FCSTD DOCUMENT  (FreeCAD 1.0RUnknown)
Label: circumlocution
License: All rights reserved
LicenseURL: http://en.wikipedia.org/wiki/All_rights_reserved
objects: Part::Feature×459, Sketcher::SketchObject×126, App::Part×76, PartDesign::Pad×49, PartDesign::Pocket×37, Part::FeaturePython×31, PartDesign::Hole×30, PartDesign::Body×27, Part::Extrusion×10, PartDesign::CoordinateSystem×4, PartDesign::ShapeBinder×2, PartDesign::Mirrored×2, Part::Cut×2, Part::Fuse×1, PartDesign::Fillet×1, Part::Mirroring×1, Part::MultiFuse×1
note: 1145 computed .brp shape members not serialized (recipe doc carries the construction recipe); baked Part::Feature solids carry a one-line shape summary decoded from their .brp

FEATURE [Sketcher::SketchObject] Sketch  label="2020LinearExtrusion"
  ArcFitTolerance = 1e-06
  FullyConstrained = true
  MakeInternals = false
  Placement = pos=(0,0,0) rot=(0,0,1;1.5708rad)
  sketch-geometry (115):
    g0: GeomPoint [constr] X=0 Y=0 Z=0
    g1: ArcOfCircle CenterX=-8.5 CenterY=8.5 CenterZ=0 NormalX=0 NormalY=0 NormalZ=1 AngleXU=0 Radius=1.5 StartAngle=1.5708 EndAngle=3.14159
    g2: GeomPoint [constr] X=-10 Y=10 Z=0
    g3: ArcOfCircle CenterX=-8.5 CenterY=-8.5 CenterZ=0 NormalX=0 NormalY=0 NormalZ=1 AngleXU=0 Radius=1.5 StartAngle=3.14159 EndAngle=4.71239
    g4: GeomPoint [constr] X=-10 Y=-10 Z=0
    g5: ArcOfCircle CenterX=8.5 CenterY=-8.5 CenterZ=0 NormalX=0 NormalY=0 NormalZ=1 AngleXU=0 Radius=1.5 StartAngle=4.71239 EndAngle=6.28319
    g6: GeomPoint [constr] X=10 Y=-10 Z=0
    g7: ArcOfCircle CenterX=8.5 CenterY=8.5 CenterZ=0 NormalX=0 NormalY=0 NormalZ=1 AngleXU=0 Radius=1.5 StartAngle=0 EndAngle=1.5708
    g8: GeomPoint [constr] X=10 Y=10 Z=0
    g9: ArcOfCircle CenterX=0 CenterY=0 CenterZ=0 NormalX=0 NormalY=0 NormalZ=1 AngleXU=0 Radius=2.75 StartAngle=5.79106 EndAngle=6.77531
    g10: LineSegment StartX=1.88798 StartY=-3.01227 StartZ=0 EndX=3.01227 EndY=-1.88798 EndZ=0
    g11: LineSegment StartX=3.01227 StartY=-1.88798 StartZ=0 EndX=2.42366 EndY=-1.29936 EndZ=0
    g12: LineSegment StartX=-1.88798 StartY=3.01227 StartZ=0 EndX=-3.01227 EndY=1.88798 EndZ=0
    g13: LineSegment StartX=-3.01227 StartY=1.88798 StartZ=0 EndX=-2.42366 EndY=1.29936 EndZ=0
    g14: GeomPoint [constr] X=0 Y=0 Z=0
    g15: LineSegment StartX=-3.01227 StartY=-1.88798 StartZ=0 EndX=-1.88798 EndY=-3.01227 EndZ=0
    g16: LineSegment StartX=-1.88798 StartY=-3.01227 StartZ=0 EndX=-1.29936 EndY=-2.42366 EndZ=0
    g17: LineSegment StartX=3.01227 StartY=1.88798 StartZ=0 EndX=1.88798 EndY=3.01227 EndZ=0
    g18: LineSegment StartX=1.88798 StartY=3.01227 StartZ=0 EndX=1.29936 EndY=2.42366 EndZ=0
    g19: GeomPoint [constr] X=0 Y=0 Z=0
    g20: LineSegment StartX=-1.29936 StartY=2.42366 StartZ=0 EndX=-1.88798 EndY=3.01227 EndZ=0
    g21: LineSegment StartX=1.29936 StartY=-2.42366 StartZ=0 EndX=1.88798 EndY=-3.01227 EndZ=0
    g22: ArcOfCircle CenterX=0 CenterY=0 CenterZ=0 NormalX=0 NormalY=0 NormalZ=1 AngleXU=0 Radius=2.75 StartAngle=2.64947 EndAngle=3.63371
    g23: ArcOfCircle CenterX=0 CenterY=0 CenterZ=0 NormalX=0 NormalY=0 NormalZ=1 AngleXU=0 Radius=2.75 StartAngle=4.22027 EndAngle=5.20451
    g24: ArcOfCircle CenterX=0 CenterY=0 CenterZ=0 NormalX=0 NormalY=0 NormalZ=1 AngleXU=0 Radius=2.75 StartAngle=1.07868 EndAngle=2.06292
    g25: LineSegment StartX=-2.42366 StartY=-1.29936 StartZ=0 EndX=-3.01227 EndY=-1.88798 EndZ=0
    g26: LineSegment StartX=2.42366 StartY=1.29936 StartZ=0 EndX=3.01227 EndY=1.88798 EndZ=0
    g27: LineSegment [constr] StartX=-1.29936 StartY=2.42366 StartZ=0 EndX=2.42366 EndY=-1.29936 EndZ=0
    g28: LineSegment [constr] StartX=1.29936 StartY=-2.42366 StartZ=0 EndX=-2.42366 EndY=1.29936 EndZ=0
    g29: LineSegment [constr] StartX=-2.42366 StartY=-1.29936 StartZ=0 EndX=1.29936 EndY=2.42366 EndZ=0
    g30: LineSegment [constr] StartX=2.42366 StartY=1.29936 StartZ=0 EndX=-1.29936 EndY=-2.42366 EndZ=0
    g31: LineSegment StartX=-3.46967 StartY=-4.53033 StartZ=0 EndX=-0.800312 EndY=-4.53033 EndZ=0
    g32: LineSegment StartX=4.53033 StartY=-3.46967 StartZ=0 EndX=4.53033 EndY=-0.800312 EndZ=0
    g33: LineSegment StartX=3.46967 StartY=4.53033 StartZ=0 EndX=0.800312 EndY=4.53033 EndZ=0
    g34: LineSegment StartX=-4.53033 StartY=3.46967 StartZ=0 EndX=-4.53033 EndY=0.800312 EndZ=0
    g35: GeomPoint [constr] X=0 Y=0 Z=0
    g36: LineSegment StartX=-3.46967 StartY=4.53033 StartZ=0 EndX=-5.95 EndY=7.01066 EndZ=0
    g37: LineSegment StartX=-5.95 StartY=8.5 StartZ=0 EndX=-5.95 EndY=7.01066 EndZ=0
    g38: LineSegment StartX=-5.95 StartY=8.5 StartZ=0 EndX=-3 EndY=8.5 EndZ=0
    g39: LineSegment StartX=-3 StartY=8.5 StartZ=0 EndX=-3 EndY=9.5 EndZ=0
    g40: LineSegment StartX=-3 StartY=9.5 StartZ=0 EndX=-3.5 EndY=9.5 EndZ=0
    g41: LineSegment StartX=-3.5 StartY=9.5 StartZ=0 EndX=-3.5 EndY=10 EndZ=0
    g42: LineSegment StartX=-3.5 StartY=10 StartZ=0 EndX=-8.5 EndY=10 EndZ=0
    g43: ArcOfCircle CenterX=-4.75033 CenterY=0 CenterZ=0 NormalX=0 NormalY=0 NormalZ=1 AngleXU=0 Radius=0.83 StartAngle=4.98066 EndAngle=7.58572
    g44: LineSegment [constr] StartX=-4.75033 StartY=0 StartZ=0 EndX=-3.92033 EndY=0 EndZ=0
    g45: LineSegment StartX=-4.53033 StartY=-0.800312 StartZ=0 EndX=-4.53033 EndY=-3.46967 EndZ=0
    g46: LineSegment [constr] StartX=-4.53033 StartY=0.800312 StartZ=0 EndX=-4.53033 EndY=-0.800312 EndZ=0
    g47: LineSegment [constr] StartX=-10 StartY=10 StartZ=0 EndX=10 EndY=10 EndZ=0
    g48: LineSegment [constr] StartX=10 StartY=10 StartZ=0 EndX=10 EndY=-10 EndZ=0
    g49: LineSegment [constr] StartX=10 StartY=-10 StartZ=0 EndX=-10 EndY=-10 EndZ=0
    g50: LineSegment [constr] StartX=-10 StartY=-10 StartZ=0 EndX=-10 EndY=10 EndZ=0
    g51: LineSegment [constr] StartX=-8.5 StartY=8.5 StartZ=0 EndX=-10 EndY=8.5 EndZ=0
    g52: LineSegment [constr] StartX=-8.5 StartY=10 StartZ=0 EndX=-8.5 EndY=8.5 EndZ=0
    g53: LineSegment [constr] StartX=-10 StartY=10 StartZ=0 EndX=10 EndY=-10 EndZ=0
    g54: LineSegment [constr] StartX=10 StartY=10 StartZ=0 EndX=-10 EndY=-10 EndZ=0
    g55: LineSegment StartX=-10 StartY=3.5 StartZ=0 EndX=-10 EndY=8.5 EndZ=0
    g56: LineSegment StartX=-9.5 StartY=3.5 StartZ=0 EndX=-10 EndY=3.5 EndZ=0
    g57: LineSegment StartX=-9.5 StartY=3 StartZ=0 EndX=-9.5 EndY=3.5 EndZ=0
    g58: LineSegment StartX=-8.5 StartY=3 StartZ=0 EndX=-9.5 EndY=3 EndZ=0
    g59: LineSegment StartX=-8.5 StartY=5.95 StartZ=0 EndX=-8.5 EndY=3 EndZ=0
    g60: LineSegment StartX=-8.5 StartY=5.95 StartZ=0 EndX=-7.01066 EndY=5.95 EndZ=0
    g61: LineSegment StartX=-4.53033 StartY=3.46967 StartZ=0 EndX=-7.01066 EndY=5.95 EndZ=0
    g62: LineSegment StartX=3.5 StartY=10 StartZ=0 EndX=8.5 EndY=10 EndZ=0
    g63: LineSegment StartX=3.5 StartY=9.5 StartZ=0 EndX=3.5 EndY=10 EndZ=0
    g64: LineSegment StartX=3 StartY=8.5 StartZ=0 EndX=3 EndY=9.5 EndZ=0
    g65: LineSegment StartX=3 StartY=9.5 StartZ=0 EndX=3.5 EndY=9.5 EndZ=0
    g66: LineSegment StartX=5.95 StartY=8.5 StartZ=0 EndX=3 EndY=8.5 EndZ=0
    g67: LineSegment StartX=5.95 StartY=8.5 StartZ=0 EndX=5.95 EndY=7.01066 EndZ=0
    g68: LineSegment StartX=3.46967 StartY=4.53033 StartZ=0 EndX=5.95 EndY=7.01066 EndZ=0
    g69: LineSegment StartX=4.53033 StartY=3.46967 StartZ=0 EndX=7.01066 EndY=5.95 EndZ=0
    g70: LineSegment StartX=8.5 StartY=5.95 StartZ=0 EndX=7.01066 EndY=5.95 EndZ=0
    g71: LineSegment StartX=8.5 StartY=5.95 StartZ=0 EndX=8.5 EndY=3 EndZ=0
    g72: LineSegment StartX=8.5 StartY=3 StartZ=0 EndX=9.5 EndY=3 EndZ=0
    g73: LineSegment StartX=9.5 StartY=3 StartZ=0 EndX=9.5 EndY=3.5 EndZ=0
    g74: LineSegment StartX=9.5 StartY=3.5 StartZ=0 EndX=10 EndY=3.5 EndZ=0
    g75: LineSegment StartX=10 StartY=3.5 StartZ=0 EndX=10 EndY=8.5 EndZ=0
    g76: LineSegment StartX=-3.5 StartY=-10 StartZ=0 EndX=-8.5 EndY=-10 EndZ=0
    g77: LineSegment StartX=-3.5 StartY=-9.5 StartZ=0 EndX=-3.5 EndY=-10 EndZ=0
    g78: LineSegment StartX=-3 StartY=-9.5 StartZ=0 EndX=-3.5 EndY=-9.5 EndZ=0
    g79: LineSegment StartX=-3 StartY=-8.5 StartZ=0 EndX=-3 EndY=-9.5 EndZ=0
    g80: LineSegment StartX=-5.95 StartY=-8.5 StartZ=0 EndX=-3 EndY=-8.5 EndZ=0
    g81: LineSegment StartX=-5.95 StartY=-8.5 StartZ=0 EndX=-5.95 EndY=-7.01066 EndZ=0
    g82: LineSegment StartX=-3.46967 StartY=-4.53033 StartZ=0 EndX=-5.95 EndY=-7.01066 EndZ=0
    g83: LineSegment StartX=-4.53033 StartY=-3.46967 StartZ=0 EndX=-7.01066 EndY=-5.95 EndZ=0
    g84: LineSegment StartX=-8.5 StartY=-5.95 StartZ=0 EndX=-7.01066 EndY=-5.95 EndZ=0
    g85: LineSegment StartX=-8.5 StartY=-5.95 StartZ=0 EndX=-8.5 EndY=-3 EndZ=0
    g86: LineSegment StartX=-8.5 StartY=-3 StartZ=0 EndX=-9.5 EndY=-3 EndZ=0
    g87: LineSegment StartX=-9.5 StartY=-3 StartZ=0 EndX=-9.5 EndY=-3.5 EndZ=0
    g88: LineSegment StartX=-9.5 StartY=-3.5 StartZ=0 EndX=-10 EndY=-3.5 EndZ=0
    g89: LineSegment StartX=-10 StartY=-3.5 StartZ=0 EndX=-10 EndY=-8.5 EndZ=0
    g90: LineSegment StartX=3.5 StartY=-10 StartZ=0 EndX=8.5 EndY=-10 EndZ=0
    g91: LineSegment StartX=3.5 StartY=-9.5 StartZ=0 EndX=3.5 EndY=-10 EndZ=0
    g92: LineSegment StartX=3 StartY=-9.5 StartZ=0 EndX=3.5 EndY=-9.5 EndZ=0
    g93: LineSegment StartX=3 StartY=-8.5 StartZ=0 EndX=3 EndY=-9.5 EndZ=0
    g94: LineSegment StartX=5.95 StartY=-8.5 StartZ=0 EndX=3 EndY=-8.5 EndZ=0
    g95: LineSegment StartX=5.95 StartY=-8.5 StartZ=0 EndX=5.95 EndY=-7.01066 EndZ=0
    g96: LineSegment StartX=3.46967 StartY=-4.53033 StartZ=0 EndX=5.95 EndY=-7.01066 EndZ=0
    g97: LineSegment StartX=4.53033 StartY=-3.46967 StartZ=0 EndX=7.01066 EndY=-5.95 EndZ=0
    g98: LineSegment StartX=8.5 StartY=-5.95 StartZ=0 EndX=7.01066 EndY=-5.95 EndZ=0
    g99: LineSegment StartX=8.5 StartY=-5.95 StartZ=0 EndX=8.5 EndY=-3 EndZ=0
    g100: LineSegment StartX=8.5 StartY=-3 StartZ=0 EndX=9.5 EndY=-3 EndZ=0
    g101: LineSegment StartX=9.5 StartY=-3 StartZ=0 EndX=9.5 EndY=-3.5 EndZ=0
    g102: LineSegment StartX=9.5 StartY=-3.5 StartZ=0 EndX=10 EndY=-3.5 EndZ=0
    g103: LineSegment StartX=10 StartY=-3.5 StartZ=0 EndX=10 EndY=-8.5 EndZ=0
    g104: GeomPoint [constr] X=-4 Y=4 Z=0
    g105: GeomPoint [constr] X=4 Y=4 Z=0
    g106: ArcOfCircle CenterX=4.75033 CenterY=0 CenterZ=0 NormalX=0 NormalY=0 NormalZ=1 AngleXU=0 Radius=0.83 StartAngle=1.83906 EndAngle=4.44412
    g107: ArcOfCircle CenterX=-1e-16 CenterY=4.75033 CenterZ=0 NormalX=0 NormalY=0 NormalZ=1 AngleXU=0 Radius=0.83 StartAngle=3.40986 EndAngle=6.01492
    g108: ArcOfCircle CenterX=3e-16 CenterY=-4.75033 CenterZ=0 NormalX=0 NormalY=0 NormalZ=1 AngleXU=0 Radius=0.83 StartAngle=0.268266 EndAngle=2.87333
    g109: LineSegment StartX=-0.800312 StartY=4.53033 StartZ=0 EndX=-3.46967 EndY=4.53033 EndZ=0
    g110: LineSegment StartX=4.53033 StartY=0.800312 StartZ=0 EndX=4.53033 EndY=3.46967 EndZ=0
    g111: LineSegment StartX=0.800312 StartY=-4.53033 StartZ=0 EndX=3.46967 EndY=-4.53033 EndZ=0
    g112: LineSegment [constr] StartX=-0.800312 StartY=4.53033 StartZ=0 EndX=0.800312 EndY=4.53033 EndZ=0
    g113: LineSegment [constr] StartX=4.53033 StartY=0.800312 StartZ=0 EndX=4.53033 EndY=-0.800312 EndZ=0
    g114: LineSegment [constr] StartX=0.800312 StartY=-4.53033 StartZ=0 EndX=-0.800312 EndY=-4.53033 EndZ=0
  constraints (276):
    c: Symmetric(g8,g4,g0)
    c: Distance(g6,g4) = 20
    c: Distance(g4,g2) = 20
    c: Coincident(g0,g-1)
    c: Radius(g1) = 1.5
    c: Equal(g1,g3)
    c: Equal(g1,g7)
    c: Equal(g1,g5)
    c: Diameter(g9) = 5.5
    c: Coincident(g9,g0)
    c: Coincident(g10,g11)
    c: Coincident(g20,g12)
    c: Coincident(g12,g13)
    c: Coincident(g21,g10)
    c: Symmetric(g12,g10,g14)
    c: Distance(g11,g21) = 1.59
    c: Distance(g10,g12) = 6.93
    c: Coincident(g14,g0)
    c: Perpendicular(g12,g13)
    c: Perpendicular(g11,g10)
    c: Equal(g10,g12)
    c: Angle(g13,g-1) = 0.785398
    c: Coincident(g15,g16)
    c: Coincident(g26,g17)
    c: Coincident(g17,g18)
    c: Coincident(g25,g15)
    c: Symmetric(g17,g15,g19)
    c: Coincident(g19,g0)
    c: Equal(g17,g15)
    c: Perpendicular(g18,g15)
    c: Perpendicular(g16,g17)
    c: Angle(g18,g-2) = 0.785398
    c: Equal(g12,g15)
    c: PointOnObject(g23,g21)
    c: Coincident(g9,g11)
    c: PointOnObject(g21,g23)
    c: PointOnObject(g13,g22)
    c: Equal(g9,g22)
    c: Coincident(g24,g20)
    c: PointOnObject(g22,g13)
    c: Coincident(g9,g22)
    c: Equal(g22,g23)
    c: PointOnObject(g22,g25)
    c: Coincident(g22,g23)
    c: Equal(g9,g24)
    c: PointOnObject(g9,g26)
    c: Coincident(g9,g24)
    c: Coincident(g18,g24)
    c: PointOnObject(g25,g22)
    c: Coincident(g16,g23)
    c: PointOnObject(g26,g9)
    c: Coincident(g27,g20)
    c: Coincident(g27,g9)
    c: Coincident(g28,g21)
    c: Coincident(g28,g13)
    c: Coincident(g29,g18)
    c: Coincident(g30,g9)
    c: Coincident(g30,g16)
    c: Parallel(g21,g28)
    c: Parallel(g27,g20)
    c: Parallel(g29,g18)
    c: Parallel(g26,g30)
    c: Parallel(g30,g16)
    c: Parallel(g25,g29)
    c: Coincident(g29,g22)
    c: Parallel(g13,g28)
    c: Parallel(g11,g27)
    c: Equal(g20,g18)
    c: Horizontal(g31)
    c: Horizontal(g33)
    c: Vertical(g32)
    c: Vertical(g34)
    c: Coincident(g35,g0)
    c: Coincident(g37,g36)
    c: Vertical(g37)
    c: Coincident(g38,g37)
    c: Horizontal(g38)
    c: Coincident(g39,g38)
    c: Vertical(g39)
    c: Coincident(g40,g39)
    c: Horizontal(g40)
    c: Vertical(g41)
    c: Coincident(g42,g41)
    c: Coincident(g42,g1)
    c: Horizontal(g42)
    c: Diameter(g43) = 1.66
    c: Coincident(g44,g43)
    c: PointOnObject(g44,g43)
    c: Horizontal(g44)
    c: Distance(g44,g34) = 0.61
    c: PointOnObject(g43,g-1)
    c: Coincident(g34,g43)
    c: Coincident(g45,g43)
    c: Vertical(g45)
    c: Coincident(g46,g34)
    c: Coincident(g46,g43)
    c: Vertical(g46)
    c: DistanceY(g41,g41) = 0.5
    c: Coincident(g41,g40)
    c: DistanceY(g38,g41) = 1.5
    c: Coincident(g47,g2)
    c: Coincident(g47,g8)
    c: Horizontal(g47)
    c: Coincident(g48,g8)
    c: Coincident(g48,g6)
    c: Vertical(g48)
    c: Tangent(g48,g7)
    c: Coincident(g49,g6)
    c: Coincident(g49,g4)
    c: Horizontal(g49)
    c: Coincident(g50,g4)
    c: Coincident(g50,g2)
    c: Vertical(g50)
    c: Tangent(g3,g50) = 1.5708
    c: Tangent(g3,g49) = 1.5708
    c: PointOnObject(g5,g49)
    c: Tangent(g49,g5,g5) = 1.5708
    c: PointOnObject(g5,g48)
    c: Tangent(g48,g5,g5) = 1.5708
    c: Tangent(g48,g7,g7) = 1.5708
    c: PointOnObject(g1,g47)
    c: PointOnObject(g1,g50)
    c: Tangent(g7,g47) = 1.5708
    c: Coincident(g51,g1)
    c: Coincident(g51,g1)
    c: Horizontal(g51)
    c: Coincident(g52,g1)
    c: Coincident(g52,g1)
    c: Vertical(g52)
    c: DistanceX(g38,g38) = 2.95
    c: DistanceX(g2,g37) = 4.05
    c: Coincident(g53,g2)
    c: Coincident(g53,g6)
    c: Coincident(g54,g8)
    c: Coincident(g54,g4)
    c: Symmetric(g36,g61,g53)
    c: Symmetric(g37,g60,g53)
    c: Symmetric(g37,g60,g53)
    c: Symmetric(g38,g59,g53)
    c: Symmetric(g38,g59,g53)
    c: Symmetric(g39,g58,g53)
    c: Symmetric(g39,g58,g53)
    c: Symmetric(g40,g57,g53)
    c: Symmetric(g40,g57,g53)
    c: Symmetric(g41,g56,g53)
    c: Symmetric(g41,g56,g53)
    c: Symmetric(g42,g55,g53)
    c: Symmetric(g42,g55,g53)
    c: Symmetric(g36,g68,g-2)
    c: Symmetric(g37,g67,g-2)
    c: Symmetric(g37,g67,g-2)
    c: Symmetric(g38,g66,g-2)
    c: Symmetric(g38,g66,g-2)
    c: Symmetric(g39,g64,g-2)
    c: Symmetric(g39,g64,g-2)
    c: Symmetric(g40,g65,g-2)
    c: Symmetric(g40,g65,g-2)
    c: Symmetric(g41,g63,g-2)
    c: Symmetric(g41,g63,g-2)
    c: Symmetric(g42,g62,g-2)
    c: Symmetric(g42,g62,g-2)
    c: Symmetric(g55,g75,g-2)
    c: Symmetric(g55,g75,g-2)
    c: Symmetric(g56,g74,g-2)
    c: Symmetric(g56,g74,g-2)
    c: Symmetric(g57,g73,g-2)
    c: Symmetric(g57,g73,g-2)
    c: Symmetric(g58,g72,g-2)
    c: Symmetric(g58,g72,g-2)
    c: Symmetric(g59,g71,g-2)
    c: Symmetric(g59,g71,g-2)
    c: Symmetric(g60,g70,g-2)
    c: Symmetric(g60,g70,g-2)
    c: Symmetric(g61,g69,g-2)
    c: Symmetric(g36,g82,g-1)
    c: Symmetric(g37,g81,g-1)
    c: Symmetric(g37,g81,g-1)
    c: Symmetric(g38,g80,g-1)
    c: Symmetric(g38,g80,g-1)
    c: Symmetric(g39,g79,g-1)
    c: Symmetric(g39,g79,g-1)
    c: Symmetric(g40,g78,g-1)
    c: Symmetric(g40,g78,g-1)
    c: Symmetric(g41,g77,g-1)
    c: Symmetric(g41,g77,g-1)
    c: Symmetric(g42,g76,g-1)
    c: Symmetric(g42,g76,g-1)
    c: Symmetric(g55,g89,g-1)
    c: Symmetric(g55,g89,g-1)
    c: Symmetric(g56,g88,g-1)
    c: Symmetric(g56,g88,g-1)
    c: Symmetric(g57,g87,g-1)
    c: Symmetric(g57,g87,g-1)
    c: Symmetric(g58,g86,g-1)
    c: Symmetric(g58,g86,g-1)
    c: Symmetric(g59,g85,g-1)
    c: Symmetric(g59,g85,g-1)
    c: Symmetric(g60,g84,g-1)
    c: Symmetric(g60,g84,g-1)
    c: Symmetric(g61,g83,g-1)
    c: Symmetric(g62,g90,g-1)
    c: Symmetric(g62,g90,g-1)
    c: Symmetric(g63,g91,g-1)
    c: Symmetric(g63,g91,g-1)
    c: Symmetric(g64,g93,g-1)
    c: Symmetric(g64,g93,g-1)
    c: Symmetric(g65,g92,g-1)
    c: Symmetric(g65,g92,g-1)
    c: Symmetric(g66,g94,g-1)
    c: Symmetric(g66,g94,g-1)
    c: Symmetric(g67,g95,g-1)
    c: Symmetric(g67,g95,g-1)
    c: Symmetric(g68,g96,g-1)
    c: Symmetric(g69,g97,g-1)
    c: Symmetric(g70,g98,g-1)
    c: Symmetric(g70,g98,g-1)
    c: Symmetric(g71,g99,g-1)
    c: Symmetric(g71,g99,g-1)
    c: Symmetric(g72,g100,g-1)
    c: Symmetric(g72,g100,g-1)
    c: Symmetric(g73,g101,g-1)
    c: Symmetric(g73,g101,g-1)
    c: Symmetric(g74,g102,g-1)
    c: Symmetric(g74,g102,g-1)
    c: Symmetric(g75,g103,g-1)
    c: Symmetric(g75,g103,g-1)
    c: Coincident(g111,g96)
    c: Coincident(g32,g97)
    c: Coincident(g31,g82)
    c: Coincident(g45,g83)
    c: Coincident(g61,g34)
    c: Coincident(g36,g109)
    c: Coincident(g33,g68)
    c: Coincident(g69,g110)
    c: Equal(g61,g36)
    c: Equal(g68,g69)
    c: Equal(g97,g96)
    c: Equal(g83,g82)
    c: Parallel(g20,g36)
    c: Parallel(g13,g61)
    c: Parallel(g82,g16)
    c: Parallel(g25,g83)
    c: Parallel(g96,g21)
    c: Parallel(g97,g11)
    c: Parallel(g18,g68)
    c: Symmetric(g109,g34,g104)
    c: Symmetric(g33,g110,g105)
    c: DistanceX(g104,g105) = 8
    c: Equal(g43,g106)
    c: Symmetric(g43,g106,g-2)
    c: Symmetric(g43,g106,g-2)
    c: Equal(g43,g107)
    c: Symmetric(g43,g107,g53)
    c: Symmetric(g43,g107,g53)
    c: Equal(g106,g108)
    c: Symmetric(g106,g108,g53)
    c: Symmetric(g106,g108,g53)
    c: PointOnObject(g33,g107)
    c: PointOnObject(g109,g107)
    c: PointOnObject(g32,g106)
    c: PointOnObject(g31,g108)
    c: PointOnObject(g111,g108)
    c: Coincident(g112,g107)
    c: Coincident(g112,g33)
    c: Horizontal(g112)
    c: Coincident(g113,g106)
    c: Coincident(g113,g32)
    c: Vertical(g113)
    c: Coincident(g114,g108)
    c: Coincident(g114,g31)
    c: Horizontal(g109)
    c: Vertical(g110)
    c: Horizontal(g111)
    c: Coincident(g106,g110)
    c: DistanceX(g2,g41) = 6.5
    c: Distance(g61,g36) = 1.5
FEATURE [Part::Extrusion] Extrude  label="XAxisExtrusion"
  Base = -> Sketch
  Dir = (0,0,1)
  DirMode = 2
  FaceMakerClass = Part::FaceMakerBullseye
  FaceMakerMode = 3
  LengthFwd = 400
  LengthRev = 0
  Placement = pos=(-250,129,200) rot=(0,1,0;1.5708rad)
  Solid = true
  Symmetric = false
FEATURE [Part::FeaturePython] ThreadedRod  label="M8x430-ThreadedRod"  # WARN: FeaturePython — macro-defined, semantics opaque (R4)
  Diameter = 9
  DiameterCustom = 8
  Invert = false
  LeftHanded = false
  Length = 430
  MatchOuter = false
  OffsetAngle = 0
  PitchCustom = 2
  Placement = pos=(-170,181,500) rot=(0,0,1;0rad)
  Thread = true
  Type = 4
FEATURE [Part::Feature] Part__Feature  label="rear end cap"
  shape: bbox 46.44 x 42.08 x 9.4 mm, 73 faces (baked)
FEATURE [Part::Feature] Part__Feature001  label="rear bearing"
  Placement = pos=(0,0,6.6) rot=(0,0,1;0rad)
  shape: bbox 16 x 16 x 5.05 mm, 13 faces (baked)
FEATURE [Part::Feature] Part__Feature002  label="connector"
  shape: bbox 10.8 x 15.6 x 6.2 mm, 85 faces (baked)
FEATURE [Part::Feature] Part__Feature003  label="shaft"
  Placement = pos=(0,0,2.8) rot=(0,0,1;0rad)
  shape: bbox 5 x 5 x 58 mm, 7 faces (baked)
FEATURE [Part::Feature] Part__Feature004  label="stator"
  Placement = pos=(0,0,9.4) rot=(0,0,1;0rad)
  shape: bbox 42 x 42 x 20 mm, 713 faces (baked)
FEATURE [Part::Feature] Part__Feature005  label="front end cap"
  Placement = pos=(0,0,29.4) rot=(0,0,1;0rad)
  shape: bbox 42 x 42 x 10 mm, 34 faces (baked)
FEATURE [Part::Feature] Part__Feature006  label="front bearing"
  Placement = pos=(0,0,34.6) rot=(0,1,0;3.14159rad)
  shape: bbox 16 x 16 x 5.05 mm, 13 faces (baked)
FEATURE [Part::Feature] Part__Feature007  label="M3x10-Screw"
  Placement = pos=(15.5,15.5,2) rot=(0,1,0;3.14159rad)
  shape: bbox 5.7 x 5.7 x 11.65 mm, 15 faces (baked)
FEATURE [Part::Feature] Part__Feature008  label="M3x10-Screw001"
  Placement = pos=(15.5,-15.5,2) rot=(0,1,0;3.14159rad)
  shape: bbox 5.7 x 5.7 x 11.65 mm, 15 faces (baked)
FEATURE [Part::Feature] Part__Feature009  label="M3x10-Screw002"
  Placement = pos=(-15.5,15.5,2) rot=(0,1,0;3.14159rad)
  shape: bbox 5.7 x 5.7 x 11.65 mm, 15 faces (baked)
FEATURE [Part::Feature] Part__Feature010  label="M3x10-Screw003"
  Placement = pos=(-15.5,-15.5,2) rot=(0,1,0;3.14159rad)
  shape: bbox 5.7 x 5.7 x 11.65 mm, 15 faces (baked)
FEATURE [App::Part] _7HS4401S_Stepper_Motor  label="ZMotor"
  Group = -> [Part__Feature,Part__Feature001,Part__Feature002,Part__Feature003,Part__Feature004,Part__Feature005,Part__Feature006,Part__Feature007,Part__Feature008,Part__Feature009,Part__Feature010]
  Origin = -> Origin
  Placement = pos=(-170,181,10) rot=(0,0,1;1.5708rad)
FEATURE [Sketcher::SketchObject] Sketch001  label="2040LinearExtrusion"
  ArcFitTolerance = 1e-06
  FullyConstrained = true
  MakeInternals = false
  Placement = pos=(0,0,0) rot=(0,0,1;1.5708rad)
  sketch-geometry (187):
    g0: GeomPoint [constr] X=0 Y=0 Z=0
    g1: ArcOfCircle CenterX=-8.5 CenterY=8.5 CenterZ=0 NormalX=0 NormalY=0 NormalZ=1 AngleXU=0 Radius=1.5 StartAngle=1.5708 EndAngle=3.14159
    g2: GeomPoint [constr] X=-10 Y=10 Z=0
    g3: ArcOfCircle CenterX=-8.5 CenterY=-8.5 CenterZ=0 NormalX=0 NormalY=0 NormalZ=1 AngleXU=0 Radius=1.5 StartAngle=3.14159 EndAngle=4.71239
    g4: GeomPoint [constr] X=-10 Y=-10 Z=0
    g5: GeomPoint [constr] X=10 Y=-10 Z=0
    g6: GeomPoint [constr] X=10 Y=10 Z=0
    g7: ArcOfCircle CenterX=0 CenterY=0 CenterZ=0 NormalX=0 NormalY=0 NormalZ=1 AngleXU=0 Radius=2.75 StartAngle=5.79106 EndAngle=6.77531
    g8: LineSegment StartX=1.88798 StartY=-3.01227 StartZ=0 EndX=3.01227 EndY=-1.88798 EndZ=0
    g9: LineSegment StartX=3.01227 StartY=-1.88798 StartZ=0 EndX=2.42366 EndY=-1.29936 EndZ=0
    g10: LineSegment StartX=-1.88798 StartY=3.01227 StartZ=0 EndX=-3.01227 EndY=1.88798 EndZ=0
    g11: LineSegment StartX=-3.01227 StartY=1.88798 StartZ=0 EndX=-2.42366 EndY=1.29936 EndZ=0
    g12: GeomPoint [constr] X=0 Y=0 Z=0
    g13: LineSegment StartX=-3.01227 StartY=-1.88798 StartZ=0 EndX=-1.88798 EndY=-3.01227 EndZ=0
    g14: LineSegment StartX=-1.88798 StartY=-3.01227 StartZ=0 EndX=-1.29936 EndY=-2.42366 EndZ=0
    g15: LineSegment StartX=3.01227 StartY=1.88798 StartZ=0 EndX=1.88798 EndY=3.01227 EndZ=0
    g16: LineSegment StartX=1.88798 StartY=3.01227 StartZ=0 EndX=1.29936 EndY=2.42366 EndZ=0
    g17: GeomPoint [constr] X=0 Y=0 Z=0
    g18: LineSegment StartX=-1.29936 StartY=2.42366 StartZ=0 EndX=-1.88798 EndY=3.01227 EndZ=0
    g19: LineSegment StartX=1.29936 StartY=-2.42366 StartZ=0 EndX=1.88798 EndY=-3.01227 EndZ=0
    g20: ArcOfCircle CenterX=0 CenterY=0 CenterZ=0 NormalX=0 NormalY=0 NormalZ=1 AngleXU=0 Radius=2.75 StartAngle=2.64947 EndAngle=3.63371
    g21: ArcOfCircle CenterX=0 CenterY=0 CenterZ=0 NormalX=0 NormalY=0 NormalZ=1 AngleXU=0 Radius=2.75 StartAngle=4.22027 EndAngle=5.20451
    g22: ArcOfCircle CenterX=0 CenterY=0 CenterZ=0 NormalX=0 NormalY=0 NormalZ=1 AngleXU=0 Radius=2.75 StartAngle=1.07868 EndAngle=2.06292
    g23: LineSegment StartX=-2.42366 StartY=-1.29936 StartZ=0 EndX=-3.01227 EndY=-1.88798 EndZ=0
    g24: LineSegment StartX=2.42366 StartY=1.29936 StartZ=0 EndX=3.01227 EndY=1.88798 EndZ=0
    g25: LineSegment [constr] StartX=-1.29936 StartY=2.42366 StartZ=0 EndX=2.42366 EndY=-1.29936 EndZ=0
    g26: LineSegment [constr] StartX=1.29936 StartY=-2.42366 StartZ=0 EndX=-2.42366 EndY=1.29936 EndZ=0
    g27: LineSegment [constr] StartX=-2.42366 StartY=-1.29936 StartZ=0 EndX=1.29936 EndY=2.42366 EndZ=0
    g28: LineSegment [constr] StartX=2.42366 StartY=1.29936 StartZ=0 EndX=-1.29936 EndY=-2.42366 EndZ=0
    g29: LineSegment StartX=-3.46967 StartY=-4.53033 StartZ=0 EndX=-0.800312 EndY=-4.53033 EndZ=0
    g30: LineSegment StartX=4.53033 StartY=-3.46967 StartZ=0 EndX=4.53033 EndY=-0.800312 EndZ=0
    g31: LineSegment StartX=3.46967 StartY=4.53033 StartZ=0 EndX=0.800312 EndY=4.53033 EndZ=0
    g32: LineSegment StartX=-4.53033 StartY=3.46967 StartZ=0 EndX=-4.53033 EndY=0.800312 EndZ=0
    g33: GeomPoint [constr] X=0 Y=0 Z=0
    g34: LineSegment StartX=-3.46967 StartY=4.53033 StartZ=0 EndX=-5.95 EndY=7.01066 EndZ=0
    g35: LineSegment StartX=-5.95 StartY=8.5 StartZ=0 EndX=-5.95 EndY=7.01066 EndZ=0
    g36: LineSegment StartX=-5.95 StartY=8.5 StartZ=0 EndX=-3 EndY=8.5 EndZ=0
    g37: LineSegment StartX=-3 StartY=8.5 StartZ=0 EndX=-3 EndY=9.5 EndZ=0
    g38: LineSegment StartX=-3 StartY=9.5 StartZ=0 EndX=-3.5 EndY=9.5 EndZ=0
    g39: LineSegment StartX=-3.5 StartY=9.5 StartZ=0 EndX=-3.5 EndY=10 EndZ=0
    g40: LineSegment StartX=-3.5 StartY=10 StartZ=0 EndX=-8.5 EndY=10 EndZ=0
    g41: ArcOfCircle CenterX=-4.75033 CenterY=0 CenterZ=0 NormalX=0 NormalY=0 NormalZ=1 AngleXU=0 Radius=0.83 StartAngle=4.98066 EndAngle=7.58572
    g42: LineSegment [constr] StartX=-4.75033 StartY=0 StartZ=0 EndX=-3.92033 EndY=0 EndZ=0
    g43: LineSegment StartX=-4.53033 StartY=-0.800312 StartZ=0 EndX=-4.53033 EndY=-3.46967 EndZ=0
    g44: LineSegment [constr] StartX=-4.53033 StartY=0.800312 StartZ=0 EndX=-4.53033 EndY=-0.800312 EndZ=0
    g45: LineSegment [constr] StartX=-10 StartY=10 StartZ=0 EndX=10 EndY=10 EndZ=0
    g46: LineSegment [constr] StartX=10 StartY=10 StartZ=0 EndX=10 EndY=-10 EndZ=0
    g47: LineSegment [constr] StartX=10 StartY=-10 StartZ=0 EndX=-10 EndY=-10 EndZ=0
    g48: LineSegment [constr] StartX=-10 StartY=-10 StartZ=0 EndX=-10 EndY=10 EndZ=0
    g49: LineSegment [constr] StartX=-8.5 StartY=8.5 StartZ=0 EndX=-10 EndY=8.5 EndZ=0
    g50: LineSegment [constr] StartX=-8.5 StartY=10 StartZ=0 EndX=-8.5 EndY=8.5 EndZ=0
    g51: LineSegment [constr] StartX=-10 StartY=10 StartZ=0 EndX=10 EndY=-10 EndZ=0
    g52: LineSegment [constr] StartX=10 StartY=10 StartZ=0 EndX=-10 EndY=-10 EndZ=0
    g53: LineSegment StartX=-10 StartY=3.5 StartZ=0 EndX=-10 EndY=8.5 EndZ=0
    g54: LineSegment StartX=-9.5 StartY=3.5 StartZ=0 EndX=-10 EndY=3.5 EndZ=0
    g55: LineSegment StartX=-9.5 StartY=3 StartZ=0 EndX=-9.5 EndY=3.5 EndZ=0
    g56: LineSegment StartX=-8.5 StartY=3 StartZ=0 EndX=-9.5 EndY=3 EndZ=0
    g57: LineSegment StartX=-8.5 StartY=5.95 StartZ=0 EndX=-8.5 EndY=3 EndZ=0
    g58: LineSegment StartX=-8.5 StartY=5.95 StartZ=0 EndX=-7.01066 EndY=5.95 EndZ=0
    g59: LineSegment StartX=-4.53033 StartY=3.46967 StartZ=0 EndX=-7.01066 EndY=5.95 EndZ=0
    g60: LineSegment StartX=3.5 StartY=10 StartZ=0 EndX=8.5 EndY=10 EndZ=0
    g61: LineSegment StartX=3.5 StartY=9.5 StartZ=0 EndX=3.5 EndY=10 EndZ=0
    g62: LineSegment StartX=3 StartY=8.5 StartZ=0 EndX=3 EndY=9.5 EndZ=0
    g63: LineSegment StartX=3 StartY=9.5 StartZ=0 EndX=3.5 EndY=9.5 EndZ=0
    g64: LineSegment StartX=5.95 StartY=8.5 StartZ=0 EndX=3 EndY=8.5 EndZ=0
    g65: LineSegment StartX=-3.5 StartY=-10 StartZ=0 EndX=-8.5 EndY=-10 EndZ=0
    g66: LineSegment StartX=-3.5 StartY=-9.5 StartZ=0 EndX=-3.5 EndY=-10 EndZ=0
    g67: LineSegment StartX=-3 StartY=-9.5 StartZ=0 EndX=-3.5 EndY=-9.5 EndZ=0
    g68: LineSegment StartX=-3 StartY=-8.5 StartZ=0 EndX=-3 EndY=-9.5 EndZ=0
    g69: LineSegment StartX=-5.95 StartY=-8.5 StartZ=0 EndX=-3 EndY=-8.5 EndZ=0
    g70: LineSegment StartX=-5.95 StartY=-8.5 StartZ=0 EndX=-5.95 EndY=-7.01066 EndZ=0
    g71: LineSegment StartX=-3.46967 StartY=-4.53033 StartZ=0 EndX=-5.95 EndY=-7.01066 EndZ=0
    g72: LineSegment StartX=-4.53033 StartY=-3.46967 StartZ=0 EndX=-7.01066 EndY=-5.95 EndZ=0
    g73: LineSegment StartX=-8.5 StartY=-5.95 StartZ=0 EndX=-7.01066 EndY=-5.95 EndZ=0
    g74: LineSegment StartX=-8.5 StartY=-5.95 StartZ=0 EndX=-8.5 EndY=-3 EndZ=0
    g75: LineSegment StartX=-8.5 StartY=-3 StartZ=0 EndX=-9.5 EndY=-3 EndZ=0
    g76: LineSegment StartX=-9.5 StartY=-3 StartZ=0 EndX=-9.5 EndY=-3.5 EndZ=0
    g77: LineSegment StartX=-9.5 StartY=-3.5 StartZ=0 EndX=-10 EndY=-3.5 EndZ=0
    g78: LineSegment StartX=-10 StartY=-3.5 StartZ=0 EndX=-10 EndY=-8.5 EndZ=0
    g79: LineSegment StartX=3.5 StartY=-10 StartZ=0 EndX=8.5 EndY=-10 EndZ=0
    g80: LineSegment StartX=3.5 StartY=-9.5 StartZ=0 EndX=3.5 EndY=-10 EndZ=0
    g81: LineSegment StartX=3 StartY=-9.5 StartZ=0 EndX=3.5 EndY=-9.5 EndZ=0
    g82: LineSegment StartX=3 StartY=-8.5 StartZ=0 EndX=3 EndY=-9.5 EndZ=0
    g83: LineSegment StartX=5.95 StartY=-8.5 StartZ=0 EndX=3 EndY=-8.5 EndZ=0
    g84: LineSegment StartX=5.95 StartY=-8.5 StartZ=0 EndX=5.95 EndY=-7.01066 EndZ=0
    g85: LineSegment StartX=3.46967 StartY=-4.53033 StartZ=0 EndX=5.95 EndY=-7.01066 EndZ=0
    g86: GeomPoint [constr] X=-4 Y=4 Z=0
    g87: GeomPoint [constr] X=4 Y=4 Z=0
    g88: ArcOfCircle CenterX=4.75033 CenterY=1e-16 CenterZ=0 NormalX=0 NormalY=0 NormalZ=1 AngleXU=0 Radius=0.83 StartAngle=1.83906 EndAngle=4.44412
    g89: ArcOfCircle CenterX=7e-16 CenterY=4.75033 CenterZ=0 NormalX=0 NormalY=0 NormalZ=1 AngleXU=0 Radius=0.83 StartAngle=3.40986 EndAngle=6.01492
    g90: ArcOfCircle CenterX=1.2e-15 CenterY=-4.75033 CenterZ=0 NormalX=0 NormalY=0 NormalZ=1 AngleXU=0 Radius=0.83 StartAngle=0.268266 EndAngle=2.87333
    g91: LineSegment StartX=-0.800312 StartY=4.53033 StartZ=0 EndX=-3.46967 EndY=4.53033 EndZ=0
    g92: LineSegment StartX=4.53033 StartY=0.800312 StartZ=0 EndX=4.53033 EndY=3.46967 EndZ=0
    g93: LineSegment StartX=0.800312 StartY=-4.53033 StartZ=0 EndX=3.46967 EndY=-4.53033 EndZ=0
    g94: LineSegment [constr] StartX=-0.800312 StartY=4.53033 StartZ=0 EndX=0.800312 EndY=4.53033 EndZ=0
    g95: LineSegment [constr] StartX=4.53033 StartY=0.800312 StartZ=0 EndX=4.53033 EndY=-0.800312 EndZ=0
    g96: LineSegment [constr] StartX=0.800312 StartY=-4.53033 StartZ=0 EndX=-0.800312 EndY=-4.53033 EndZ=0
    g97: LineSegment [constr] StartX=7.45 StartY=-8.5 StartZ=0 EndX=5.95 EndY=-8.5 EndZ=0
    g98: LineSegment StartX=4.53033 StartY=-3.46967 StartZ=0 EndX=7.45 EndY=-6.38934 EndZ=0
    g99: LineSegment StartX=7.45 StartY=-6.38934 StartZ=0 EndX=7.45 EndY=-8.5 EndZ=0
    g100: LineSegment [constr] StartX=3.46967 StartY=-4.53033 StartZ=0 EndX=4.53033 EndY=-3.46967 EndZ=0
    g101: LineSegment [constr] StartX=7.45 StartY=8.5 StartZ=0 EndX=5.95 EndY=8.5 EndZ=0
    g102: LineSegment StartX=5.95 StartY=8.5 StartZ=0 EndX=5.95 EndY=7.01066 EndZ=0
    g103: LineSegment StartX=5.95 StartY=7.01066 StartZ=0 EndX=3.46967 EndY=4.53033 EndZ=0
    g104: LineSegment StartX=7.45 StartY=8.5 StartZ=0 EndX=7.45 EndY=6.38934 EndZ=0
    g105: LineSegment StartX=7.45 StartY=6.38934 StartZ=0 EndX=4.53033 EndY=3.46967 EndZ=0
    g106: LineSegment [constr] StartX=3.46967 StartY=4.53033 StartZ=0 EndX=4.53033 EndY=3.46967 EndZ=0
    g107: ArcOfCircle CenterX=28.5 CenterY=8.5 CenterZ=0 NormalX=0 NormalY=0 NormalZ=1 AngleXU=0 Radius=1.5 StartAngle=0 EndAngle=1.5708
    g108: ArcOfCircle CenterX=28.5 CenterY=-8.5 CenterZ=0 NormalX=0 NormalY=0 NormalZ=1 AngleXU=0 Radius=1.5 StartAngle=4.71239 EndAngle=6.28319
    g109: ArcOfCircle CenterX=20 CenterY=0 CenterZ=0 NormalX=0 NormalY=0 NormalZ=1 AngleXU=0 Radius=2.75 StartAngle=2.64947 EndAngle=3.63371
    g110: LineSegment StartX=18.112 StartY=-3.01227 StartZ=0 EndX=16.9877 EndY=-1.88798 EndZ=0
    g111: LineSegment StartX=16.9877 StartY=-1.88798 StartZ=0 EndX=17.5763 EndY=-1.29936 EndZ=0
    g112: LineSegment StartX=21.888 StartY=3.01227 StartZ=0 EndX=23.0123 EndY=1.88798 EndZ=0
    g113: LineSegment StartX=23.0123 StartY=1.88798 StartZ=0 EndX=22.4237 EndY=1.29936 EndZ=0
    g114: LineSegment StartX=23.0123 StartY=-1.88798 StartZ=0 EndX=21.888 EndY=-3.01227 EndZ=0
    g115: LineSegment StartX=21.888 StartY=-3.01227 StartZ=0 EndX=21.2994 EndY=-2.42366 EndZ=0
    g116: LineSegment StartX=16.9877 StartY=1.88798 StartZ=0 EndX=18.112 EndY=3.01227 EndZ=0
    g117: LineSegment StartX=18.112 StartY=3.01227 StartZ=0 EndX=18.7006 EndY=2.42366 EndZ=0
    g118: LineSegment StartX=21.2994 StartY=2.42366 StartZ=0 EndX=21.888 EndY=3.01227 EndZ=0
    g119: LineSegment StartX=18.7006 StartY=-2.42366 StartZ=0 EndX=18.112 EndY=-3.01227 EndZ=0
    g120: ArcOfCircle CenterX=20 CenterY=0 CenterZ=0 NormalX=0 NormalY=0 NormalZ=1 AngleXU=0 Radius=2.75 StartAngle=5.79106 EndAngle=6.77531
    g121: ArcOfCircle CenterX=20 CenterY=0 CenterZ=0 NormalX=0 NormalY=0 NormalZ=1 AngleXU=0 Radius=2.75 StartAngle=4.22027 EndAngle=5.20451
    g122: ArcOfCircle CenterX=20 CenterY=0 CenterZ=0 NormalX=0 NormalY=0 NormalZ=1 AngleXU=0 Radius=2.75 StartAngle=1.07868 EndAngle=2.06292
    g123: LineSegment StartX=22.4237 StartY=-1.29936 StartZ=0 EndX=23.0123 EndY=-1.88798 EndZ=0
    g124: LineSegment StartX=17.5763 StartY=1.29936 StartZ=0 EndX=16.9877 EndY=1.88798 EndZ=0
    g125: LineSegment StartX=23.4697 StartY=-4.53033 StartZ=0 EndX=20.8003 EndY=-4.53033 EndZ=0
    g126: LineSegment StartX=15.4697 StartY=-3.46967 StartZ=0 EndX=15.4697 EndY=-0.800312 EndZ=0
    g127: LineSegment StartX=16.5303 StartY=4.53033 StartZ=0 EndX=19.1997 EndY=4.53033 EndZ=0
    g128: LineSegment StartX=24.5303 StartY=3.46967 StartZ=0 EndX=24.5303 EndY=0.800312 EndZ=0
    g129: LineSegment StartX=23.4697 StartY=4.53033 StartZ=0 EndX=25.95 EndY=7.01066 EndZ=0
    g130: LineSegment StartX=25.95 StartY=8.5 StartZ=0 EndX=25.95 EndY=7.01066 EndZ=0
    g131: LineSegment StartX=25.95 StartY=8.5 StartZ=0 EndX=23 EndY=8.5 EndZ=0
    g132: LineSegment StartX=23 StartY=8.5 StartZ=0 EndX=23 EndY=9.5 EndZ=0
    g133: LineSegment StartX=23 StartY=9.5 StartZ=0 EndX=23.5 EndY=9.5 EndZ=0
    g134: LineSegment StartX=23.5 StartY=9.5 StartZ=0 EndX=23.5 EndY=10 EndZ=0
    g135: LineSegment StartX=23.5 StartY=10 StartZ=0 EndX=28.5 EndY=10 EndZ=0
    g136: ArcOfCircle CenterX=24.7503 CenterY=0 CenterZ=0 NormalX=0 NormalY=0 NormalZ=1 AngleXU=0 Radius=0.83 StartAngle=1.83906 EndAngle=4.44412
    g137: LineSegment StartX=24.5303 StartY=-0.800312 StartZ=0 EndX=24.5303 EndY=-3.46967 EndZ=0
    g138: LineSegment StartX=30 StartY=3.5 StartZ=0 EndX=30 EndY=8.5 EndZ=0
    g139: LineSegment StartX=29.5 StartY=3.5 StartZ=0 EndX=30 EndY=3.5 EndZ=0
    g140: LineSegment StartX=29.5 StartY=3 StartZ=0 EndX=29.5 EndY=3.5 EndZ=0
    g141: LineSegment StartX=28.5 StartY=3 StartZ=0 EndX=29.5 EndY=3 EndZ=0
    g142: LineSegment StartX=28.5 StartY=5.95 StartZ=0 EndX=28.5 EndY=3 EndZ=0
    g143: LineSegment StartX=28.5 StartY=5.95 StartZ=0 EndX=27.0107 EndY=5.95 EndZ=0
    g144: LineSegment StartX=24.5303 StartY=3.46967 StartZ=0 EndX=27.0107 EndY=5.95 EndZ=0
    g145: LineSegment StartX=16.5 StartY=10 StartZ=0 EndX=11.5 EndY=10 EndZ=0
    g146: LineSegment StartX=16.5 StartY=9.5 StartZ=0 EndX=16.5 EndY=10 EndZ=0
    g147: LineSegment StartX=17 StartY=8.5 StartZ=0 EndX=17 EndY=9.5 EndZ=0
    g148: LineSegment StartX=17 StartY=9.5 StartZ=0 EndX=16.5 EndY=9.5 EndZ=0
    g149: LineSegment StartX=14.05 StartY=8.5 StartZ=0 EndX=17 EndY=8.5 EndZ=0
    g150: LineSegment StartX=23.5 StartY=-10 StartZ=0 EndX=28.5 EndY=-10 EndZ=0
    g151: LineSegment StartX=23.5 StartY=-9.5 StartZ=0 EndX=23.5 EndY=-10 EndZ=0
    g152: LineSegment StartX=23 StartY=-9.5 StartZ=0 EndX=23.5 EndY=-9.5 EndZ=0
    g153: LineSegment StartX=23 StartY=-8.5 StartZ=0 EndX=23 EndY=-9.5 EndZ=0
    g154: LineSegment StartX=25.95 StartY=-8.5 StartZ=0 EndX=23 EndY=-8.5 EndZ=0
    g155: LineSegment StartX=25.95 StartY=-8.5 StartZ=0 EndX=25.95 EndY=-7.01066 EndZ=0
    g156: LineSegment StartX=23.4697 StartY=-4.53033 StartZ=0 EndX=25.95 EndY=-7.01066 EndZ=0
    g157: LineSegment StartX=24.5303 StartY=-3.46967 StartZ=0 EndX=27.0107 EndY=-5.95 EndZ=0
    g158: LineSegment StartX=28.5 StartY=-5.95 StartZ=0 EndX=27.0107 EndY=-5.95 EndZ=0
    g159: LineSegment StartX=28.5 StartY=-5.95 StartZ=0 EndX=28.5 EndY=-3 EndZ=0
    g160: LineSegment StartX=28.5 StartY=-3 StartZ=0 EndX=29.5 EndY=-3 EndZ=0
    g161: LineSegment StartX=29.5 StartY=-3 StartZ=0 EndX=29.5 EndY=-3.5 EndZ=0
    g162: LineSegment StartX=29.5 StartY=-3.5 StartZ=0 EndX=30 EndY=-3.5 EndZ=0
    g163: LineSegment StartX=30 StartY=-3.5 StartZ=0 EndX=30 EndY=-8.5 EndZ=0
    g164: LineSegment StartX=16.5 StartY=-10 StartZ=0 EndX=11.5 EndY=-10 EndZ=0
    g165: LineSegment StartX=16.5 StartY=-9.5 StartZ=0 EndX=16.5 EndY=-10 EndZ=0
    g166: LineSegment StartX=17 StartY=-9.5 StartZ=0 EndX=16.5 EndY=-9.5 EndZ=0
    g167: LineSegment StartX=17 StartY=-8.5 StartZ=0 EndX=17 EndY=-9.5 EndZ=0
    g168: LineSegment StartX=14.05 StartY=-8.5 StartZ=0 EndX=17 EndY=-8.5 EndZ=0
    g169: LineSegment StartX=14.05 StartY=-8.5 StartZ=0 EndX=14.05 EndY=-7.01066 EndZ=0
    g170: LineSegment StartX=16.5303 StartY=-4.53033 StartZ=0 EndX=14.05 EndY=-7.01066 EndZ=0
    g171: ArcOfCircle CenterX=15.2497 CenterY=-1e-16 CenterZ=0 NormalX=0 NormalY=0 NormalZ=1 AngleXU=0 Radius=0.83 StartAngle=4.98066 EndAngle=7.58572
    g172: ArcOfCircle CenterX=20 CenterY=4.75033 CenterZ=0 NormalX=0 NormalY=0 NormalZ=1 AngleXU=0 Radius=0.83 StartAngle=3.40986 EndAngle=6.01492
    g173: ArcOfCircle CenterX=20 CenterY=-4.75033 CenterZ=0 NormalX=0 NormalY=0 NormalZ=1 AngleXU=0 Radius=0.83 StartAngle=0.268266 EndAngle=2.87333
    g174: LineSegment StartX=20.8003 StartY=4.53033 StartZ=0 EndX=23.4697 EndY=4.53033 EndZ=0
    g175: LineSegment StartX=15.4697 StartY=0.800312 StartZ=0 EndX=15.4697 EndY=3.46967 EndZ=0
    g176: LineSegment StartX=19.1997 StartY=-4.53033 StartZ=0 EndX=16.5303 EndY=-4.53033 EndZ=0
    g177: LineSegment StartX=15.4697 StartY=-3.46967 StartZ=0 EndX=12.55 EndY=-6.38934 EndZ=0
    g178: LineSegment StartX=12.55 StartY=-6.38934 StartZ=0 EndX=12.55 EndY=-8.5 EndZ=0
    g179: LineSegment StartX=14.05 StartY=8.5 StartZ=0 EndX=14.05 EndY=7.01066 EndZ=0
    g180: LineSegment StartX=14.05 StartY=7.01066 StartZ=0 EndX=16.5303 EndY=4.53033 EndZ=0
    g181: LineSegment StartX=12.55 StartY=8.5 StartZ=0 EndX=12.55 EndY=6.38934 EndZ=0
    g182: LineSegment StartX=12.55 StartY=6.38934 StartZ=0 EndX=15.4697 EndY=3.46967 EndZ=0
    g183: LineSegment StartX=7.45 StartY=-8.5 StartZ=0 EndX=12.55 EndY=-8.5 EndZ=0
    g184: LineSegment StartX=11.5 StartY=-10 StartZ=0 EndX=8.5 EndY=-10 EndZ=0
    g185: LineSegment StartX=8.5 StartY=10 StartZ=0 EndX=11.5 EndY=10 EndZ=0
    g186: LineSegment StartX=12.55 StartY=8.5 StartZ=0 EndX=7.45 EndY=8.5 EndZ=0
  constraints (430):
    c: Symmetric(g6,g4,g0)
    c: Distance(g5,g4) = 20
    c: Distance(g4,g2) = 20
    c: Coincident(g0,g-1)
    c: Radius(g1) = 1.5
    c: Equal(g1,g3)
    c: Diameter(g7) = 5.5
    c: Coincident(g7,g0)
    c: Coincident(g8,g9)
    c: Coincident(g18,g10)
    c: Coincident(g10,g11)
    c: Coincident(g19,g8)
    c: Symmetric(g10,g8,g12)
    c: Distance(g9,g19) = 1.59
    c: Distance(g8,g10) = 6.93
    c: Coincident(g12,g0)
    c: Perpendicular(g10,g11)
    c: Perpendicular(g9,g8)
    c: Equal(g8,g10)
    c: Angle(g11,g-1) = 0.785398
    c: Coincident(g13,g14)
    c: Coincident(g24,g15)
    c: Coincident(g15,g16)
    c: Coincident(g23,g13)
    c: Symmetric(g15,g13,g17)
    c: Coincident(g17,g0)
    c: Equal(g15,g13)
    c: Perpendicular(g16,g13)
    c: Perpendicular(g14,g15)
    c: Angle(g16,g-2) = 0.785398
    c: Equal(g10,g13)
    c: PointOnObject(g21,g19)
    c: Coincident(g7,g9)
    c: PointOnObject(g19,g21)
    c: PointOnObject(g11,g20)
    c: Equal(g7,g20)
    c: Coincident(g22,g18)
    c: PointOnObject(g20,g11)
    c: Coincident(g7,g20)
    c: Equal(g20,g21)
    c: PointOnObject(g20,g23)
    c: Coincident(g20,g21)
    c: Equal(g7,g22)
    c: PointOnObject(g7,g24)
    c: Coincident(g7,g22)
    c: Coincident(g16,g22)
    c: PointOnObject(g23,g20)
    c: Coincident(g14,g21)
    c: PointOnObject(g24,g7)
    c: Coincident(g25,g18)
    c: Coincident(g25,g7)
    c: Coincident(g26,g19)
    c: Coincident(g26,g11)
    c: Coincident(g27,g16)
    c: Coincident(g28,g7)
    c: Coincident(g28,g14)
    c: Parallel(g19,g26)
    c: Parallel(g25,g18)
    c: Parallel(g27,g16)
    c: Parallel(g24,g28)
    c: Parallel(g28,g14)
    c: Parallel(g23,g27)
    c: Coincident(g27,g20)
    c: Parallel(g11,g26)
    c: Parallel(g9,g25)
    c: Equal(g18,g16)
    c: Horizontal(g29)
    c: Horizontal(g31)
    c: Vertical(g30)
    c: Vertical(g32)
    c: Coincident(g33,g0)
    c: Coincident(g35,g34)
    c: Vertical(g35)
    c: Coincident(g36,g35)
    c: Horizontal(g36)
    c: Coincident(g37,g36)
    c: Vertical(g37)
    c: Coincident(g38,g37)
    c: Horizontal(g38)
    c: Vertical(g39)
    c: Coincident(g40,g39)
    c: Coincident(g40,g1)
    c: Horizontal(g40)
    c: Diameter(g41) = 1.66
    c: Coincident(g42,g41)
    c: PointOnObject(g42,g41)
    c: Horizontal(g42)
    c: Distance(g42,g32) = 0.61
    c: PointOnObject(g41,g-1)
    c: Coincident(g32,g41)
    c: Coincident(g43,g41)
    c: Vertical(g43)
    c: Coincident(g44,g32)
    c: Coincident(g44,g41)
    c: Vertical(g44)
    c: DistanceY(g39,g39) = 0.5
    c: Coincident(g39,g38)
    c: DistanceY(g36,g39) = 1.5
    c: Coincident(g45,g2)
    c: Coincident(g45,g6)
    c: Horizontal(g45)
    c: Coincident(g46,g6)
    c: Coincident(g46,g5)
    c: Vertical(g46)
    c: Coincident(g47,g5)
    c: Coincident(g47,g4)
    c: Horizontal(g47)
    c: Coincident(g48,g4)
    c: Coincident(g48,g2)
    c: Vertical(g48)
    c: Tangent(g3,g48) = 1.5708
    c: Tangent(g3,g47) = 1.5708
    c: PointOnObject(g1,g45)
    c: PointOnObject(g1,g48)
    c: Coincident(g49,g1)
    c: Coincident(g49,g1)
    c: Horizontal(g49)
    c: Coincident(g50,g1)
    c: Coincident(g50,g1)
    c: Vertical(g50)
    c: DistanceX(g36,g36) = 2.95
    c: DistanceX(g2,g35) = 4.05
    c: Coincident(g51,g2)
    c: Coincident(g51,g5)
    c: Coincident(g52,g6)
    c: Coincident(g52,g4)
    c: Symmetric(g34,g59,g51)
    c: Symmetric(g35,g58,g51)
    c: Symmetric(g35,g58,g51)
    c: Symmetric(g36,g57,g51)
    c: Symmetric(g36,g57,g51)
    c: Symmetric(g37,g56,g51)
    c: Symmetric(g37,g56,g51)
    c: Symmetric(g38,g55,g51)
    c: Symmetric(g38,g55,g51)
    c: Symmetric(g39,g54,g51)
    c: Symmetric(g39,g54,g51)
    c: Symmetric(g40,g53,g51)
    c: Symmetric(g40,g53,g51)
    c: Symmetric(g36,g64,g-2)
    c: Symmetric(g36,g64,g-2)
    c: Symmetric(g37,g62,g-2)
    c: Symmetric(g37,g62,g-2)
    c: Symmetric(g38,g63,g-2)
    c: Symmetric(g38,g63,g-2)
    c: Symmetric(g39,g61,g-2)
    c: Symmetric(g39,g61,g-2)
    c: Symmetric(g40,g60,g-2)
    c: Symmetric(g40,g60,g-2)
    c: Symmetric(g34,g71,g-1)
    c: Symmetric(g35,g70,g-1)
    c: Symmetric(g35,g70,g-1)
    c: Symmetric(g36,g69,g-1)
    c: Symmetric(g36,g69,g-1)
    c: Symmetric(g37,g68,g-1)
    c: Symmetric(g37,g68,g-1)
    c: Symmetric(g38,g67,g-1)
    c: Symmetric(g38,g67,g-1)
    c: Symmetric(g39,g66,g-1)
    c: Symmetric(g39,g66,g-1)
    c: Symmetric(g40,g65,g-1)
    c: Symmetric(g40,g65,g-1)
    c: Symmetric(g53,g78,g-1)
    c: Symmetric(g53,g78,g-1)
    c: Symmetric(g54,g77,g-1)
    c: Symmetric(g54,g77,g-1)
    c: Symmetric(g55,g76,g-1)
    c: Symmetric(g55,g76,g-1)
    c: Symmetric(g56,g75,g-1)
    c: Symmetric(g56,g75,g-1)
    c: Symmetric(g57,g74,g-1)
    c: Symmetric(g57,g74,g-1)
    c: Symmetric(g58,g73,g-1)
    c: Symmetric(g58,g73,g-1)
    c: Symmetric(g59,g72,g-1)
    c: Symmetric(g60,g79,g-1)
    c: Symmetric(g60,g79,g-1)
    c: Symmetric(g61,g80,g-1)
    c: Symmetric(g61,g80,g-1)
    c: Symmetric(g62,g82,g-1)
    c: Symmetric(g62,g82,g-1)
    c: Symmetric(g63,g81,g-1)
    c: Symmetric(g63,g81,g-1)
    c: Symmetric(g64,g83,g-1)
    c: Symmetric(g64,g83,g-1)
    c: Coincident(g93,g85)
    c: Coincident(g29,g71)
    c: Coincident(g43,g72)
    c: Coincident(g59,g32)
    c: Coincident(g34,g91)
    c: Equal(g59,g34)
    c: Equal(g72,g71)
    c: Parallel(g18,g34)
    c: Parallel(g11,g59)
    c: Parallel(g71,g14)
    c: Parallel(g23,g72)
    c: Parallel(g85,g19)
    c: Symmetric(g91,g32,g86)
    c: DistanceX(g86,g87) = 8
    c: Equal(g41,g88)
    c: Symmetric(g41,g88,g-2)
    c: Symmetric(g41,g88,g-2)
    c: Equal(g41,g89)
    c: Symmetric(g41,g89,g51)
    c: Symmetric(g41,g89,g51)
    c: Equal(g88,g90)
    c: Symmetric(g88,g90,g51)
    c: Symmetric(g88,g90,g51)
    c: PointOnObject(g31,g89)
    c: PointOnObject(g91,g89)
    c: PointOnObject(g30,g88)
    c: PointOnObject(g29,g90)
    c: Coincident(g94,g89)
    c: Coincident(g94,g31)
    c: Horizontal(g94)
    c: Coincident(g95,g88)
    c: Coincident(g95,g30)
    c: Vertical(g95)
    c: Coincident(g96,g90)
    c: Coincident(g96,g29)
    c: Horizontal(g91)
    c: Vertical(g92)
    c: Horizontal(g93)
    c: Coincident(g88,g92)
    c: DistanceX(g2,g39) = 6.5
    c: Distance(g59,g34) = 1.5
    c: Coincident(g97,g83)
    c: Horizontal(g97)
    c: Coincident(g98,g30)
    c: Coincident(g99,g98)
    c: Coincident(g99,g97)
    c: DistanceX(g97,g97) = 1.5
    c: Coincident(g100,g85)
    c: Coincident(g100,g30)
    c: Distance(g100,g100) = 1.5
    c: Coincident(g93,g90)
    c: Vertical(g99)
    c: Parallel(g98,g85)
    c: Coincident(g101,g64)
    c: Horizontal(g101)
    c: DistanceX(g101,g101) = 1.5
    c: Coincident(g102,g64)
    c: Vertical(g102)
    c: Coincident(g103,g102)
    c: Coincident(g103,g31)
    c: Coincident(g104,g101)
    c: Vertical(g104)
    c: Coincident(g105,g104)
    c: Coincident(g105,g92)
    c: Coincident(g106,g31)
    c: Coincident(g106,g92)
    c: Distance(g106,g106) = 1.5
    c: Parallel(g103,g105)
    c: Parallel(g16,g103)
    c: Equal(g84,g102)
    c: Equal(g104,g99)
    c: Coincident(g84,g85)
    c: Symmetric(g31,g92,g87)
    c: PointOnObject(g87,g52)
    c: Coincident(g83,g84)
    c: Equal(g1,g107)
    c: Symmetric(g1,g107,g46)
    c: Symmetric(g1,g107,g46)
    c: Equal(g3,g108)
    c: Symmetric(g3,g108,g46)
    c: Symmetric(g3,g108,g46)
    c: Equal(g7,g109)
    c: Symmetric(g7,g109,g46)
    c: Symmetric(g7,g109,g46)
    c: Symmetric(g8,g110,g46)
    c: Symmetric(g8,g110,g46)
    c: Symmetric(g9,g111,g46)
    c: Symmetric(g9,g111,g46)
    c: Symmetric(g10,g112,g46)
    c: Symmetric(g10,g112,g46)
    c: Symmetric(g11,g113,g46)
    c: Symmetric(g11,g113,g46)
    c: Symmetric(g13,g114,g46)
    c: Symmetric(g13,g114,g46)
    c: Symmetric(g14,g115,g46)
    c: Symmetric(g14,g115,g46)
    c: Symmetric(g15,g116,g46)
    c: Symmetric(g15,g116,g46)
    c: Symmetric(g16,g117,g46)
    c: Symmetric(g16,g117,g46)
    c: Symmetric(g18,g118,g46)
    c: Symmetric(g18,g118,g46)
    c: Symmetric(g19,g119,g46)
    c: Symmetric(g19,g119,g46)
    c: Equal(g20,g120)
    c: Symmetric(g20,g120,g46)
    c: Symmetric(g20,g120,g46)
    c: Equal(g21,g121)
    c: Symmetric(g21,g121,g46)
    c: Symmetric(g21,g121,g46)
    c: Equal(g22,g122)
    c: Symmetric(g22,g122,g46)
    c: Symmetric(g22,g122,g46)
    c: Symmetric(g23,g123,g46)
    c: Symmetric(g23,g123,g46)
    c: Symmetric(g24,g124,g46)
    c: Symmetric(g24,g124,g46)
    c: Symmetric(g29,g125,g46)
    c: Symmetric(g29,g125,g46)
    c: Symmetric(g30,g126,g46)
    c: Symmetric(g30,g126,g46)
    c: Symmetric(g31,g127,g46)
    c: Symmetric(g31,g127,g46)
    c: Symmetric(g32,g128,g46)
    c: Symmetric(g32,g128,g46)
    c: Symmetric(g34,g129,g46)
    c: Symmetric(g34,g129,g46)
    c: Symmetric(g35,g130,g46)
    c: Symmetric(g35,g130,g46)
    c: Symmetric(g36,g131,g46)
    c: Symmetric(g36,g131,g46)
    c: Symmetric(g37,g132,g46)
    c: Symmetric(g37,g132,g46)
    c: Symmetric(g38,g133,g46)
    c: Symmetric(g38,g133,g46)
    c: Symmetric(g39,g134,g46)
    c: Symmetric(g39,g134,g46)
    c: Symmetric(g40,g135,g46)
    c: Symmetric(g40,g135,g46)
    c: Equal(g41,g136)
    c: Symmetric(g41,g136,g46)
    c: Symmetric(g41,g136,g46)
    c: Symmetric(g43,g137,g46)
    c: Symmetric(g43,g137,g46)
    c: Symmetric(g53,g138,g46)
    c: Symmetric(g53,g138,g46)
    c: Symmetric(g54,g139,g46)
    c: Symmetric(g54,g139,g46)
    c: Symmetric(g55,g140,g46)
    c: Symmetric(g55,g140,g46)
    c: Symmetric(g56,g141,g46)
    c: Symmetric(g56,g141,g46)
    c: Symmetric(g57,g142,g46)
    c: Symmetric(g57,g142,g46)
    c: Symmetric(g58,g143,g46)
    c: Symmetric(g58,g143,g46)
    c: Symmetric(g59,g144,g46)
    c: Symmetric(g59,g144,g46)
    c: Symmetric(g60,g145,g46)
    c: Symmetric(g60,g145,g46)
    c: Symmetric(g61,g146,g46)
    c: Symmetric(g61,g146,g46)
    c: Symmetric(g62,g147,g46)
    c: Symmetric(g62,g147,g46)
    c: Symmetric(g63,g148,g46)
    c: Symmetric(g63,g148,g46)
    c: Symmetric(g64,g149,g46)
    c: Symmetric(g64,g149,g46)
    c: Symmetric(g65,g150,g46)
    c: Symmetric(g65,g150,g46)
    c: Symmetric(g66,g151,g46)
    c: Symmetric(g66,g151,g46)
    c: Symmetric(g67,g152,g46)
    c: Symmetric(g67,g152,g46)
    c: Symmetric(g68,g153,g46)
    c: Symmetric(g68,g153,g46)
    c: Symmetric(g69,g154,g46)
    c: Symmetric(g69,g154,g46)
    c: Symmetric(g70,g155,g46)
    c: Symmetric(g70,g155,g46)
    c: Symmetric(g71,g156,g46)
    c: Symmetric(g71,g156,g46)
    c: Symmetric(g72,g157,g46)
    c: Symmetric(g72,g157,g46)
    c: Symmetric(g73,g158,g46)
    c: Symmetric(g73,g158,g46)
    c: Symmetric(g74,g159,g46)
    c: Symmetric(g74,g159,g46)
    c: Symmetric(g75,g160,g46)
    c: Symmetric(g75,g160,g46)
    c: Symmetric(g76,g161,g46)
    c: Symmetric(g76,g161,g46)
    c: Symmetric(g77,g162,g46)
    c: Symmetric(g77,g162,g46)
    c: Symmetric(g78,g163,g46)
    c: Symmetric(g78,g163,g46)
    c: Symmetric(g79,g164,g46)
    c: Symmetric(g79,g164,g46)
    c: Symmetric(g80,g165,g46)
    c: Symmetric(g80,g165,g46)
    c: Symmetric(g81,g166,g46)
    c: Symmetric(g81,g166,g46)
    c: Symmetric(g82,g167,g46)
    c: Symmetric(g82,g167,g46)
    c: Symmetric(g83,g168,g46)
    c: Symmetric(g83,g168,g46)
    c: Symmetric(g84,g169,g46)
    c: Symmetric(g84,g169,g46)
    c: Symmetric(g85,g170,g46)
    c: Symmetric(g85,g170,g46)
    c: Equal(g88,g171)
    c: Symmetric(g88,g171,g46)
    c: Symmetric(g88,g171,g46)
    c: Equal(g89,g172)
    c: Symmetric(g89,g172,g46)
    c: Symmetric(g89,g172,g46)
    c: Equal(g90,g173)
    c: Symmetric(g90,g173,g46)
    c: Symmetric(g90,g173,g46)
    c: Symmetric(g91,g174,g46)
    c: Symmetric(g91,g174,g46)
    c: Symmetric(g92,g175,g46)
    c: Symmetric(g92,g175,g46)
    c: Symmetric(g93,g176,g46)
    c: Symmetric(g93,g176,g46)
    c: Symmetric(g98,g177,g46)
    c: Symmetric(g98,g177,g46)
    c: Symmetric(g99,g178,g46)
    c: Symmetric(g99,g178,g46)
    c: Symmetric(g102,g179,g46)
    c: Symmetric(g102,g179,g46)
    c: Symmetric(g103,g180,g46)
    c: Symmetric(g103,g180,g46)
    c: Symmetric(g104,g181,g46)
    c: Symmetric(g104,g181,g46)
    c: Symmetric(g105,g182,g46)
    c: Symmetric(g105,g182,g46)
    c: Coincident(g183,g97)
    c: Coincident(g183,g178)
    c: Coincident(g184,g164)
    c: Coincident(g184,g79)
    c: Coincident(g185,g60)
    c: Coincident(g185,g145)
    c: Coincident(g186,g181)
    c: Coincident(g186,g101)
FEATURE [Part::Extrusion] Extrude001  label="ZAxisExtrusion"
  Base = -> Sketch001
  Dir = (0,0,1)
  DirMode = 2
  FaceMakerClass = Part::FaceMakerBullseye
  FaceMakerMode = 3
  LengthFwd = 470
  LengthRev = 0
  Placement = pos=(-160,150,10) rot=(0,0,1;1.5708rad)
  Solid = true
  Symmetric = false
FEATURE [Sketcher::SketchObject] Sketch002  label="MotorMountSktech"
  ArcFitTolerance = 1e-06
  FullyConstrained = true
  MakeInternals = false
  MapMode = 5
  sketch-geometry (13):
    g0: LineSegment StartX=25 StartY=-25 StartZ=0 EndX=25 EndY=25 EndZ=0
    g1: LineSegment StartX=25 StartY=25 StartZ=0 EndX=-25 EndY=25 EndZ=0
    g2: LineSegment StartX=-25 StartY=25 StartZ=0 EndX=-25 EndY=-25 EndZ=0
    g3: Circle CenterX=0 CenterY=4 CenterZ=0 NormalX=0 NormalY=0 NormalZ=1 AngleXU=0 Radius=11.05
    g4: Circle CenterX=-15.5 CenterY=19.5 CenterZ=0 NormalX=0 NormalY=0 NormalZ=1 AngleXU=0 Radius=1.75
    g5: Circle CenterX=-15.5 CenterY=-11.5 CenterZ=0 NormalX=0 NormalY=0 NormalZ=1 AngleXU=0 Radius=1.75
    g6: Circle CenterX=15.5 CenterY=19.5 CenterZ=0 NormalX=0 NormalY=0 NormalZ=1 AngleXU=0 Radius=1.75
    g7: Circle CenterX=15.5 CenterY=-11.5 CenterZ=0 NormalX=0 NormalY=0 NormalZ=1 AngleXU=0 Radius=1.75
    g8: LineSegment [constr] StartX=-15.5 StartY=19.5 StartZ=0 EndX=-15.5 EndY=-11.5 EndZ=0
    g9: LineSegment [constr] StartX=-15.5 StartY=19.5 StartZ=0 EndX=15.5 EndY=19.5 EndZ=0
    g10: LineSegment [constr] StartX=15.5 StartY=19.5 StartZ=0 EndX=15.5 EndY=-11.5 EndZ=0
    g11: LineSegment [constr] StartX=15.5 StartY=-11.5 StartZ=0 EndX=-15.5 EndY=-11.5 EndZ=0
    g12: LineSegment StartX=-25 StartY=-25 StartZ=0 EndX=25 EndY=-25 EndZ=0
  constraints (32):
    c: Coincident(g0,g1)
    c: Coincident(g1,g2)
    c: Vertical(g0)
    c: Distance(g2,g1) = 50
    c: DistanceX(g1,g1) = 50
    c: Diameter(g3) = 22.1
    c: Diameter(g4) = 3.5
    c: DistanceX(g4,g6) = 31
    c: DistanceX(g5,g7) = 31
    c: Coincident(g8,g4)
    c: Coincident(g8,g5)
    c: Vertical(g8)
    c: DistanceY(g8,g8) = 31
    c: Coincident(g9,g4)
    c: Coincident(g9,g6)
    c: Horizontal(g9)
    c: Coincident(g10,g6)
    c: Coincident(g10,g7)
    c: Coincident(g11,g7)
    c: Coincident(g11,g5)
    c: Equal(g4,g6)
    c: Equal(g6,g7)
    c: Equal(g7,g5)
    c: Horizontal(g11)
    c: DistanceY(g3,g1) = 21
    c: Coincident(g12,g2)
    c: Coincident(g12,g0)
    c: Horizontal(g12)
    c: Symmetric(g1,g0,g-2)
    c: Symmetric(g4,g7,g3)
    c: Symmetric(g2,g1,g-1)
    c: PointOnObject(g3,g-2)
FEATURE [Sketcher::SketchObject] Sketch003  label="MountPlateSketch"
  ArcFitTolerance = 1e-06
  FullyConstrained = true
  MakeInternals = false
  Placement = pos=(0,28.5,28.5) rot=(1,0,0;1.5708rad)
  sketch-geometry (13):
    g0: LineSegment StartX=-25 StartY=-25 StartZ=0 EndX=25 EndY=-25 EndZ=0
    g1: LineSegment StartX=25 StartY=-25 StartZ=0 EndX=25 EndY=25 EndZ=0
    g2: LineSegment StartX=25 StartY=25 StartZ=0 EndX=-25 EndY=25 EndZ=0
    g3: LineSegment StartX=-25 StartY=25 StartZ=0 EndX=-25 EndY=-25 EndZ=0
    g4: GeomPoint [constr] X=0 Y=0 Z=0
    g5: ArcOfCircle CenterX=-12.875 CenterY=16 CenterZ=0 NormalX=0 NormalY=0 NormalZ=1 AngleXU=0 Radius=2.1 StartAngle=0 EndAngle=3.14159
    g6: ArcOfCircle CenterX=-12.875 CenterY=-14 CenterZ=0 NormalX=0 NormalY=0 NormalZ=1 AngleXU=0 Radius=2.1 StartAngle=3.14159 EndAngle=6.28319
    g7: LineSegment StartX=-10.775 StartY=16 StartZ=0 EndX=-10.775 EndY=-14 EndZ=0
    g8: LineSegment StartX=-14.975 StartY=16 StartZ=0 EndX=-14.975 EndY=-14 EndZ=0
    g9: ArcOfCircle CenterX=12.875 CenterY=16 CenterZ=0 NormalX=0 NormalY=0 NormalZ=1 AngleXU=0 Radius=2.1 StartAngle=6.28318 EndAngle=9.42478
    g10: ArcOfCircle CenterX=12.875 CenterY=-14 CenterZ=0 NormalX=0 NormalY=0 NormalZ=1 AngleXU=0 Radius=2.1 StartAngle=3.14159 EndAngle=6.28319
    g11: LineSegment StartX=10.775 StartY=16 StartZ=0 EndX=10.775 EndY=-14 EndZ=0
    g12: LineSegment StartX=14.975 StartY=16 StartZ=0 EndX=14.975 EndY=-14 EndZ=0
  constraints (32):
    c: Coincident(g0,g1)
    c: Coincident(g1,g2)
    c: Coincident(g2,g3)
    c: Coincident(g3,g0)
    c: Horizontal(g0)
    c: Horizontal(g2)
    c: Vertical(g1)
    c: Vertical(g3)
    c: Symmetric(g2,g0,g4)
    c: Distance(g1,g3) = 50
    c: Distance(g0,g2) = 50
    c: Coincident(g4,g-1)
    c: Tangent(g5,g7) = 1.5708
    c: Tangent(g5,g8) = -1.5708
    c: Tangent(g6,g7) = 1.5708
    c: Tangent(g6,g8) = -1.5708
    c: Equal(g5,g6)
    c: Distance(g5,g6) = 30
    c: Radius(g5) = 2.1
    c: Vertical(g7)
    c: Equal(g5,g9)
    c: Symmetric(g5,g9,g-2)
    c: Symmetric(g5,g9,g-2)
    c: Equal(g6,g10)
    c: Symmetric(g6,g10,g-2)
    c: Symmetric(g6,g10,g-2)
    c: Symmetric(g7,g11,g-2)
    c: Symmetric(g7,g11,g-2)
    c: Symmetric(g8,g12,g-2)
    c: Symmetric(g8,g12,g-2)
    c: DistanceX(g6,g10) = 25.75
    c: DistanceY(g0,g10) = 11
FEATURE [Part::Extrusion] Extrude002  label="MotorPlate"
  Base = -> Sketch002
  Dir = (0,0,1)
  DirMode = 2
  FaceMakerClass = Part::FaceMakerBullseye
  FaceMakerMode = 3
  LengthFwd = 3.5
  LengthRev = 0
  Solid = true
  Symmetric = false
FEATURE [Part::Extrusion] Extrude003  label="MountPlate"
  Base = -> Sketch003
  Dir = (0,-1,2e-16)
  DirMode = 2
  FaceMakerClass = Part::FaceMakerBullseye
  FaceMakerMode = 3
  LengthFwd = 3.5
  LengthRev = 0
  Solid = true
  Symmetric = false
FEATURE [Part::Fuse] Fusion  label="NEMA17RightAngle"
  Base = -> Extrude002
  Placement = pos=(-9.85,-38.48,0) rot=(0,0,1;0rad)
  Tool = -> Extrude003
FEATURE [Sketcher::SketchObject] Sketch004  label="5mmCouplingSketch"
  ArcFitTolerance = 1e-06
  FullyConstrained = true
  MakeInternals = false
  sketch-geometry (2):
    g0: Circle CenterX=0 CenterY=0 CenterZ=0 NormalX=0 NormalY=0 NormalZ=1 AngleXU=0 Radius=10
    g1: Circle CenterX=0 CenterY=0 CenterZ=0 NormalX=0 NormalY=0 NormalZ=1 AngleXU=0 Radius=2.5
  constraints (4):
    c: Diameter(g0) = 20
    c: Coincident(g0,g-1)
    c: Diameter(g1) = 5
    c: Coincident(g1,g0)
FEATURE [Part::Extrusion] Extrude004  label="Z-5-8mmCoupling"
  Base = -> Sketch004
  Dir = (0,0,1)
  DirMode = 2
  FaceMakerClass = Part::FaceMakerBullseye
  FaceMakerMode = 3
  LengthFwd = 25
  LengthRev = 0
  Placement = pos=(-170,181,52.8) rot=(0,0,1;0rad)
  Solid = true
  Symmetric = false
FEATURE [Sketcher::SketchObject] Sketch005  label="BracketBaseShape"
  ArcFitTolerance = 1e-06
  AttachmentSupport = -> [YZ_Plane001]
  FullyConstrained = true
  MakeInternals = false
  MapMode = 5
  Placement = pos=(0,0,0) rot=(0.57735,0.57735,0.57735;2.0944rad)
  sketch-geometry (16):
    g0: LineSegment StartX=0 StartY=52.5 StartZ=0 EndX=0 EndY=32.5 EndZ=0
    g1: LineSegment StartX=0 StartY=32.5 StartZ=0 EndX=2.2 EndY=32.5 EndZ=0
    g2: LineSegment StartX=2.2 StartY=32.5 StartZ=0 EndX=2.2 EndY=52.5 EndZ=0
    g3: LineSegment StartX=2.2 StartY=52.5 StartZ=0 EndX=0 EndY=52.5 EndZ=0
    g4: LineSegment StartX=2.2 StartY=32.5 StartZ=0 EndX=45.8 EndY=32.5 EndZ=0
    g5: LineSegment StartX=45.8 StartY=32.5 StartZ=0 EndX=45.8 EndY=36 EndZ=0
    g6: LineSegment StartX=45.8 StartY=36 StartZ=0 EndX=2.2 EndY=36 EndZ=0
    g7: LineSegment StartX=2.2 StartY=36 StartZ=0 EndX=2.2 EndY=32.5 EndZ=0
    g8: LineSegment StartX=45.8 StartY=32.5 StartZ=0 EndX=42.3 EndY=32.5 EndZ=0
    g9: LineSegment StartX=42.3 StartY=32.5 StartZ=0 EndX=42.3 EndY=0 EndZ=0
    g10: LineSegment StartX=42.3 StartY=0 StartZ=0 EndX=45.8 EndY=0 EndZ=0
    g11: LineSegment StartX=45.8 StartY=0 StartZ=0 EndX=45.8 EndY=32.5 EndZ=0
    g12: LineSegment StartX=45.8 StartY=0 StartZ=0 EndX=75.8 EndY=0 EndZ=0
    g13: LineSegment StartX=75.8 StartY=0 StartZ=0 EndX=75.8 EndY=2.2 EndZ=0
    g14: LineSegment StartX=75.8 StartY=2.2 StartZ=0 EndX=45.8 EndY=2.2 EndZ=0
    g15: LineSegment StartX=45.8 StartY=2.2 StartZ=0 EndX=45.8 EndY=0 EndZ=0
  constraints (45):
    c: Coincident(g0,g1)
    c: Coincident(g1,g2)
    c: Coincident(g2,g3)
    c: Coincident(g3,g0)
    c: Vertical(g0)
    c: Vertical(g2)
    c: Horizontal(g1)
    c: Horizontal(g3)
    c: Coincident(g4,g5)
    c: Coincident(g5,g6)
    c: Coincident(g6,g7)
    c: Coincident(g7,g4)
    c: Horizontal(g4)
    c: Horizontal(g6)
    c: Vertical(g5)
    c: Vertical(g7)
    c: Coincident(g4,g1)
    c: Coincident(g8,g9)
    c: Coincident(g9,g10)
    c: Coincident(g10,g11)
    c: Coincident(g11,g8)
    c: Horizontal(g8)
    c: Horizontal(g10)
    c: Vertical(g9)
    c: Vertical(g11)
    c: Coincident(g8,g4)
    c: PointOnObject(g9,g-1)
    c: Coincident(g12,g13)
    c: Coincident(g13,g14)
    c: Coincident(g14,g15)
    c: Coincident(g15,g12)
    c: Horizontal(g12)
    c: Horizontal(g14)
    c: Vertical(g13)
    c: Vertical(g15)
    c: Coincident(g12,g10)
    c: DistanceX(g3,g3) = 2.2
    c: DistanceY(g0,g0) = 20
    c: DistanceY(g5,g5) = 3.5
    c: DistanceX(g0,g8) = 42.3
    c: DistanceX(g10,g10) = 3.5
    c: DistanceY(g13,g13) = 2.2
    c: DistanceX(g14,g14) = 30
    c: DistanceY(g9,g9) = 32.5
    c: PointOnObject(g0,g-2)
FEATURE [PartDesign::Pad] Pad  label="BracketPad"
  Direction = (1,0,0)
  Length = 42.3
  Length2 = 10
  Placement = pos=(0,0,0) rot=(1,1,1;2.0944rad)
  Profile = -> Sketch005
  ReferenceAxis = -> Sketch005 [N_Axis]
  Suppressed = false
  Type = 0
FEATURE [Sketcher::SketchObject] Sketch006  label="MotorMountHoles"
  ArcFitTolerance = 1e-06
  AttachmentSupport = -> [Pad]
  FullyConstrained = true
  MakeInternals = false
  MapMode = 5
  Placement = pos=(0,7.9e-15,36) rot=(0,0,-1;1.5708rad)
  sketch-geometry (9):
    g0: Circle CenterX=-21.15 CenterY=21.15 CenterZ=0 NormalX=0 NormalY=0 NormalZ=1 AngleXU=0 Radius=11.1
    g1: Circle CenterX=-36.65 CenterY=36.65 CenterZ=0 NormalX=0 NormalY=0 NormalZ=1 AngleXU=0 Radius=1.75
    g2: Circle CenterX=-36.65 CenterY=5.65 CenterZ=0 NormalX=0 NormalY=0 NormalZ=1 AngleXU=0 Radius=1.75
    g3: Circle CenterX=-5.65 CenterY=36.65 CenterZ=0 NormalX=0 NormalY=0 NormalZ=1 AngleXU=0 Radius=1.75
    g4: Circle CenterX=-5.65 CenterY=5.65 CenterZ=0 NormalX=0 NormalY=0 NormalZ=1 AngleXU=0 Radius=1.75
    g5: LineSegment [constr] StartX=-36.65 StartY=36.65 StartZ=0 EndX=-5.65 EndY=36.65 EndZ=0
    g6: LineSegment [constr] StartX=-5.65 StartY=36.65 StartZ=0 EndX=-5.65 EndY=5.65 EndZ=0
    g7: LineSegment [constr] StartX=-5.65 StartY=5.65 StartZ=0 EndX=-36.65 EndY=5.65 EndZ=0
    g8: LineSegment [constr] StartX=-36.65 StartY=5.65 StartZ=0 EndX=-36.65 EndY=36.65 EndZ=0
  constraints (22):
    c: Diameter(g0) = 22.2
    c: Coincident(g5,g1)
    c: Coincident(g5,g3)
    c: Horizontal(g5)
    c: Coincident(g6,g3)
    c: Coincident(g6,g4)
    c: Coincident(g7,g4)
    c: Coincident(g7,g2)
    c: Coincident(g8,g2)
    c: Coincident(g8,g1)
    c: Vertical(g8)
    c: Vertical(g6)
    c: Horizontal(g7)
    c: Equal(g4,g2)
    c: Equal(g2,g1)
    c: Equal(g1,g3)
    c: Diameter(g1) = 3.5
    c: Symmetric(g1,g4,g0)
    c: DistanceX(g5,g5) = 31
    c: DistanceY(g6,g6) = 31
    c: DistanceX(g0,g-1) = 21.15
    c: DistanceY(g-1,g0) = 21.15
FEATURE [PartDesign::Pocket] Pocket  label="MotorMountPocket"
  BaseFeature = -> Pad
  Direction = (0,0,-1)
  Length = 10
  Length2 = 5
  Placement = pos=(0,0,0) rot=(1,1,1;2.0944rad)
  Profile = -> Sketch006
  ReferenceAxis = -> Sketch006 [N_Axis]
  Suppressed = false
  Type = 1
FEATURE [Sketcher::SketchObject] Sketch007  label="MotorCableHole"
  ArcFitTolerance = 1e-06
  AttachmentOffset = pos=(0,0,-20) rot=(0,0,1;0rad)
  AttachmentSupport = -> [Pocket]
  FullyConstrained = true
  MakeInternals = false
  MapMode = 5
  Placement = pos=(1.67e-14,55.8,0) rot=(0.57735,0.57735,0.57735;4.18879rad)
  sketch-geometry (4):
    g0: LineSegment StartX=0 StartY=32 StartZ=0 EndX=0 EndY=10 EndZ=0
    g1: LineSegment StartX=0 StartY=10 StartZ=0 EndX=13 EndY=10 EndZ=0
    g2: LineSegment StartX=13 StartY=10 StartZ=0 EndX=13 EndY=32 EndZ=0
    g3: LineSegment StartX=13 StartY=32 StartZ=0 EndX=0 EndY=32 EndZ=0
  constraints (12):
    c: Coincident(g0,g1)
    c: Coincident(g1,g2)
    c: Coincident(g2,g3)
    c: Coincident(g3,g0)
    c: Vertical(g0)
    c: Vertical(g2)
    c: Horizontal(g1)
    c: Horizontal(g3)
    c: PointOnObject(g0,g-2)
    c: DistanceY(g2,g2) = 22
    c: DistanceX(g3,g3) = 13
    c: DistanceY(g-1,g0) = 10
FEATURE [PartDesign::Pocket] Pocket001  label="CablePocket"
  BaseFeature = -> Pocket
  Direction = (0,-1,0)
  Length = 5
  Length2 = 5
  Placement = pos=(0,0,0) rot=(1,1,1;2.0944rad)
  Profile = -> Sketch007
  ReferenceAxis = -> Sketch007 [N_Axis]
  Suppressed = false
  Type = 1
FEATURE [Sketcher::SketchObject] Sketch008  label="ZAxisExtrusionTSlotMountingHoles"
  ArcFitTolerance = 1e-06
  AttachmentSupport = -> [Pocket001]
  FullyConstrained = true
  MakeInternals = false
  MapMode = 5
  Placement = pos=(5e-16,2.2,0) rot=(0.57735,0.57735,0.57735;4.18879rad)
  sketch-geometry (3):
    g0: Circle CenterX=44 CenterY=31 CenterZ=0 NormalX=0 NormalY=0 NormalZ=1 AngleXU=0 Radius=3
    g1: Circle CenterX=44 CenterY=11 CenterZ=0 NormalX=0 NormalY=0 NormalZ=1 AngleXU=0 Radius=3
    g2: LineSegment [constr] StartX=44 StartY=31 StartZ=0 EndX=44 EndY=11 EndZ=0
  constraints (8):
    c: DistanceY(g-1,g1) = 11
    c: DistanceY(g-1,g0) = 31
    c: Diameter(g1) = 6
    c: Diameter(g0) = 6
    c: Coincident(g2,g0)
    c: Coincident(g2,g1)
    c: Vertical(g2)
    c: DistanceX(g-1,g0) = 44
FEATURE [PartDesign::Hole] Hole  label="ZMount"
  BaseFeature = -> Pocket001
  CustomThreadClearance = 0
  Depth = 25
  DepthType = 0
  Diameter = 5.5
  DrillForDepth = false
  DrillPoint = 1
  DrillPointAngle = 118
  HoleCutCountersinkAngle = 90
  HoleCutCustomValues = false
  HoleCutDepth = 0
  HoleCutDiameter = 0
  HoleCutType = 0
  ModelThread = false
  Placement = pos=(0,0,0) rot=(1,1,1;2.0944rad)
  Profile = -> Sketch008
  Suppressed = false
  Tapered = false
  TaperedAngle = 90
  ThreadClass = 0
  ThreadDepth = 25
  ThreadDepthType = 0
  ThreadDirection = 0
  ThreadFit = 0
  ThreadSize = 13
  ThreadType = 1
  Threaded = false
  UseCustomThreadClearance = false
FEATURE [Sketcher::SketchObject] Sketch009  label="BaseLeftExtrusionTSlotMountingHoles"
  ArcFitTolerance = 1e-06
  AttachmentSupport = -> [Hole]
  FullyConstrained = true
  MakeInternals = false
  MapMode = 5
  Placement = pos=(0,5e-16,2.2) rot=(0,0,-1;1.5708rad)
  sketch-geometry (3):
    g0: Circle CenterX=-66 CenterY=31 CenterZ=0 NormalX=0 NormalY=0 NormalZ=1 AngleXU=0 Radius=3
    g1: Circle CenterX=-66 CenterY=11 CenterZ=0 NormalX=0 NormalY=0 NormalZ=1 AngleXU=0 Radius=3
    g2: LineSegment [constr] StartX=-66 StartY=31 StartZ=0 EndX=-66 EndY=11 EndZ=0
  constraints (8):
    c: Diameter(g0) = 6
    c: Equal(g0,g1)
    c: Coincident(g2,g0)
    c: Coincident(g2,g1)
    c: Vertical(g2)
    c: DistanceY(g-1,g1) = 11
    c: DistanceY(g-1,g0) = 31
    c: DistanceX(g1,g-1) = 66
FEATURE [PartDesign::Hole] Hole001  label="BaseLeftMount"
  BaseFeature = -> Hole
  CustomThreadClearance = 0
  Depth = 25
  DepthType = 0
  Diameter = 5.5
  DrillForDepth = false
  DrillPoint = 1
  DrillPointAngle = 118
  HoleCutCountersinkAngle = 90
  HoleCutCustomValues = false
  HoleCutDepth = 0
  HoleCutDiameter = 0
  HoleCutType = 0
  ModelThread = false
  Placement = pos=(0,0,0) rot=(1,1,1;2.0944rad)
  Profile = -> Sketch009
  Suppressed = false
  Tapered = false
  TaperedAngle = 90
  ThreadClass = 0
  ThreadDepth = 25
  ThreadDepthType = 0
  ThreadDirection = 0
  ThreadFit = 0
  ThreadSize = 13
  ThreadType = 1
  Threaded = false
  UseCustomThreadClearance = false
FEATURE [Part::FeaturePython] TSlot001  label="M5 x 20 series-TSlot"  # WARN: FeaturePython — macro-defined, semantics opaque (R4)
  Diameter = 3
  Invert = false
  LeftHanded = false
  MatchOuter = false
  OffsetAngle = 0
  Placement = pos=(-160.02,225.9,9.5) rot=(0,0,1;0rad)
  SlotWidth = 0
  Thread = false
  Type = 3
FEATURE [Part::FeaturePython] TSlot002  label="M5 x 20 series-TSlot005"  # WARN: FeaturePython — macro-defined, semantics opaque (R4)
  Diameter = 3
  Invert = false
  LeftHanded = false
  MatchOuter = false
  OffsetAngle = 0
  Placement = pos=(-180,225.91,9.51) rot=(0,0,1;0rad)
  SlotWidth = 0
  Thread = false
  Type = 3
FEATURE [Part::FeaturePython] TSlot  label="M5 x 20 series-TSlot007"  # WARN: FeaturePython — macro-defined, semantics opaque (R4)
  Diameter = 3
  Invert = false
  LeftHanded = false
  MatchOuter = false
  OffsetAngle = 0
  Placement = pos=(-180.08,159.5,59) rot=(0,0.707107,0.707107;3.14159rad)
  SlotWidth = 0
  Thread = false
  Type = 3
FEATURE [Part::FeaturePython] TSlot003  label="M5 x 20 series-TSlot006"  # WARN: FeaturePython — macro-defined, semantics opaque (R4)
  Diameter = 3
  Invert = false
  LeftHanded = false
  MatchOuter = false
  OffsetAngle = 0
  Placement = pos=(-160,159.51,59) rot=(-1,0,0;1.5708rad)
  SlotWidth = 0
  Thread = false
  Type = 3
FEATURE [Sketcher::SketchObject] Sketch010
  ArcFitTolerance = 1e-06
  AttachmentSupport = -> [XY_Plane004]
  FullyConstrained = true
  MakeInternals = false
  MapMode = 5
  sketch-geometry (6):
    g0: Circle [constr] CenterX=0 CenterY=0 CenterZ=0 NormalX=0 NormalY=0 NormalZ=1 AngleXU=0 Radius=8
    g1: Circle CenterX=0 CenterY=0 CenterZ=0 NormalX=0 NormalY=0 NormalZ=1 AngleXU=0 Radius=11
    g2: Circle CenterX=0 CenterY=8 CenterZ=0 NormalX=0 NormalY=0 NormalZ=1 AngleXU=0 Radius=1.75
    g3: Circle CenterX=-8 CenterY=0 CenterZ=0 NormalX=0 NormalY=0 NormalZ=1 AngleXU=0 Radius=1.75
    g4: Circle CenterX=0 CenterY=-8 CenterZ=0 NormalX=0 NormalY=0 NormalZ=1 AngleXU=0 Radius=1.75
    g5: Circle CenterX=8 CenterY=0 CenterZ=0 NormalX=0 NormalY=0 NormalZ=1 AngleXU=0 Radius=1.75
  constraints (16):
    c: Diameter(g0) = 16
    c: Coincident(g0,g-1)
    c: Diameter(g1) = 22
    c: Coincident(g1,g0)
    c: Diameter(g2) = 3.5
    c: PointOnObject(g2,g0)
    c: PointOnObject(g3,g0)
    c: PointOnObject(g4,g0)
    c: PointOnObject(g5,g0)
    c: Equal(g3,g2)
    c: Equal(g2,g5)
    c: Equal(g4,g5)
    c: PointOnObject(g3,g-1)
    c: PointOnObject(g2,g-2)
    c: PointOnObject(g5,g-1)
    c: PointOnObject(g4,g-2)
FEATURE [PartDesign::Pad] Pad001
  Direction = (0,0,1)
  Length = 3.5
  Length2 = 10
  Profile = -> Sketch010
  ReferenceAxis = -> Sketch010 [N_Axis]
  Suppressed = false
  Type = 0
FEATURE [Sketcher::SketchObject] Sketch011
  ArcFitTolerance = 1e-06
  AttachmentSupport = -> [XY_Plane004]
  FullyConstrained = true
  MakeInternals = false
  MapMode = 5
  sketch-geometry (1):
    g0: Circle CenterX=0 CenterY=0 CenterZ=0 NormalX=0 NormalY=0 NormalZ=1 AngleXU=0 Radius=5.1
  constraints (2):
    c: Diameter(g0) = 10.2
    c: Coincident(g0,g-1)
FEATURE [PartDesign::Pad] Pad002
  BaseFeature = -> Pad001
  Direction = (0,0,1)
  Length = 5
  Length2 = 10
  Profile = -> Sketch011
  ReferenceAxis = -> Sketch011 [N_Axis]
  Suppressed = false
  Type = 0
FEATURE [PartDesign::Pad] Pad003
  BaseFeature = -> Pad002
  Direction = (0,0,1)
  Length = 10
  Length2 = 10
  Profile = -> Sketch011
  ReferenceAxis = -> Sketch011 [N_Axis]
  Reversed = true
  Suppressed = false
  Type = 0
FEATURE [Sketcher::SketchObject] Sketch012
  ArcFitTolerance = 1e-06
  AttachmentSupport = -> [Pad003]
  FullyConstrained = true
  MakeInternals = false
  MapMode = 5
  Placement = pos=(0,0,5) rot=(0,0,1;0rad)
  sketch-geometry (1):
    g0: Circle CenterX=0 CenterY=0 CenterZ=0 NormalX=0 NormalY=0 NormalZ=1 AngleXU=0 Radius=4
  constraints (2):
    c: Diameter(g0) = 8
    c: Coincident(g0,g-1)
FEATURE [PartDesign::Hole] Hole002
  BaseFeature = -> Pad003
  CustomThreadClearance = 0
  Depth = 69.6499
  DepthType = 1
  Diameter = 9
  DrillForDepth = false
  DrillPoint = 1
  DrillPointAngle = 118
  HoleCutCountersinkAngle = 90
  HoleCutCustomValues = false
  HoleCutDepth = 0
  HoleCutDiameter = 10.3
  HoleCutType = 0
  ModelThread = false
  Profile = -> Sketch012
  Suppressed = false
  Tapered = false
  TaperedAngle = 90
  ThreadClass = 0
  ThreadDepth = 69.6499
  ThreadDepthType = 2
  ThreadDirection = 0
  ThreadFit = 0
  ThreadSize = 16
  ThreadType = 1
  Threaded = false
  UseCustomThreadClearance = false
FEATURE [PartDesign::Body] Body001  label="LeadScrewNut"
  AllowCompound = false
  Group = -> [Sketch010,Pad001,Sketch011,Pad002,Pad003,Sketch012,Hole002]
  Origin = -> Origin004
  Placement = pos=(-170,181,178) rot=(0,0,1;0rad)
  Tip = -> Hole002
FEATURE [Sketcher::SketchObject] Sketch013  label="ZFollowerSketch"
  ArcFitTolerance = 1e-06
  AttachmentOffset = pos=(0,0,-12) rot=(0,0,1;0rad)
  AttachmentSupport = -> [YZ_Plane005]
  FullyConstrained = true
  MakeInternals = false
  MapMode = 5
  Placement = pos=(-12,0,0) rot=(0.57735,0.57735,0.57735;2.0944rad)
  sketch-geometry (6):
    g0: LineSegment StartX=44 StartY=-14.5 StartZ=0 EndX=44 EndY=-8 EndZ=0
    g1: LineSegment StartX=44 StartY=-8 StartZ=0 EndX=19 EndY=-8 EndZ=0
    g2: LineSegment StartX=14 StartY=-14.5 StartZ=0 EndX=44 EndY=-14.5 EndZ=0
    g3: LineSegment StartX=14 StartY=48 StartZ=0 EndX=14 EndY=-14.5 EndZ=0
    g4: LineSegment StartX=19 StartY=-8 StartZ=0 EndX=19 EndY=48 EndZ=0
    g5: LineSegment StartX=19 StartY=48 StartZ=0 EndX=14 EndY=48 EndZ=0
  constraints (18):
    c: Coincident(g0,g1)
    c: Coincident(g2,g0)
    c: Vertical(g0)
    c: Horizontal(g1)
    c: Vertical(g3)
    c: Vertical(g4)
    c: Coincident(g4,g1)
    c: DistanceY(g0,g0) = 6.5
    c: Coincident(g3,g2)
    c: DistanceX(g1,g1) = 25
    c: DistanceY(g4,g4) = 56
    c: Coincident(g5,g4)
    c: Coincident(g5,g3)
    c: Horizontal(g5)
    c: DistanceX(g5,g5) = 5
    c: Horizontal(g2)
    c: DistanceY(g2,g-1) = 14.5
    c: Distance(g-1,g3) = 14
FEATURE [PartDesign::Pad] Pad004  label="FollowerPad"
  Direction = (1,0,0)
  Length = 76
  Length2 = 10
  Placement = pos=(0,0,0) rot=(1,1,1;2.0944rad)
  Profile = -> Sketch013
  ReferenceAxis = -> Sketch013 [N_Axis]
  Reversed = true
  Suppressed = false
  Type = 0
FEATURE [Sketcher::SketchObject] Sketch014  label="ThreadedRodHoleSketch"
  ArcFitTolerance = 1e-06
  AttachmentSupport = -> [Pad004]
  FullyConstrained = true
  MakeInternals = false
  MapMode = 5
  Placement = pos=(0,-1.8e-15,-8) rot=(0,0,-1;1.5708rad)
  sketch-geometry (1):
    g0: Circle CenterX=-30.9 CenterY=-50 CenterZ=0 NormalX=0 NormalY=0 NormalZ=1 AngleXU=0 Radius=5.15
  constraints (3):
    c: Diameter(g0) = 10.3
    c: DistanceY(g0,g-1) = 50
    c: DistanceX(g0,g-1) = 30.9
FEATURE [PartDesign::Pocket] Pocket002  label="ThreadedRodThroughHole"
  BaseFeature = -> Pad004
  Direction = (0,0,-1)
  Length = 5
  Length2 = 5
  Placement = pos=(0,0,0) rot=(1,1,1;2.0944rad)
  Profile = -> Sketch014
  ReferenceAxis = -> Sketch014 [N_Axis]
  Suppressed = false
  Type = 1
FEATURE [Sketcher::SketchObject] Sketch015  label="LeadScrewNutHeatSetHolesSketch"
  ArcFitTolerance = 1e-06
  AttachmentSupport = -> [Pocket002]
  FullyConstrained = true
  MakeInternals = false
  MapMode = 5
  Placement = pos=(0,-1.8e-15,-8) rot=(0,0,-1;1.5708rad)
  sketch-geometry (7):
    g0: Circle [constr] CenterX=-31 CenterY=-50 CenterZ=0 NormalX=0 NormalY=0 NormalZ=1 AngleXU=0 Radius=9
    g1: Circle CenterX=-31 CenterY=-41 CenterZ=0 NormalX=0 NormalY=0 NormalZ=1 AngleXU=0 Radius=2.3
    g2: Circle CenterX=-22 CenterY=-50 CenterZ=0 NormalX=0 NormalY=0 NormalZ=1 AngleXU=0 Radius=2.3
    g3: Circle CenterX=-31 CenterY=-59 CenterZ=0 NormalX=0 NormalY=0 NormalZ=1 AngleXU=0 Radius=2.3
    g4: Circle CenterX=-40 CenterY=-50 CenterZ=0 NormalX=0 NormalY=0 NormalZ=1 AngleXU=0 Radius=2.3
    g5: LineSegment [constr] StartX=-40 StartY=-50 StartZ=0 EndX=-22 EndY=-50 EndZ=0
    g6: LineSegment [constr] StartX=-31 StartY=-59 StartZ=0 EndX=-31 EndY=-41 EndZ=0
  constraints (19):
    c: Diameter(g0) = 18
    c: PointOnObject(g1,g0)
    c: PointOnObject(g2,g0)
    c: PointOnObject(g3,g0)
    c: PointOnObject(g4,g0)
    c: Coincident(g5,g4)
    c: Coincident(g5,g2)
    c: Horizontal(g5)
    c: Coincident(g6,g3)
    c: Coincident(g6,g1)
    c: Vertical(g6)
    c: Diameter(g1) = 4.6
    c: Equal(g2,g1)
    c: Equal(g4,g1)
    c: Equal(g3,g4)
    c: PointOnObject(g0,g5)
    c: PointOnObject(g0,g6)
    c: DistanceX(g0,g-1) = 31
    c: DistanceY(g0,g-1) = 50
FEATURE [PartDesign::Pocket] Pocket003  label="LeadScrewNutHeatSetInsertPocket"
  BaseFeature = -> Pocket002
  Direction = (0,0,-1)
  Length = 5.5
  Length2 = 5
  Placement = pos=(0,0,0) rot=(1,1,1;2.0944rad)
  Profile = -> Sketch015
  ReferenceAxis = -> Sketch015 [N_Axis]
  Suppressed = false
  Type = 0
FEATURE [Part::FeaturePython] Screw  label="M5x6-Screw"  # WARN: FeaturePython — macro-defined, semantics opaque (R4)
  BaseObject = -> Body [Hole001.Edge34]
  Diameter = 6
  Invert = false
  LeftHanded = false
  Length = 12
  LengthCustom = 6
  MatchOuter = false
  OffsetAngle = 0
  Placement = pos=(-160.1,162.1,54) rot=(-1,0,0;1.5708rad)
  Thread = false
  Type = 75
FEATURE [Part::FeaturePython] Screw011  label="M5x6-Screw017"  # WARN: FeaturePython — macro-defined, semantics opaque (R4)
  BaseObject = -> Body [Hole001.Edge36]
  Diameter = 6
  Invert = false
  LeftHanded = false
  Length = 12
  LengthCustom = 6
  MatchOuter = false
  OffsetAngle = 0
  Placement = pos=(-180.1,162.1,54) rot=(-1,0,0;1.5708rad)
  Thread = false
  Type = 75
FEATURE [Part::FeaturePython] Screw012  label="M3x8-Screw"  # WARN: FeaturePython — macro-defined, semantics opaque (R4)
  BaseObject = -> Body [Hole001.Edge72]
  Diameter = 4
  Invert = false
  LeftHanded = false
  Length = 2
  LengthCustom = 8
  MatchOuter = false
  OffsetAngle = 0
  Placement = pos=(-154.45,165.55,46) rot=(0,0,1;0rad)
  Thread = false
  Type = 75
FEATURE [Part::FeaturePython] Screw013  label="M3x8-Screw026"  # WARN: FeaturePython — macro-defined, semantics opaque (R4)
  BaseObject = -> Body [Hole001.Edge75]
  Diameter = 4
  Invert = false
  LeftHanded = false
  Length = 2
  LengthCustom = 8
  MatchOuter = false
  OffsetAngle = 0
  Placement = pos=(-185.45,165.55,46) rot=(0,0,1;0rad)
  Thread = false
  Type = 75
FEATURE [Part::FeaturePython] Screw014  label="M3x8-Screw024"  # WARN: FeaturePython — macro-defined, semantics opaque (R4)
  BaseObject = -> Body [Hole001.Edge71]
  Diameter = 4
  Invert = false
  LeftHanded = false
  Length = 2
  LengthCustom = 8
  MatchOuter = false
  OffsetAngle = 0
  Placement = pos=(-154.45,196.55,46) rot=(0,0,1;0rad)
  Thread = false
  Type = 75
FEATURE [Part::FeaturePython] Screw015  label="M3x8-Screw025"  # WARN: FeaturePython — macro-defined, semantics opaque (R4)
  BaseObject = -> Body [Hole001.Edge73]
  Diameter = 4
  Invert = false
  LeftHanded = false
  Length = 2
  LengthCustom = 8
  MatchOuter = false
  OffsetAngle = 0
  Placement = pos=(-185.45,196.55,46) rot=(0,0,1;0rad)
  Thread = false
  Type = 75
FEATURE [Part::FeaturePython] Screw016  label="M5x6-Screw016"  # WARN: FeaturePython — macro-defined, semantics opaque (R4)
  BaseObject = -> Body [Hole001.Edge64]
  Diameter = 6
  Invert = false
  LeftHanded = false
  Length = 12
  LengthCustom = 6
  MatchOuter = false
  OffsetAngle = 0
  Placement = pos=(-160.1,225.9,12.2) rot=(0,0,1;0rad)
  Thread = false
  Type = 75
FEATURE [Part::FeaturePython] Screw017  label="M5x6-Screw015"  # WARN: FeaturePython — macro-defined, semantics opaque (R4)
  BaseObject = -> Body [Hole001.Edge65]
  Diameter = 6
  Invert = false
  LeftHanded = false
  Length = 12
  LengthCustom = 6
  MatchOuter = false
  OffsetAngle = 0
  Placement = pos=(-180.1,225.9,12.2) rot=(0,0,1;0rad)
  Thread = false
  Type = 75
FEATURE [App::Part] Part002  label="ZMotorBracketFasteners"
  Group = -> [TSlot001,TSlot002,TSlot,TSlot003,Screw012,Screw,Screw014,Screw017,Screw015,Screw016,Screw013,Screw011]
  Origin = -> Origin006
FEATURE [Sketcher::SketchObject] Sketch021
  ArcFitTolerance = 1e-06
  AttachmentSupport = -> [XY_Plane009]
  FullyConstrained = true
  MakeInternals = false
  MapMode = 5
  sketch-geometry (2):
    g0: Circle CenterX=0 CenterY=118 CenterZ=0 NormalX=0 NormalY=0 NormalZ=1 AngleXU=0 Radius=72.5
    g1: Circle CenterX=0 CenterY=118 CenterZ=0 NormalX=0 NormalY=0 NormalZ=1 AngleXU=0 Radius=87
  constraints (5):
    c: Diameter(g0) = 145
    c: PointOnObject(g0,g-2)
    c: DistanceY(g-1,g0) = 118
    c: Diameter(g1) = 174
    c: Coincident(g1,g0)
FEATURE [Part::Feature] Part__Feature011  label="rear end cap001"
  shape: bbox 46.44 x 42.08 x 9.4 mm, 73 faces (baked)
FEATURE [Part::Feature] Part__Feature012  label="rear bearing001"
  Placement = pos=(0,0,6.6) rot=(0,0,1;0rad)
  shape: bbox 16 x 16 x 5.05 mm, 13 faces (baked)
FEATURE [Part::Feature] Part__Feature013  label="connector001"
  shape: bbox 10.8 x 15.6 x 6.2 mm, 85 faces (baked)
FEATURE [Part::Feature] Part__Feature014  label="shaft001"
  Placement = pos=(0,0,2.8) rot=(0,0,1;0rad)
  shape: bbox 5 x 5 x 58 mm, 7 faces (baked)
FEATURE [Part::Feature] Part__Feature015  label="stator001"
  Placement = pos=(0,0,9.4) rot=(0,0,1;0rad)
  shape: bbox 42 x 42 x 20 mm, 713 faces (baked)
FEATURE [Part::Feature] Part__Feature016  label="front end cap001"
  Placement = pos=(0,0,29.4) rot=(0,0,1;0rad)
  shape: bbox 42 x 42 x 10 mm, 34 faces (baked)
FEATURE [Part::Feature] Part__Feature017  label="front bearing001"
  Placement = pos=(0,0,34.6) rot=(0,1,0;3.14159rad)
  shape: bbox 16 x 16 x 5.05 mm, 13 faces (baked)
FEATURE [Part::Feature] Part__Feature018  label="M3x10-Screw004"
  Placement = pos=(15.5,15.5,2) rot=(0,1,0;3.14159rad)
  shape: bbox 5.7 x 5.7 x 11.65 mm, 15 faces (baked)
FEATURE [Part::Feature] Part__Feature019  label="M3x10-Screw005"
  Placement = pos=(15.5,-15.5,2) rot=(0,1,0;3.14159rad)
  shape: bbox 5.7 x 5.7 x 11.65 mm, 15 faces (baked)
FEATURE [Part::Feature] Part__Feature020  label="M3x10-Screw006"
  Placement = pos=(-15.5,15.5,2) rot=(0,1,0;3.14159rad)
  shape: bbox 5.7 x 5.7 x 11.65 mm, 15 faces (baked)
FEATURE [Part::Feature] Part__Feature021  label="M3x10-Screw007"
  Placement = pos=(-15.5,-15.5,2) rot=(0,1,0;3.14159rad)
  shape: bbox 5.7 x 5.7 x 11.65 mm, 15 faces (baked)
FEATURE [App::Part] _7HS4401S_Stepper_Motor001  label="XMotor"
  Group = -> [Part__Feature011,Part__Feature012,Part__Feature013,Part__Feature014,Part__Feature015,Part__Feature016,Part__Feature017,Part__Feature018,Part__Feature019,Part__Feature020,Part__Feature021]
  Origin = -> Origin010
  Placement = pos=(-280,185,200) rot=(1,0,0;1.5708rad)
FEATURE [Part::Feature] Part__Feature022  label="GT2 Pulley 20 Tooth (ID6mm)"
  shape: bbox 16 x 16 x 17 mm, 133 faces (baked)
FEATURE [Part::Feature] Part__Feature023  label="socket set screw flat point_am_B18.3.6M - M3 x 0.5 x 5 Hex Socket Flat Pt. SS --S"
  Placement = pos=(8.05,9e-16,12) rot=(0,0.826578,-0.562822;3.14159rad)
  shape: bbox 5 x 3 x 3 mm, 71 faces (baked)
FEATURE [Part::Feature] Part__Feature024  label="socket set screw flat point_am_B18.3.6M - M3 x 0.5 x 5 Hex Socket Flat Pt. SS --S001"
  Placement = pos=(0,8.05,12) rot=(0.274383,-0.274383,-0.921644;1.6523rad)
  shape: bbox 3 x 5 x 3 mm, 71 faces (baked)
FEATURE [App::Part] GT2_20_Tooth_Assy__ID_6mm_  label="GT2 20 Tooth Assy (ID 6mm)"
  Group = -> [Part__Feature022,Part__Feature023,Part__Feature024]
  Origin = -> Origin011
  Placement = pos=(-280,141.2,200) rot=(-0.58,-0.58,0.58;4.18879rad)
FEATURE [Part::Feature] Part__Feature025  label="6153K690_625-2RS SST BALL BEARING, SEALED v2"
  Placement = pos=(3.05,0,1.33e-14) rot=(0,1,0;1.5708rad)
  shape: bbox 5 x 16 x 16 mm, 8 faces (baked)
FEATURE [Part::Feature] Part__Feature026  label="6153K690_625-2RS SST BALL BEARING, SEALED v003"
  Placement = pos=(3.05,0,1.33e-14) rot=(0,1,0;1.5708rad)
  shape: bbox 5 x 11.37 x 11.37 mm, 8 faces (baked)
FEATURE [Part::Feature] Part__Feature027  label="6153K690_625-2RS SST BALL BEARING, SEALED v004"
  Placement = pos=(3.05,0,1.33e-14) rot=(0,1,0;1.5708rad)
  shape: bbox 2.424 x 2.424 x 2.424 mm, 1 faces (baked)
FEATURE [Part::Feature] Part__Feature028  label="6153K690_625-2RS SST BALL BEARING, SEALED v005"
  Placement = pos=(3.05,0,1.33e-14) rot=(0,1,0;1.5708rad)
  shape: bbox 2.424 x 2.424 x 2.424 mm, 1 faces (baked)
FEATURE [Part::Feature] Part__Feature029  label="6153K690_625-2RS SST BALL BEARING, SEALED v006"
  Placement = pos=(3.05,0,1.33e-14) rot=(0,1,0;1.5708rad)
  shape: bbox 2.424 x 2.424 x 2.424 mm, 1 faces (baked)
FEATURE [Part::Feature] Part__Feature030  label="6153K690_625-2RS SST BALL BEARING, SEALED v007"
  Placement = pos=(3.05,0,1.33e-14) rot=(0,1,0;1.5708rad)
  shape: bbox 2.424 x 2.424 x 2.424 mm, 1 faces (baked)
FEATURE [Part::Feature] Part__Feature031  label="6153K690_625-2RS SST BALL BEARING, SEALED v008"
  Placement = pos=(3.05,0,1.33e-14) rot=(0,1,0;1.5708rad)
  shape: bbox 2.424 x 2.424 x 2.424 mm, 1 faces (baked)
FEATURE [Part::Feature] Part__Feature032  label="6153K690_625-2RS SST BALL BEARING, SEALED v009"
  Placement = pos=(3.05,0,1.33e-14) rot=(0,1,0;1.5708rad)
  shape: bbox 2.424 x 2.424 x 2.424 mm, 1 faces (baked)
FEATURE [Part::Feature] Part__Feature033  label="6153K690_625-2RS SST BALL BEARING, SEALED v010"
  Placement = pos=(3.05,0,1.33e-14) rot=(0,1,0;1.5708rad)
  shape: bbox 2.424 x 2.424 x 2.424 mm, 1 faces (baked)
FEATURE [Part::Feature] Part__Feature034  label="6153K690_625-2RS SST BALL BEARING, SEALED v011"
  Placement = pos=(3.05,0,1.33e-14) rot=(0,1,0;1.5708rad)
  shape: bbox 2.424 x 2.424 x 2.424 mm, 1 faces (baked)
FEATURE [Part::Feature] Part__Feature035  label="6153K690_625-2RS SST BALL BEARING, SEALED v012"
  Placement = pos=(3.05,0,1.33e-14) rot=(0,1,0;1.5708rad)
  shape: bbox 2.424 x 2.424 x 2.424 mm, 1 faces (baked)
FEATURE [Part::Feature] Part__Feature036  label="6153K690_625-2RS SST BALL BEARING, SEALED v013"
  Placement = pos=(3.05,0,1.33e-14) rot=(0,1,0;1.5708rad)
  shape: bbox 2.424 x 2.424 x 2.424 mm, 1 faces (baked)
FEATURE [Part::Feature] Part__Feature037  label="6153K690_625-2RS SST BALL BEARING, SEALED v014"
  Placement = pos=(3.05,0,1.33e-14) rot=(0,1,0;1.5708rad)
  shape: bbox 2.424 x 2.424 x 2.424 mm, 1 faces (baked)
FEATURE [Part::Feature] Part__Feature038  label="6153K690_625-2RS SST BALL BEARING, SEALED v015"
  Placement = pos=(3.05,0,1.33e-14) rot=(0,1,0;1.5708rad)
  shape: bbox 2.424 x 2.424 x 2.424 mm, 1 faces (baked)
FEATURE [Part::Feature] Part__Feature039  label="6153K690_625-2RS SST BALL BEARING, SEALED v016"
  Placement = pos=(3.05,0,1.33e-14) rot=(0,1,0;1.5708rad)
  shape: bbox 1.163 x 11.47 x 11.47 mm, 4 faces (baked)
FEATURE [Part::Feature] Part__Feature040  label="6153K690_625-2RS SST BALL BEARING, SEALED v017"
  Placement = pos=(3.05,0,1.33e-14) rot=(0,1,0;1.5708rad)
  shape: bbox 1.163 x 11.47 x 11.47 mm, 4 faces (baked)
FEATURE [App::Part] _153K690_625_2RS_SST_BALL_BEARING__SEALED_v2  label="6153K690_625-2RS SST BALL BEARING, SEALED v018"
  Group = -> [Part__Feature025,Part__Feature026,Part__Feature027,Part__Feature028,Part__Feature029,Part__Feature030,Part__Feature031,Part__Feature032,Part__Feature033,Part__Feature034,Part__Feature035,Part__Feature036,Part__Feature037,Part__Feature038,Part__Feature039,Part__Feature040]
  Origin = -> Origin014
FEATURE [Part::Feature] Part__Feature041  label="6153K690_625-2RS SST BALL BEARING, SEALED v2 (1)"
  Placement = pos=(-3.05,0,1.33e-14) rot=(0,1,0;1.5708rad)
  shape: bbox 5 x 16 x 16 mm, 8 faces (baked)
FEATURE [Part::Feature] Part__Feature042  label="6153K690_625-2RS SST BALL BEARING, SEALED v2 (1)001"
  Placement = pos=(-3.05,0,1.33e-14) rot=(0,1,0;1.5708rad)
  shape: bbox 5 x 11.37 x 11.37 mm, 8 faces (baked)
FEATURE [Part::Feature] Part__Feature043  label="6153K690_625-2RS SST BALL BEARING, SEALED v2 (1)002"
  Placement = pos=(-3.05,0,1.33e-14) rot=(0,1,0;1.5708rad)
  shape: bbox 2.424 x 2.424 x 2.424 mm, 1 faces (baked)
FEATURE [Part::Feature] Part__Feature044  label="6153K690_625-2RS SST BALL BEARING, SEALED v2 (1)003"
  Placement = pos=(-3.05,0,1.33e-14) rot=(0,1,0;1.5708rad)
  shape: bbox 2.424 x 2.424 x 2.424 mm, 1 faces (baked)
FEATURE [Part::Feature] Part__Feature045  label="6153K690_625-2RS SST BALL BEARING, SEALED v2 (1)004"
  Placement = pos=(-3.05,0,1.33e-14) rot=(0,1,0;1.5708rad)
  shape: bbox 2.424 x 2.424 x 2.424 mm, 1 faces (baked)
FEATURE [Part::Feature] Part__Feature046  label="6153K690_625-2RS SST BALL BEARING, SEALED v2 (1)005"
  Placement = pos=(-3.05,0,1.33e-14) rot=(0,1,0;1.5708rad)
  shape: bbox 2.424 x 2.424 x 2.424 mm, 1 faces (baked)
FEATURE [Part::Feature] Part__Feature047  label="6153K690_625-2RS SST BALL BEARING, SEALED v2 (1)006"
  Placement = pos=(-3.05,0,1.33e-14) rot=(0,1,0;1.5708rad)
  shape: bbox 2.424 x 2.424 x 2.424 mm, 1 faces (baked)
FEATURE [Part::Feature] Part__Feature048  label="6153K690_625-2RS SST BALL BEARING, SEALED v2 (1)007"
  Placement = pos=(-3.05,0,1.33e-14) rot=(0,1,0;1.5708rad)
  shape: bbox 2.424 x 2.424 x 2.424 mm, 1 faces (baked)
FEATURE [Part::Feature] Part__Feature049  label="6153K690_625-2RS SST BALL BEARING, SEALED v2 (1)008"
  Placement = pos=(-3.05,0,1.33e-14) rot=(0,1,0;1.5708rad)
  shape: bbox 2.424 x 2.424 x 2.424 mm, 1 faces (baked)
FEATURE [Part::Feature] Part__Feature050  label="6153K690_625-2RS SST BALL BEARING, SEALED v2 (1)009"
  Placement = pos=(-3.05,0,1.33e-14) rot=(0,1,0;1.5708rad)
  shape: bbox 2.424 x 2.424 x 2.424 mm, 1 faces (baked)
FEATURE [Part::Feature] Part__Feature051  label="6153K690_625-2RS SST BALL BEARING, SEALED v2 (1)010"
  Placement = pos=(-3.05,0,1.33e-14) rot=(0,1,0;1.5708rad)
  shape: bbox 2.424 x 2.424 x 2.424 mm, 1 faces (baked)
FEATURE [Part::Feature] Part__Feature052  label="6153K690_625-2RS SST BALL BEARING, SEALED v2 (1)011"
  Placement = pos=(-3.05,0,1.33e-14) rot=(0,1,0;1.5708rad)
  shape: bbox 2.424 x 2.424 x 2.424 mm, 1 faces (baked)
FEATURE [Part::Feature] Part__Feature053  label="6153K690_625-2RS SST BALL BEARING, SEALED v2 (1)012"
  Placement = pos=(-3.05,0,1.33e-14) rot=(0,1,0;1.5708rad)
  shape: bbox 2.424 x 2.424 x 2.424 mm, 1 faces (baked)
FEATURE [Part::Feature] Part__Feature054  label="6153K690_625-2RS SST BALL BEARING, SEALED v2 (1)013"
  Placement = pos=(-3.05,0,1.33e-14) rot=(0,1,0;1.5708rad)
  shape: bbox 2.424 x 2.424 x 2.424 mm, 1 faces (baked)
FEATURE [Part::Feature] Part__Feature055  label="6153K690_625-2RS SST BALL BEARING, SEALED v2 (1)014"
  Placement = pos=(-3.05,0,1.33e-14) rot=(0,1,0;1.5708rad)
  shape: bbox 1.163 x 11.47 x 11.47 mm, 4 faces (baked)
FEATURE [Part::Feature] Part__Feature056  label="6153K690_625-2RS SST BALL BEARING, SEALED v2 (1)015"
  Placement = pos=(-3.05,0,1.33e-14) rot=(0,1,0;1.5708rad)
  shape: bbox 1.163 x 11.47 x 11.47 mm, 4 faces (baked)
FEATURE [App::Part] _153K690_625_2RS_SST_BALL_BEARING__SEALED_v2__1_  label="6153K690_625-2RS SST BALL BEARING, SEALED v2 (1)016"
  Group = -> [Part__Feature041,Part__Feature042,Part__Feature043,Part__Feature044,Part__Feature045,Part__Feature046,Part__Feature047,Part__Feature048,Part__Feature049,Part__Feature050,Part__Feature051,Part__Feature052,Part__Feature053,Part__Feature054,Part__Feature055,Part__Feature056]
  Origin = -> Origin015
FEATURE [Part::Feature] Part__Feature057  label="Wheel, V-slot Rail for 625 Bearing"
  shape: bbox 10.2 x 24 x 24 mm, 10 faces (baked)
FEATURE [Part::Feature] Part__Feature058  label="91166A240 WSR, FLAT, M5, STL/Z v1"
  Placement = pos=(-0.55,0,0) rot=(0.707107,0,0.707107;3.14159rad)
  shape: bbox 1.1 x 10 x 10 mm, 4 faces (baked)
FEATURE [App::Part] Wheel__V_slot_Rail_625_2Z_Bearing_v4  label="Wheel_BR"
  Group = -> [_153K690_625_2RS_SST_BALL_BEARING__SEALED_v2,_153K690_625_2RS_SST_BALL_BEARING__SEALED_v2__1_,Part__Feature057,Part__Feature058]
  Origin = -> Origin016
  Placement = pos=(-200.5,150,180) rot=(0,0,-1;1.5708rad)
FEATURE [Part::Feature] Part__Feature059  label="6153K690_625-2RS SST BALL BEARING, SEALED v019"
  Placement = pos=(3.05,0,1.33e-14) rot=(0,1,0;1.5708rad)
  shape: bbox 5 x 16 x 16 mm, 8 faces (baked)
FEATURE [Part::Feature] Part__Feature060  label="6153K690_625-2RS SST BALL BEARING, SEALED v020"
  Placement = pos=(3.05,0,1.33e-14) rot=(0,1,0;1.5708rad)
  shape: bbox 5 x 11.37 x 11.37 mm, 8 faces (baked)
FEATURE [Part::Feature] Part__Feature061  label="6153K690_625-2RS SST BALL BEARING, SEALED v021"
  Placement = pos=(3.05,0,1.33e-14) rot=(0,1,0;1.5708rad)
  shape: bbox 2.424 x 2.424 x 2.424 mm, 1 faces (baked)
FEATURE [Part::Feature] Part__Feature062  label="6153K690_625-2RS SST BALL BEARING, SEALED v022"
  Placement = pos=(3.05,0,1.33e-14) rot=(0,1,0;1.5708rad)
  shape: bbox 2.424 x 2.424 x 2.424 mm, 1 faces (baked)
FEATURE [Part::Feature] Part__Feature063  label="6153K690_625-2RS SST BALL BEARING, SEALED v023"
  Placement = pos=(3.05,0,1.33e-14) rot=(0,1,0;1.5708rad)
  shape: bbox 2.424 x 2.424 x 2.424 mm, 1 faces (baked)
FEATURE [Part::Feature] Part__Feature064  label="6153K690_625-2RS SST BALL BEARING, SEALED v024"
  Placement = pos=(3.05,0,1.33e-14) rot=(0,1,0;1.5708rad)
  shape: bbox 2.424 x 2.424 x 2.424 mm, 1 faces (baked)
FEATURE [Part::Feature] Part__Feature065  label="6153K690_625-2RS SST BALL BEARING, SEALED v025"
  Placement = pos=(3.05,0,1.33e-14) rot=(0,1,0;1.5708rad)
  shape: bbox 2.424 x 2.424 x 2.424 mm, 1 faces (baked)
FEATURE [Part::Feature] Part__Feature066  label="6153K690_625-2RS SST BALL BEARING, SEALED v026"
  Placement = pos=(3.05,0,1.33e-14) rot=(0,1,0;1.5708rad)
  shape: bbox 2.424 x 2.424 x 2.424 mm, 1 faces (baked)
FEATURE [Part::Feature] Part__Feature067  label="6153K690_625-2RS SST BALL BEARING, SEALED v027"
  Placement = pos=(3.05,0,1.33e-14) rot=(0,1,0;1.5708rad)
  shape: bbox 2.424 x 2.424 x 2.424 mm, 1 faces (baked)
FEATURE [Part::Feature] Part__Feature068  label="6153K690_625-2RS SST BALL BEARING, SEALED v028"
  Placement = pos=(3.05,0,1.33e-14) rot=(0,1,0;1.5708rad)
  shape: bbox 2.424 x 2.424 x 2.424 mm, 1 faces (baked)
FEATURE [Part::Feature] Part__Feature069  label="6153K690_625-2RS SST BALL BEARING, SEALED v029"
  Placement = pos=(3.05,0,1.33e-14) rot=(0,1,0;1.5708rad)
  shape: bbox 2.424 x 2.424 x 2.424 mm, 1 faces (baked)
FEATURE [Part::Feature] Part__Feature070  label="6153K690_625-2RS SST BALL BEARING, SEALED v030"
  Placement = pos=(3.05,0,1.33e-14) rot=(0,1,0;1.5708rad)
  shape: bbox 2.424 x 2.424 x 2.424 mm, 1 faces (baked)
FEATURE [Part::Feature] Part__Feature071  label="6153K690_625-2RS SST BALL BEARING, SEALED v031"
  Placement = pos=(3.05,0,1.33e-14) rot=(0,1,0;1.5708rad)
  shape: bbox 2.424 x 2.424 x 2.424 mm, 1 faces (baked)
FEATURE [Part::Feature] Part__Feature072  label="6153K690_625-2RS SST BALL BEARING, SEALED v032"
  Placement = pos=(3.05,0,1.33e-14) rot=(0,1,0;1.5708rad)
  shape: bbox 2.424 x 2.424 x 2.424 mm, 1 faces (baked)
FEATURE [Part::Feature] Part__Feature073  label="6153K690_625-2RS SST BALL BEARING, SEALED v033"
  Placement = pos=(3.05,0,1.33e-14) rot=(0,1,0;1.5708rad)
  shape: bbox 1.163 x 11.47 x 11.47 mm, 4 faces (baked)
FEATURE [Part::Feature] Part__Feature074  label="6153K690_625-2RS SST BALL BEARING, SEALED v034"
  Placement = pos=(3.05,0,1.33e-14) rot=(0,1,0;1.5708rad)
  shape: bbox 1.163 x 11.47 x 11.47 mm, 4 faces (baked)
FEATURE [Part::Feature] Part__Feature075  label="6153K690_625-2RS SST BALL BEARING, SEALED v2 (1)017"
  Placement = pos=(-3.05,0,1.33e-14) rot=(0,1,0;1.5708rad)
  shape: bbox 5 x 16 x 16 mm, 8 faces (baked)
FEATURE [Part::Feature] Part__Feature076  label="6153K690_625-2RS SST BALL BEARING, SEALED v2 (1)018"
  Placement = pos=(-3.05,0,1.33e-14) rot=(0,1,0;1.5708rad)
  shape: bbox 5 x 11.37 x 11.37 mm, 8 faces (baked)
FEATURE [Part::Feature] Part__Feature077  label="6153K690_625-2RS SST BALL BEARING, SEALED v2 (1)019"
  Placement = pos=(-3.05,0,1.33e-14) rot=(0,1,0;1.5708rad)
  shape: bbox 2.424 x 2.424 x 2.424 mm, 1 faces (baked)
FEATURE [Part::Feature] Part__Feature078  label="6153K690_625-2RS SST BALL BEARING, SEALED v2 (1)020"
  Placement = pos=(-3.05,0,1.33e-14) rot=(0,1,0;1.5708rad)
  shape: bbox 2.424 x 2.424 x 2.424 mm, 1 faces (baked)
FEATURE [Part::Feature] Part__Feature079  label="6153K690_625-2RS SST BALL BEARING, SEALED v2 (1)021"
  Placement = pos=(-3.05,0,1.33e-14) rot=(0,1,0;1.5708rad)
  shape: bbox 2.424 x 2.424 x 2.424 mm, 1 faces (baked)
FEATURE [Part::Feature] Part__Feature080  label="6153K690_625-2RS SST BALL BEARING, SEALED v2 (1)022"
  Placement = pos=(-3.05,0,1.33e-14) rot=(0,1,0;1.5708rad)
  shape: bbox 2.424 x 2.424 x 2.424 mm, 1 faces (baked)
FEATURE [Part::Feature] Part__Feature081  label="6153K690_625-2RS SST BALL BEARING, SEALED v2 (1)023"
  Placement = pos=(-3.05,0,1.33e-14) rot=(0,1,0;1.5708rad)
  shape: bbox 2.424 x 2.424 x 2.424 mm, 1 faces (baked)
FEATURE [Part::Feature] Part__Feature082  label="6153K690_625-2RS SST BALL BEARING, SEALED v2 (1)024"
  Placement = pos=(-3.05,0,1.33e-14) rot=(0,1,0;1.5708rad)
  shape: bbox 2.424 x 2.424 x 2.424 mm, 1 faces (baked)
FEATURE [Part::Feature] Part__Feature083  label="6153K690_625-2RS SST BALL BEARING, SEALED v2 (1)025"
  Placement = pos=(-3.05,0,1.33e-14) rot=(0,1,0;1.5708rad)
  shape: bbox 2.424 x 2.424 x 2.424 mm, 1 faces (baked)
FEATURE [Part::Feature] Part__Feature084  label="6153K690_625-2RS SST BALL BEARING, SEALED v2 (1)026"
  Placement = pos=(-3.05,0,1.33e-14) rot=(0,1,0;1.5708rad)
  shape: bbox 2.424 x 2.424 x 2.424 mm, 1 faces (baked)
FEATURE [Part::Feature] Part__Feature085  label="6153K690_625-2RS SST BALL BEARING, SEALED v2 (1)027"
  Placement = pos=(-3.05,0,1.33e-14) rot=(0,1,0;1.5708rad)
  shape: bbox 2.424 x 2.424 x 2.424 mm, 1 faces (baked)
FEATURE [Part::Feature] Part__Feature086  label="6153K690_625-2RS SST BALL BEARING, SEALED v2 (1)028"
  Placement = pos=(-3.05,0,1.33e-14) rot=(0,1,0;1.5708rad)
  shape: bbox 2.424 x 2.424 x 2.424 mm, 1 faces (baked)
FEATURE [Part::Feature] Part__Feature087  label="6153K690_625-2RS SST BALL BEARING, SEALED v2 (1)029"
  Placement = pos=(-3.05,0,1.33e-14) rot=(0,1,0;1.5708rad)
  shape: bbox 2.424 x 2.424 x 2.424 mm, 1 faces (baked)
FEATURE [Part::Feature] Part__Feature088  label="6153K690_625-2RS SST BALL BEARING, SEALED v2 (1)030"
  Placement = pos=(-3.05,0,1.33e-14) rot=(0,1,0;1.5708rad)
  shape: bbox 2.424 x 2.424 x 2.424 mm, 1 faces (baked)
FEATURE [Part::Feature] Part__Feature089  label="6153K690_625-2RS SST BALL BEARING, SEALED v2 (1)031"
  Placement = pos=(-3.05,0,1.33e-14) rot=(0,1,0;1.5708rad)
  shape: bbox 1.163 x 11.47 x 11.47 mm, 4 faces (baked)
FEATURE [Part::Feature] Part__Feature090  label="6153K690_625-2RS SST BALL BEARING, SEALED v2 (1)032"
  Placement = pos=(-3.05,0,1.33e-14) rot=(0,1,0;1.5708rad)
  shape: bbox 1.163 x 11.47 x 11.47 mm, 4 faces (baked)
FEATURE [Part::Feature] Part__Feature091  label="Wheel, V-slot Rail for 625 Bearing001"
  shape: bbox 10.2 x 24 x 24 mm, 10 faces (baked)
FEATURE [Part::Feature] Part__Feature092  label="91166A240 WSR, FLAT, M5, STL/Z v002"
  Placement = pos=(-0.55,0,0) rot=(0.707107,0,0.707107;3.14159rad)
  shape: bbox 1.1 x 10 x 10 mm, 4 faces (baked)
FEATURE [App::Part] _153K690_625_2RS_SST_BALL_BEARING__SEALED_v003  label="6153K690_625-2RS SST BALL BEARING, SEALED v035"
  Group = -> [Part__Feature059,Part__Feature060,Part__Feature061,Part__Feature062,Part__Feature063,Part__Feature064,Part__Feature065,Part__Feature066,Part__Feature067,Part__Feature068,Part__Feature069,Part__Feature070,Part__Feature071,Part__Feature072,Part__Feature073,Part__Feature074]
  Origin = -> Origin017
FEATURE [App::Part] _153K690_625_2RS_SST_BALL_BEARING__SEALED_v2__1_001  label="6153K690_625-2RS SST BALL BEARING, SEALED v2 (1)033"
  Group = -> [Part__Feature075,Part__Feature076,Part__Feature077,Part__Feature078,Part__Feature079,Part__Feature080,Part__Feature081,Part__Feature082,Part__Feature083,Part__Feature084,Part__Feature085,Part__Feature086,Part__Feature087,Part__Feature088,Part__Feature089,Part__Feature090]
  Origin = -> Origin018
FEATURE [App::Part] Wheel__V_slot_Rail_625_2Z_Bearing_v005  label="Wheel_BL"
  Group = -> [_153K690_625_2RS_SST_BALL_BEARING__SEALED_v003,_153K690_625_2RS_SST_BALL_BEARING__SEALED_v2__1_001,Part__Feature091,Part__Feature092]
  Origin = -> Origin019
  Placement = pos=(-139.49,149.99,180) rot=(0,0,-1;1.5708rad)
FEATURE [Part::Feature] Part__Feature093  label="6153K690_625-2RS SST BALL BEARING, SEALED v036"
  Placement = pos=(3.05,0,1.33e-14) rot=(0,1,0;1.5708rad)
  shape: bbox 5 x 16 x 16 mm, 8 faces (baked)
FEATURE [Part::Feature] Part__Feature094  label="6153K690_625-2RS SST BALL BEARING, SEALED v037"
  Placement = pos=(3.05,0,1.33e-14) rot=(0,1,0;1.5708rad)
  shape: bbox 5 x 11.37 x 11.37 mm, 8 faces (baked)
FEATURE [Part::Feature] Part__Feature095  label="6153K690_625-2RS SST BALL BEARING, SEALED v038"
  Placement = pos=(3.05,0,1.33e-14) rot=(0,1,0;1.5708rad)
  shape: bbox 2.424 x 2.424 x 2.424 mm, 1 faces (baked)
FEATURE [Part::Feature] Part__Feature096  label="6153K690_625-2RS SST BALL BEARING, SEALED v039"
  Placement = pos=(3.05,0,1.33e-14) rot=(0,1,0;1.5708rad)
  shape: bbox 2.424 x 2.424 x 2.424 mm, 1 faces (baked)
FEATURE [Part::Feature] Part__Feature097  label="6153K690_625-2RS SST BALL BEARING, SEALED v040"
  Placement = pos=(3.05,0,1.33e-14) rot=(0,1,0;1.5708rad)
  shape: bbox 2.424 x 2.424 x 2.424 mm, 1 faces (baked)
FEATURE [Part::Feature] Part__Feature098  label="6153K690_625-2RS SST BALL BEARING, SEALED v041"
  Placement = pos=(3.05,0,1.33e-14) rot=(0,1,0;1.5708rad)
  shape: bbox 2.424 x 2.424 x 2.424 mm, 1 faces (baked)
FEATURE [Part::Feature] Part__Feature099  label="6153K690_625-2RS SST BALL BEARING, SEALED v042"
  Placement = pos=(3.05,0,1.33e-14) rot=(0,1,0;1.5708rad)
  shape: bbox 2.424 x 2.424 x 2.424 mm, 1 faces (baked)
FEATURE [Part::Feature] Part__Feature100  label="6153K690_625-2RS SST BALL BEARING, SEALED v043"
  Placement = pos=(3.05,0,1.33e-14) rot=(0,1,0;1.5708rad)
  shape: bbox 2.424 x 2.424 x 2.424 mm, 1 faces (baked)
FEATURE [Part::Feature] Part__Feature101  label="6153K690_625-2RS SST BALL BEARING, SEALED v044"
  Placement = pos=(3.05,0,1.33e-14) rot=(0,1,0;1.5708rad)
  shape: bbox 2.424 x 2.424 x 2.424 mm, 1 faces (baked)
FEATURE [Part::Feature] Part__Feature102  label="6153K690_625-2RS SST BALL BEARING, SEALED v045"
  Placement = pos=(3.05,0,1.33e-14) rot=(0,1,0;1.5708rad)
  shape: bbox 2.424 x 2.424 x 2.424 mm, 1 faces (baked)
FEATURE [Part::Feature] Part__Feature103  label="6153K690_625-2RS SST BALL BEARING, SEALED v046"
  Placement = pos=(3.05,0,1.33e-14) rot=(0,1,0;1.5708rad)
  shape: bbox 2.424 x 2.424 x 2.424 mm, 1 faces (baked)
FEATURE [Part::Feature] Part__Feature104  label="6153K690_625-2RS SST BALL BEARING, SEALED v047"
  Placement = pos=(3.05,0,1.33e-14) rot=(0,1,0;1.5708rad)
  shape: bbox 2.424 x 2.424 x 2.424 mm, 1 faces (baked)
FEATURE [Part::Feature] Part__Feature105  label="6153K690_625-2RS SST BALL BEARING, SEALED v048"
  Placement = pos=(3.05,0,1.33e-14) rot=(0,1,0;1.5708rad)
  shape: bbox 2.424 x 2.424 x 2.424 mm, 1 faces (baked)
FEATURE [Part::Feature] Part__Feature106  label="6153K690_625-2RS SST BALL BEARING, SEALED v049"
  Placement = pos=(3.05,0,1.33e-14) rot=(0,1,0;1.5708rad)
  shape: bbox 2.424 x 2.424 x 2.424 mm, 1 faces (baked)
FEATURE [Part::Feature] Part__Feature107  label="6153K690_625-2RS SST BALL BEARING, SEALED v050"
  Placement = pos=(3.05,0,1.33e-14) rot=(0,1,0;1.5708rad)
  shape: bbox 1.163 x 11.47 x 11.47 mm, 4 faces (baked)
FEATURE [Part::Feature] Part__Feature108  label="6153K690_625-2RS SST BALL BEARING, SEALED v051"
  Placement = pos=(3.05,0,1.33e-14) rot=(0,1,0;1.5708rad)
  shape: bbox 1.163 x 11.47 x 11.47 mm, 4 faces (baked)
FEATURE [Part::Feature] Part__Feature109  label="6153K690_625-2RS SST BALL BEARING, SEALED v2 (1)034"
  Placement = pos=(-3.05,0,1.33e-14) rot=(0,1,0;1.5708rad)
  shape: bbox 5 x 16 x 16 mm, 8 faces (baked)
FEATURE [Part::Feature] Part__Feature110  label="6153K690_625-2RS SST BALL BEARING, SEALED v2 (1)035"
  Placement = pos=(-3.05,0,1.33e-14) rot=(0,1,0;1.5708rad)
  shape: bbox 5 x 11.37 x 11.37 mm, 8 faces (baked)
FEATURE [Part::Feature] Part__Feature111  label="6153K690_625-2RS SST BALL BEARING, SEALED v2 (1)036"
  Placement = pos=(-3.05,0,1.33e-14) rot=(0,1,0;1.5708rad)
  shape: bbox 2.424 x 2.424 x 2.424 mm, 1 faces (baked)
FEATURE [Part::Feature] Part__Feature112  label="6153K690_625-2RS SST BALL BEARING, SEALED v2 (1)037"
  Placement = pos=(-3.05,0,1.33e-14) rot=(0,1,0;1.5708rad)
  shape: bbox 2.424 x 2.424 x 2.424 mm, 1 faces (baked)
FEATURE [Part::Feature] Part__Feature113  label="6153K690_625-2RS SST BALL BEARING, SEALED v2 (1)038"
  Placement = pos=(-3.05,0,1.33e-14) rot=(0,1,0;1.5708rad)
  shape: bbox 2.424 x 2.424 x 2.424 mm, 1 faces (baked)
FEATURE [Part::Feature] Part__Feature114  label="6153K690_625-2RS SST BALL BEARING, SEALED v2 (1)039"
  Placement = pos=(-3.05,0,1.33e-14) rot=(0,1,0;1.5708rad)
  shape: bbox 2.424 x 2.424 x 2.424 mm, 1 faces (baked)
FEATURE [Part::Feature] Part__Feature115  label="6153K690_625-2RS SST BALL BEARING, SEALED v2 (1)040"
  Placement = pos=(-3.05,0,1.33e-14) rot=(0,1,0;1.5708rad)
  shape: bbox 2.424 x 2.424 x 2.424 mm, 1 faces (baked)
FEATURE [Part::Feature] Part__Feature116  label="6153K690_625-2RS SST BALL BEARING, SEALED v2 (1)041"
  Placement = pos=(-3.05,0,1.33e-14) rot=(0,1,0;1.5708rad)
  shape: bbox 2.424 x 2.424 x 2.424 mm, 1 faces (baked)
FEATURE [Part::Feature] Part__Feature117  label="6153K690_625-2RS SST BALL BEARING, SEALED v2 (1)042"
  Placement = pos=(-3.05,0,1.33e-14) rot=(0,1,0;1.5708rad)
  shape: bbox 2.424 x 2.424 x 2.424 mm, 1 faces (baked)
FEATURE [Part::Feature] Part__Feature118  label="6153K690_625-2RS SST BALL BEARING, SEALED v2 (1)043"
  Placement = pos=(-3.05,0,1.33e-14) rot=(0,1,0;1.5708rad)
  shape: bbox 2.424 x 2.424 x 2.424 mm, 1 faces (baked)
FEATURE [Part::Feature] Part__Feature119  label="6153K690_625-2RS SST BALL BEARING, SEALED v2 (1)044"
  Placement = pos=(-3.05,0,1.33e-14) rot=(0,1,0;1.5708rad)
  shape: bbox 2.424 x 2.424 x 2.424 mm, 1 faces (baked)
FEATURE [Part::Feature] Part__Feature120  label="6153K690_625-2RS SST BALL BEARING, SEALED v2 (1)045"
  Placement = pos=(-3.05,0,1.33e-14) rot=(0,1,0;1.5708rad)
  shape: bbox 2.424 x 2.424 x 2.424 mm, 1 faces (baked)
FEATURE [Part::Feature] Part__Feature121  label="6153K690_625-2RS SST BALL BEARING, SEALED v2 (1)046"
  Placement = pos=(-3.05,0,1.33e-14) rot=(0,1,0;1.5708rad)
  shape: bbox 2.424 x 2.424 x 2.424 mm, 1 faces (baked)
FEATURE [Part::Feature] Part__Feature122  label="6153K690_625-2RS SST BALL BEARING, SEALED v2 (1)047"
  Placement = pos=(-3.05,0,1.33e-14) rot=(0,1,0;1.5708rad)
  shape: bbox 2.424 x 2.424 x 2.424 mm, 1 faces (baked)
FEATURE [Part::Feature] Part__Feature123  label="6153K690_625-2RS SST BALL BEARING, SEALED v2 (1)048"
  Placement = pos=(-3.05,0,1.33e-14) rot=(0,1,0;1.5708rad)
  shape: bbox 1.163 x 11.47 x 11.47 mm, 4 faces (baked)
FEATURE [Part::Feature] Part__Feature124  label="6153K690_625-2RS SST BALL BEARING, SEALED v2 (1)049"
  Placement = pos=(-3.05,0,1.33e-14) rot=(0,1,0;1.5708rad)
  shape: bbox 1.163 x 11.47 x 11.47 mm, 4 faces (baked)
FEATURE [Part::Feature] Part__Feature125  label="Wheel, V-slot Rail for 625 Bearing002"
  shape: bbox 10.2 x 24 x 24 mm, 10 faces (baked)
FEATURE [Part::Feature] Part__Feature126  label="91166A240 WSR, FLAT, M5, STL/Z v003"
  Placement = pos=(-0.55,0,0) rot=(0.707107,0,0.707107;3.14159rad)
  shape: bbox 1.1 x 10 x 10 mm, 4 faces (baked)
FEATURE [App::Part] _153K690_625_2RS_SST_BALL_BEARING__SEALED_v004  label="6153K690_625-2RS SST BALL BEARING, SEALED v052"
  Group = -> [Part__Feature093,Part__Feature094,Part__Feature095,Part__Feature096,Part__Feature097,Part__Feature098,Part__Feature099,Part__Feature100,Part__Feature101,Part__Feature102,Part__Feature103,Part__Feature104,Part__Feature105,Part__Feature106,Part__Feature107,Part__Feature108]
  Origin = -> Origin020
FEATURE [App::Part] _153K690_625_2RS_SST_BALL_BEARING__SEALED_v2__1_002  label="6153K690_625-2RS SST BALL BEARING, SEALED v2 (1)050"
  Group = -> [Part__Feature109,Part__Feature110,Part__Feature111,Part__Feature112,Part__Feature113,Part__Feature114,Part__Feature115,Part__Feature116,Part__Feature117,Part__Feature118,Part__Feature119,Part__Feature120,Part__Feature121,Part__Feature122,Part__Feature123,Part__Feature124]
  Origin = -> Origin021
FEATURE [App::Part] Wheel__V_slot_Rail_625_2Z_Bearing_v006  label="Wheel_TR"
  Group = -> [_153K690_625_2RS_SST_BALL_BEARING__SEALED_v004,_153K690_625_2RS_SST_BALL_BEARING__SEALED_v2__1_002,Part__Feature125,Part__Feature126]
  Origin = -> Origin022
  Placement = pos=(-200.5,150,220) rot=(0,0,-1;1.5708rad)
FEATURE [Sketcher::SketchObject] Sketch023
  ArcFitTolerance = 1e-06
  AttachmentSupport = -> [XZ_Plane023]
  FullyConstrained = true
  MakeInternals = false
  MapMode = 5
  Placement = pos=(0,0,0) rot=(1,0,0;1.5708rad)
  sketch-geometry (4):
    g0: LineSegment StartX=-208 StartY=215 StartZ=0 EndX=-132 EndY=215 EndZ=0
    g1: LineSegment StartX=-132 StartY=215 StartZ=0 EndX=-132 EndY=185 EndZ=0
    g2: LineSegment StartX=-132 StartY=185 StartZ=0 EndX=-208 EndY=185 EndZ=0
    g3: LineSegment StartX=-208 StartY=185 StartZ=0 EndX=-208 EndY=215 EndZ=0
  constraints (12):
    c: Horizontal(g0)
    c: Coincident(g1,g0)
    c: Vertical(g1)
    c: Coincident(g2,g1)
    c: Horizontal(g2)
    c: DistanceX(g1,g-1) = 132
    c: DistanceY(g-1,g1) = 185
    c: Coincident(g3,g2)
    c: Coincident(g3,g0)
    c: Vertical(g3)
    c: DistanceX(g0,g0) = 76
    c: DistanceY(g3,g3) = 30
FEATURE [PartDesign::Pad] Pad006
  Direction = (0,-1,2e-16)
  Length = 4
  Length2 = 10
  Placement = pos=(0,0,0) rot=(1,0,0;1.5708rad)
  Profile = -> Sketch023
  ReferenceAxis = -> Sketch023 [N_Axis]
  Suppressed = false
  Type = 0
FEATURE [Sketcher::SketchObject] Sketch024
  ArcFitTolerance = 1e-06
  AttachmentOffset = pos=(0,0,-132) rot=(0,0,1;0rad)
  AttachmentSupport = -> [YZ_Plane023]
  FullyConstrained = true
  MakeInternals = false
  MapMode = 5
  Placement = pos=(-132,0,0) rot=(0.57735,0.57735,0.57735;2.0944rad)
  sketch-geometry (12):
    g0: LineSegment StartX=0 StartY=215 StartZ=0 EndX=0 EndY=210 EndZ=0
    g1: LineSegment StartX=0 StartY=210 StartZ=0 EndX=17 EndY=210 EndZ=0
    g2: LineSegment StartX=13 StartY=228 StartZ=0 EndX=17 EndY=228 EndZ=0
    g3: LineSegment StartX=17 StartY=228 StartZ=0 EndX=17 EndY=210 EndZ=0
    g4: LineSegment StartX=0 StartY=190 StartZ=0 EndX=17 EndY=190 EndZ=0
    g5: LineSegment StartX=17 StartY=190 StartZ=0 EndX=17 EndY=172 EndZ=0
    g6: LineSegment StartX=17 StartY=172 StartZ=0 EndX=13 EndY=172 EndZ=0
    g7: LineSegment StartX=0 StartY=185 StartZ=0 EndX=0 EndY=190 EndZ=0
    g8: LineSegment StartX=13 StartY=228 StartZ=0 EndX=13 EndY=215 EndZ=0
    g9: LineSegment StartX=0 StartY=215 StartZ=0 EndX=13 EndY=215 EndZ=0
    g10: LineSegment StartX=0 StartY=185 StartZ=0 EndX=13 EndY=185 EndZ=0
    g11: LineSegment StartX=13 StartY=185 StartZ=0 EndX=13 EndY=172 EndZ=0
  constraints (36):
    c: Coincident(g0,g1)
    c: Vertical(g0)
    c: Horizontal(g1)
    c: Horizontal(g2)
    c: Coincident(g3,g2)
    c: Coincident(g3,g1)
    c: Vertical(g3)
    c: DistanceY(g3,g3) = 18
    c: DistanceX(g2,g2) = 4
    c: DistanceY(g0,g0) = 5
    c: DistanceY(g-1,g0) = 210
    c: PointOnObject(g0,g-2)
    c: PointOnObject(g4,g-2)
    c: Horizontal(g4)
    c: Distance(g5) = 18
    c: Coincident(g5,g4)
    c: Vertical(g5)
    c: Distance(g6) = 4
    c: Coincident(g6,g5)
    c: Horizontal(g6)
    c: Coincident(g7,g4)
    c: Vertical(g7)
    c: DistanceY(g7,g7) = 5
    c: DistanceY(g-1,g4) = 190
    c: DistanceX(g0,g2) = 13
    c: DistanceX(g7,g6) = 13
    c: Coincident(g8,g2)
    c: Vertical(g8)
    c: Coincident(g9,g0)
    c: Coincident(g9,g8)
    c: Horizontal(g9)
    c: Coincident(g10,g7)
    c: Horizontal(g10)
    c: Coincident(g11,g10)
    c: Coincident(g11,g6)
    c: Vertical(g11)
FEATURE [PartDesign::Pad] Pad007
  BaseFeature = -> Pad006
  Direction = (1,0,0)
  Length = 76
  Length2 = 10
  Placement = pos=(0,0,0) rot=(1,0,0;1.5708rad)
  Profile = -> Sketch024
  ReferenceAxis = -> Sketch024 [N_Axis]
  Reversed = true
  Suppressed = false
  Type = 0
FEATURE [Sketcher::SketchObject] Sketch025
  ArcFitTolerance = 1e-06
  FullyConstrained = true
  MakeInternals = false
  MapMode = 5
  Placement = pos=(3e-15,20,-1.05e-14) rot=(0.57735,0.57735,0.57735;4.18879rad)
  sketch-geometry (8):
    g0: Circle CenterX=0 CenterY=-20 CenterZ=0 NormalX=0 NormalY=0 NormalZ=1 AngleXU=0 Radius=2.5
    g1: Circle CenterX=0 CenterY=-80 CenterZ=0 NormalX=0 NormalY=0 NormalZ=1 AngleXU=0 Radius=2.5
    g2: Circle CenterX=40 CenterY=-80 CenterZ=0 NormalX=0 NormalY=0 NormalZ=1 AngleXU=0 Radius=2.5
    g3: LineSegment [constr] StartX=0 StartY=-80 StartZ=0 EndX=40 EndY=-80 EndZ=0
    g4: LineSegment [constr] StartX=0 StartY=-80 StartZ=0 EndX=0 EndY=-20 EndZ=0
    g5: Circle CenterX=40 CenterY=-20 CenterZ=0 NormalX=0 NormalY=0 NormalZ=1 AngleXU=0 Radius=2.5
    g6: LineSegment [constr] StartX=40 StartY=-20 StartZ=0 EndX=0 EndY=-20 EndZ=0
    g7: LineSegment [constr] StartX=40 StartY=-20 StartZ=0 EndX=40 EndY=-80 EndZ=0
  constraints (20):
    c: Equal(g0,g1)
    c: Equal(g1,g2)
    c: Diameter(g0) = 5
    c: DistanceY(g1,g-1) = 80
    c: Coincident(g3,g1)
    c: Coincident(g3,g2)
    c: Horizontal(g3)
    c: Coincident(g4,g1)
    c: Coincident(g4,g0)
    c: Vertical(g4)
    c: DistanceY(g0,g-1) = 20
    c: DistanceX(g3,g3) = 40
    c: PointOnObject(g0,g-2)
    c: Equal(g5,g0)
    c: Coincident(g6,g5)
    c: Coincident(g6,g0)
    c: Horizontal(g6)
    c: Coincident(g7,g5)
    c: Coincident(g7,g2)
    c: Vertical(g7)
FEATURE [PartDesign::Hole] Hole003
  BaseFeature = -> Pocket003
  CustomThreadClearance = 0
  Depth = 25
  DepthType = 0
  Diameter = 5.5
  DrillForDepth = false
  DrillPoint = 1
  DrillPointAngle = 118
  HoleCutCountersinkAngle = 90
  HoleCutCustomValues = false
  HoleCutDepth = 0
  HoleCutDiameter = 6.1
  HoleCutType = 0
  ModelThread = false
  Placement = pos=(0,0,0) rot=(1,1,1;2.0944rad)
  Profile = -> Sketch025
  Suppressed = false
  Tapered = false
  TaperedAngle = 90
  ThreadClass = 0
  ThreadDepth = 25
  ThreadDepthType = 0
  ThreadDirection = 0
  ThreadFit = 0
  ThreadSize = 13
  ThreadType = 1
  Threaded = false
  UseCustomThreadClearance = false
FEATURE [Sketcher::SketchObject] Sketch028
  ArcFitTolerance = 1e-06
  FullyConstrained = true
  MakeInternals = false
  MapMode = 5
  Placement = pos=(0,20,0) rot=(-1,0,0;1.5708rad)
  sketch-geometry (8):
    g0: Circle CenterX=-200 CenterY=-220 CenterZ=0 NormalX=0 NormalY=0 NormalZ=1 AngleXU=0 Radius=2.125
    g1: LineSegment [constr] StartX=-220 StartY=-200 StartZ=0 EndX=-120 EndY=-200 EndZ=0
    g2: Circle CenterX=-200 CenterY=-180 CenterZ=0 NormalX=0 NormalY=0 NormalZ=1 AngleXU=0 Radius=2.125
    g3: LineSegment [constr] StartX=-170 StartY=-170 StartZ=0 EndX=-170 EndY=-228 EndZ=0
    g4: Circle CenterX=-140 CenterY=-180 CenterZ=0 NormalX=0 NormalY=0 NormalZ=1 AngleXU=0 Radius=2.125
    g5: Circle CenterX=-140 CenterY=-220 CenterZ=0 NormalX=0 NormalY=0 NormalZ=1 AngleXU=0 Radius=2.125
    g6: LineSegment [constr] StartX=-200 StartY=-220 StartZ=0 EndX=-140 EndY=-220 EndZ=0
    g7: LineSegment [constr] StartX=-140 StartY=-220 StartZ=0 EndX=-140 EndY=-180 EndZ=0
  constraints (22):
    c: Diameter(g0) = 4.25
    c: Horizontal(g1)
    c: DistanceX(g1,g1) = 100
    c: DistanceY(g1,g-1) = 200
    c: DistanceX(g1,g-1) = 120
    c: Equal(g0,g2)
    c: Symmetric(g0,g2,g1)
    c: Distance(g3) = 58
    c: Vertical(g3)
    c: DistanceX(g3,g-1) = 170
    c: DistanceY(g3,g-1) = 170
    c: Equal(g2,g4)
    c: Symmetric(g2,g4,g3)
    c: Coincident(g6,g0)
    c: Coincident(g6,g5)
    c: Horizontal(g6)
    c: Coincident(g7,g5)
    c: Coincident(g7,g4)
    c: Vertical(g7)
    c: Equal(g5,g4)
    c: DistanceX(g0,g3) = 30
    c: DistanceY(g0,g1) = 20
FEATURE [PartDesign::Hole] Hole004
  BaseFeature = -> Pad007
  CustomThreadClearance = 0
  Depth = 209.769
  DepthType = 1
  Diameter = 5.5
  DrillForDepth = false
  DrillPoint = 0
  DrillPointAngle = 118
  HoleCutCountersinkAngle = 90
  HoleCutCustomValues = false
  HoleCutDepth = 0
  HoleCutDiameter = 6.1
  HoleCutType = 0
  ModelThread = false
  Placement = pos=(0,0,0) rot=(1,0,0;1.5708rad)
  Profile = -> Sketch028
  Suppressed = false
  Tapered = false
  TaperedAngle = 90
  ThreadClass = 0
  ThreadDepth = 209.769
  ThreadDepthType = 0
  ThreadDirection = 0
  ThreadFit = 0
  ThreadSize = 13
  ThreadType = 1
  Threaded = false
  UseCustomThreadClearance = false
FEATURE [Part::FeaturePython] Insert  label="M3x5.74-Insert"  # WARN: FeaturePython — macro-defined, semantics opaque (R4)
  BaseObject = -> Body002 [Hole003.Edge14]
  Diameter = 3
  ExternalDiam = 4.55
  Invert = false
  LeftHanded = false
  Length = 5.74
  MatchOuter = false
  OffsetAngle = 0
  Placement = pos=(-161,181,172) rot=(0,0,1;0rad)
  Thread = false
  Type = 0
FEATURE [Part::FeaturePython] Insert001  label="M3x5.74-Insert301"  # WARN: FeaturePython — macro-defined, semantics opaque (R4)
  BaseObject = -> Body002 [Hole003.Edge16]
  Diameter = 3
  ExternalDiam = 4.55
  Invert = false
  LeftHanded = false
  Length = 5.74
  MatchOuter = false
  OffsetAngle = 0
  Placement = pos=(-170,172,172) rot=(0,0,1;0rad)
  Thread = false
  Type = 0
FEATURE [Part::FeaturePython] Insert002  label="M3x5.74-Insert302"  # WARN: FeaturePython — macro-defined, semantics opaque (R4)
  BaseObject = -> Body002 [Hole003.Edge12]
  Diameter = 3
  ExternalDiam = 4.55
  Invert = false
  LeftHanded = false
  Length = 5.74
  MatchOuter = false
  OffsetAngle = 0
  Placement = pos=(-179,181,172) rot=(0,0,1;0rad)
  Thread = false
  Type = 0
FEATURE [Part::FeaturePython] Insert003  label="M3x5.74-Insert303"  # WARN: FeaturePython — macro-defined, semantics opaque (R4)
  BaseObject = -> Body002 [Hole003.Edge13]
  Diameter = 3
  ExternalDiam = 4.55
  Invert = false
  LeftHanded = false
  Length = 5.74
  MatchOuter = false
  OffsetAngle = 0
  Placement = pos=(-170,190,172) rot=(0,0,1;0rad)
  Thread = false
  Type = 0
FEATURE [Part::FeaturePython] Screw021  label="M3x8-Screw008"  # WARN: FeaturePython — macro-defined, semantics opaque (R4)
  BaseObject = -> Body001 [Hole002.Edge12]
  Diameter = 4
  Invert = false
  LeftHanded = false
  Length = 2
  LengthCustom = 8
  MatchOuter = false
  OffsetAngle = 0
  Placement = pos=(-162,181,181.5) rot=(0,0,1;0rad)
  Thread = false
  Type = 75
FEATURE [Part::FeaturePython] Screw022  label="M3x8-Screw009"  # WARN: FeaturePython — macro-defined, semantics opaque (R4)
  BaseObject = -> Body001 [Hole002.Edge9]
  Diameter = 4
  Invert = false
  LeftHanded = false
  Length = 2
  LengthCustom = 8
  MatchOuter = false
  OffsetAngle = 0
  Placement = pos=(-170,173,181.5) rot=(0,0,1;0rad)
  Thread = false
  Type = 75
FEATURE [Part::FeaturePython] Screw023  label="M3x8-Screw010"  # WARN: FeaturePython — macro-defined, semantics opaque (R4)
  BaseObject = -> Body001 [Hole002.Edge10]
  Diameter = 4
  Invert = false
  LeftHanded = false
  Length = 2
  LengthCustom = 8
  MatchOuter = false
  OffsetAngle = 0
  Placement = pos=(-178,181,181.5) rot=(0,0,1;0rad)
  Thread = false
  Type = 75
FEATURE [Part::FeaturePython] Screw024  label="M3x8-Screw011"  # WARN: FeaturePython — macro-defined, semantics opaque (R4)
  BaseObject = -> Body001 [Hole002.Edge13]
  Diameter = 4
  Invert = false
  LeftHanded = false
  Length = 2
  LengthCustom = 8
  MatchOuter = false
  OffsetAngle = 0
  Placement = pos=(-170,189,181.5) rot=(0,0,1;0rad)
  Thread = false
  Type = 75
FEATURE [Sketcher::SketchObject] Sketch030
  ArcFitTolerance = 1e-06
  AttachmentSupport = -> [Hole003]
  FullyConstrained = true
  MakeInternals = false
  MapMode = 5
  Placement = pos=(4.2e-15,19,0) rot=(0.57735,0.57735,0.57735;4.18879rad)
  sketch-geometry (20):
    g0: LineSegment [constr] StartX=40 StartY=-27.5 StartZ=0 EndX=0 EndY=-27.5 EndZ=0
    g1: LineSegment [constr] StartX=0 StartY=-27.5 StartZ=0 EndX=0 EndY=-72.5 EndZ=0
    g2: LineSegment [constr] StartX=0 StartY=-72.5 StartZ=0 EndX=40 EndY=-72.5 EndZ=0
    g3: LineSegment [constr] StartX=40 StartY=-72.5 StartZ=0 EndX=40 EndY=-27.5 EndZ=0
    g4: LineSegment StartX=4 StartY=-27.5 StartZ=0 EndX=20 EndY=-45 EndZ=0
    g5: LineSegment StartX=20 StartY=-45 StartZ=0 EndX=36 EndY=-27.5 EndZ=0
    g6: LineSegment StartX=40 StartY=-31.5 StartZ=0 EndX=22.5 EndY=-50 EndZ=0
    g7: LineSegment StartX=0 StartY=-31.5 StartZ=0 EndX=17.5 EndY=-50 EndZ=0
    g8: LineSegment [constr] StartX=20 StartY=-45 StartZ=0 EndX=20 EndY=-50 EndZ=0
    g9: LineSegment [constr] StartX=17.5 StartY=-50 StartZ=0 EndX=22.5 EndY=-50 EndZ=0
    g10: LineSegment [constr] StartX=0 StartY=-50 StartZ=0 EndX=40 EndY=-50 EndZ=0
    g11: LineSegment StartX=4 StartY=-27.5 StartZ=0 EndX=36 EndY=-27.5 EndZ=0
    g12: LineSegment StartX=17.5 StartY=-50 StartZ=0 EndX=0 EndY=-68.5 EndZ=0
    g13: LineSegment StartX=4 StartY=-72.5 StartZ=0 EndX=20 EndY=-55 EndZ=0
    g14: LineSegment StartX=20 StartY=-55 StartZ=0 EndX=36 EndY=-72.5 EndZ=0
    g15: LineSegment StartX=40 StartY=-68.5 StartZ=0 EndX=22.5 EndY=-50 EndZ=0
    g16: LineSegment StartX=0 StartY=-31.5 StartZ=0 EndX=0 EndY=-68.5 EndZ=0
    g17: LineSegment StartX=4 StartY=-72.5 StartZ=0 EndX=36 EndY=-72.5 EndZ=0
    g18: LineSegment StartX=40 StartY=-31.5 StartZ=0 EndX=40 EndY=-68.5 EndZ=0
    g19: LineSegment [constr] StartX=20 StartY=-55 StartZ=0 EndX=20 EndY=-50 EndZ=0
  constraints (55):
    c: Coincident(g0,g1)
    c: Coincident(g1,g2)
    c: Coincident(g2,g3)
    c: Coincident(g3,g0)
    c: Horizontal(g0)
    c: Horizontal(g2)
    c: Vertical(g1)
    c: Vertical(g3)
    c: Distance(g1,g3) = 40
    c: Distance(g0,g2) = 45
    c: DistanceX(g-1,g0) = 0
    c: DistanceY(g0,g-1) = 27.5
    c: PointOnObject(g4,g0)
    c: Coincident(g5,g4)
    c: PointOnObject(g5,g0)
    c: PointOnObject(g6,g3)
    c: PointOnObject(g7,g1)
    c: DistanceX(g0,g4) = 4
    c: DistanceY(g7,g0) = 4
    c: DistanceX(g5,g0) = 4
    c: DistanceY(g6,g0) = 4
    c: DistanceX(g7,g6) = 5
    c: Coincident(g8,g4)
    c: Vertical(g8)
    c: Coincident(g9,g7)
    c: Coincident(g9,g6)
    c: Horizontal(g9)
    c: Symmetric(g6,g7,g8)
    c: DistanceY(g8,g8) = 5
    c: Symmetric(g1,g1,g10)
    c: Symmetric(g3,g3,g10)
    c: Symmetric(g10,g10,g8)
    c: Coincident(g11,g4)
    c: Coincident(g11,g5)
    c: Coincident(g12,g7)
    c: PointOnObject(g12,g1)
    c: PointOnObject(g13,g2)
    c: Coincident(g14,g13)
    c: PointOnObject(g14,g2)
    c: PointOnObject(g15,g3)
    c: Coincident(g15,g6)
    c: DistanceY(g13,g8) = 5
    c: DistanceY(g1,g12) = 4
    c: DistanceX(g1,g13) = 4
    c: DistanceX(g14,g2) = 4
    c: DistanceY(g2,g15) = 4
    c: Coincident(g16,g7)
    c: Coincident(g16,g12)
    c: Coincident(g17,g13)
    c: Coincident(g17,g14)
    c: Coincident(g18,g6)
    c: Coincident(g18,g15)
    c: Coincident(g19,g13)
    c: Coincident(g19,g8)
    c: Vertical(g19)
FEATURE [PartDesign::Pocket] Pocket007
  BaseFeature = -> Hole003
  Direction = (1e-16,-1,1e-15)
  Length = 5
  Length2 = 5
  Placement = pos=(0,0,0) rot=(1,1,1;2.0944rad)
  Profile = -> Sketch030
  ReferenceAxis = -> Sketch030 [N_Axis]
  Suppressed = false
  Type = 1
FEATURE [PartDesign::Fillet] Fillet001
  Base = -> Hole001 [Edge70,Edge30,Edge29,Edge28,Edge22,Edge23,Edge3,Edge21,Edge31,Edge1,Edge7,Edge25,Edge24,Edge27,Edge58,Edge51,Edge16,Edge14,Edge13,Edge12,Edge17,Edge18,Edge11,Edge19,Edge20,Edge2,Edge10,Edge55,Edge63,Edge76,Edge47,Edge67,Edge46,Edge68,Edge84,Edge83,Edge69,Edge45,Edge52,Edge60,+8 more]
  BaseFeature = -> Hole001
  Placement = pos=(0,0,0) rot=(1,1,1;2.0944rad)
  Radius = 1
  SupportTransform = false
  Suppressed = false
  UseAllEdges = false
FEATURE [PartDesign::Body] Body  label="ZMotorBracket"
  AllowCompound = false
  Group = -> [Sketch005,Pad,Sketch006,Pocket,Sketch007,Pocket001,Sketch008,Hole,Sketch009,Hole001,Fillet001]
  Origin = -> Origin001
  Placement = pos=(-191.1,159.9,10) rot=(0,0,1;0rad)
  Tip = -> Fillet001
FEATURE [Sketcher::SketchObject] Sketch032
  ArcFitTolerance = 1e-06
  FullyConstrained = true
  MakeInternals = false
  MapMode = 5
  Placement = pos=(0,-8,1.8e-15) rot=(1,0,0;1.5708rad)
  sketch-geometry (3):
    g0: Circle CenterX=-190 CenterY=200 CenterZ=0 NormalX=0 NormalY=0 NormalZ=1 AngleXU=0 Radius=2.5
    g1: Circle CenterX=-150 CenterY=200 CenterZ=0 NormalX=0 NormalY=0 NormalZ=1 AngleXU=0 Radius=2.5
    g2: LineSegment [constr] StartX=-190 StartY=200 StartZ=0 EndX=-150 EndY=200 EndZ=0
  constraints (8):
    c: Diameter(g0) = 5
    c: Diameter(g1) = 5
    c: Coincident(g2,g0)
    c: Coincident(g2,g1)
    c: Horizontal(g2)
    c: DistanceX(g1,g-1) = 150
    c: DistanceX(g2,g2) = 40
    c: DistanceY(g-1,g1) = 200
FEATURE [PartDesign::Hole] Hole005
  BaseFeature = -> Hole004
  CustomThreadClearance = 0
  Depth = 243.24
  DepthType = 1
  Diameter = 5.5
  DrillForDepth = false
  DrillPoint = 1
  DrillPointAngle = 118
  HoleCutCountersinkAngle = 90
  HoleCutCustomValues = false
  HoleCutDepth = 0
  HoleCutDiameter = 6.1
  HoleCutType = 0
  ModelThread = false
  Placement = pos=(0,0,0) rot=(1,0,0;1.5708rad)
  Profile = -> Sketch032
  Suppressed = false
  Tapered = false
  TaperedAngle = 90
  ThreadClass = 0
  ThreadDepth = 243.24
  ThreadDepthType = 0
  ThreadDirection = 0
  ThreadFit = 0
  ThreadSize = 13
  ThreadType = 1
  Threaded = false
  UseCustomThreadClearance = false
FEATURE [Part::FeaturePython] TSlot004  label="M5 x 20 series-TSlot016"  # WARN: FeaturePython — macro-defined, semantics opaque (R4)
  Diameter = 3
  Invert = false
  LeftHanded = false
  MatchOuter = false
  OffsetAngle = 0
  Placement = pos=(-190.01,120.3,200) rot=(-0.58,-0.58,0.58;4.18879rad)
  SlotWidth = 0
  Thread = false
  Type = 3
FEATURE [Part::FeaturePython] TSlot005  label="M5 x 20 series-TSlot017"  # WARN: FeaturePython — macro-defined, semantics opaque (R4)
  Diameter = 3
  Invert = false
  LeftHanded = false
  MatchOuter = false
  OffsetAngle = 0
  Placement = pos=(-150,120.3,200) rot=(-0.58,-0.58,0.58;4.18879rad)
  SlotWidth = 0
  Thread = false
  Type = 3
FEATURE [Sketcher::SketchObject] Sketch031
  ArcFitTolerance = 1e-06
  AttachmentSupport = -> [Pocket007]
  FullyConstrained = true
  MakeInternals = false
  MapMode = 5
  Placement = pos=(0,-1.8e-15,-8) rot=(0,0,-1;1.5708rad)
  sketch-geometry (7):
    g0: LineSegment [constr] StartX=0 StartY=-50 StartZ=0 EndX=-50 EndY=-50 EndZ=0
    g1: LineSegment StartX=-19 StartY=-12 StartZ=0 EndX=-44 EndY=-37 EndZ=0
    g2: LineSegment StartX=-44 StartY=-12 StartZ=0 EndX=-44 EndY=-37 EndZ=0
    g3: LineSegment StartX=-44 StartY=-12 StartZ=0 EndX=-19 EndY=-12 EndZ=0
    g4: LineSegment StartX=-19 StartY=-88 StartZ=0 EndX=-44 EndY=-63 EndZ=0
    g5: LineSegment StartX=-44 StartY=-88 StartZ=0 EndX=-44 EndY=-63 EndZ=0
    g6: LineSegment StartX=-44 StartY=-88 StartZ=0 EndX=-19 EndY=-88 EndZ=0
  constraints (19):
    c: Distance(g0) = 50
    c: PointOnObject(g0,g-2)
    c: Horizontal(g0)
    c: DistanceY(g0,g-1) = 50
    c: DistanceY(g1,g-1) = 12
    c: DistanceX(g1,g-1) = 19
    c: Coincident(g2,g1)
    c: Vertical(g2)
    c: Coincident(g3,g2)
    c: Coincident(g3,g1)
    c: Horizontal(g3)
    c: DistanceX(g3,g3) = 25
    c: DistanceY(g2,g2) = 25
    c: Symmetric(g1,g4,g0)
    c: Symmetric(g1,g4,g0)
    c: Symmetric(g2,g5,g0)
    c: Symmetric(g2,g5,g0)
    c: Symmetric(g3,g6,g0)
    c: Symmetric(g3,g6,g0)
FEATURE [PartDesign::Pocket] Pocket009
  BaseFeature = -> Pocket007
  Direction = (1.4e-15,0,-1)
  Length = 5
  Length2 = 5
  Placement = pos=(0,0,0) rot=(1,1,1;2.0944rad)
  Profile = -> Sketch031
  ReferenceAxis = -> Sketch031 [N_Axis]
  Suppressed = false
  Type = 1
FEATURE [PartDesign::Body] Body002  label="BackZFollower"
  AllowCompound = false
  Group = -> [Sketch013,Pad004,Sketch014,Pocket002,Sketch015,Pocket003,Sketch025,Hole003,Sketch030,Pocket007,Sketch031,Pocket009]
  Origin = -> Origin005
  Placement = pos=(-120,150,180) rot=(0,0,1;0rad)
  Tip = -> Pocket009
FEATURE [Sketcher::SketchObject] Sketch033
  ArcFitTolerance = 1e-06
  AttachmentSupport = -> [Hole005]
  FullyConstrained = true
  MakeInternals = false
  MapMode = 5
  Placement = pos=(0,5.02e-14,228) rot=(0,0,1;3.14159rad)
  sketch-geometry (5):
    g0: LineSegment StartX=147.5 StartY=-20 StartZ=0 EndX=192.5 EndY=-20 EndZ=0
    g1: LineSegment StartX=192.5 StartY=-20 StartZ=0 EndX=192.5 EndY=0 EndZ=0
    g2: LineSegment StartX=192.5 StartY=0 StartZ=0 EndX=147.5 EndY=0 EndZ=0
    g3: LineSegment StartX=147.5 StartY=0 StartZ=0 EndX=147.5 EndY=-20 EndZ=0
    g4: GeomPoint X=170 Y=0 Z=0
  constraints (13):
    c: Coincident(g0,g1)
    c: Coincident(g1,g2)
    c: Coincident(g2,g3)
    c: Coincident(g3,g0)
    c: Horizontal(g0)
    c: Horizontal(g2)
    c: Vertical(g1)
    c: Vertical(g3)
    c: Distance(g1,g3) = 45
    c: Distance(g0,g2) = 20
    c: PointOnObject(g2,g-1)
    c: Symmetric(g2,g1,g4)
    c: DistanceX(g-1,g4) = 170
FEATURE [PartDesign::Pocket] Pocket010
  BaseFeature = -> Hole005
  Direction = (0,0,-1)
  Length = 5
  Length2 = 5
  Placement = pos=(0,0,0) rot=(1,0,0;1.5708rad)
  Profile = -> Sketch033
  ReferenceAxis = -> Sketch033 [N_Axis]
  Suppressed = false
  Type = 1
FEATURE [Sketcher::SketchObject] Sketch034
  ArcFitTolerance = 1e-06
  AttachmentSupport = -> [Pocket010]
  FullyConstrained = true
  MakeInternals = false
  MapMode = 5
  Placement = pos=(0,-4,9e-16) rot=(1,0,0;1.5708rad)
  sketch-geometry (16):
    g0: LineSegment StartX=-210 StartY=210 StartZ=0 EndX=-200 EndY=200 EndZ=0
    g1: LineSegment StartX=-200 StartY=200 StartZ=0 EndX=-210 EndY=190 EndZ=0
    g2: LineSegment [constr] StartX=-170 StartY=225 StartZ=0 EndX=-170 EndY=175 EndZ=0
    g3: LineSegment StartX=-210 StartY=190 StartZ=0 EndX=-210 EndY=210 EndZ=0
    g4: LineSegment [constr] StartX=-200 StartY=200 StartZ=0 EndX=-210 EndY=200 EndZ=0
    g5: LineSegment StartX=-130 StartY=210 StartZ=0 EndX=-140 EndY=200 EndZ=0
    g6: LineSegment StartX=-140 StartY=200 StartZ=0 EndX=-130 EndY=190 EndZ=0
    g7: LineSegment StartX=-130 StartY=190 StartZ=0 EndX=-130 EndY=210 EndZ=0
    g8: LineSegment [constr] StartX=-140 StartY=200 StartZ=0 EndX=-130 EndY=200 EndZ=0
    g9: LineSegment StartX=-192.5 StartY=218 StartZ=0 EndX=-147.5 EndY=218 EndZ=0
    g10: LineSegment StartX=-147.5 StartY=218 StartZ=0 EndX=-170 EndY=206 EndZ=0
    g11: LineSegment StartX=-170 StartY=206 StartZ=0 EndX=-192.5 EndY=218 EndZ=0
    g12: LineSegment [constr] StartX=-195 StartY=200 StartZ=0 EndX=-145 EndY=200 EndZ=0
    g13: LineSegment StartX=-192.5 StartY=182 StartZ=0 EndX=-147.5 EndY=182 EndZ=0
    g14: LineSegment StartX=-147.5 StartY=182 StartZ=0 EndX=-170 EndY=194 EndZ=0
    g15: LineSegment StartX=-170 StartY=194 StartZ=0 EndX=-192.5 EndY=182 EndZ=0
  constraints (40):
    c: Coincident(g1,g0)
    c: Vertical(g2)
    c: DistanceX(g2,g-1) = 170
    c: DistanceY(g2,g2) = 50
    c: DistanceX(g0,g0) = 10
    c: Coincident(g3,g1)
    c: Coincident(g3,g0)
    c: Vertical(g3)
    c: DistanceY(g3,g3) = 20
    c: Coincident(g4,g0)
    c: Symmetric(g3,g3,g4)
    c: Horizontal(g4)
    c: DistanceX(g0,g-1) = 210
    c: DistanceY(g-1,g4) = 200
    c: DistanceY(g-1,g2) = 225
    c: Symmetric(g0,g5,g2)
    c: Symmetric(g0,g5,g2)
    c: Symmetric(g1,g6,g2)
    c: Symmetric(g1,g6,g2)
    c: Symmetric(g3,g7,g2)
    c: Symmetric(g3,g7,g2)
    c: Symmetric(g4,g8,g2)
    c: Symmetric(g4,g8,g2)
    c: Coincident(g10,g9)
    c: PointOnObject(g10,g2)
    c: Coincident(g11,g10)
    c: Coincident(g11,g9)
    c: DistanceX(g9,g9) = 45
    c: DistanceY(g10,g9) = 12
    c: Symmetric(g9,g9,g2)
    c: DistanceY(g-1,g9) = 218
    c: DistanceX(g12,g12) = 50
    c: DistanceY(g-1,g12) = 200
    c: Symmetric(g12,g12,g2)
    c: Symmetric(g9,g13,g12)
    c: Symmetric(g9,g13,g12)
    c: Symmetric(g10,g14,g12)
    c: Symmetric(g10,g14,g12)
    c: Symmetric(g11,g15,g12)
    c: Symmetric(g11,g15,g12)
FEATURE [PartDesign::Pocket] Pocket011
  BaseFeature = -> Pocket010
  Direction = (0,1,-2e-16)
  Length = 5
  Length2 = 5
  Placement = pos=(0,0,0) rot=(1,0,0;1.5708rad)
  Profile = -> Sketch034
  ReferenceAxis = -> Sketch034 [N_Axis]
  Suppressed = false
  Type = 1
FEATURE [PartDesign::Body] Body004  label="FrontZFollower"
  AllowCompound = false
  Group = -> [Sketch023,Pad006,Sketch024,Pad007,Sketch028,Hole004,Sketch032,Hole005,Sketch033,Pocket010,Sketch034,Pocket011]
  Origin = -> Origin023
  Placement = pos=(0,119,0) rot=(0,0,1;0rad)
  Tip = -> Pocket011
FEATURE [Sketcher::SketchObject] Sketch037  label="d"
  ArcFitTolerance = 0
  AttachmentSupport = -> [XY_Plane024]
  FullyConstrained = true
  MakeInternals = false
  MapMode = 5
  sketch-geometry (12):
    g0: ArcOfCircle CenterX=-190 CenterY=0 CenterZ=0 NormalX=0 NormalY=0 NormalZ=1 AngleXU=0 Radius=7.5 StartAngle=1.5708 EndAngle=4.71239
    g1: ArcOfCircle CenterX=250 CenterY=0 CenterZ=0 NormalX=0 NormalY=0 NormalZ=1 AngleXU=0 Radius=7.5 StartAngle=4.71239 EndAngle=7.85398
    g2: LineSegment StartX=-190 StartY=-7.5 StartZ=0 EndX=250 EndY=-7.5 EndZ=0
    g3: LineSegment StartX=-190 StartY=7.5 StartZ=0 EndX=250 EndY=7.5 EndZ=0
    g4: LineSegment StartX=-1 StartY=-0.254 StartZ=0 EndX=-0.734887 EndY=-0.254 EndZ=0
    g5: ArcOfCircle CenterX=-0.734887 CenterY=-0.404 CenterZ=0 NormalX=0 NormalY=0 NormalZ=1 AngleXU=0 Radius=0.15 StartAngle=0.162302 EndAngle=1.5708
    g6: ArcOfCircle CenterX=0.4 CenterY=-0.218171 CenterZ=0 NormalX=0 NormalY=0 NormalZ=1 AngleXU=0 Radius=1 StartAngle=3.30389 EndAngle=3.68787
    g7: ArcOfCircle CenterX=0.0197626 CenterY=-0.449352 CenterZ=0 NormalX=0 NormalY=0 NormalZ=1 AngleXU=0 Radius=0.555 StartAngle=3.68787 EndAngle=4.67677
    g8: LineSegment StartX=-1 StartY=0.376 StartZ=0 EndX=3.331e-13 EndY=0.376 EndZ=0
    g9: LineSegment StartX=3.331e-13 StartY=0.376 StartZ=0 EndX=3.331e-13 EndY=-1.004 EndZ=0
    g10: LineSegment StartX=-1 StartY=0.376 StartZ=0 EndX=-1 EndY=-0.254 EndZ=0
    g11: LineSegment StartX=0 StartY=1.577e-12 StartZ=0 EndX=5.851e-13 EndY=1.577e-12 EndZ=0
  constraints (36):
    c: Tangent(g0,g3) = 1.5708
    c: Tangent(g0,g2) = -1.5708
    c: Tangent(g2,g1) = -1.5708
    c: Tangent(g3,g1) = 1.5708
    c: Horizontal(g4)
    c: Tangent(g4,g5) = 1.5708
    c: Tangent(g6,g5) = 1.5708
    c: Radius(g5) = 0.15
    c: Radius(g6) = 1
    c: Tangent(g7,g6) = -1.5708
    c: Radius(g7) = 0.555
    c: DistanceX(g7,g6) = 0.4
    c: DistanceX(g4,g7) = 1
    c: DistanceY(g7,g4) = 0.75
    c: Angle(g6) = 0.383972
    c: Horizontal(g8)
    c: Coincident(g9,g8)
    c: Coincident(g9,g7)
    c: Vertical(g9)
    c: Coincident(g10,g4)
    c: DistanceY(g7,g8) = 1.38
    c: Horizontal(g11)
    c: PointOnObject(g11,g9)
    c: DistanceY(g4,g11) = 0.254
    c: Radius(g1) = 7.5  'r1'
    c: Radius(g0) = 7.5  'r2'
    c: PointOnObject(g1,g-1)
    c: Distance(g3) = 440  'd1'
    c: Distance(g2) = 440  'd2'
    c: Coincident(g10,g8)
    c: Coincident(g11,g-1)
    c: PointOnObject(g7,g-2)
    c: Vertical(g10)
    c: DistanceX(g-1,g1) = 250
    c: DistanceX(g0,g-1) = 190
    c: PointOnObject(g0,g-1)
FEATURE [PartDesign::ShapeBinder] ShapeBinder
  Support = -> [Sketch037]
  TraceSupport = false
FEATURE [PartDesign::CoordinateSystem] LCS_Part_1
  AttacherType = Attacher::AttachEngine3D
  AttachmentSupport = -> [ShapeBinder]
  MapMode = 11
  Placement = pos=(-190,0,0) rot=(0,0,1;3.14159rad)
FEATURE [PartDesign::CoordinateSystem] LCS_Part_2
  AttacherType = Attacher::AttachEngine3D
  AttachmentSupport = -> [ShapeBinder]
  MapMode = 11
  Placement = pos=(250,0,0) rot=(0,0,1;0rad)
FEATURE [Sketcher::SketchObject] Sketch038
  ArcFitTolerance = 0
  AttachmentSupport = -> [XY_Plane024]
  ExternalGeometry = -> [ShapeBinder]
  FullyConstrained = true
  MakeInternals = false
  MapMode = 5
  sketch-geometry (7):
    g0: ArcOfCircle CenterX=0.0197626 CenterY=-0.449352 CenterZ=0 NormalX=0 NormalY=0 NormalZ=1 AngleXU=0 Radius=0.555 StartAngle=3.68787 EndAngle=4.67677
    g1: ArcOfCircle CenterX=0.4 CenterY=-0.218171 CenterZ=0 NormalX=0 NormalY=0 NormalZ=1 AngleXU=0 Radius=1 StartAngle=3.30389 EndAngle=3.68787
    g2: ArcOfCircle CenterX=-0.734887 CenterY=-0.404 CenterZ=0 NormalX=0 NormalY=0 NormalZ=1 AngleXU=0 Radius=0.15 StartAngle=0.162302 EndAngle=1.5708
    g3: LineSegment StartX=-0.734887 StartY=-0.254 StartZ=0 EndX=-1 EndY=-0.254 EndZ=0
    g4: LineSegment StartX=-1 StartY=-0.254 StartZ=0 EndX=-1 EndY=0.376 EndZ=0
    g5: LineSegment StartX=-1 StartY=0.376 StartZ=0 EndX=1.1954e-12 EndY=0.376 EndZ=0
    g6: LineSegment StartX=1.1954e-12 StartY=0.376 StartZ=0 EndX=8.933e-13 EndY=-1.004 EndZ=0
  constraints (17):
    c: Coincident(g0,g-4)
    c: Horizontal(g0,g-5)
    c: Coincident(g0,g1)
    c: Horizontal(g1,g-6)
    c: Coincident(g1,g-5)
    c: Coincident(g0,g-4)
    c: Coincident(g2,g-6)
    c: Coincident(g2,g1)
    c: Vertical(g-7,g2)
    c: Coincident(g3,g2)
    c: Coincident(g3,g-10)
    c: Coincident(g4,g3)
    c: Coincident(g5,g-9)
    c: Coincident(g6,g5)
    c: Coincident(g6,g0)
    c: Coincident(g5,g-10)
    c: Coincident(g4,g5)
FEATURE [PartDesign::Pad] Pad008
  Direction = (0,0,1)
  Length = 6
  Length2 = 100
  Profile = -> Sketch038
  Refine = true
  Suppressed = false
  Type = 0
FEATURE [PartDesign::Mirrored] Mirrored
  BaseFeature = -> Pad008
  MirrorPlane = -> Pad008 [Face2]
  Originals = -> [Pad008]
  Refine = true
  Suppressed = false
  TransformMode = 0
FEATURE [PartDesign::Body] Body005
  AllowCompound = false
  Group = -> [Sketch037,ShapeBinder,Sketch038,Pad008,Mirrored]
  Origin = -> Origin024
  Tip = -> Mirrored
FEATURE [Part::FeaturePython] PathArray  # WARN: FeaturePython — macro-defined, semantics opaque (R4)
  Align = true
  AlignMode = 0
  Base = -> Mirrored
  Count = 465
  EndOffset = 0
  ExtraTranslation = (0,0,0)
  ForceVertical = true
  Fuse = false
  PathObject = -> ShapeBinder
  StartOffset = 0
  TangentVector = (1,0,0)
  VerticalVector = (0,0,-1)
  expr: Count = (Sketch037.Constraints.d1 + Sketch037.Constraints.d2 + pi * Sketch037.Constraints.r1 + pi * Sketch037.Constraints.r2) / 2 + 1 mm
FEATURE [App::Part] Part006  label="XBelt"
  Group = -> [PathArray,Body005,LCS_Part_1,LCS_Part_2]
  Origin = -> Origin025
  Placement = pos=(-30,134.7,200) rot=(0,-0.71,0.71;3.14159rad)
FEATURE [App::Part] Part005  label="XMotorAssembly"
  Group = -> [_7HS4401S_Stepper_Motor001,GT2_20_Tooth_Assy__ID_6mm_,Part006]
  Origin = -> Origin012
  Placement = pos=(0,-8.65,0) rot=(0,0,1;0rad)
FEATURE [Sketcher::SketchObject] Sketch039
  ArcFitTolerance = 1e-06
  AttachmentSupport = -> [XZ_Plane026]
  FullyConstrained = true
  MakeInternals = false
  MapMode = 5
  Placement = pos=(0,0,0) rot=(1,0,0;1.5708rad)
  sketch-geometry (4):
    g0: LineSegment StartX=-301 StartY=229 StartZ=0 EndX=-301 EndY=179 EndZ=0
    g1: LineSegment StartX=-301 StartY=179 StartZ=0 EndX=-250 EndY=179 EndZ=0
    g2: LineSegment StartX=-250 StartY=179 StartZ=0 EndX=-250 EndY=229 EndZ=0
    g3: LineSegment StartX=-250 StartY=229 StartZ=0 EndX=-301 EndY=229 EndZ=0
  constraints (12):
    c: Coincident(g0,g1)
    c: Coincident(g1,g2)
    c: Coincident(g2,g3)
    c: Coincident(g3,g0)
    c: Vertical(g0)
    c: Vertical(g2)
    c: Horizontal(g1)
    c: Horizontal(g3)
    c: DistanceX(g3,g3) = 51
    c: DistanceY(g0,g0) = 50
    c: DistanceX(g1,g-1) = 250
    c: DistanceY(g-1,g1) = 179
FEATURE [PartDesign::Pad] Pad009
  Direction = (0,-1,2e-16)
  Length = 5.45
  Length2 = 10
  Placement = pos=(0,0,0) rot=(1,0,0;1.5708rad)
  Profile = -> Sketch039
  ReferenceAxis = -> Sketch039 [N_Axis]
  Suppressed = false
  Type = 0
FEATURE [Sketcher::SketchObject] Sketch040
  ArcFitTolerance = 1e-06
  AttachmentSupport = -> [Pad009]
  FullyConstrained = true
  MakeInternals = false
  MapMode = 5
  Placement = pos=(0,-5.45,1.2e-15) rot=(1,0,0;1.5708rad)
  sketch-geometry (8):
    g0: Circle CenterX=-295.5 CenterY=215.5 CenterZ=0 NormalX=0 NormalY=0 NormalZ=1 AngleXU=0 Radius=2
    g1: Circle CenterX=-264.5 CenterY=215.5 CenterZ=0 NormalX=0 NormalY=0 NormalZ=1 AngleXU=0 Radius=2
    g2: Circle CenterX=-295.5 CenterY=184.5 CenterZ=0 NormalX=0 NormalY=0 NormalZ=1 AngleXU=0 Radius=2
    g3: Circle CenterX=-264.5 CenterY=184.5 CenterZ=0 NormalX=0 NormalY=0 NormalZ=1 AngleXU=0 Radius=2
    g4: LineSegment [constr] StartX=-295.5 StartY=215.5 StartZ=0 EndX=-295.5 EndY=184.5 EndZ=0
    g5: LineSegment [constr] StartX=-295.5 StartY=184.5 StartZ=0 EndX=-264.5 EndY=184.5 EndZ=0
    g6: LineSegment [constr] StartX=-264.5 StartY=184.5 StartZ=0 EndX=-264.5 EndY=215.5 EndZ=0
    g7: LineSegment [constr] StartX=-264.5 StartY=215.5 StartZ=0 EndX=-295.5 EndY=215.5 EndZ=0
  constraints (20):
    c: Diameter(g0) = 4
    c: Equal(g0,g1)
    c: Equal(g1,g2)
    c: Equal(g2,g3)
    c: Coincident(g4,g5)
    c: Coincident(g5,g6)
    c: Coincident(g6,g7)
    c: Coincident(g7,g4)
    c: Vertical(g4)
    c: Vertical(g6)
    c: Horizontal(g5)
    c: Horizontal(g7)
    c: Coincident(g4,g0)
    c: Coincident(g5,g3)
    c: Coincident(g2,g4)
    c: Coincident(g6,g1)
    c: DistanceX(g7,g7) = 31
    c: DistanceY(g4,g4) = 31
    c: DistanceX(g3,g-1) = 264.5
    c: DistanceY(g-1,g3) = 184.5
FEATURE [PartDesign::Hole] Hole006
  BaseFeature = -> Pad009
  CustomThreadClearance = 0
  Depth = 121.065
  DepthType = 1
  Diameter = 3.4
  DrillForDepth = false
  DrillPoint = 1
  DrillPointAngle = 118
  HoleCutCountersinkAngle = 90
  HoleCutCustomValues = false
  HoleCutDepth = 0
  HoleCutDiameter = 6.1
  HoleCutType = 0
  ModelThread = false
  Placement = pos=(0,0,0) rot=(1,0,0;1.5708rad)
  Profile = -> Sketch040
  Suppressed = false
  Tapered = false
  TaperedAngle = 90
  ThreadClass = 0
  ThreadDepth = 121.065
  ThreadDepthType = 0
  ThreadDirection = 0
  ThreadFit = 0
  ThreadSize = 9
  ThreadType = 1
  Threaded = false
  UseCustomThreadClearance = false
FEATURE [Sketcher::SketchObject] Sketch041
  ArcFitTolerance = 1e-06
  AttachmentSupport = -> [Hole006]
  FullyConstrained = true
  MakeInternals = false
  MapMode = 5
  Placement = pos=(0,-5.45,1.2e-15) rot=(1,0,0;1.5708rad)
  sketch-geometry (1):
    g0: Circle CenterX=-280 CenterY=200 CenterZ=0 NormalX=0 NormalY=0 NormalZ=1 AngleXU=0 Radius=11.5
  constraints (3):
    c: Diameter(g0) = 23
    c: DistanceX(g0,g-1) = 280
    c: DistanceY(g-1,g0) = 200
FEATURE [PartDesign::Pocket] Pocket013
  BaseFeature = -> Hole006
  Direction = (0,1,-2e-16)
  Length = 5
  Length2 = 5
  Placement = pos=(0,0,0) rot=(1,0,0;1.5708rad)
  Profile = -> Sketch041
  ReferenceAxis = -> Sketch041 [N_Axis]
  Suppressed = false
  Type = 1
FEATURE [Sketcher::SketchObject] Sketch042
  ArcFitTolerance = 1e-06
  AttachmentSupport = -> [Pocket013]
  FullyConstrained = true
  MakeInternals = false
  MapMode = 5
  Placement = pos=(0,-5.45,1.2e-15) rot=(1,0,0;1.5708rad)
  sketch-geometry (4):
    g0: LineSegment StartX=-250 StartY=229 StartZ=0 EndX=-260 EndY=229 EndZ=0
    g1: LineSegment StartX=-260 StartY=229 StartZ=0 EndX=-260 EndY=171 EndZ=0
    g2: LineSegment StartX=-260 StartY=171 StartZ=0 EndX=-250 EndY=171 EndZ=0
    g3: LineSegment StartX=-250 StartY=171 StartZ=0 EndX=-250 EndY=229 EndZ=0
  constraints (12):
    c: Coincident(g0,g1)
    c: Coincident(g1,g2)
    c: Coincident(g2,g3)
    c: Coincident(g3,g0)
    c: Horizontal(g0)
    c: Horizontal(g2)
    c: Vertical(g1)
    c: Vertical(g3)
    c: Distance(g1,g3) = 10
    c: Distance(g0,g2) = 58
    c: DistanceX(g2,g-1) = 250
    c: DistanceY(g-1,g2) = 171
FEATURE [PartDesign::Pad] Pad010
  BaseFeature = -> Pocket013
  Direction = (0,-1,2e-16)
  Length = 18.5
  Length2 = 10
  Placement = pos=(0,0,0) rot=(1,0,0;1.5708rad)
  Profile = -> Sketch042
  ReferenceAxis = -> Sketch042 [N_Axis]
  Suppressed = false
  Type = 0
FEATURE [Sketcher::SketchObject] Sketch043
  ArcFitTolerance = 1e-06
  AttachmentSupport = -> [Pad010]
  FullyConstrained = true
  MakeInternals = false
  MapMode = 5
  Placement = pos=(-250,0,0) rot=(0.707107,0,0.707107;3.14159rad)
  sketch-geometry (4):
    g0: LineSegment StartX=171 StartY=24 StartZ=0 EndX=171 EndY=20 EndZ=0
    g1: LineSegment StartX=171 StartY=20 StartZ=0 EndX=229 EndY=20 EndZ=0
    g2: LineSegment StartX=229 StartY=20 StartZ=0 EndX=229 EndY=24 EndZ=0
    g3: LineSegment StartX=229 StartY=24 StartZ=0 EndX=171 EndY=24 EndZ=0
  constraints (12):
    c: Coincident(g0,g1)
    c: Coincident(g1,g2)
    c: Coincident(g2,g3)
    c: Coincident(g3,g0)
    c: Vertical(g0)
    c: Vertical(g2)
    c: Horizontal(g1)
    c: Horizontal(g3)
    c: Distance(g0,g2) = 58
    c: Distance(g1,g3) = 4
    c: DistanceX(g-1,g0) = 171
    c: DistanceY(g-1,g0) = 20
FEATURE [PartDesign::Pad] Pad011
  BaseFeature = -> Pad010
  Direction = (1,0,-2e-16)
  Length = 35
  Length2 = 10
  Placement = pos=(0,0,0) rot=(1,0,0;1.5708rad)
  Profile = -> Sketch043
  ReferenceAxis = -> Sketch043 [N_Axis]
  Suppressed = false
  Type = 0
FEATURE [Sketcher::SketchObject] Sketch044
  ArcFitTolerance = 1e-06
  AttachmentSupport = -> [Pad011]
  FullyConstrained = true
  MakeInternals = false
  MapMode = 5
  Placement = pos=(0,7.88e-14,179) rot=(1,0,0;3.14159rad)
  sketch-geometry (4):
    g0: LineSegment StartX=-301 StartY=5.5 StartZ=0 EndX=-301 EndY=-32.5 EndZ=0
    g1: LineSegment StartX=-301 StartY=-32.5 StartZ=0 EndX=-250 EndY=-32.5 EndZ=0
    g2: LineSegment StartX=-250 StartY=-32.5 StartZ=0 EndX=-250 EndY=5.5 EndZ=0
    g3: LineSegment StartX=-250 StartY=5.5 StartZ=0 EndX=-301 EndY=5.5 EndZ=0
  constraints (12):
    c: Coincident(g0,g1)
    c: Coincident(g1,g2)
    c: Coincident(g2,g3)
    c: Coincident(g3,g0)
    c: Vertical(g0)
    c: Vertical(g2)
    c: Horizontal(g1)
    c: Horizontal(g3)
    c: Distance(g0,g2) = 51
    c: Distance(g1,g3) = 38
    c: DistanceX(g1,g-1) = 250
    c: DistanceY(g1,g-1) = 32.5
FEATURE [PartDesign::Pad] Pad012
  BaseFeature = -> Pad011
  Direction = (0,0,-1)
  Length = 8
  Length2 = 10
  Placement = pos=(0,0,0) rot=(1,0,0;1.5708rad)
  Profile = -> Sketch044
  ReferenceAxis = -> Sketch044 [N_Axis]
  Suppressed = false
  Type = 0
FEATURE [Sketcher::SketchObject] Sketch045
  ArcFitTolerance = 1e-06
  AttachmentSupport = -> [Pad012]
  FullyConstrained = true
  MakeInternals = false
  MapMode = 5
  Placement = pos=(0,4e-16,0) rot=(-1,0,0;1.5708rad)
  sketch-geometry (4):
    g0: LineSegment StartX=-250 StartY=-179 StartZ=0 EndX=-258 EndY=-179 EndZ=0
    g1: LineSegment StartX=-258 StartY=-179 StartZ=0 EndX=-258 EndY=-229 EndZ=0
    g2: LineSegment StartX=-258 StartY=-229 StartZ=0 EndX=-250 EndY=-229 EndZ=0
    g3: LineSegment StartX=-250 StartY=-229 StartZ=0 EndX=-250 EndY=-179 EndZ=0
  constraints (12):
    c: Coincident(g0,g1)
    c: Coincident(g1,g2)
    c: Coincident(g2,g3)
    c: Coincident(g3,g0)
    c: Horizontal(g0)
    c: Horizontal(g2)
    c: Vertical(g1)
    c: Vertical(g3)
    c: DistanceX(g0,g0) = 8
    c: DistanceY(g3,g3) = 50
    c: DistanceX(g2,g-1) = 250
    c: DistanceY(g2,g-1) = 229
FEATURE [PartDesign::Pad] Pad013
  BaseFeature = -> Pad012
  Direction = (0,1,2e-16)
  Length = 20
  Length2 = 10
  Placement = pos=(0,0,0) rot=(1,0,0;1.5708rad)
  Profile = -> Sketch045
  ReferenceAxis = -> Sketch045 [N_Axis]
  Suppressed = false
  Type = 0
FEATURE [Sketcher::SketchObject] Sketch046
  ArcFitTolerance = 1e-06
  AttachmentSupport = -> [Pad013]
  FullyConstrained = true
  MakeInternals = false
  MapMode = 5
  Placement = pos=(-250,0,0) rot=(0.707107,0,0.707107;3.14159rad)
  sketch-geometry (4):
    g0: LineSegment StartX=171 StartY=20 StartZ=0 EndX=171 EndY=-4 EndZ=0
    g1: LineSegment StartX=171 StartY=-4 StartZ=0 EndX=229 EndY=-4 EndZ=0
    g2: LineSegment StartX=229 StartY=-4 StartZ=0 EndX=229 EndY=20 EndZ=0
    g3: LineSegment StartX=229 StartY=20 StartZ=0 EndX=171 EndY=20 EndZ=0
  constraints (12):
    c: Coincident(g0,g1)
    c: Coincident(g1,g2)
    c: Coincident(g2,g3)
    c: Coincident(g3,g0)
    c: Vertical(g0)
    c: Vertical(g2)
    c: Horizontal(g1)
    c: Horizontal(g3)
    c: Distance(g0,g2) = 58
    c: Distance(g1,g3) = 24
    c: DistanceX(g-1,g0) = 171
    c: DistanceY(g-1,g0) = 20
FEATURE [PartDesign::Pad] Pad014
  BaseFeature = -> Pad013
  Direction = (1,0,-2e-16)
  Length = 35
  Length2 = 10
  Placement = pos=(0,0,0) rot=(1,0,0;1.5708rad)
  Profile = -> Sketch046
  ReferenceAxis = -> Sketch046 [N_Axis]
  Suppressed = false
  Type = 0
FEATURE [Sketcher::SketchObject] Sketch047
  ArcFitTolerance = 1e-06
  AttachmentSupport = -> [Pad014]
  FullyConstrained = true
  MakeInternals = false
  MapMode = 5
  Placement = pos=(0,-24,5.3e-15) rot=(1,0,0;1.5708rad)
  sketch-geometry (1):
    g0: Circle CenterX=-235 CenterY=200 CenterZ=0 NormalX=0 NormalY=0 NormalZ=1 AngleXU=0 Radius=2.5
  constraints (3):
    c: Diameter(g0) = 5
    c: DistanceX(g0,g-1) = 235
    c: DistanceY(g-1,g0) = 200
FEATURE [PartDesign::Hole] Hole007
  BaseFeature = -> Pad014
  CustomThreadClearance = 0
  Depth = 247.813
  DepthType = 1
  Diameter = 5.5
  DrillForDepth = false
  DrillPoint = 1
  DrillPointAngle = 118
  HoleCutCountersinkAngle = 90
  HoleCutCustomValues = false
  HoleCutDepth = 0
  HoleCutDiameter = 6.1
  HoleCutType = 0
  ModelThread = false
  Placement = pos=(0,0,0) rot=(1,0,0;1.5708rad)
  Profile = -> Sketch047
  Suppressed = false
  Tapered = false
  TaperedAngle = 90
  ThreadClass = 0
  ThreadDepth = 247.813
  ThreadDepthType = 0
  ThreadDirection = 0
  ThreadFit = 0
  ThreadSize = 13
  ThreadType = 1
  Threaded = false
  UseCustomThreadClearance = false
FEATURE [Sketcher::SketchObject] Sketch048
  ArcFitTolerance = 1e-06
  AttachmentSupport = -> [Hole007]
  FullyConstrained = true
  MakeInternals = false
  MapMode = 5
  Placement = pos=(0,-24,5.3e-15) rot=(1,0,0;1.5708rad)
  sketch-geometry (6):
    g0: LineSegment StartX=-235 StartY=219 StartZ=0 EndX=-214 EndY=200 EndZ=0
    g1: LineSegment StartX=-214 StartY=200 StartZ=0 EndX=-235 EndY=181 EndZ=0
    g2: LineSegment StartX=-235 StartY=181 StartZ=0 EndX=-235 EndY=171 EndZ=0
    g3: LineSegment StartX=-235 StartY=171 StartZ=0 EndX=-215 EndY=171 EndZ=0
    g4: LineSegment StartX=-215 StartY=171 StartZ=0 EndX=-215 EndY=219 EndZ=0
    g5: LineSegment StartX=-215 StartY=219 StartZ=0 EndX=-235 EndY=219 EndZ=0
  constraints (18):
    c: Coincident(g1,g0)
    c: Coincident(g2,g1)
    c: Vertical(g2)
    c: Coincident(g3,g2)
    c: Horizontal(g3)
    c: Coincident(g4,g3)
    c: Vertical(g4)
    c: Coincident(g5,g4)
    c: Horizontal(g5)
    c: DistanceY(g0,g0) = 19
    c: Equal(g1,g0)
    c: DistanceY(g1,g1) = 19
    c: DistanceX(g5,g5) = 20
    c: DistanceX(g3,g-1) = 215
    c: DistanceY(g-1,g3) = 171
    c: DistanceX(g0,g0) = 21
    c: Coincident(g0,g5)
    c: DistanceY(g2,g2) = 10
FEATURE [PartDesign::Pocket] Pocket014
  BaseFeature = -> Hole007
  Direction = (0,1,-2e-16)
  Length = 5
  Length2 = 5
  Placement = pos=(0,0,0) rot=(1,0,0;1.5708rad)
  Profile = -> Sketch048
  ReferenceAxis = -> Sketch048 [N_Axis]
  Suppressed = false
  Type = 1
FEATURE [Sketcher::SketchObject] Sketch049
  ArcFitTolerance = 1e-06
  AttachmentSupport = -> [Pocket014]
  FullyConstrained = true
  MakeInternals = false
  MapMode = 5
  Placement = pos=(0,-5.45,1.2e-15) rot=(1,0,0;1.5708rad)
  sketch-geometry (4):
    g0: LineSegment StartX=-301 StartY=229 StartZ=0 EndX=-301 EndY=219 EndZ=0
    g1: LineSegment StartX=-301 StartY=219 StartZ=0 EndX=-231 EndY=219 EndZ=0
    g2: LineSegment StartX=-231 StartY=219 StartZ=0 EndX=-231 EndY=229 EndZ=0
    g3: LineSegment StartX=-231 StartY=229 StartZ=0 EndX=-301 EndY=229 EndZ=0
  constraints (12):
    c: Coincident(g0,g1)
    c: Coincident(g1,g2)
    c: Coincident(g2,g3)
    c: Coincident(g3,g0)
    c: Vertical(g0)
    c: Vertical(g2)
    c: Horizontal(g1)
    c: Horizontal(g3)
    c: Distance(g0,g2) = 70
    c: Distance(g1,g3) = 10
    c: DistanceY(g-1,g0) = 229
    c: DistanceX(g0,g-1) = 301
FEATURE [PartDesign::Pocket] Pocket015
  BaseFeature = -> Pocket014
  Direction = (0,1,-2e-16)
  Length = 30
  Length2 = 30
  Placement = pos=(0,0,0) rot=(1,0,0;1.5708rad)
  Profile = -> Sketch049
  ReferenceAxis = -> Sketch049 [N_Axis]
  Suppressed = false
  Type = 4
FEATURE [Sketcher::SketchObject] Sketch052
  ArcFitTolerance = 1e-06
  FullyConstrained = true
  MakeInternals = false
  MapMode = 5
  Placement = pos=(-260,0,0) rot=(0.707107,0,-0.707107;3.14159rad)
  sketch-geometry (5):
    g0: LineSegment [constr] StartX=-211 StartY=21 StartZ=0 EndX=-211 EndY=-1 EndZ=0
    g1: LineSegment [constr] StartX=-211 StartY=-1 StartZ=0 EndX=-189 EndY=-1 EndZ=0
    g2: LineSegment [constr] StartX=-189 StartY=-1 StartZ=0 EndX=-189 EndY=21 EndZ=0
    g3: LineSegment [constr] StartX=-189 StartY=21 StartZ=0 EndX=-211 EndY=21 EndZ=0
    g4: Circle CenterX=-200 CenterY=10 CenterZ=0 NormalX=0 NormalY=0 NormalZ=1 AngleXU=0 Radius=3
  constraints (13):
    c: Coincident(g0,g1)
    c: Coincident(g1,g2)
    c: Coincident(g2,g3)
    c: Coincident(g3,g0)
    c: Vertical(g0)
    c: Horizontal(g1)
    c: Distance(g0,g2) = 22
    c: Distance(g1,g3) = 22
    c: DistanceX(g2,g-1) = 189
    c: DistanceY(g-1,g2) = 21
    c: Diameter(g4) = 6
    c: Symmetric(g0,g1,g4)
    c: Symmetric(g2,g0,g4)
FEATURE [PartDesign::Hole] Hole008
  BaseFeature = -> Pocket015
  CustomThreadClearance = 0
  Depth = 25
  DepthType = 0
  Diameter = 6.6
  DrillForDepth = false
  DrillPoint = 1
  DrillPointAngle = 118
  HoleCutCountersinkAngle = 90
  HoleCutCustomValues = false
  HoleCutDepth = 0
  HoleCutDiameter = 6.1
  HoleCutType = 0
  ModelThread = false
  Placement = pos=(0,0,0) rot=(1,0,0;1.5708rad)
  Profile = -> Sketch052
  Suppressed = false
  Tapered = false
  TaperedAngle = 90
  ThreadClass = 0
  ThreadDepth = 25
  ThreadDepthType = 0
  ThreadDirection = 0
  ThreadFit = 0
  ThreadSize = 14
  ThreadType = 1
  Threaded = false
  UseCustomThreadClearance = false
FEATURE [Sketcher::SketchObject] Sketch053
  ArcFitTolerance = 1e-06
  AttachmentSupport = -> [Hole008]
  FullyConstrained = true
  MakeInternals = false
  MapMode = 5
  Placement = pos=(-260,0,0) rot=(0.707107,0,-0.707107;3.14159rad)
  sketch-geometry (22):
    g0: LineSegment [constr] StartX=-210 StartY=6 StartZ=0 EndX=-205 EndY=6 EndZ=0
    g1: LineSegment [constr] StartX=-205 StartY=6 StartZ=0 EndX=-205 EndY=14 EndZ=0
    g2: LineSegment [constr] StartX=-205 StartY=14 StartZ=0 EndX=-210 EndY=14 EndZ=0
    g3: LineSegment [constr] StartX=-210 StartY=14 StartZ=0 EndX=-210 EndY=6 EndZ=0
    g4: LineSegment StartX=-208 StartY=14 StartZ=0 EndX=-210 EndY=10 EndZ=0
    g5: LineSegment StartX=-206 StartY=14 StartZ=0 EndX=-205 EndY=10 EndZ=0
    g6: LineSegment StartX=-205 StartY=10 StartZ=0 EndX=-206 EndY=6 EndZ=0
    g7: LineSegment StartX=-208 StartY=6 StartZ=0 EndX=-210 EndY=10 EndZ=0
    g8: LineSegment [constr] StartX=-200 StartY=15 StartZ=0 EndX=-200 EndY=5 EndZ=0
    g9: LineSegment [constr] StartX=-205 StartY=10 StartZ=0 EndX=-200 EndY=10 EndZ=0
    g10: LineSegment [constr] StartX=-190 StartY=6 StartZ=0 EndX=-195 EndY=6 EndZ=0
    g11: LineSegment [constr] StartX=-195 StartY=6 StartZ=0 EndX=-195 EndY=14 EndZ=0
    g12: LineSegment [constr] StartX=-195 StartY=14 StartZ=0 EndX=-190 EndY=14 EndZ=0
    g13: LineSegment [constr] StartX=-190 StartY=14 StartZ=0 EndX=-190 EndY=6 EndZ=0
    g14: LineSegment StartX=-192 StartY=14 StartZ=0 EndX=-190 EndY=10 EndZ=0
    g15: LineSegment StartX=-194 StartY=14 StartZ=0 EndX=-195 EndY=10 EndZ=0
    g16: LineSegment StartX=-195 StartY=10 StartZ=0 EndX=-194 EndY=6 EndZ=0
    g17: LineSegment StartX=-192 StartY=6 StartZ=0 EndX=-190 EndY=10 EndZ=0
    g18: LineSegment StartX=-208 StartY=14 StartZ=0 EndX=-206 EndY=14 EndZ=0
    g19: LineSegment StartX=-206 StartY=6 StartZ=0 EndX=-208 EndY=6 EndZ=0
    g20: LineSegment StartX=-194 StartY=6 StartZ=0 EndX=-192 EndY=6 EndZ=0
    g21: LineSegment StartX=-192 StartY=14 StartZ=0 EndX=-194 EndY=14 EndZ=0
  constraints (58):
    c: Coincident(g0,g1)
    c: Coincident(g1,g2)
    c: Coincident(g2,g3)
    c: Coincident(g3,g0)
    c: Horizontal(g0)
    c: Horizontal(g2)
    c: Vertical(g1)
    c: Vertical(g3)
    c: DistanceX(g2,g2) = 5
    c: DistanceY(g1,g1) = 8
    c: DistanceX(g0,g-1) = 210
    c: PointOnObject(g4,g2)
    c: PointOnObject(g4,g3)
    c: PointOnObject(g5,g2)
    c: PointOnObject(g5,g1)
    c: PointOnObject(g6,g1)
    c: PointOnObject(g7,g3)
    c: PointOnObject(g6,g0)
    c: PointOnObject(g7,g0)
    c: DistanceX(g0,g7) = 2
    c: DistanceX(g6,g0) = 1
    c: DistanceY(g0,g6) = 4
    c: DistanceY(g5,g1) = 4
    c: DistanceX(g5,g1) = 1
    c: DistanceX(g2,g4) = 2
    c: DistanceY(g4,g2) = 4
    c: DistanceY(g0,g7) = 4
    c: Vertical(g8)
    c: DistanceX(g8,g-1) = 200
    c: DistanceY(g8,g8) = 10
    c: Coincident(g9,g5)
    c: Symmetric(g8,g8,g9)
    c: Horizontal(g9)
    c: Symmetric(g0,g10,g8)
    c: Symmetric(g0,g10,g8)
    c: Symmetric(g1,g11,g8)
    c: Symmetric(g1,g11,g8)
    c: Symmetric(g2,g12,g8)
    c: Symmetric(g2,g12,g8)
    c: Symmetric(g3,g13,g8)
    c: Symmetric(g3,g13,g8)
    c: Symmetric(g4,g14,g8)
    c: Symmetric(g4,g14,g8)
    c: Symmetric(g5,g15,g8)
    c: Symmetric(g5,g15,g8)
    c: Symmetric(g6,g16,g8)
    c: Symmetric(g6,g16,g8)
    c: Symmetric(g7,g17,g8)
    c: Symmetric(g7,g17,g8)
    c: DistanceY(g-1,g9) = 10
    c: Coincident(g18,g4)
    c: Coincident(g18,g5)
    c: Coincident(g19,g6)
    c: Coincident(g19,g7)
    c: Coincident(g20,g16)
    c: Coincident(g20,g17)
    c: Coincident(g21,g14)
    c: Coincident(g21,g15)
FEATURE [PartDesign::Pocket] Pocket017
  BaseFeature = -> Hole008
  Direction = (1,0,2e-16)
  Length = 5
  Length2 = 5
  Placement = pos=(0,0,0) rot=(1,0,0;1.5708rad)
  Profile = -> Sketch053
  ReferenceAxis = -> Sketch053 [N_Axis]
  Suppressed = false
  Type = 1
FEATURE [Part::FeaturePython] Screw028  label="M6x20-Screw"  # WARN: FeaturePython — macro-defined, semantics opaque (R4)
  BaseObject = -> Body006 [Pocket017.Edge63]
  Diameter = 7
  Invert = false
  LeftHanded = false
  Length = 5
  LengthCustom = 20
  MatchOuter = false
  OffsetAngle = 0
  Placement = pos=(-260,129,200) rot=(0,-1,0;1.5708rad)
  Thread = false
  Type = 75
FEATURE [Part::FeaturePython] Screw031  label="M5x12-Screw"  # WARN: FeaturePython — macro-defined, semantics opaque (R4)
  BaseObject = -> Body006 [Pocket017.?Edge131]
  Diameter = 6
  Invert = false
  LeftHanded = false
  Length = 2
  LengthCustom = 12
  MatchOuter = false
  OffsetAngle = 0
  Placement = pos=(-235,144,200) rot=(-1,0,0;1.5708rad)
  Thread = false
  Type = 75
FEATURE [App::Part] Part003  label="ZFollowerFasteners"
  Group = -> [Insert,Insert001,Insert002,Insert003,Screw021,Screw022,Screw023,Screw024,TSlot004,TSlot005,Screw028,Screw031]
  Origin = -> Origin007
FEATURE [Sketcher::SketchObject] Sketch056
  ArcFitTolerance = 1e-06
  AttachmentSupport = -> [Pocket017]
  FullyConstrained = true
  MakeInternals = false
  MapMode = 5
  Placement = pos=(0,4,-9e-16) rot=(-1,0,0;1.5708rad)
  sketch-geometry (4):
    g0: LineSegment StartX=-225 StartY=-185 StartZ=0 EndX=-225 EndY=-215 EndZ=0
    g1: LineSegment StartX=-225 StartY=-215 StartZ=0 EndX=-205 EndY=-215 EndZ=0
    g2: LineSegment StartX=-205 StartY=-215 StartZ=0 EndX=-205 EndY=-185 EndZ=0
    g3: LineSegment StartX=-205 StartY=-185 StartZ=0 EndX=-225 EndY=-185 EndZ=0
  constraints (12):
    c: Coincident(g0,g1)
    c: Coincident(g1,g2)
    c: Coincident(g2,g3)
    c: Coincident(g3,g0)
    c: Vertical(g0)
    c: Vertical(g2)
    c: Horizontal(g1)
    c: Horizontal(g3)
    c: Distance(g0,g2) = 20
    c: Distance(g1,g3) = 30
    c: DistanceX(g0,g-1) = 225
    c: DistanceY(g0,g-1) = 215
FEATURE [PartDesign::Pocket] Pocket019
  BaseFeature = -> Pocket017
  Direction = (0,-1,-2e-16)
  Length = 5
  Length2 = 5
  Placement = pos=(0,0,0) rot=(1,0,0;1.5708rad)
  Profile = -> Sketch056
  ReferenceAxis = -> Sketch056 [N_Axis]
  Suppressed = false
  Type = 1
FEATURE [Sketcher::SketchObject] Sketch057
  ArcFitTolerance = 1e-06
  AttachmentSupport = -> [Pocket019]
  FullyConstrained = true
  MakeInternals = false
  MapMode = 5
  Placement = pos=(-250,0,0) rot=(0.707107,0,0.707107;3.14159rad)
  sketch-geometry (4):
    g0: LineSegment StartX=190 StartY=20 StartZ=0 EndX=190 EndY=0 EndZ=0
    g1: LineSegment StartX=190 StartY=0 StartZ=0 EndX=210 EndY=0 EndZ=0
    g2: LineSegment StartX=210 StartY=0 StartZ=0 EndX=210 EndY=20 EndZ=0
    g3: LineSegment StartX=210 StartY=20 StartZ=0 EndX=190 EndY=20 EndZ=0
  constraints (12):
    c: Coincident(g0,g1)
    c: Coincident(g1,g2)
    c: Coincident(g2,g3)
    c: Coincident(g3,g0)
    c: Vertical(g0)
    c: Vertical(g2)
    c: Horizontal(g1)
    c: Horizontal(g3)
    c: Distance(g0,g2) = 20
    c: Distance(g1,g3) = 20
    c: DistanceX(g-1,g0) = 190
    c: DistanceY(g-1,g0) = 20
FEATURE [PartDesign::Pocket] Pocket020
  BaseFeature = -> Pocket019
  Direction = (-1,0,2e-16)
  Length = 5
  Length2 = 5
  Placement = pos=(0,0,0) rot=(1,0,0;1.5708rad)
  Profile = -> Sketch057
  ReferenceAxis = -> Sketch057 [N_Axis]
  Reversed = true
  Suppressed = false
  Type = 1
FEATURE [PartDesign::Body] Body006  label="MotorHolder"
  AllowCompound = false
  Group = -> [Sketch039,Pad009,Sketch040,Hole006,Sketch041,Pocket013,Sketch042,Pad010,Sketch043,Pad011,Sketch044,Pad012,Sketch045,Pad013,Sketch046,Pad014,Sketch047,Hole007,Sketch048,Pocket014,Sketch049,Pocket015,Sketch052,Hole008,Sketch053,Pocket017,Sketch056,Pocket019,Sketch057,Pocket020]
  Origin = -> Origin026
  Placement = pos=(0,139,0) rot=(0,0,1;0rad)
  Tip = -> Pocket020
FEATURE [Sketcher::SketchObject] Sketch058
  ArcFitTolerance = 1e-06
  AttachmentOffset = pos=(0,0,-144) rot=(0,0,1;0rad)
  AttachmentSupport = -> [XZ_Plane029]
  FullyConstrained = true
  MakeInternals = false
  MapMode = 5
  Placement = pos=(0,144,-3.2e-14) rot=(1,0,0;1.5708rad)
  sketch-geometry (5):
    g0: LineSegment StartX=125 StartY=185 StartZ=0 EndX=175 EndY=185 EndZ=0
    g1: LineSegment StartX=175 StartY=185 StartZ=0 EndX=175 EndY=215 EndZ=0
    g2: LineSegment StartX=175 StartY=215 StartZ=0 EndX=125 EndY=215 EndZ=0
    g3: LineSegment StartX=125 StartY=215 StartZ=0 EndX=125 EndY=185 EndZ=0
    g4: GeomPoint [constr] X=150 Y=200 Z=0
  constraints (13):
    c: Coincident(g0,g1)
    c: Coincident(g1,g2)
    c: Coincident(g2,g3)
    c: Coincident(g3,g0)
    c: Horizontal(g0)
    c: Horizontal(g2)
    c: Vertical(g1)
    c: Vertical(g3)
    c: Symmetric(g2,g0,g4)
    c: Distance(g1,g3) = 50
    c: Distance(g0,g2) = 30
    c: DistanceY(g-1,g4) = 200
    c: DistanceX(g-1,g4) = 150
FEATURE [PartDesign::Pad] Pad015
  Direction = (0,-1,2e-16)
  Length = 28
  Length2 = 10
  Placement = pos=(0,0,0) rot=(1,0,0;1.5708rad)
  Profile = -> Sketch058
  ReferenceAxis = -> Sketch058 [N_Axis]
  Suppressed = false
  Type = 0
FEATURE [Sketcher::SketchObject] Sketch059
  ArcFitTolerance = 1e-06
  AttachmentSupport = -> [Pad015]
  FullyConstrained = true
  MakeInternals = false
  MapMode = 5
  Placement = pos=(0,116,-1.102e-13) rot=(1,0,0;1.5708rad)
  sketch-geometry (1):
    g0: Circle CenterX=160 CenterY=200 CenterZ=0 NormalX=0 NormalY=0 NormalZ=1 AngleXU=0 Radius=4
  constraints (3):
    c: Diameter(g0) = 8
    c: DistanceX(g-1,g0) = 160
    c: DistanceY(g-1,g0) = 200
FEATURE [PartDesign::Hole] Hole009
  BaseFeature = -> Pad015
  CustomThreadClearance = 0
  Depth = 4
  DepthType = 0
  Diameter = 9
  DrillForDepth = false
  DrillPoint = 1
  DrillPointAngle = 118
  HoleCutCountersinkAngle = 90
  HoleCutCustomValues = false
  HoleCutDepth = 0
  HoleCutDiameter = 0
  HoleCutType = 0
  ModelThread = false
  Placement = pos=(0,0,0) rot=(1,0,0;1.5708rad)
  Profile = -> Sketch059
  Suppressed = false
  Tapered = false
  TaperedAngle = 90
  ThreadClass = 0
  ThreadDepth = 4
  ThreadDepthType = 0
  ThreadDirection = 0
  ThreadFit = 0
  ThreadSize = 16
  ThreadType = 1
  Threaded = false
  UseCustomThreadClearance = false
FEATURE [Sketcher::SketchObject] Sketch060
  ArcFitTolerance = 1e-06
  AttachmentSupport = -> [Hole009]
  FullyConstrained = true
  MakeInternals = false
  MapMode = 5
  Placement = pos=(125,0,0) rot=(0.707107,0,-0.707107;3.14159rad)
  sketch-geometry (4):
    g0: LineSegment StartX=-210 StartY=-120 StartZ=0 EndX=-210 EndY=-140 EndZ=0
    g1: LineSegment StartX=-210 StartY=-140 StartZ=0 EndX=-190 EndY=-140 EndZ=0
    g2: LineSegment StartX=-190 StartY=-140 StartZ=0 EndX=-190 EndY=-120 EndZ=0
    g3: LineSegment StartX=-190 StartY=-120 StartZ=0 EndX=-210 EndY=-120 EndZ=0
  constraints (12):
    c: Coincident(g0,g1)
    c: Coincident(g1,g2)
    c: Coincident(g2,g3)
    c: Coincident(g3,g0)
    c: Vertical(g0)
    c: Vertical(g2)
    c: Horizontal(g1)
    c: Horizontal(g3)
    c: Distance(g0,g2) = 20
    c: Distance(g1,g3) = 20
    c: DistanceX(g1,g-1) = 190
    c: DistanceY(g2,g-1) = 120
FEATURE [PartDesign::Pocket] Pocket021
  BaseFeature = -> Hole009
  Direction = (1,0,2e-16)
  Length = 46
  Length2 = 5
  Placement = pos=(0,0,0) rot=(1,0,0;1.5708rad)
  Profile = -> Sketch060
  ReferenceAxis = -> Sketch060 [N_Axis]
  Suppressed = false
  Type = 0
FEATURE [Sketcher::SketchObject] Sketch061
  ArcFitTolerance = 1e-06
  AttachmentSupport = -> [Pocket021]
  FullyConstrained = true
  MakeInternals = false
  MapMode = 5
  Placement = pos=(0,116,-1.102e-13) rot=(1,0,0;1.5708rad)
  sketch-geometry (7):
    g0: LineSegment StartX=125 StartY=200 StartZ=0 EndX=135 EndY=190 EndZ=0
    g1: LineSegment StartX=135 StartY=190 StartZ=0 EndX=135 EndY=185 EndZ=0
    g2: LineSegment StartX=135 StartY=185 StartZ=0 EndX=125 EndY=185 EndZ=0
    g3: LineSegment StartX=125 StartY=185 StartZ=0 EndX=125 EndY=215 EndZ=0
    g4: LineSegment StartX=125 StartY=215 StartZ=0 EndX=135 EndY=215 EndZ=0
    g5: LineSegment StartX=125 StartY=200 StartZ=0 EndX=135 EndY=210 EndZ=0
    g6: LineSegment StartX=135 StartY=215 StartZ=0 EndX=135 EndY=210 EndZ=0
  constraints (21):
    c: DistanceY(g-1,g0) = 200
    c: Coincident(g1,g0)
    c: Coincident(g2,g1)
    c: Horizontal(g2)
    c: Coincident(g3,g2)
    c: Vertical(g3)
    c: Coincident(g4,g3)
    c: Horizontal(g4)
    c: Coincident(g5,g0)
    c: Coincident(g6,g4)
    c: Coincident(g6,g5)
    c: Vertical(g6)
    c: DistanceY(g1,g4) = 30
    c: Vertical(g1)
    c: Equal(g6,g1)
    c: DistanceX(g5,g5) = 10
    c: DistanceY(g0,g5) = 20
    c: Equal(g5,g0)
    c: DistanceX(g0,g0) = 10
    c: DistanceX(g4,g4) = 10
    c: DistanceX(g-1,g3) = 125
FEATURE [PartDesign::Pocket] Pocket022
  BaseFeature = -> Pocket021
  Direction = (0,1,-2e-16)
  Length = 5
  Length2 = 5
  Placement = pos=(0,0,0) rot=(1,0,0;1.5708rad)
  Profile = -> Sketch061
  ReferenceAxis = -> Sketch061 [N_Axis]
  Suppressed = false
  Type = 1
FEATURE [Sketcher::SketchObject] Sketch062
  ArcFitTolerance = 1e-06
  AttachmentSupport = -> [Pocket022]
  FullyConstrained = true
  MakeInternals = false
  MapMode = 5
  Placement = pos=(0,116,-1.102e-13) rot=(1,0,0;1.5708rad)
  sketch-geometry (1):
    g0: Circle CenterX=135 CenterY=200 CenterZ=0 NormalX=0 NormalY=0 NormalZ=1 AngleXU=0 Radius=2.5
  constraints (3):
    c: Diameter(g0) = 5
    c: DistanceX(g-1,g0) = 135
    c: DistanceY(g-1,g0) = 200
FEATURE [PartDesign::Hole] Hole010
  BaseFeature = -> Pocket022
  CustomThreadClearance = 0
  Depth = 130.661
  DepthType = 1
  Diameter = 5.5
  DrillForDepth = false
  DrillPoint = 1
  DrillPointAngle = 118
  HoleCutCountersinkAngle = 90
  HoleCutCustomValues = false
  HoleCutDepth = 0
  HoleCutDiameter = 6.1
  HoleCutType = 0
  ModelThread = false
  Placement = pos=(0,0,0) rot=(1,0,0;1.5708rad)
  Profile = -> Sketch062
  Suppressed = false
  Tapered = false
  TaperedAngle = 90
  ThreadClass = 0
  ThreadDepth = 130.661
  ThreadDepthType = 0
  ThreadDirection = 0
  ThreadFit = 0
  ThreadSize = 13
  ThreadType = 1
  Threaded = false
  UseCustomThreadClearance = false
FEATURE [Sketcher::SketchObject] Sketch063
  ArcFitTolerance = 1e-06
  AttachmentSupport = -> [Hole010]
  FullyConstrained = true
  MakeInternals = false
  MapMode = 5
  Placement = pos=(0,9.46e-14,215) rot=(0,0,1;3.14159rad)
  sketch-geometry (4):
    g0: LineSegment StartX=-129 StartY=-120 StartZ=0 EndX=-171 EndY=-120 EndZ=0
    g1: LineSegment StartX=-171 StartY=-120 StartZ=0 EndX=-171 EndY=-140 EndZ=0
    g2: LineSegment StartX=-171 StartY=-140 StartZ=0 EndX=-129 EndY=-140 EndZ=0
    g3: LineSegment StartX=-129 StartY=-140 StartZ=0 EndX=-129 EndY=-120 EndZ=0
  constraints (12):
    c: Coincident(g0,g1)
    c: Coincident(g1,g2)
    c: Coincident(g2,g3)
    c: Coincident(g3,g0)
    c: Horizontal(g0)
    c: Horizontal(g2)
    c: Vertical(g1)
    c: Vertical(g3)
    c: Distance(g1,g3) = 42
    c: Distance(g0,g2) = 20
    c: DistanceY(g0,g-1) = 120
    c: DistanceX(g0,g-1) = 129
FEATURE [PartDesign::Pocket] Pocket023
  BaseFeature = -> Hole010
  Direction = (0,0,-1)
  Length = 25
  Length2 = 5
  Placement = pos=(0,0,0) rot=(1,0,0;1.5708rad)
  Profile = -> Sketch063
  ReferenceAxis = -> Sketch063 [N_Axis]
  Suppressed = false
  Type = 0
FEATURE [Sketcher::SketchObject] Sketch064
  ArcFitTolerance = 1e-06
  AttachmentSupport = -> [Pocket023]
  FullyConstrained = true
  MakeInternals = false
  MapMode = 5
  Placement = pos=(0,120,-2.64e-14) rot=(-1,0,0;1.5708rad)
  sketch-geometry (4):
    g0: LineSegment StartX=150 StartY=-190 StartZ=0 EndX=150 EndY=-210 EndZ=0
    g1: LineSegment StartX=150 StartY=-210 StartZ=0 EndX=152 EndY=-210 EndZ=0
    g2: LineSegment StartX=152 StartY=-210 StartZ=0 EndX=152 EndY=-190 EndZ=0
    g3: LineSegment StartX=152 StartY=-190 StartZ=0 EndX=150 EndY=-190 EndZ=0
  constraints (12):
    c: Coincident(g0,g1)
    c: Coincident(g1,g2)
    c: Coincident(g2,g3)
    c: Coincident(g3,g0)
    c: Vertical(g0)
    c: Vertical(g2)
    c: Horizontal(g1)
    c: Horizontal(g3)
    c: Distance(g0,g2) = 2
    c: Distance(g1,g3) = 20
    c: DistanceY(g0,g-1) = 190
    c: DistanceX(g-1,g0) = 150
FEATURE [PartDesign::Pad] Pad016
  BaseFeature = -> Pocket023
  Direction = (0,1,2e-16)
  Length = 5
  Length2 = 10
  Placement = pos=(0,0,0) rot=(1,0,0;1.5708rad)
  Profile = -> Sketch064
  ReferenceAxis = -> Sketch064 [N_Axis]
  Suppressed = false
  Type = 0
FEATURE [Sketcher::SketchObject] Sketch065
  ArcFitTolerance = 1e-06
  AttachmentSupport = -> [Pocket023]
  FullyConstrained = true
  MakeInternals = false
  MapMode = 5
  Placement = pos=(0,144,-1.368e-13) rot=(-1,0,0;1.5708rad)
  sketch-geometry (11):
    g0: LineSegment StartX=166 StartY=-190 StartZ=0 EndX=171 EndY=-190 EndZ=0
    g1: LineSegment StartX=171 StartY=-190 StartZ=0 EndX=171 EndY=-195 EndZ=0
    g2: ArcOfCircle CenterX=166 CenterY=-195 CenterZ=0 NormalX=0 NormalY=0 NormalZ=1 AngleXU=0 Radius=5 StartAngle=1e-16 EndAngle=1.5708
    g3: LineSegment [constr] StartX=166 StartY=-195 StartZ=0 EndX=166 EndY=-190 EndZ=0
    g4: LineSegment [constr] StartX=166 StartY=-195 StartZ=0 EndX=171 EndY=-195 EndZ=0
    g5: LineSegment [constr] StartX=150 StartY=-200 StartZ=0 EndX=190 EndY=-200 EndZ=0
    g6: LineSegment StartX=166 StartY=-210 StartZ=0 EndX=171 EndY=-210 EndZ=0
    g7: LineSegment StartX=171 StartY=-210 StartZ=0 EndX=171 EndY=-205 EndZ=0
    g8: ArcOfCircle CenterX=166 CenterY=-205 CenterZ=0 NormalX=0 NormalY=0 NormalZ=1 AngleXU=0 Radius=5 StartAngle=4.71239 EndAngle=6.28319
    g9: LineSegment [constr] StartX=166 StartY=-205 StartZ=0 EndX=166 EndY=-210 EndZ=0
    g10: LineSegment [constr] StartX=166 StartY=-205 StartZ=0 EndX=171 EndY=-205 EndZ=0
  constraints (29):
    c: Horizontal(g0)
    c: Coincident(g1,g0)
    c: Vertical(g1)
    c: Coincident(g2,g0)
    c: Coincident(g2,g1)
    c: Coincident(g3,g2)
    c: Coincident(g3,g0)
    c: Coincident(g4,g2)
    c: Coincident(g4,g1)
    c: Horizontal(g4)
    c: Vertical(g3)
    c: DistanceX(g0,g0) = 5
    c: DistanceY(g1,g-1) = 195
    c: DistanceX(g-1,g0) = 171
    c: Horizontal(g5)
    c: DistanceY(g5,g-1) = 200
    c: DistanceX(g5,g5) = 40
    c: Symmetric(g0,g6,g5)
    c: Symmetric(g0,g6,g5)
    c: Symmetric(g1,g7,g5)
    c: Symmetric(g1,g7,g5)
    c: Equal(g2,g8)
    c: Symmetric(g2,g8,g5)
    c: Symmetric(g2,g8,g5)
    c: Symmetric(g3,g9,g5)
    c: Symmetric(g3,g9,g5)
    c: Symmetric(g4,g10,g5)
    c: Symmetric(g4,g10,g5)
    c: DistanceX(g-1,g5) = 150
FEATURE [PartDesign::Pad] Pad017
  BaseFeature = -> Pad016
  Direction = (0,1,2e-16)
  Length = 10
  Length2 = 10
  Offset = -4
  Placement = pos=(0,0,0) rot=(1,0,0;1.5708rad)
  Profile = -> Sketch065
  ReferenceAxis = -> Sketch065 [N_Axis]
  Reversed = true
  Suppressed = false
  Type = 1
FEATURE [Sketcher::SketchObject] Sketch066
  ArcFitTolerance = 1e-06
  AttachmentSupport = -> [Pad017]
  FullyConstrained = true
  MakeInternals = false
  MapMode = 5
  Placement = pos=(0,140,-3.08e-14) rot=(1,0,0;1.5708rad)
  sketch-geometry (4):
    g0: LineSegment StartX=166 StartY=215 StartZ=0 EndX=166 EndY=210 EndZ=0
    g1: LineSegment StartX=166 StartY=210 StartZ=0 EndX=171 EndY=210 EndZ=0
    g2: LineSegment StartX=171 StartY=210 StartZ=0 EndX=171 EndY=215 EndZ=0
    g3: LineSegment StartX=171 StartY=215 StartZ=0 EndX=166 EndY=215 EndZ=0
  constraints (12):
    c: Coincident(g0,g1)
    c: Coincident(g1,g2)
    c: Coincident(g2,g3)
    c: Coincident(g3,g0)
    c: Vertical(g0)
    c: Vertical(g2)
    c: Horizontal(g1)
    c: Horizontal(g3)
    c: Distance(g0,g2) = 5
    c: Distance(g1,g3) = 5
    c: DistanceX(g-1,g0) = 166
    c: DistanceY(g-1,g0) = 215
FEATURE [PartDesign::Pad] Pad018
  BaseFeature = -> Pad017
  Direction = (0,-1,2e-16)
  Length = 10
  Length2 = 10
  Placement = pos=(0,0,0) rot=(1,0,0;1.5708rad)
  Profile = -> Sketch066
  ReferenceAxis = -> Sketch066 [N_Axis]
  Suppressed = false
  Type = 2
FEATURE [Sketcher::SketchObject] Sketch067
  ArcFitTolerance = 1e-06
  AttachmentSupport = -> [Pad018]
  FullyConstrained = true
  MakeInternals = false
  MapMode = 5
  Placement = pos=(0,144,-1.368e-13) rot=(-1,0,0;1.5708rad)
  sketch-geometry (4):
    g0: LineSegment StartX=152 StartY=-215 StartZ=0 EndX=171 EndY=-215 EndZ=0
    g1: LineSegment StartX=171 StartY=-215 StartZ=0 EndX=171 EndY=-190 EndZ=0
    g2: LineSegment StartX=171 StartY=-190 StartZ=0 EndX=152 EndY=-190 EndZ=0
    g3: LineSegment StartX=152 StartY=-190 StartZ=0 EndX=152 EndY=-215 EndZ=0
  constraints (12):
    c: Coincident(g0,g1)
    c: Coincident(g1,g2)
    c: Coincident(g2,g3)
    c: Coincident(g3,g0)
    c: Horizontal(g0)
    c: Horizontal(g2)
    c: Vertical(g1)
    c: Vertical(g3)
    c: Distance(g1,g3) = 19
    c: Distance(g0,g2) = 25
    c: DistanceY(g1,g-1) = 190
    c: DistanceX(g-1,g0) = 152
FEATURE [PartDesign::Pocket] Pocket024
  BaseFeature = -> Pad018
  Direction = (0,-1,-2e-16)
  Length = 4
  Length2 = 5
  Placement = pos=(0,0,0) rot=(1,0,0;1.5708rad)
  Profile = -> Sketch067
  ReferenceAxis = -> Sketch067 [N_Axis]
  Suppressed = false
  Type = 0
FEATURE [Sketcher::SketchObject] Sketch068
  ArcFitTolerance = 1e-06
  AttachmentSupport = -> [Pocket024]
  FullyConstrained = true
  MakeInternals = false
  MapMode = 5
  Placement = pos=(0,140,-3.08e-14) rot=(1,0,0;1.5708rad)
  sketch-geometry (4):
    g0: LineSegment StartX=152 StartY=210 StartZ=0 EndX=150 EndY=210 EndZ=0
    g1: LineSegment StartX=150 StartY=210 StartZ=0 EndX=150 EndY=190 EndZ=0
    g2: LineSegment StartX=150 StartY=190 StartZ=0 EndX=152 EndY=190 EndZ=0
    g3: LineSegment StartX=152 StartY=190 StartZ=0 EndX=152 EndY=210 EndZ=0
  constraints (12):
    c: Coincident(g0,g1)
    c: Coincident(g1,g2)
    c: Coincident(g2,g3)
    c: Coincident(g3,g0)
    c: Horizontal(g0)
    c: Horizontal(g2)
    c: Vertical(g1)
    c: Vertical(g3)
    c: Distance(g0,g2) = 20
    c: DistanceX(g0,g0) = 2
    c: DistanceX(g-1,g1) = 150
    c: DistanceY(g-1,g1) = 190
FEATURE [PartDesign::Pad] Pad019
  BaseFeature = -> Pocket024
  Direction = (0,-1,2e-16)
  Length = 5
  Length2 = 10
  Placement = pos=(0,0,0) rot=(1,0,0;1.5708rad)
  Profile = -> Sketch068
  ReferenceAxis = -> Sketch068 [N_Axis]
  Suppressed = false
  Type = 0
FEATURE [PartDesign::Body] Body007  label="XIdler"
  AllowCompound = false
  Group = -> [Sketch058,Pad015,Sketch059,Hole009,Sketch060,Pocket021,Sketch061,Pocket022,Sketch062,Hole010,Sketch063,Pocket023,Sketch064,Pad016,Sketch065,Pad017,Sketch066,Pad018,Sketch067,Pocket024,Sketch068,Pad019]
  Origin = -> Origin029
  Tip = -> Pad019
FEATURE [Sketcher::SketchObject] Sketch069
  ArcFitTolerance = 1e-06
  AttachmentOffset = pos=(0,0,-136) rot=(0,0,1;0rad)
  AttachmentSupport = -> [XZ_Plane030]
  FullyConstrained = true
  MakeInternals = false
  MapMode = 5
  Placement = pos=(0,136,-3.02e-14) rot=(1,0,0;1.5708rad)
  sketch-geometry (5):
    g0: LineSegment StartX=-45 StartY=235 StartZ=0 EndX=-45 EndY=165 EndZ=0
    g1: LineSegment StartX=-45 StartY=165 StartZ=0 EndX=45 EndY=165 EndZ=0
    g2: LineSegment StartX=45 StartY=165 StartZ=0 EndX=45 EndY=235 EndZ=0
    g3: LineSegment StartX=45 StartY=235 StartZ=0 EndX=-45 EndY=235 EndZ=0
    g4: GeomPoint X=0 Y=200 Z=0
  constraints (13):
    c: Coincident(g0,g1)
    c: Coincident(g1,g2)
    c: Coincident(g2,g3)
    c: Coincident(g3,g0)
    c: Vertical(g0)
    c: Vertical(g2)
    c: Horizontal(g1)
    c: Horizontal(g3)
    c: Distance(g0,g2) = 90
    c: Distance(g1,g3) = 70
    c: Symmetric(g0,g2,g4)
    c: PointOnObject(g4,g-2)
    c: DistanceY(g-1,g4) = 200
FEATURE [Sketcher::SketchObject] Sketch070
  ArcFitTolerance = 1e-06
  AttachmentOffset = pos=(0,0,480) rot=(0,0,1;0rad)
  AttachmentSupport = -> [XY_Plane031]
  FullyConstrained = true
  MakeInternals = false
  MapMode = 5
  Placement = pos=(0,0,480) rot=(0,0,1;0rad)
  sketch-geometry (6):
    g0: LineSegment StartX=-190 StartY=160 StartZ=0 EndX=-190 EndY=140 EndZ=0
    g1: LineSegment StartX=-190 StartY=140 StartZ=0 EndX=-150 EndY=140 EndZ=0
    g2: LineSegment StartX=-150 StartY=140 StartZ=0 EndX=-150 EndY=160 EndZ=0
    g3: LineSegment StartX=-190 StartY=194 StartZ=0 EndX=-190 EndY=160 EndZ=0
    g4: LineSegment StartX=-150 StartY=160 StartZ=0 EndX=-150 EndY=194 EndZ=0
    g5: LineSegment StartX=-190 StartY=194 StartZ=0 EndX=-150 EndY=194 EndZ=0
  constraints (18):
    c: Coincident(g0,g1)
    c: Coincident(g1,g2)
    c: Vertical(g0)
    c: Vertical(g2)
    c: Horizontal(g1)
    c: Distance(g0,g2) = 40
    c: Distance(g1,g0) = 20
    c: Coincident(g3,g0)
    c: Coincident(g4,g2)
    c: Coincident(g5,g3)
    c: Coincident(g5,g4)
    c: Horizontal(g5)
    c: Equal(g3,g4)
    c: DistanceX(g4,g4) = 0
    c: DistanceX(g3,g3) = 0
    c: DistanceY(g4,g4) = 34
    c: DistanceX(g1,g-1) = 150
    c: DistanceY(g-1,g1) = 140
FEATURE [PartDesign::Pad] Pad020
  Direction = (0,0,1)
  Length = 20
  Length2 = 10
  Profile = -> Sketch070
  ReferenceAxis = -> Sketch070 [N_Axis]
  Suppressed = false
  Type = 0
FEATURE [Sketcher::SketchObject] Sketch071
  ArcFitTolerance = 1e-06
  AttachmentSupport = -> [Pad020]
  FullyConstrained = true
  MakeInternals = false
  MapMode = 5
  Placement = pos=(0,0,500) rot=(0,0,1;0rad)
  sketch-geometry (1):
    g0: Circle CenterX=-170 CenterY=181 CenterZ=0 NormalX=0 NormalY=0 NormalZ=1 AngleXU=0 Radius=4
  constraints (3):
    c: Diameter(g0) = 8
    c: DistanceX(g0,g-1) = 170
    c: DistanceY(g-1,g0) = 181
FEATURE [PartDesign::Hole] Hole011
  BaseFeature = -> Pad020
  CustomThreadClearance = 0
  Depth = 25
  DepthType = 0
  Diameter = 8.4
  DrillForDepth = false
  DrillPoint = 1
  DrillPointAngle = 118
  HoleCutCountersinkAngle = 90
  HoleCutCustomValues = false
  HoleCutDepth = 0
  HoleCutDiameter = 0
  HoleCutType = 0
  ModelThread = false
  Profile = -> Sketch071
  Suppressed = false
  Tapered = false
  TaperedAngle = 90
  ThreadClass = 0
  ThreadDepth = 25
  ThreadDepthType = 0
  ThreadDirection = 0
  ThreadFit = 1
  ThreadSize = 16
  ThreadType = 1
  Threaded = false
  UseCustomThreadClearance = false
FEATURE [Sketcher::SketchObject] Sketch072
  ArcFitTolerance = 1e-06
  AttachmentSupport = -> [Hole011]
  FullyConstrained = true
  MakeInternals = false
  MapMode = 5
  Placement = pos=(0,0,500) rot=(0,0,1;0rad)
  sketch-geometry (3):
    g0: Circle CenterX=-180 CenterY=150 CenterZ=0 NormalX=0 NormalY=0 NormalZ=1 AngleXU=0 Radius=2.5
    g1: Circle CenterX=-160 CenterY=150 CenterZ=0 NormalX=0 NormalY=0 NormalZ=1 AngleXU=0 Radius=2.5
    g2: LineSegment [constr] StartX=-180 StartY=150 StartZ=0 EndX=-160 EndY=150 EndZ=0
  constraints (8):
    c: Diameter(g0) = 5
    c: Diameter(g1) = 5
    c: Coincident(g2,g0)
    c: Coincident(g2,g1)
    c: Horizontal(g2)
    c: DistanceX(g1,g-1) = 160
    c: DistanceX(g2,g2) = 20
    c: DistanceY(g-1,g1) = 150
FEATURE [PartDesign::Hole] Hole012
  BaseFeature = -> Hole011
  CustomThreadClearance = 0
  Depth = 25
  DepthType = 0
  Diameter = 5.5
  DrillForDepth = false
  DrillPoint = 1
  DrillPointAngle = 118
  HoleCutCountersinkAngle = 90
  HoleCutCustomValues = false
  HoleCutDepth = 0
  HoleCutDiameter = 6.1
  HoleCutType = 0
  ModelThread = false
  Profile = -> Sketch072
  Suppressed = false
  Tapered = false
  TaperedAngle = 90
  ThreadClass = 0
  ThreadDepth = 25
  ThreadDepthType = 0
  ThreadDirection = 0
  ThreadFit = 0
  ThreadSize = 13
  ThreadType = 1
  Threaded = false
  UseCustomThreadClearance = false
FEATURE [Sketcher::SketchObject] Sketch073
  ArcFitTolerance = 1e-06
  AttachmentSupport = -> [Hole012]
  FullyConstrained = true
  MakeInternals = false
  MapMode = 5
  Placement = pos=(0,0,500) rot=(0,0,1;0rad)
  sketch-geometry (4):
    g0: LineSegment StartX=-150 StartY=160 StartZ=0 EndX=-190 EndY=160 EndZ=0
    g1: LineSegment StartX=-190 StartY=160 StartZ=0 EndX=-190 EndY=140 EndZ=0
    g2: LineSegment StartX=-190 StartY=140 StartZ=0 EndX=-150 EndY=140 EndZ=0
    g3: LineSegment StartX=-150 StartY=140 StartZ=0 EndX=-150 EndY=160 EndZ=0
  constraints (12):
    c: Coincident(g0,g1)
    c: Coincident(g1,g2)
    c: Coincident(g2,g3)
    c: Coincident(g3,g0)
    c: Horizontal(g0)
    c: Horizontal(g2)
    c: Vertical(g1)
    c: Vertical(g3)
    c: Distance(g1,g3) = 40
    c: Distance(g0,g2) = 20
    c: DistanceX(g0,g-1) = 150
    c: DistanceY(g-1,g0) = 160
FEATURE [PartDesign::Pocket] Pocket025
  BaseFeature = -> Hole012
  Direction = (0,0,-1)
  Length = 10
  Length2 = 5
  Profile = -> Sketch073
  ReferenceAxis = -> Sketch073 [N_Axis]
  Suppressed = false
  Type = 0
FEATURE [Sketcher::SketchObject] Sketch074
  ArcFitTolerance = 1e-06
  AttachmentSupport = -> [YZ_Plane031]
  FullyConstrained = true
  MakeInternals = false
  MapMode = 5
  Placement = pos=(0,0,0) rot=(0.57735,0.57735,0.57735;2.0944rad)
  sketch-geometry (4):
    g0: LineSegment StartX=194 StartY=490 StartZ=0 EndX=194 EndY=480 EndZ=0
    g1: LineSegment StartX=194 StartY=480 StartZ=0 EndX=169 EndY=480 EndZ=0
    g2: LineSegment StartX=169 StartY=480 StartZ=0 EndX=169 EndY=490 EndZ=0
    g3: LineSegment StartX=169 StartY=490 StartZ=0 EndX=194 EndY=490 EndZ=0
  constraints (12):
    c: Coincident(g0,g1)
    c: Coincident(g1,g2)
    c: Coincident(g2,g3)
    c: Coincident(g3,g0)
    c: Vertical(g0)
    c: Vertical(g2)
    c: Horizontal(g1)
    c: Horizontal(g3)
    c: Distance(g0,g2) = 25
    c: Distance(g1,g3) = 10
    c: DistanceX(g-1,g2) = 169
    c: DistanceY(g-1,g2) = 490
FEATURE [PartDesign::Pocket] Pocket026
  BaseFeature = -> Pocket025
  Direction = (-1,0,0)
  Length = 5
  Length2 = 5
  Profile = -> Sketch074
  ReferenceAxis = -> Sketch074 [N_Axis]
  Suppressed = false
  Type = 1
FEATURE [Sketcher::SketchObject] Sketch075
  ArcFitTolerance = 1e-06
  AttachmentSupport = -> [Pocket026]
  FullyConstrained = true
  MakeInternals = false
  MapMode = 5
  Placement = pos=(0,0,500) rot=(0,0,1;0rad)
  sketch-geometry (4):
    g0: LineSegment StartX=-190 StartY=186 StartZ=0 EndX=-190 EndY=176 EndZ=0
    g1: LineSegment StartX=-190 StartY=176 StartZ=0 EndX=-150 EndY=176 EndZ=0
    g2: LineSegment StartX=-150 StartY=176 StartZ=0 EndX=-150 EndY=186 EndZ=0
    g3: LineSegment StartX=-150 StartY=186 StartZ=0 EndX=-190 EndY=186 EndZ=0
  constraints (12):
    c: Coincident(g0,g1)
    c: Coincident(g1,g2)
    c: Coincident(g2,g3)
    c: Coincident(g3,g0)
    c: Vertical(g0)
    c: Vertical(g2)
    c: Horizontal(g1)
    c: Horizontal(g3)
    c: Distance(g0,g2) = 40
    c: Distance(g1,g3) = 10
    c: DistanceX(g2,g-1) = 150
    c: DistanceY(g-1,g1) = 176
FEATURE [PartDesign::Pad] Pad021
  BaseFeature = -> Pocket026
  Direction = (0,0,1)
  Length = 2
  Length2 = 10
  Profile = -> Sketch075
  ReferenceAxis = -> Sketch075 [N_Axis]
  Suppressed = false
  Type = 0
FEATURE [PartDesign::Body] Body009  label="ThreadedRodAligner"
  AllowCompound = false
  Group = -> [Sketch070,Pad020,Sketch071,Hole011,Sketch072,Hole012,Sketch073,Pocket025,Sketch074,Pocket026,Sketch075,Pad021]
  Origin = -> Origin031
  Tip = -> Pad021
FEATURE [Part::Feature] Part__Feature127  label="E3D v6 HotEnd - Heatbreak (1) (1)"
  Placement = pos=(-6.128e-13,-23.6743,8.42574) rot=(0,-0.707107,0.707107;3.14159rad)
  shape: bbox 7 x 21.9 x 7 mm, 14 faces (baked)
FEATURE [Part::Feature] Part__Feature128  label="E3D v6 HotEnd - Nozzle (1) (1)"
  Placement = pos=(-3.242e-13,-34.1743,8.42574) rot=(-0.186157,-0.694747,0.694747;3.50969rad)
  shape: bbox 7 x 12.5 x 8.083 mm, 22 faces (baked)
FEATURE [Part::Feature] Part__Feature129  label="E3D v6 HotEnd - Heat Block (1) (1)"
  Placement = pos=(15.5,-30.1743,0.425745) rot=(0,1,0;3.14159rad)
  shape: bbox 23 x 11.5 x 16 mm, 37 faces (baked)
FEATURE [Part::Feature] Part__Feature130  label="Ceramic Cartridge Heater (1)"
  Placement = pos=(7,-26.1743,-1.57426) rot=(0,1,0;3.14159rad)
  shape: bbox 6 x 6 x 20 mm, 3 faces (baked)
FEATURE [Part::Feature] Part__Feature131  label="E3D v6 HotEnd - Heatsink (1) (1)"
  Placement = pos=(8.127e-13,-16.5743,8.42574) rot=(0,0.707107,-0.707107;3.14159rad)
  shape: bbox 22.3 x 43.7 x 22.3 mm, 64 faces (baked)
FEATURE [App::Part] E3D_V6_Hotend_v2  label="E3D V6 Hotend v2"
  Group = -> [Part__Feature127,Part__Feature128,Part__Feature129,Part__Feature130,Part__Feature131]
  Origin = -> Origin032
  Placement = pos=(8.43,119,189) rot=(0.58,-0.58,-0.58;2.0944rad)
FEATURE [Part::Feature] Part__Feature132  label="Hotend 3010 Fan"
  Placement = pos=(0,92,187) rot=(0.58,0.58,0.58;4.18879rad)
  shape: bbox 30 x 10 x 30 mm, 82 faces (baked)
FEATURE [Part::Feature] Part__Feature133  label="BLTOUCH_V3-1"
  Placement = pos=(0,40.3,0) rot=(0,1,0;3.14159rad)
  shape: bbox 26.01 x 40.31 x 16.65 mm, 900 faces (baked)
FEATURE [Part::Feature] Part__Feature134  label="BLTOUCH_V3-1_CABLE"
  Placement = pos=(0,24.3,-6.7) rot=(0,1,0;3.14159rad)
  shape: bbox 7.9 x 23.9 x 3 mm, 28 faces (baked)
FEATURE [Part::Feature] Part__Feature135  label="BLTOUCH_V3-1_SCREW"
  Placement = pos=(9,38.05,0) rot=(1,0,0;3.14159rad)
  shape: bbox 5.5 x 7.75 x 5.5 mm, 14 faces (baked)
FEATURE [Part::Feature] Part__Feature136  label="BLTOUCH_V3-1_SCREW001"
  Placement = pos=(-9,38.05,0) rot=(1,0,0;3.14159rad)
  shape: bbox 5.5 x 7.75 x 5.5 mm, 14 faces (baked)
FEATURE [App::Part] BLTouch_V3_1_v2  label="BLTouch V3.1 v2"
  Group = -> [Part__Feature133,Part__Feature134,Part__Feature135,Part__Feature136]
  Origin = -> Origin033
  Placement = pos=(-34,119,158.5) rot=(0.58,0.58,0.58;2.0944rad)
FEATURE [Part::Feature] Part__Feature137  label="3010 DC Axial Fan v004"
  Placement = pos=(38.5,111,186) rot=(-0.92,0,0.38;3.14857rad)
  shape: bbox 28.38 x 30.14 x 28.43 mm, 82 faces (baked)
FEATURE [App::Part] Part008  label="Non-Printed Parts"
  Group = -> [Part__Feature137,BLTouch_V3_1_v2,Part__Feature132,E3D_V6_Hotend_v2]
  Origin = -> Origin034
FEATURE [PartDesign::Pad] Pad022
  Direction = (0,-1,2e-16)
  Length = 4
  Length2 = 10
  Placement = pos=(0,0,0) rot=(1,0,0;1.5708rad)
  Profile = -> Sketch069
  ReferenceAxis = -> Sketch069 [N_Axis]
  Suppressed = false
  Type = 0
FEATURE [Sketcher::SketchObject] Sketch076
  ArcFitTolerance = 1e-06
  AttachmentSupport = -> [XZ_Plane030]
  FullyConstrained = true
  MakeInternals = false
  MapMode = 5
  Placement = pos=(0,0,0) rot=(1,0,0;1.5708rad)
  sketch-geometry (5):
    g0: Circle CenterX=-20 CenterY=220 CenterZ=0 NormalX=0 NormalY=0 NormalZ=1 AngleXU=0 Radius=2.5
    g1: LineSegment [constr] StartX=-35 StartY=200 StartZ=0 EndX=35 EndY=200 EndZ=0
    g2: Circle CenterX=20 CenterY=220 CenterZ=0 NormalX=0 NormalY=0 NormalZ=1 AngleXU=0 Radius=2.5
    g3: Circle CenterX=-20 CenterY=180 CenterZ=0 NormalX=0 NormalY=0 NormalZ=1 AngleXU=0 Radius=2.5
    g4: Circle CenterX=20 CenterY=180 CenterZ=0 NormalX=0 NormalY=0 NormalZ=1 AngleXU=0 Radius=2.5
  constraints (12):
    c: Diameter(g0) = 5
    c: DistanceY(g-1,g1) = 200
    c: DistanceX(g1,g1) = 70
    c: Distance(g0,g1) = 20
    c: Distance(g0,g-2) = 20
    c: Equal(g0,g2)
    c: Symmetric(g0,g2,g-2)
    c: Equal(g0,g3)
    c: Symmetric(g0,g3,g1)
    c: Equal(g2,g4)
    c: Symmetric(g2,g4,g1)
    c: Symmetric(g1,g1,g-2)
FEATURE [PartDesign::Hole] Hole013
  BaseFeature = -> Pad022
  CustomThreadClearance = 0
  Depth = 346.358
  DepthType = 1
  Diameter = 5.5
  DrillForDepth = false
  DrillPoint = 1
  DrillPointAngle = 118
  HoleCutCountersinkAngle = 90
  HoleCutCustomValues = false
  HoleCutDepth = 0
  HoleCutDiameter = 6.1
  HoleCutType = 0
  ModelThread = false
  Placement = pos=(0,0,0) rot=(1,0,0;1.5708rad)
  Profile = -> Sketch076
  Suppressed = false
  Tapered = false
  TaperedAngle = 90
  ThreadClass = 0
  ThreadDepth = 346.358
  ThreadDepthType = 0
  ThreadDirection = 0
  ThreadFit = 0
  ThreadSize = 13
  ThreadType = 1
  Threaded = false
  UseCustomThreadClearance = false
FEATURE [Part::Feature] Part__Feature138  label="6153K690_625-2RS SST BALL BEARING, SEALED v053"
  Placement = pos=(3.05,0,1.33e-14) rot=(0,1,0;1.5708rad)
  shape: bbox 5 x 16 x 16 mm, 8 faces (baked)
FEATURE [Part::Feature] Part__Feature139  label="6153K690_625-2RS SST BALL BEARING, SEALED v054"
  Placement = pos=(3.05,0,1.33e-14) rot=(0,1,0;1.5708rad)
  shape: bbox 5 x 11.37 x 11.37 mm, 8 faces (baked)
FEATURE [Part::Feature] Part__Feature140  label="6153K690_625-2RS SST BALL BEARING, SEALED v055"
  Placement = pos=(3.05,0,1.33e-14) rot=(0,1,0;1.5708rad)
  shape: bbox 2.424 x 2.424 x 2.424 mm, 1 faces (baked)
FEATURE [Part::Feature] Part__Feature141  label="6153K690_625-2RS SST BALL BEARING, SEALED v056"
  Placement = pos=(3.05,0,1.33e-14) rot=(0,1,0;1.5708rad)
  shape: bbox 2.424 x 2.424 x 2.424 mm, 1 faces (baked)
FEATURE [Part::Feature] Part__Feature142  label="6153K690_625-2RS SST BALL BEARING, SEALED v057"
  Placement = pos=(3.05,0,1.33e-14) rot=(0,1,0;1.5708rad)
  shape: bbox 2.424 x 2.424 x 2.424 mm, 1 faces (baked)
FEATURE [Part::Feature] Part__Feature143  label="6153K690_625-2RS SST BALL BEARING, SEALED v058"
  Placement = pos=(3.05,0,1.33e-14) rot=(0,1,0;1.5708rad)
  shape: bbox 2.424 x 2.424 x 2.424 mm, 1 faces (baked)
FEATURE [Part::Feature] Part__Feature144  label="6153K690_625-2RS SST BALL BEARING, SEALED v059"
  Placement = pos=(3.05,0,1.33e-14) rot=(0,1,0;1.5708rad)
  shape: bbox 2.424 x 2.424 x 2.424 mm, 1 faces (baked)
FEATURE [Part::Feature] Part__Feature145  label="6153K690_625-2RS SST BALL BEARING, SEALED v060"
  Placement = pos=(3.05,0,1.33e-14) rot=(0,1,0;1.5708rad)
  shape: bbox 2.424 x 2.424 x 2.424 mm, 1 faces (baked)
FEATURE [Part::Feature] Part__Feature146  label="6153K690_625-2RS SST BALL BEARING, SEALED v061"
  Placement = pos=(3.05,0,1.33e-14) rot=(0,1,0;1.5708rad)
  shape: bbox 2.424 x 2.424 x 2.424 mm, 1 faces (baked)
FEATURE [Part::Feature] Part__Feature147  label="6153K690_625-2RS SST BALL BEARING, SEALED v062"
  Placement = pos=(3.05,0,1.33e-14) rot=(0,1,0;1.5708rad)
  shape: bbox 2.424 x 2.424 x 2.424 mm, 1 faces (baked)
FEATURE [Part::Feature] Part__Feature148  label="6153K690_625-2RS SST BALL BEARING, SEALED v063"
  Placement = pos=(3.05,0,1.33e-14) rot=(0,1,0;1.5708rad)
  shape: bbox 2.424 x 2.424 x 2.424 mm, 1 faces (baked)
FEATURE [Part::Feature] Part__Feature149  label="6153K690_625-2RS SST BALL BEARING, SEALED v064"
  Placement = pos=(3.05,0,1.33e-14) rot=(0,1,0;1.5708rad)
  shape: bbox 2.424 x 2.424 x 2.424 mm, 1 faces (baked)
FEATURE [Part::Feature] Part__Feature150  label="6153K690_625-2RS SST BALL BEARING, SEALED v065"
  Placement = pos=(3.05,0,1.33e-14) rot=(0,1,0;1.5708rad)
  shape: bbox 2.424 x 2.424 x 2.424 mm, 1 faces (baked)
FEATURE [Part::Feature] Part__Feature151  label="6153K690_625-2RS SST BALL BEARING, SEALED v066"
  Placement = pos=(3.05,0,1.33e-14) rot=(0,1,0;1.5708rad)
  shape: bbox 2.424 x 2.424 x 2.424 mm, 1 faces (baked)
FEATURE [Part::Feature] Part__Feature152  label="6153K690_625-2RS SST BALL BEARING, SEALED v067"
  Placement = pos=(3.05,0,1.33e-14) rot=(0,1,0;1.5708rad)
  shape: bbox 1.163 x 11.47 x 11.47 mm, 4 faces (baked)
FEATURE [Part::Feature] Part__Feature153  label="6153K690_625-2RS SST BALL BEARING, SEALED v068"
  Placement = pos=(3.05,0,1.33e-14) rot=(0,1,0;1.5708rad)
  shape: bbox 1.163 x 11.47 x 11.47 mm, 4 faces (baked)
FEATURE [Part::Feature] Part__Feature154  label="6153K690_625-2RS SST BALL BEARING, SEALED v2 (1)051"
  Placement = pos=(-3.05,0,1.33e-14) rot=(0,1,0;1.5708rad)
  shape: bbox 5 x 16 x 16 mm, 8 faces (baked)
FEATURE [Part::Feature] Part__Feature155  label="6153K690_625-2RS SST BALL BEARING, SEALED v2 (1)052"
  Placement = pos=(-3.05,0,1.33e-14) rot=(0,1,0;1.5708rad)
  shape: bbox 5 x 11.37 x 11.37 mm, 8 faces (baked)
FEATURE [Part::Feature] Part__Feature156  label="6153K690_625-2RS SST BALL BEARING, SEALED v2 (1)053"
  Placement = pos=(-3.05,0,1.33e-14) rot=(0,1,0;1.5708rad)
  shape: bbox 2.424 x 2.424 x 2.424 mm, 1 faces (baked)
FEATURE [Part::Feature] Part__Feature157  label="6153K690_625-2RS SST BALL BEARING, SEALED v2 (1)054"
  Placement = pos=(-3.05,0,1.33e-14) rot=(0,1,0;1.5708rad)
  shape: bbox 2.424 x 2.424 x 2.424 mm, 1 faces (baked)
FEATURE [Part::Feature] Part__Feature158  label="6153K690_625-2RS SST BALL BEARING, SEALED v2 (1)055"
  Placement = pos=(-3.05,0,1.33e-14) rot=(0,1,0;1.5708rad)
  shape: bbox 2.424 x 2.424 x 2.424 mm, 1 faces (baked)
FEATURE [Part::Feature] Part__Feature159  label="6153K690_625-2RS SST BALL BEARING, SEALED v2 (1)056"
  Placement = pos=(-3.05,0,1.33e-14) rot=(0,1,0;1.5708rad)
  shape: bbox 2.424 x 2.424 x 2.424 mm, 1 faces (baked)
FEATURE [Part::Feature] Part__Feature160  label="6153K690_625-2RS SST BALL BEARING, SEALED v2 (1)057"
  Placement = pos=(-3.05,0,1.33e-14) rot=(0,1,0;1.5708rad)
  shape: bbox 2.424 x 2.424 x 2.424 mm, 1 faces (baked)
FEATURE [Part::Feature] Part__Feature161  label="6153K690_625-2RS SST BALL BEARING, SEALED v2 (1)058"
  Placement = pos=(-3.05,0,1.33e-14) rot=(0,1,0;1.5708rad)
  shape: bbox 2.424 x 2.424 x 2.424 mm, 1 faces (baked)
FEATURE [Part::Feature] Part__Feature162  label="6153K690_625-2RS SST BALL BEARING, SEALED v2 (1)059"
  Placement = pos=(-3.05,0,1.33e-14) rot=(0,1,0;1.5708rad)
  shape: bbox 2.424 x 2.424 x 2.424 mm, 1 faces (baked)
FEATURE [Part::Feature] Part__Feature163  label="6153K690_625-2RS SST BALL BEARING, SEALED v2 (1)060"
  Placement = pos=(-3.05,0,1.33e-14) rot=(0,1,0;1.5708rad)
  shape: bbox 2.424 x 2.424 x 2.424 mm, 1 faces (baked)
FEATURE [Part::Feature] Part__Feature164  label="6153K690_625-2RS SST BALL BEARING, SEALED v2 (1)061"
  Placement = pos=(-3.05,0,1.33e-14) rot=(0,1,0;1.5708rad)
  shape: bbox 2.424 x 2.424 x 2.424 mm, 1 faces (baked)
FEATURE [Part::Feature] Part__Feature165  label="6153K690_625-2RS SST BALL BEARING, SEALED v2 (1)062"
  Placement = pos=(-3.05,0,1.33e-14) rot=(0,1,0;1.5708rad)
  shape: bbox 2.424 x 2.424 x 2.424 mm, 1 faces (baked)
FEATURE [Part::Feature] Part__Feature166  label="6153K690_625-2RS SST BALL BEARING, SEALED v2 (1)063"
  Placement = pos=(-3.05,0,1.33e-14) rot=(0,1,0;1.5708rad)
  shape: bbox 2.424 x 2.424 x 2.424 mm, 1 faces (baked)
FEATURE [Part::Feature] Part__Feature167  label="6153K690_625-2RS SST BALL BEARING, SEALED v2 (1)064"
  Placement = pos=(-3.05,0,1.33e-14) rot=(0,1,0;1.5708rad)
  shape: bbox 2.424 x 2.424 x 2.424 mm, 1 faces (baked)
FEATURE [Part::Feature] Part__Feature168  label="6153K690_625-2RS SST BALL BEARING, SEALED v2 (1)065"
  Placement = pos=(-3.05,0,1.33e-14) rot=(0,1,0;1.5708rad)
  shape: bbox 1.163 x 11.47 x 11.47 mm, 4 faces (baked)
FEATURE [Part::Feature] Part__Feature169  label="6153K690_625-2RS SST BALL BEARING, SEALED v2 (1)066"
  Placement = pos=(-3.05,0,1.33e-14) rot=(0,1,0;1.5708rad)
  shape: bbox 1.163 x 11.47 x 11.47 mm, 4 faces (baked)
FEATURE [Part::Feature] Part__Feature170  label="Wheel, V-slot Rail for 625 Bearing003"
  shape: bbox 10.2 x 24 x 24 mm, 10 faces (baked)
FEATURE [Part::Feature] Part__Feature171  label="91166A240 WSR, FLAT, M5, STL/Z v004"
  Placement = pos=(-0.55,0,0) rot=(0.707107,0,0.707107;3.14159rad)
  shape: bbox 1.1 x 10 x 10 mm, 4 faces (baked)
FEATURE [App::Part] _153K690_625_2RS_SST_BALL_BEARING__SEALED_v005  label="6153K690_625-2RS SST BALL BEARING, SEALED v069"
  Group = -> [Part__Feature138,Part__Feature139,Part__Feature140,Part__Feature141,Part__Feature142,Part__Feature143,Part__Feature144,Part__Feature145,Part__Feature146,Part__Feature147,Part__Feature148,Part__Feature149,Part__Feature150,Part__Feature151,Part__Feature152,Part__Feature153]
  Origin = -> Origin035
FEATURE [App::Part] _153K690_625_2RS_SST_BALL_BEARING__SEALED_v2__1_003  label="6153K690_625-2RS SST BALL BEARING, SEALED v2 (1)067"
  Group = -> [Part__Feature154,Part__Feature155,Part__Feature156,Part__Feature157,Part__Feature158,Part__Feature159,Part__Feature160,Part__Feature161,Part__Feature162,Part__Feature163,Part__Feature164,Part__Feature165,Part__Feature166,Part__Feature167,Part__Feature168,Part__Feature169]
  Origin = -> Origin036
FEATURE [App::Part] Wheel__V_slot_Rail_625_2Z_Bearing_v007  label="Wheel_TL"
  Group = -> [_153K690_625_2RS_SST_BALL_BEARING__SEALED_v005,_153K690_625_2RS_SST_BALL_BEARING__SEALED_v2__1_003,Part__Feature170,Part__Feature171]
  Origin = -> Origin037
  Placement = pos=(-139.49,150,220) rot=(0,0,-1;1.5708rad)
FEATURE [App::Part] Part001  label="XAxisAssembly"
  Group = -> [Body002,Body001,Part003,Part005,Wheel__V_slot_Rail_625_2Z_Bearing_v4,Wheel__V_slot_Rail_625_2Z_Bearing_v005,Wheel__V_slot_Rail_625_2Z_Bearing_v006,Wheel__V_slot_Rail_625_2Z_Bearing_v007,Body004,Body006,Body007]
  Origin = -> Origin003
  Placement = pos=(0,20,0) rot=(0,0,1;0rad)
FEATURE [Part::Feature] Part__Feature172  label="6153K690_625-2RS SST BALL BEARING, SEALED v070"
  Placement = pos=(3.05,0,1.33e-14) rot=(0,1,0;1.5708rad)
  shape: bbox 5 x 16 x 16 mm, 8 faces (baked)
FEATURE [Part::Feature] Part__Feature173  label="6153K690_625-2RS SST BALL BEARING, SEALED v071"
  Placement = pos=(3.05,0,1.33e-14) rot=(0,1,0;1.5708rad)
  shape: bbox 5 x 11.37 x 11.37 mm, 8 faces (baked)
FEATURE [Part::Feature] Part__Feature174  label="6153K690_625-2RS SST BALL BEARING, SEALED v072"
  Placement = pos=(3.05,0,1.33e-14) rot=(0,1,0;1.5708rad)
  shape: bbox 2.424 x 2.424 x 2.424 mm, 1 faces (baked)
FEATURE [Part::Feature] Part__Feature175  label="6153K690_625-2RS SST BALL BEARING, SEALED v073"
  Placement = pos=(3.05,0,1.33e-14) rot=(0,1,0;1.5708rad)
  shape: bbox 2.424 x 2.424 x 2.424 mm, 1 faces (baked)
FEATURE [Part::Feature] Part__Feature176  label="6153K690_625-2RS SST BALL BEARING, SEALED v074"
  Placement = pos=(3.05,0,1.33e-14) rot=(0,1,0;1.5708rad)
  shape: bbox 2.424 x 2.424 x 2.424 mm, 1 faces (baked)
FEATURE [Part::Feature] Part__Feature177  label="6153K690_625-2RS SST BALL BEARING, SEALED v075"
  Placement = pos=(3.05,0,1.33e-14) rot=(0,1,0;1.5708rad)
  shape: bbox 2.424 x 2.424 x 2.424 mm, 1 faces (baked)
FEATURE [Part::Feature] Part__Feature178  label="6153K690_625-2RS SST BALL BEARING, SEALED v076"
  Placement = pos=(3.05,0,1.33e-14) rot=(0,1,0;1.5708rad)
  shape: bbox 2.424 x 2.424 x 2.424 mm, 1 faces (baked)
FEATURE [Part::Feature] Part__Feature179  label="6153K690_625-2RS SST BALL BEARING, SEALED v077"
  Placement = pos=(3.05,0,1.33e-14) rot=(0,1,0;1.5708rad)
  shape: bbox 2.424 x 2.424 x 2.424 mm, 1 faces (baked)
FEATURE [Part::Feature] Part__Feature180  label="6153K690_625-2RS SST BALL BEARING, SEALED v078"
  Placement = pos=(3.05,0,1.33e-14) rot=(0,1,0;1.5708rad)
  shape: bbox 2.424 x 2.424 x 2.424 mm, 1 faces (baked)
FEATURE [Part::Feature] Part__Feature181  label="6153K690_625-2RS SST BALL BEARING, SEALED v079"
  Placement = pos=(3.05,0,1.33e-14) rot=(0,1,0;1.5708rad)
  shape: bbox 2.424 x 2.424 x 2.424 mm, 1 faces (baked)
FEATURE [Part::Feature] Part__Feature182  label="6153K690_625-2RS SST BALL BEARING, SEALED v080"
  Placement = pos=(3.05,0,1.33e-14) rot=(0,1,0;1.5708rad)
  shape: bbox 2.424 x 2.424 x 2.424 mm, 1 faces (baked)
FEATURE [Part::Feature] Part__Feature183  label="6153K690_625-2RS SST BALL BEARING, SEALED v081"
  Placement = pos=(3.05,0,1.33e-14) rot=(0,1,0;1.5708rad)
  shape: bbox 2.424 x 2.424 x 2.424 mm, 1 faces (baked)
FEATURE [Part::Feature] Part__Feature184  label="6153K690_625-2RS SST BALL BEARING, SEALED v082"
  Placement = pos=(3.05,0,1.33e-14) rot=(0,1,0;1.5708rad)
  shape: bbox 2.424 x 2.424 x 2.424 mm, 1 faces (baked)
FEATURE [Part::Feature] Part__Feature185  label="6153K690_625-2RS SST BALL BEARING, SEALED v083"
  Placement = pos=(3.05,0,1.33e-14) rot=(0,1,0;1.5708rad)
  shape: bbox 2.424 x 2.424 x 2.424 mm, 1 faces (baked)
FEATURE [Part::Feature] Part__Feature186  label="6153K690_625-2RS SST BALL BEARING, SEALED v084"
  Placement = pos=(3.05,0,1.33e-14) rot=(0,1,0;1.5708rad)
  shape: bbox 1.163 x 11.47 x 11.47 mm, 4 faces (baked)
FEATURE [Part::Feature] Part__Feature187  label="6153K690_625-2RS SST BALL BEARING, SEALED v085"
  Placement = pos=(3.05,0,1.33e-14) rot=(0,1,0;1.5708rad)
  shape: bbox 1.163 x 11.47 x 11.47 mm, 4 faces (baked)
FEATURE [Part::Feature] Part__Feature188  label="6153K690_625-2RS SST BALL BEARING, SEALED v2 (1)068"
  Placement = pos=(-3.05,0,1.33e-14) rot=(0,1,0;1.5708rad)
  shape: bbox 5 x 16 x 16 mm, 8 faces (baked)
FEATURE [Part::Feature] Part__Feature189  label="6153K690_625-2RS SST BALL BEARING, SEALED v2 (1)069"
  Placement = pos=(-3.05,0,1.33e-14) rot=(0,1,0;1.5708rad)
  shape: bbox 5 x 11.37 x 11.37 mm, 8 faces (baked)
FEATURE [Part::Feature] Part__Feature190  label="6153K690_625-2RS SST BALL BEARING, SEALED v2 (1)070"
  Placement = pos=(-3.05,0,1.33e-14) rot=(0,1,0;1.5708rad)
  shape: bbox 2.424 x 2.424 x 2.424 mm, 1 faces (baked)
FEATURE [Part::Feature] Part__Feature191  label="6153K690_625-2RS SST BALL BEARING, SEALED v2 (1)071"
  Placement = pos=(-3.05,0,1.33e-14) rot=(0,1,0;1.5708rad)
  shape: bbox 2.424 x 2.424 x 2.424 mm, 1 faces (baked)
FEATURE [Part::Feature] Part__Feature192  label="6153K690_625-2RS SST BALL BEARING, SEALED v2 (1)072"
  Placement = pos=(-3.05,0,1.33e-14) rot=(0,1,0;1.5708rad)
  shape: bbox 2.424 x 2.424 x 2.424 mm, 1 faces (baked)
FEATURE [Part::Feature] Part__Feature193  label="6153K690_625-2RS SST BALL BEARING, SEALED v2 (1)073"
  Placement = pos=(-3.05,0,1.33e-14) rot=(0,1,0;1.5708rad)
  shape: bbox 2.424 x 2.424 x 2.424 mm, 1 faces (baked)
FEATURE [Part::Feature] Part__Feature194  label="6153K690_625-2RS SST BALL BEARING, SEALED v2 (1)074"
  Placement = pos=(-3.05,0,1.33e-14) rot=(0,1,0;1.5708rad)
  shape: bbox 2.424 x 2.424 x 2.424 mm, 1 faces (baked)
FEATURE [Part::Feature] Part__Feature195  label="6153K690_625-2RS SST BALL BEARING, SEALED v2 (1)075"
  Placement = pos=(-3.05,0,1.33e-14) rot=(0,1,0;1.5708rad)
  shape: bbox 2.424 x 2.424 x 2.424 mm, 1 faces (baked)
FEATURE [Part::Feature] Part__Feature196  label="6153K690_625-2RS SST BALL BEARING, SEALED v2 (1)076"
  Placement = pos=(-3.05,0,1.33e-14) rot=(0,1,0;1.5708rad)
  shape: bbox 2.424 x 2.424 x 2.424 mm, 1 faces (baked)
FEATURE [Part::Feature] Part__Feature197  label="6153K690_625-2RS SST BALL BEARING, SEALED v2 (1)077"
  Placement = pos=(-3.05,0,1.33e-14) rot=(0,1,0;1.5708rad)
  shape: bbox 2.424 x 2.424 x 2.424 mm, 1 faces (baked)
FEATURE [Part::Feature] Part__Feature198  label="6153K690_625-2RS SST BALL BEARING, SEALED v2 (1)078"
  Placement = pos=(-3.05,0,1.33e-14) rot=(0,1,0;1.5708rad)
  shape: bbox 2.424 x 2.424 x 2.424 mm, 1 faces (baked)
FEATURE [Part::Feature] Part__Feature199  label="6153K690_625-2RS SST BALL BEARING, SEALED v2 (1)079"
  Placement = pos=(-3.05,0,1.33e-14) rot=(0,1,0;1.5708rad)
  shape: bbox 2.424 x 2.424 x 2.424 mm, 1 faces (baked)
FEATURE [Part::Feature] Part__Feature200  label="6153K690_625-2RS SST BALL BEARING, SEALED v2 (1)080"
  Placement = pos=(-3.05,0,1.33e-14) rot=(0,1,0;1.5708rad)
  shape: bbox 2.424 x 2.424 x 2.424 mm, 1 faces (baked)
FEATURE [Part::Feature] Part__Feature201  label="6153K690_625-2RS SST BALL BEARING, SEALED v2 (1)081"
  Placement = pos=(-3.05,0,1.33e-14) rot=(0,1,0;1.5708rad)
  shape: bbox 2.424 x 2.424 x 2.424 mm, 1 faces (baked)
FEATURE [Part::Feature] Part__Feature202  label="6153K690_625-2RS SST BALL BEARING, SEALED v2 (1)082"
  Placement = pos=(-3.05,0,1.33e-14) rot=(0,1,0;1.5708rad)
  shape: bbox 1.163 x 11.47 x 11.47 mm, 4 faces (baked)
FEATURE [Part::Feature] Part__Feature203  label="6153K690_625-2RS SST BALL BEARING, SEALED v2 (1)083"
  Placement = pos=(-3.05,0,1.33e-14) rot=(0,1,0;1.5708rad)
  shape: bbox 1.163 x 11.47 x 11.47 mm, 4 faces (baked)
FEATURE [Part::Feature] Part__Feature204  label="Wheel, V-slot Rail for 625 Bearing004"
  shape: bbox 10.2 x 24 x 24 mm, 10 faces (baked)
FEATURE [Part::Feature] Part__Feature205  label="91166A240 WSR, FLAT, M5, STL/Z v005"
  Placement = pos=(-0.55,0,0) rot=(0.707107,0,0.707107;3.14159rad)
  shape: bbox 1.1 x 10 x 10 mm, 4 faces (baked)
FEATURE [App::Part] _153K690_625_2RS_SST_BALL_BEARING__SEALED_v006  label="6153K690_625-2RS SST BALL BEARING, SEALED v086"
  Group = -> [Part__Feature172,Part__Feature173,Part__Feature174,Part__Feature175,Part__Feature176,Part__Feature177,Part__Feature178,Part__Feature179,Part__Feature180,Part__Feature181,Part__Feature182,Part__Feature183,Part__Feature184,Part__Feature185,Part__Feature186,Part__Feature187]
  Origin = -> Origin038
FEATURE [App::Part] _153K690_625_2RS_SST_BALL_BEARING__SEALED_v2__1_004  label="6153K690_625-2RS SST BALL BEARING, SEALED v2 (1)084"
  Group = -> [Part__Feature188,Part__Feature189,Part__Feature190,Part__Feature191,Part__Feature192,Part__Feature193,Part__Feature194,Part__Feature195,Part__Feature196,Part__Feature197,Part__Feature198,Part__Feature199,Part__Feature200,Part__Feature201,Part__Feature202,Part__Feature203]
  Origin = -> Origin039
FEATURE [App::Part] Wheel__V_slot_Rail_625_2Z_Bearing_v008  label="EWheel_TL"
  Group = -> [_153K690_625_2RS_SST_BALL_BEARING__SEALED_v006,_153K690_625_2RS_SST_BALL_BEARING__SEALED_v2__1_004,Part__Feature204,Part__Feature205]
  Origin = -> Origin040
  Placement = pos=(-20,150,220.5) rot=(0,0,-1;1.5708rad)
FEATURE [Part::Feature] Part__Feature206  label="6153K690_625-2RS SST BALL BEARING, SEALED v087"
  Placement = pos=(3.05,0,1.33e-14) rot=(0,1,0;1.5708rad)
  shape: bbox 5 x 16 x 16 mm, 8 faces (baked)
FEATURE [Part::Feature] Part__Feature207  label="6153K690_625-2RS SST BALL BEARING, SEALED v088"
  Placement = pos=(3.05,0,1.33e-14) rot=(0,1,0;1.5708rad)
  shape: bbox 5 x 11.37 x 11.37 mm, 8 faces (baked)
FEATURE [Part::Feature] Part__Feature208  label="6153K690_625-2RS SST BALL BEARING, SEALED v089"
  Placement = pos=(3.05,0,1.33e-14) rot=(0,1,0;1.5708rad)
  shape: bbox 2.424 x 2.424 x 2.424 mm, 1 faces (baked)
FEATURE [Part::Feature] Part__Feature209  label="6153K690_625-2RS SST BALL BEARING, SEALED v090"
  Placement = pos=(3.05,0,1.33e-14) rot=(0,1,0;1.5708rad)
  shape: bbox 2.424 x 2.424 x 2.424 mm, 1 faces (baked)
FEATURE [Part::Feature] Part__Feature210  label="6153K690_625-2RS SST BALL BEARING, SEALED v091"
  Placement = pos=(3.05,0,1.33e-14) rot=(0,1,0;1.5708rad)
  shape: bbox 2.424 x 2.424 x 2.424 mm, 1 faces (baked)
FEATURE [Part::Feature] Part__Feature211  label="6153K690_625-2RS SST BALL BEARING, SEALED v092"
  Placement = pos=(3.05,0,1.33e-14) rot=(0,1,0;1.5708rad)
  shape: bbox 2.424 x 2.424 x 2.424 mm, 1 faces (baked)
FEATURE [Part::Feature] Part__Feature212  label="6153K690_625-2RS SST BALL BEARING, SEALED v093"
  Placement = pos=(3.05,0,1.33e-14) rot=(0,1,0;1.5708rad)
  shape: bbox 2.424 x 2.424 x 2.424 mm, 1 faces (baked)
FEATURE [Part::Feature] Part__Feature213  label="6153K690_625-2RS SST BALL BEARING, SEALED v094"
  Placement = pos=(3.05,0,1.33e-14) rot=(0,1,0;1.5708rad)
  shape: bbox 2.424 x 2.424 x 2.424 mm, 1 faces (baked)
FEATURE [Part::Feature] Part__Feature214  label="6153K690_625-2RS SST BALL BEARING, SEALED v095"
  Placement = pos=(3.05,0,1.33e-14) rot=(0,1,0;1.5708rad)
  shape: bbox 2.424 x 2.424 x 2.424 mm, 1 faces (baked)
FEATURE [Part::Feature] Part__Feature215  label="6153K690_625-2RS SST BALL BEARING, SEALED v096"
  Placement = pos=(3.05,0,1.33e-14) rot=(0,1,0;1.5708rad)
  shape: bbox 2.424 x 2.424 x 2.424 mm, 1 faces (baked)
FEATURE [Part::Feature] Part__Feature216  label="6153K690_625-2RS SST BALL BEARING, SEALED v097"
  Placement = pos=(3.05,0,1.33e-14) rot=(0,1,0;1.5708rad)
  shape: bbox 2.424 x 2.424 x 2.424 mm, 1 faces (baked)
FEATURE [Part::Feature] Part__Feature217  label="6153K690_625-2RS SST BALL BEARING, SEALED v098"
  Placement = pos=(3.05,0,1.33e-14) rot=(0,1,0;1.5708rad)
  shape: bbox 2.424 x 2.424 x 2.424 mm, 1 faces (baked)
FEATURE [Part::Feature] Part__Feature218  label="6153K690_625-2RS SST BALL BEARING, SEALED v099"
  Placement = pos=(3.05,0,1.33e-14) rot=(0,1,0;1.5708rad)
  shape: bbox 2.424 x 2.424 x 2.424 mm, 1 faces (baked)
FEATURE [Part::Feature] Part__Feature219  label="6153K690_625-2RS SST BALL BEARING, SEALED v100"
  Placement = pos=(3.05,0,1.33e-14) rot=(0,1,0;1.5708rad)
  shape: bbox 2.424 x 2.424 x 2.424 mm, 1 faces (baked)
FEATURE [Part::Feature] Part__Feature220  label="6153K690_625-2RS SST BALL BEARING, SEALED v101"
  Placement = pos=(3.05,0,1.33e-14) rot=(0,1,0;1.5708rad)
  shape: bbox 1.163 x 11.47 x 11.47 mm, 4 faces (baked)
FEATURE [Part::Feature] Part__Feature221  label="6153K690_625-2RS SST BALL BEARING, SEALED v102"
  Placement = pos=(3.05,0,1.33e-14) rot=(0,1,0;1.5708rad)
  shape: bbox 1.163 x 11.47 x 11.47 mm, 4 faces (baked)
FEATURE [Part::Feature] Part__Feature222  label="6153K690_625-2RS SST BALL BEARING, SEALED v2 (1)085"
  Placement = pos=(-3.05,0,1.33e-14) rot=(0,1,0;1.5708rad)
  shape: bbox 5 x 16 x 16 mm, 8 faces (baked)
FEATURE [Part::Feature] Part__Feature223  label="6153K690_625-2RS SST BALL BEARING, SEALED v2 (1)086"
  Placement = pos=(-3.05,0,1.33e-14) rot=(0,1,0;1.5708rad)
  shape: bbox 5 x 11.37 x 11.37 mm, 8 faces (baked)
FEATURE [Part::Feature] Part__Feature224  label="6153K690_625-2RS SST BALL BEARING, SEALED v2 (1)087"
  Placement = pos=(-3.05,0,1.33e-14) rot=(0,1,0;1.5708rad)
  shape: bbox 2.424 x 2.424 x 2.424 mm, 1 faces (baked)
FEATURE [Part::Feature] Part__Feature225  label="6153K690_625-2RS SST BALL BEARING, SEALED v2 (1)088"
  Placement = pos=(-3.05,0,1.33e-14) rot=(0,1,0;1.5708rad)
  shape: bbox 2.424 x 2.424 x 2.424 mm, 1 faces (baked)
FEATURE [Part::Feature] Part__Feature226  label="6153K690_625-2RS SST BALL BEARING, SEALED v2 (1)089"
  Placement = pos=(-3.05,0,1.33e-14) rot=(0,1,0;1.5708rad)
  shape: bbox 2.424 x 2.424 x 2.424 mm, 1 faces (baked)
FEATURE [Part::Feature] Part__Feature227  label="6153K690_625-2RS SST BALL BEARING, SEALED v2 (1)090"
  Placement = pos=(-3.05,0,1.33e-14) rot=(0,1,0;1.5708rad)
  shape: bbox 2.424 x 2.424 x 2.424 mm, 1 faces (baked)
FEATURE [Part::Feature] Part__Feature228  label="6153K690_625-2RS SST BALL BEARING, SEALED v2 (1)091"
  Placement = pos=(-3.05,0,1.33e-14) rot=(0,1,0;1.5708rad)
  shape: bbox 2.424 x 2.424 x 2.424 mm, 1 faces (baked)
FEATURE [Part::Feature] Part__Feature229  label="6153K690_625-2RS SST BALL BEARING, SEALED v2 (1)092"
  Placement = pos=(-3.05,0,1.33e-14) rot=(0,1,0;1.5708rad)
  shape: bbox 2.424 x 2.424 x 2.424 mm, 1 faces (baked)
FEATURE [Part::Feature] Part__Feature230  label="6153K690_625-2RS SST BALL BEARING, SEALED v2 (1)093"
  Placement = pos=(-3.05,0,1.33e-14) rot=(0,1,0;1.5708rad)
  shape: bbox 2.424 x 2.424 x 2.424 mm, 1 faces (baked)
FEATURE [Part::Feature] Part__Feature231  label="6153K690_625-2RS SST BALL BEARING, SEALED v2 (1)094"
  Placement = pos=(-3.05,0,1.33e-14) rot=(0,1,0;1.5708rad)
  shape: bbox 2.424 x 2.424 x 2.424 mm, 1 faces (baked)
FEATURE [Part::Feature] Part__Feature232  label="6153K690_625-2RS SST BALL BEARING, SEALED v2 (1)095"
  Placement = pos=(-3.05,0,1.33e-14) rot=(0,1,0;1.5708rad)
  shape: bbox 2.424 x 2.424 x 2.424 mm, 1 faces (baked)
FEATURE [Part::Feature] Part__Feature233  label="6153K690_625-2RS SST BALL BEARING, SEALED v2 (1)096"
  Placement = pos=(-3.05,0,1.33e-14) rot=(0,1,0;1.5708rad)
  shape: bbox 2.424 x 2.424 x 2.424 mm, 1 faces (baked)
FEATURE [Part::Feature] Part__Feature234  label="6153K690_625-2RS SST BALL BEARING, SEALED v2 (1)097"
  Placement = pos=(-3.05,0,1.33e-14) rot=(0,1,0;1.5708rad)
  shape: bbox 2.424 x 2.424 x 2.424 mm, 1 faces (baked)
FEATURE [Part::Feature] Part__Feature235  label="6153K690_625-2RS SST BALL BEARING, SEALED v2 (1)098"
  Placement = pos=(-3.05,0,1.33e-14) rot=(0,1,0;1.5708rad)
  shape: bbox 2.424 x 2.424 x 2.424 mm, 1 faces (baked)
FEATURE [Part::Feature] Part__Feature236  label="6153K690_625-2RS SST BALL BEARING, SEALED v2 (1)099"
  Placement = pos=(-3.05,0,1.33e-14) rot=(0,1,0;1.5708rad)
  shape: bbox 1.163 x 11.47 x 11.47 mm, 4 faces (baked)
FEATURE [Part::Feature] Part__Feature237  label="6153K690_625-2RS SST BALL BEARING, SEALED v2 (1)100"
  Placement = pos=(-3.05,0,1.33e-14) rot=(0,1,0;1.5708rad)
  shape: bbox 1.163 x 11.47 x 11.47 mm, 4 faces (baked)
FEATURE [Part::Feature] Part__Feature238  label="Wheel, V-slot Rail for 625 Bearing005"
  shape: bbox 10.2 x 24 x 24 mm, 10 faces (baked)
FEATURE [Part::Feature] Part__Feature239  label="91166A240 WSR, FLAT, M5, STL/Z v006"
  Placement = pos=(-0.55,0,0) rot=(0.707107,0,0.707107;3.14159rad)
  shape: bbox 1.1 x 10 x 10 mm, 4 faces (baked)
FEATURE [App::Part] _153K690_625_2RS_SST_BALL_BEARING__SEALED_v007  label="6153K690_625-2RS SST BALL BEARING, SEALED v103"
  Group = -> [Part__Feature206,Part__Feature207,Part__Feature208,Part__Feature209,Part__Feature210,Part__Feature211,Part__Feature212,Part__Feature213,Part__Feature214,Part__Feature215,Part__Feature216,Part__Feature217,Part__Feature218,Part__Feature219,Part__Feature220,Part__Feature221]
  Origin = -> Origin041
FEATURE [App::Part] _153K690_625_2RS_SST_BALL_BEARING__SEALED_v2__1_005  label="6153K690_625-2RS SST BALL BEARING, SEALED v2 (1)101"
  Group = -> [Part__Feature222,Part__Feature223,Part__Feature224,Part__Feature225,Part__Feature226,Part__Feature227,Part__Feature228,Part__Feature229,Part__Feature230,Part__Feature231,Part__Feature232,Part__Feature233,Part__Feature234,Part__Feature235,Part__Feature236,Part__Feature237]
  Origin = -> Origin042
FEATURE [App::Part] Wheel__V_slot_Rail_625_2Z_Bearing_v009  label="EWheel_TR"
  Group = -> [_153K690_625_2RS_SST_BALL_BEARING__SEALED_v007,_153K690_625_2RS_SST_BALL_BEARING__SEALED_v2__1_005,Part__Feature238,Part__Feature239]
  Origin = -> Origin043
  Placement = pos=(20,150,220.5) rot=(0,0,-1;1.5708rad)
FEATURE [Part::Feature] Part__Feature240  label="6153K690_625-2RS SST BALL BEARING, SEALED v104"
  Placement = pos=(3.05,0,1.33e-14) rot=(0,1,0;1.5708rad)
  shape: bbox 5 x 16 x 16 mm, 8 faces (baked)
FEATURE [Part::Feature] Part__Feature241  label="6153K690_625-2RS SST BALL BEARING, SEALED v105"
  Placement = pos=(3.05,0,1.33e-14) rot=(0,1,0;1.5708rad)
  shape: bbox 5 x 11.37 x 11.37 mm, 8 faces (baked)
FEATURE [Part::Feature] Part__Feature242  label="6153K690_625-2RS SST BALL BEARING, SEALED v106"
  Placement = pos=(3.05,0,1.33e-14) rot=(0,1,0;1.5708rad)
  shape: bbox 2.424 x 2.424 x 2.424 mm, 1 faces (baked)
FEATURE [Part::Feature] Part__Feature243  label="6153K690_625-2RS SST BALL BEARING, SEALED v107"
  Placement = pos=(3.05,0,1.33e-14) rot=(0,1,0;1.5708rad)
  shape: bbox 2.424 x 2.424 x 2.424 mm, 1 faces (baked)
FEATURE [Part::Feature] Part__Feature244  label="6153K690_625-2RS SST BALL BEARING, SEALED v108"
  Placement = pos=(3.05,0,1.33e-14) rot=(0,1,0;1.5708rad)
  shape: bbox 2.424 x 2.424 x 2.424 mm, 1 faces (baked)
FEATURE [Part::Feature] Part__Feature245  label="6153K690_625-2RS SST BALL BEARING, SEALED v109"
  Placement = pos=(3.05,0,1.33e-14) rot=(0,1,0;1.5708rad)
  shape: bbox 2.424 x 2.424 x 2.424 mm, 1 faces (baked)
FEATURE [Part::Feature] Part__Feature246  label="6153K690_625-2RS SST BALL BEARING, SEALED v110"
  Placement = pos=(3.05,0,1.33e-14) rot=(0,1,0;1.5708rad)
  shape: bbox 2.424 x 2.424 x 2.424 mm, 1 faces (baked)
FEATURE [Part::Feature] Part__Feature247  label="6153K690_625-2RS SST BALL BEARING, SEALED v111"
  Placement = pos=(3.05,0,1.33e-14) rot=(0,1,0;1.5708rad)
  shape: bbox 2.424 x 2.424 x 2.424 mm, 1 faces (baked)
FEATURE [Part::Feature] Part__Feature248  label="6153K690_625-2RS SST BALL BEARING, SEALED v112"
  Placement = pos=(3.05,0,1.33e-14) rot=(0,1,0;1.5708rad)
  shape: bbox 2.424 x 2.424 x 2.424 mm, 1 faces (baked)
FEATURE [Part::Feature] Part__Feature249  label="6153K690_625-2RS SST BALL BEARING, SEALED v113"
  Placement = pos=(3.05,0,1.33e-14) rot=(0,1,0;1.5708rad)
  shape: bbox 2.424 x 2.424 x 2.424 mm, 1 faces (baked)
FEATURE [Part::Feature] Part__Feature250  label="6153K690_625-2RS SST BALL BEARING, SEALED v114"
  Placement = pos=(3.05,0,1.33e-14) rot=(0,1,0;1.5708rad)
  shape: bbox 2.424 x 2.424 x 2.424 mm, 1 faces (baked)
FEATURE [Part::Feature] Part__Feature251  label="6153K690_625-2RS SST BALL BEARING, SEALED v115"
  Placement = pos=(3.05,0,1.33e-14) rot=(0,1,0;1.5708rad)
  shape: bbox 2.424 x 2.424 x 2.424 mm, 1 faces (baked)
FEATURE [Part::Feature] Part__Feature252  label="6153K690_625-2RS SST BALL BEARING, SEALED v116"
  Placement = pos=(3.05,0,1.33e-14) rot=(0,1,0;1.5708rad)
  shape: bbox 2.424 x 2.424 x 2.424 mm, 1 faces (baked)
FEATURE [Part::Feature] Part__Feature253  label="6153K690_625-2RS SST BALL BEARING, SEALED v117"
  Placement = pos=(3.05,0,1.33e-14) rot=(0,1,0;1.5708rad)
  shape: bbox 2.424 x 2.424 x 2.424 mm, 1 faces (baked)
FEATURE [Part::Feature] Part__Feature254  label="6153K690_625-2RS SST BALL BEARING, SEALED v118"
  Placement = pos=(3.05,0,1.33e-14) rot=(0,1,0;1.5708rad)
  shape: bbox 1.163 x 11.47 x 11.47 mm, 4 faces (baked)
FEATURE [Part::Feature] Part__Feature255  label="6153K690_625-2RS SST BALL BEARING, SEALED v119"
  Placement = pos=(3.05,0,1.33e-14) rot=(0,1,0;1.5708rad)
  shape: bbox 1.163 x 11.47 x 11.47 mm, 4 faces (baked)
FEATURE [Part::Feature] Part__Feature256  label="6153K690_625-2RS SST BALL BEARING, SEALED v2 (1)102"
  Placement = pos=(-3.05,0,1.33e-14) rot=(0,1,0;1.5708rad)
  shape: bbox 5 x 16 x 16 mm, 8 faces (baked)
FEATURE [Part::Feature] Part__Feature257  label="6153K690_625-2RS SST BALL BEARING, SEALED v2 (1)103"
  Placement = pos=(-3.05,0,1.33e-14) rot=(0,1,0;1.5708rad)
  shape: bbox 5 x 11.37 x 11.37 mm, 8 faces (baked)
FEATURE [Part::Feature] Part__Feature258  label="6153K690_625-2RS SST BALL BEARING, SEALED v2 (1)104"
  Placement = pos=(-3.05,0,1.33e-14) rot=(0,1,0;1.5708rad)
  shape: bbox 2.424 x 2.424 x 2.424 mm, 1 faces (baked)
FEATURE [Part::Feature] Part__Feature259  label="6153K690_625-2RS SST BALL BEARING, SEALED v2 (1)105"
  Placement = pos=(-3.05,0,1.33e-14) rot=(0,1,0;1.5708rad)
  shape: bbox 2.424 x 2.424 x 2.424 mm, 1 faces (baked)
FEATURE [Part::Feature] Part__Feature260  label="6153K690_625-2RS SST BALL BEARING, SEALED v2 (1)106"
  Placement = pos=(-3.05,0,1.33e-14) rot=(0,1,0;1.5708rad)
  shape: bbox 2.424 x 2.424 x 2.424 mm, 1 faces (baked)
FEATURE [Part::Feature] Part__Feature261  label="6153K690_625-2RS SST BALL BEARING, SEALED v2 (1)107"
  Placement = pos=(-3.05,0,1.33e-14) rot=(0,1,0;1.5708rad)
  shape: bbox 2.424 x 2.424 x 2.424 mm, 1 faces (baked)
FEATURE [Part::Feature] Part__Feature262  label="6153K690_625-2RS SST BALL BEARING, SEALED v2 (1)108"
  Placement = pos=(-3.05,0,1.33e-14) rot=(0,1,0;1.5708rad)
  shape: bbox 2.424 x 2.424 x 2.424 mm, 1 faces (baked)
FEATURE [Part::Feature] Part__Feature263  label="6153K690_625-2RS SST BALL BEARING, SEALED v2 (1)109"
  Placement = pos=(-3.05,0,1.33e-14) rot=(0,1,0;1.5708rad)
  shape: bbox 2.424 x 2.424 x 2.424 mm, 1 faces (baked)
FEATURE [Part::Feature] Part__Feature264  label="6153K690_625-2RS SST BALL BEARING, SEALED v2 (1)110"
  Placement = pos=(-3.05,0,1.33e-14) rot=(0,1,0;1.5708rad)
  shape: bbox 2.424 x 2.424 x 2.424 mm, 1 faces (baked)
FEATURE [Part::Feature] Part__Feature265  label="6153K690_625-2RS SST BALL BEARING, SEALED v2 (1)111"
  Placement = pos=(-3.05,0,1.33e-14) rot=(0,1,0;1.5708rad)
  shape: bbox 2.424 x 2.424 x 2.424 mm, 1 faces (baked)
FEATURE [Part::Feature] Part__Feature266  label="6153K690_625-2RS SST BALL BEARING, SEALED v2 (1)112"
  Placement = pos=(-3.05,0,1.33e-14) rot=(0,1,0;1.5708rad)
  shape: bbox 2.424 x 2.424 x 2.424 mm, 1 faces (baked)
FEATURE [Part::Feature] Part__Feature267  label="6153K690_625-2RS SST BALL BEARING, SEALED v2 (1)113"
  Placement = pos=(-3.05,0,1.33e-14) rot=(0,1,0;1.5708rad)
  shape: bbox 2.424 x 2.424 x 2.424 mm, 1 faces (baked)
FEATURE [Part::Feature] Part__Feature268  label="6153K690_625-2RS SST BALL BEARING, SEALED v2 (1)114"
  Placement = pos=(-3.05,0,1.33e-14) rot=(0,1,0;1.5708rad)
  shape: bbox 2.424 x 2.424 x 2.424 mm, 1 faces (baked)
FEATURE [Part::Feature] Part__Feature269  label="6153K690_625-2RS SST BALL BEARING, SEALED v2 (1)115"
  Placement = pos=(-3.05,0,1.33e-14) rot=(0,1,0;1.5708rad)
  shape: bbox 2.424 x 2.424 x 2.424 mm, 1 faces (baked)
FEATURE [Part::Feature] Part__Feature270  label="6153K690_625-2RS SST BALL BEARING, SEALED v2 (1)116"
  Placement = pos=(-3.05,0,1.33e-14) rot=(0,1,0;1.5708rad)
  shape: bbox 1.163 x 11.47 x 11.47 mm, 4 faces (baked)
FEATURE [Part::Feature] Part__Feature271  label="6153K690_625-2RS SST BALL BEARING, SEALED v2 (1)117"
  Placement = pos=(-3.05,0,1.33e-14) rot=(0,1,0;1.5708rad)
  shape: bbox 1.163 x 11.47 x 11.47 mm, 4 faces (baked)
FEATURE [Part::Feature] Part__Feature272  label="Wheel, V-slot Rail for 625 Bearing006"
  shape: bbox 10.2 x 24 x 24 mm, 10 faces (baked)
FEATURE [Part::Feature] Part__Feature273  label="91166A240 WSR, FLAT, M5, STL/Z v007"
  Placement = pos=(-0.55,0,0) rot=(0.707107,0,0.707107;3.14159rad)
  shape: bbox 1.1 x 10 x 10 mm, 4 faces (baked)
FEATURE [App::Part] _153K690_625_2RS_SST_BALL_BEARING__SEALED_v008  label="6153K690_625-2RS SST BALL BEARING, SEALED v120"
  Group = -> [Part__Feature240,Part__Feature241,Part__Feature242,Part__Feature243,Part__Feature244,Part__Feature245,Part__Feature246,Part__Feature247,Part__Feature248,Part__Feature249,Part__Feature250,Part__Feature251,Part__Feature252,Part__Feature253,Part__Feature254,Part__Feature255]
  Origin = -> Origin044
FEATURE [App::Part] _153K690_625_2RS_SST_BALL_BEARING__SEALED_v2__1_006  label="6153K690_625-2RS SST BALL BEARING, SEALED v2 (1)118"
  Group = -> [Part__Feature256,Part__Feature257,Part__Feature258,Part__Feature259,Part__Feature260,Part__Feature261,Part__Feature262,Part__Feature263,Part__Feature264,Part__Feature265,Part__Feature266,Part__Feature267,Part__Feature268,Part__Feature269,Part__Feature270,Part__Feature271]
  Origin = -> Origin045
FEATURE [App::Part] Wheel__V_slot_Rail_625_2Z_Bearing_v010  label="EWheel_BR"
  Group = -> [_153K690_625_2RS_SST_BALL_BEARING__SEALED_v008,_153K690_625_2RS_SST_BALL_BEARING__SEALED_v2__1_006,Part__Feature272,Part__Feature273]
  Origin = -> Origin046
  Placement = pos=(20,150,179.5) rot=(0,0,-1;1.5708rad)
FEATURE [Part::Feature] Part__Feature274  label="6153K690_625-2RS SST BALL BEARING, SEALED v121"
  Placement = pos=(3.05,0,1.33e-14) rot=(0,1,0;1.5708rad)
  shape: bbox 5 x 16 x 16 mm, 8 faces (baked)
FEATURE [Part::Feature] Part__Feature275  label="6153K690_625-2RS SST BALL BEARING, SEALED v122"
  Placement = pos=(3.05,0,1.33e-14) rot=(0,1,0;1.5708rad)
  shape: bbox 5 x 11.37 x 11.37 mm, 8 faces (baked)
FEATURE [Part::Feature] Part__Feature276  label="6153K690_625-2RS SST BALL BEARING, SEALED v123"
  Placement = pos=(3.05,0,1.33e-14) rot=(0,1,0;1.5708rad)
  shape: bbox 2.424 x 2.424 x 2.424 mm, 1 faces (baked)
FEATURE [Part::Feature] Part__Feature277  label="6153K690_625-2RS SST BALL BEARING, SEALED v124"
  Placement = pos=(3.05,0,1.33e-14) rot=(0,1,0;1.5708rad)
  shape: bbox 2.424 x 2.424 x 2.424 mm, 1 faces (baked)
FEATURE [Part::Feature] Part__Feature278  label="6153K690_625-2RS SST BALL BEARING, SEALED v125"
  Placement = pos=(3.05,0,1.33e-14) rot=(0,1,0;1.5708rad)
  shape: bbox 2.424 x 2.424 x 2.424 mm, 1 faces (baked)
FEATURE [Part::Feature] Part__Feature279  label="6153K690_625-2RS SST BALL BEARING, SEALED v126"
  Placement = pos=(3.05,0,1.33e-14) rot=(0,1,0;1.5708rad)
  shape: bbox 2.424 x 2.424 x 2.424 mm, 1 faces (baked)
FEATURE [Part::Feature] Part__Feature280  label="6153K690_625-2RS SST BALL BEARING, SEALED v127"
  Placement = pos=(3.05,0,1.33e-14) rot=(0,1,0;1.5708rad)
  shape: bbox 2.424 x 2.424 x 2.424 mm, 1 faces (baked)
FEATURE [Part::Feature] Part__Feature281  label="6153K690_625-2RS SST BALL BEARING, SEALED v128"
  Placement = pos=(3.05,0,1.33e-14) rot=(0,1,0;1.5708rad)
  shape: bbox 2.424 x 2.424 x 2.424 mm, 1 faces (baked)
FEATURE [Part::Feature] Part__Feature282  label="6153K690_625-2RS SST BALL BEARING, SEALED v129"
  Placement = pos=(3.05,0,1.33e-14) rot=(0,1,0;1.5708rad)
  shape: bbox 2.424 x 2.424 x 2.424 mm, 1 faces (baked)
FEATURE [Part::Feature] Part__Feature283  label="6153K690_625-2RS SST BALL BEARING, SEALED v130"
  Placement = pos=(3.05,0,1.33e-14) rot=(0,1,0;1.5708rad)
  shape: bbox 2.424 x 2.424 x 2.424 mm, 1 faces (baked)
FEATURE [Part::Feature] Part__Feature284  label="6153K690_625-2RS SST BALL BEARING, SEALED v131"
  Placement = pos=(3.05,0,1.33e-14) rot=(0,1,0;1.5708rad)
  shape: bbox 2.424 x 2.424 x 2.424 mm, 1 faces (baked)
FEATURE [Part::Feature] Part__Feature285  label="6153K690_625-2RS SST BALL BEARING, SEALED v132"
  Placement = pos=(3.05,0,1.33e-14) rot=(0,1,0;1.5708rad)
  shape: bbox 2.424 x 2.424 x 2.424 mm, 1 faces (baked)
FEATURE [Part::Feature] Part__Feature286  label="6153K690_625-2RS SST BALL BEARING, SEALED v133"
  Placement = pos=(3.05,0,1.33e-14) rot=(0,1,0;1.5708rad)
  shape: bbox 2.424 x 2.424 x 2.424 mm, 1 faces (baked)
FEATURE [Part::Feature] Part__Feature287  label="6153K690_625-2RS SST BALL BEARING, SEALED v134"
  Placement = pos=(3.05,0,1.33e-14) rot=(0,1,0;1.5708rad)
  shape: bbox 2.424 x 2.424 x 2.424 mm, 1 faces (baked)
FEATURE [Part::Feature] Part__Feature288  label="6153K690_625-2RS SST BALL BEARING, SEALED v135"
  Placement = pos=(3.05,0,1.33e-14) rot=(0,1,0;1.5708rad)
  shape: bbox 1.163 x 11.47 x 11.47 mm, 4 faces (baked)
FEATURE [Part::Feature] Part__Feature289  label="6153K690_625-2RS SST BALL BEARING, SEALED v136"
  Placement = pos=(3.05,0,1.33e-14) rot=(0,1,0;1.5708rad)
  shape: bbox 1.163 x 11.47 x 11.47 mm, 4 faces (baked)
FEATURE [Part::Feature] Part__Feature290  label="6153K690_625-2RS SST BALL BEARING, SEALED v2 (1)119"
  Placement = pos=(-3.05,0,1.33e-14) rot=(0,1,0;1.5708rad)
  shape: bbox 5 x 16 x 16 mm, 8 faces (baked)
FEATURE [Part::Feature] Part__Feature291  label="6153K690_625-2RS SST BALL BEARING, SEALED v2 (1)120"
  Placement = pos=(-3.05,0,1.33e-14) rot=(0,1,0;1.5708rad)
  shape: bbox 5 x 11.37 x 11.37 mm, 8 faces (baked)
FEATURE [Part::Feature] Part__Feature292  label="6153K690_625-2RS SST BALL BEARING, SEALED v2 (1)121"
  Placement = pos=(-3.05,0,1.33e-14) rot=(0,1,0;1.5708rad)
  shape: bbox 2.424 x 2.424 x 2.424 mm, 1 faces (baked)
FEATURE [Part::Feature] Part__Feature293  label="6153K690_625-2RS SST BALL BEARING, SEALED v2 (1)122"
  Placement = pos=(-3.05,0,1.33e-14) rot=(0,1,0;1.5708rad)
  shape: bbox 2.424 x 2.424 x 2.424 mm, 1 faces (baked)
FEATURE [Part::Feature] Part__Feature294  label="6153K690_625-2RS SST BALL BEARING, SEALED v2 (1)123"
  Placement = pos=(-3.05,0,1.33e-14) rot=(0,1,0;1.5708rad)
  shape: bbox 2.424 x 2.424 x 2.424 mm, 1 faces (baked)
FEATURE [Part::Feature] Part__Feature295  label="6153K690_625-2RS SST BALL BEARING, SEALED v2 (1)124"
  Placement = pos=(-3.05,0,1.33e-14) rot=(0,1,0;1.5708rad)
  shape: bbox 2.424 x 2.424 x 2.424 mm, 1 faces (baked)
FEATURE [Part::Feature] Part__Feature296  label="6153K690_625-2RS SST BALL BEARING, SEALED v2 (1)125"
  Placement = pos=(-3.05,0,1.33e-14) rot=(0,1,0;1.5708rad)
  shape: bbox 2.424 x 2.424 x 2.424 mm, 1 faces (baked)
FEATURE [Part::Feature] Part__Feature297  label="6153K690_625-2RS SST BALL BEARING, SEALED v2 (1)126"
  Placement = pos=(-3.05,0,1.33e-14) rot=(0,1,0;1.5708rad)
  shape: bbox 2.424 x 2.424 x 2.424 mm, 1 faces (baked)
FEATURE [Part::Feature] Part__Feature298  label="6153K690_625-2RS SST BALL BEARING, SEALED v2 (1)127"
  Placement = pos=(-3.05,0,1.33e-14) rot=(0,1,0;1.5708rad)
  shape: bbox 2.424 x 2.424 x 2.424 mm, 1 faces (baked)
FEATURE [Part::Feature] Part__Feature299  label="6153K690_625-2RS SST BALL BEARING, SEALED v2 (1)128"
  Placement = pos=(-3.05,0,1.33e-14) rot=(0,1,0;1.5708rad)
  shape: bbox 2.424 x 2.424 x 2.424 mm, 1 faces (baked)
FEATURE [Part::Feature] Part__Feature300  label="6153K690_625-2RS SST BALL BEARING, SEALED v2 (1)129"
  Placement = pos=(-3.05,0,1.33e-14) rot=(0,1,0;1.5708rad)
  shape: bbox 2.424 x 2.424 x 2.424 mm, 1 faces (baked)
FEATURE [Part::Feature] Part__Feature301  label="6153K690_625-2RS SST BALL BEARING, SEALED v2 (1)130"
  Placement = pos=(-3.05,0,1.33e-14) rot=(0,1,0;1.5708rad)
  shape: bbox 2.424 x 2.424 x 2.424 mm, 1 faces (baked)
FEATURE [Part::Feature] Part__Feature302  label="6153K690_625-2RS SST BALL BEARING, SEALED v2 (1)131"
  Placement = pos=(-3.05,0,1.33e-14) rot=(0,1,0;1.5708rad)
  shape: bbox 2.424 x 2.424 x 2.424 mm, 1 faces (baked)
FEATURE [Part::Feature] Part__Feature303  label="6153K690_625-2RS SST BALL BEARING, SEALED v2 (1)132"
  Placement = pos=(-3.05,0,1.33e-14) rot=(0,1,0;1.5708rad)
  shape: bbox 2.424 x 2.424 x 2.424 mm, 1 faces (baked)
FEATURE [Part::Feature] Part__Feature304  label="6153K690_625-2RS SST BALL BEARING, SEALED v2 (1)133"
  Placement = pos=(-3.05,0,1.33e-14) rot=(0,1,0;1.5708rad)
  shape: bbox 1.163 x 11.47 x 11.47 mm, 4 faces (baked)
FEATURE [Part::Feature] Part__Feature305  label="6153K690_625-2RS SST BALL BEARING, SEALED v2 (1)134"
  Placement = pos=(-3.05,0,1.33e-14) rot=(0,1,0;1.5708rad)
  shape: bbox 1.163 x 11.47 x 11.47 mm, 4 faces (baked)
FEATURE [Part::Feature] Part__Feature306  label="Wheel, V-slot Rail for 625 Bearing007"
  shape: bbox 10.2 x 24 x 24 mm, 10 faces (baked)
FEATURE [Part::Feature] Part__Feature307  label="91166A240 WSR, FLAT, M5, STL/Z v008"
  Placement = pos=(-0.55,0,0) rot=(0.707107,0,0.707107;3.14159rad)
  shape: bbox 1.1 x 10 x 10 mm, 4 faces (baked)
FEATURE [App::Part] _153K690_625_2RS_SST_BALL_BEARING__SEALED_v009  label="6153K690_625-2RS SST BALL BEARING, SEALED v137"
  Group = -> [Part__Feature274,Part__Feature275,Part__Feature276,Part__Feature277,Part__Feature278,Part__Feature279,Part__Feature280,Part__Feature281,Part__Feature282,Part__Feature283,Part__Feature284,Part__Feature285,Part__Feature286,Part__Feature287,Part__Feature288,Part__Feature289]
  Origin = -> Origin047
FEATURE [App::Part] _153K690_625_2RS_SST_BALL_BEARING__SEALED_v2__1_007  label="6153K690_625-2RS SST BALL BEARING, SEALED v2 (1)135"
  Group = -> [Part__Feature290,Part__Feature291,Part__Feature292,Part__Feature293,Part__Feature294,Part__Feature295,Part__Feature296,Part__Feature297,Part__Feature298,Part__Feature299,Part__Feature300,Part__Feature301,Part__Feature302,Part__Feature303,Part__Feature304,Part__Feature305]
  Origin = -> Origin048
FEATURE [App::Part] Wheel__V_slot_Rail_625_2Z_Bearing_v011  label="EWheel_BL"
  Group = -> [_153K690_625_2RS_SST_BALL_BEARING__SEALED_v009,_153K690_625_2RS_SST_BALL_BEARING__SEALED_v2__1_007,Part__Feature306,Part__Feature307]
  Origin = -> Origin049
  Placement = pos=(-20,150,179.5) rot=(0,0,-1;1.5708rad)
FEATURE [Sketcher::SketchObject] Sketch078
  ArcFitTolerance = 1e-06
  AttacherType = Attacher::AttachEngine3D
  FullyConstrained = true
  MakeInternals = false
  Placement = pos=(0,153,9.29e-14) rot=(-1,0,0;1.5708rad)
  sketch-geometry (4):
    g0: LineSegment StartX=-40 StartY=-185 StartZ=0 EndX=-40 EndY=-165 EndZ=0
    g1: ArcOfCircle CenterX=-47.5 CenterY=-185 CenterZ=0 NormalX=0 NormalY=0 NormalZ=1 AngleXU=0 Radius=7.5 StartAngle=4.71239 EndAngle=6.28319
    g2: LineSegment [constr] StartX=-47.5 StartY=-185 StartZ=0 EndX=-47.5 EndY=-192.5 EndZ=0
    g3: LineSegment [constr] StartX=-47.5 StartY=-185 StartZ=0 EndX=-40 EndY=-185 EndZ=0
  constraints (12):
    c: Vertical(g0)
    c: DistanceX(g0,g-1) = 40
    c: DistanceY(g0,g-1) = 165
    c: DistanceY(g0,g0) = 20
    c: Coincident(g1,g0)
    c: Coincident(g2,g1)
    c: Coincident(g2,g1)
    c: Vertical(g2)
    c: Coincident(g3,g1)
    c: Coincident(g3,g0)
    c: Horizontal(g3)
    c: DistanceY(g2,g2) = 7.5
FEATURE [Sketcher::SketchObject] Sketch079
  ArcFitTolerance = 1e-06
  AttachmentSupport = -> [XZ_Plane050]
  FullyConstrained = true
  MakeInternals = false
  MapMode = 5
  Placement = pos=(0,0,0) rot=(1,0,0;1.5708rad)
  sketch-geometry (17):
    g0: LineSegment StartX=-0.727916 StartY=0.059 StartZ=0 EndX=-1.125 EndY=0.059 EndZ=0
    g1: LineSegment StartX=-1.125 StartY=0.059 StartZ=0 EndX=-1.125 EndY=-0.571 EndZ=0
    g2: LineSegment StartX=-1.125 StartY=-0.571 StartZ=0 EndX=1.125 EndY=-0.571 EndZ=0
    g3: LineSegment StartX=1.125 StartY=-0.571 StartZ=0 EndX=1.125 EndY=0.059 EndZ=0
    g4: LineSegment StartX=1.125 StartY=0.059 StartZ=0 EndX=0.727916 EndY=0.059 EndZ=0
    g5: ArcOfCircle CenterX=-0.727916 CenterY=0.209 CenterZ=0 NormalX=0 NormalY=0 NormalZ=1 AngleXU=0 Radius=0.15 StartAngle=4.71239 EndAngle=6.28319
    g6: GeomPoint X=0.4 Y=0 Z=0
    g7: ArcOfCircle CenterX=0.4 CenterY=0 CenterZ=0 NormalX=0 NormalY=0 NormalZ=1 AngleXU=0 Radius=1 StartAngle=2.83303 EndAngle=2.93104
    g8: ArcOfCircle CenterX=0 CenterY=0.254 CenterZ=0 NormalX=0 NormalY=0 NormalZ=1 AngleXU=0 Radius=0.555 StartAngle=1.04187 EndAngle=3.05194
    g9: LineSegment [constr] StartX=-0.577916 StartY=0.209 StartZ=0 EndX=-0.727916 EndY=0.209 EndZ=0
    g10: GeomPoint X=-0.4 Y=0 Z=0
    g11: ArcOfCircle CenterX=-0.4 CenterY=0 CenterZ=0 NormalX=0 NormalY=0 NormalZ=1 AngleXU=0 Radius=1 StartAngle=0.210552 EndAngle=0.822954
    g12: ArcOfCircle CenterX=0.727916 CenterY=0.209 CenterZ=0 NormalX=0 NormalY=0 NormalZ=1 AngleXU=0 Radius=0.15 StartAngle=3.14159 EndAngle=4.71239
    g13: LineSegment [constr] StartX=0.727916 StartY=0.209 StartZ=0 EndX=0.577916 EndY=0.209 EndZ=0
    g14: LineSegment [constr] StartX=-0.727916 StartY=0.059 StartZ=0 EndX=-0.727916 EndY=0.209 EndZ=0
    g15: LineSegment [constr] StartX=0.727916 StartY=0.059 StartZ=0 EndX=0.727916 EndY=0.209 EndZ=0
    g16: GeomPoint [constr] X=0 Y=0.809 Z=0
  constraints (47):
    c: Horizontal(g0)
    c: Coincident(g1,g0)
    c: Coincident(g2,g1)
    c: Horizontal(g2)
    c: Coincident(g3,g2)
    c: Vertical(g3)
    c: Coincident(g4,g3)
    c: Horizontal(g4)
    c: Vertical(g1)
    c: DistanceX(g2,g2) = 2.25
    c: Equal(g0,g4)
    c: Coincident(g5,g0)
    c: Radius(g5) = 0.15
    c: PointOnObject(g6,g-1)
    c: DistanceX(g-1,g6) = 0.4
    c: Coincident(g7,g6)
    c: Coincident(g7,g5)
    c: Radius(g7) = 1
    c: PointOnObject(g8,g-2)
    c: Coincident(g8,g7)
    c: Radius(g8) = 0.555
    c: Coincident(g9,g5)
    c: Coincident(g9,g5)
    c: Horizontal(g9)
    c: PointOnObject(g10,g-1)
    c: DistanceX(g10,g-1) = 0.4
    c: Coincident(g11,g10)
    c: Coincident(g11,g8)
    c: Radius(g11) = 1
    c: Coincident(g12,g4)
    c: Coincident(g12,g11)
    c: Radius(g12) = 0.15
    c: Coincident(g13,g12)
    c: Coincident(g13,g11)
    c: Horizontal(g13)
    c: Equal(g3,g1)
    c: Coincident(g14,g0)
    c: Coincident(g14,g5)
    c: Vertical(g14)
    c: Coincident(g15,g4)
    c: Coincident(g15,g12)
    c: Vertical(g15)
    c: PointOnObject(g16,g8)
    c: PointOnObject(g16,g-2)
    c: DistanceY(g4,g16) = 0.75
    c: DistanceY(g2,g16) = 1.38
    c: DistanceY(g-1,g8) = 0.254
FEATURE [PartDesign::Pad] Pad024
  Direction = (0,-1,2e-16)
  Length = 6
  Length2 = 10
  Placement = pos=(0,0,0) rot=(1,0,0;1.5708rad)
  Profile = -> Sketch079
  ReferenceAxis = -> Sketch079 [N_Axis]
  Suppressed = false
  Type = 0
FEATURE [PartDesign::Body] Body010  label="BeltArrayObject"
  AllowCompound = false
  Group = -> [Sketch079,Pad024]
  Origin = -> Origin050
  Tip = -> Pad024
FEATURE [Part::FeaturePython] PathArray001  # WARN: FeaturePython — macro-defined, semantics opaque (R4)
  Align = true
  AlignMode = 0
  Base = -> Body010
  Count = 17
  EndOffset = 0
  ExtraTranslation = (0,0,0)
  ForceVertical = false
  Fuse = true
  PathObject = -> Sketch078
  StartOffset = 0
  TangentVector = (1,0,0)
  VerticalVector = (0,0,1)
FEATURE [Part::Mirroring] Part__Mirroring  label="PathArray001 (Mirror #1)"
  Base = (3.05176e-05,149,183.698)
  Normal = (1,0,-1.19209e-07)
  Source = -> PathArray001
FEATURE [Part::Extrusion] Extrude005  label="BaseLeftExtrusion"
  Base = -> Sketch001
  Dir = (0,0,1)
  DirMode = 2
  FaceMakerClass = Part::FaceMakerBullseye
  FaceMakerMode = 3
  LengthFwd = 410
  LengthRev = 0
  Placement = pos=(-180,-135,3.89e-14) rot=(-0.58,-0.58,0.58;4.18879rad)
  Reversed = true
  Solid = true
  Symmetric = false
FEATURE [Sketcher::SketchObject] Sketch080
  ArcFitTolerance = 1e-06
  AttacherType = Attacher::AttachEngine3D
  FullyConstrained = true
  MakeInternals = false
  MapMode = 5
  Placement = pos=(0,152,9.29e-14) rot=(-1,0,0;1.5708rad)
FEATURE [Part::MultiFuse] Fusion001
  Shapes = -> [Part__Mirroring,PathArray001]
FEATURE [Sketcher::SketchObject] Sketch082
  ArcFitTolerance = 1e-06
  AttachmentSupport = -> [Hole013]
  FullyConstrained = true
  MakeInternals = false
  MapMode = 5
  Placement = pos=(0,136,-5.58e-14) rot=(-1,0,0;1.5708rad)
  sketch-geometry (9):
    g0: LineSegment StartX=-45 StartY=-165 StartZ=0 EndX=-45 EndY=-189 EndZ=0
    g1: LineSegment StartX=-45 StartY=-189 StartZ=0 EndX=-35 EndY=-189 EndZ=0
    g2: LineSegment StartX=-35 StartY=-189 StartZ=0 EndX=-35 EndY=-165 EndZ=0
    g3: LineSegment StartX=-35 StartY=-165 StartZ=0 EndX=-45 EndY=-165 EndZ=0
    g4: LineSegment StartX=45 StartY=-165 StartZ=0 EndX=45 EndY=-189 EndZ=0
    g5: LineSegment StartX=45 StartY=-189 StartZ=0 EndX=35 EndY=-189 EndZ=0
    g6: LineSegment StartX=35 StartY=-189 StartZ=0 EndX=35 EndY=-165 EndZ=0
    g7: LineSegment StartX=35 StartY=-165 StartZ=0 EndX=45 EndY=-165 EndZ=0
    g8: LineSegment [constr] StartX=-10 StartY=-200 StartZ=0 EndX=10 EndY=-200 EndZ=0
  constraints (23):
    c: Coincident(g0,g1)
    c: Coincident(g1,g2)
    c: Coincident(g2,g3)
    c: Coincident(g3,g0)
    c: Vertical(g0)
    c: Vertical(g2)
    c: Horizontal(g1)
    c: Horizontal(g3)
    c: Distance(g0,g2) = 10
    c: Distance(g1,g3) = 24
    c: DistanceX(g2,g-1) = 35
    c: DistanceY(g2,g-1) = 165
    c: Symmetric(g0,g4,g-2)
    c: Symmetric(g0,g4,g-2)
    c: Symmetric(g1,g5,g-2)
    c: Symmetric(g1,g5,g-2)
    c: Symmetric(g2,g6,g-2)
    c: Symmetric(g2,g6,g-2)
    c: Symmetric(g3,g7,g-2)
    c: Symmetric(g3,g7,g-2)
    c: DistanceY(g8,g-1) = 200
    c: DistanceX(g8,g8) = 20
    c: Symmetric(g8,g8,g-2)
FEATURE [PartDesign::Pad] Pad025
  BaseFeature = -> Hole013
  Direction = (0,1,2e-16)
  Length = 17
  Length2 = 10
  Placement = pos=(0,0,0) rot=(1,0,0;1.5708rad)
  Profile = -> Sketch082
  ReferenceAxis = -> Sketch082 [N_Axis]
  Suppressed = false
  Type = 0
FEATURE [Sketcher::SketchObject] Sketch084
  ArcFitTolerance = 1e-06
  AttachmentSupport = -> [Pad025]
  FullyConstrained = true
  MakeInternals = false
  MapMode = 5
  Placement = pos=(45,0,0) rot=(0.707107,0,0.707107;3.14159rad)
  sketch-geometry (6):
    g0: Circle CenterX=180.875 CenterY=-150 CenterZ=0 NormalX=0 NormalY=0 NormalZ=1 AngleXU=0 Radius=2.5
    g1: LineSegment [constr] StartX=172 StartY=-136 StartZ=0 EndX=172 EndY=-153 EndZ=0
    g2: LineSegment [constr] StartX=172 StartY=-153 StartZ=0 EndX=189.75 EndY=-153 EndZ=0
    g3: LineSegment [constr] StartX=189.75 StartY=-153 StartZ=0 EndX=189.75 EndY=-136 EndZ=0
    g4: LineSegment [constr] StartX=189.75 StartY=-136 StartZ=0 EndX=172 EndY=-136 EndZ=0
    g5: LineSegment [constr] StartX=189.75 StartY=-147 StartZ=0 EndX=172 EndY=-147 EndZ=0
  constraints (18):
    c: Diameter(g0) = 5
    c: Coincident(g1,g2)
    c: Coincident(g2,g3)
    c: Coincident(g3,g4)
    c: Coincident(g4,g1)
    c: Vertical(g1)
    c: Vertical(g3)
    c: Horizontal(g2)
    c: Horizontal(g4)
    c: DistanceX(g4,g4) = 17.75
    c: DistanceY(g3,g3) = 17
    c: DistanceY(g3,g-1) = 136
    c: DistanceX(g-1,g1) = 172
    c: PointOnObject(g5,g3)
    c: PointOnObject(g5,g1)
    c: Horizontal(g5)
    c: DistanceY(g5,g3) = 11
    c: Symmetric(g5,g2,g0)
FEATURE [PartDesign::Hole] Hole015
  BaseFeature = -> Pad025
  CustomThreadClearance = 0
  Depth = 5
  DepthType = 0
  Diameter = 4.224
  DrillForDepth = false
  DrillPoint = 0
  DrillPointAngle = 118
  HoleCutCountersinkAngle = 90
  HoleCutCustomValues = false
  HoleCutDepth = 0
  HoleCutDiameter = 6.1
  HoleCutType = 0
  ModelThread = true
  Placement = pos=(0,0,0) rot=(1,0,0;1.5708rad)
  Profile = -> Sketch084
  Suppressed = true
  Tapered = false
  TaperedAngle = 90
  ThreadClass = 0
  ThreadDepth = 5
  ThreadDepthType = 0
  ThreadDirection = 0
  ThreadFit = 0
  ThreadSize = 13
  ThreadType = 1
  Threaded = true
  UseCustomThreadClearance = false
FEATURE [Sketcher::SketchObject] Sketch085
  ArcFitTolerance = 1e-06
  AttachmentSupport = -> [Hole015]
  FullyConstrained = true
  MakeInternals = false
  MapMode = 5
  Placement = pos=(-45,0,0) rot=(0.707107,0,-0.707107;3.14159rad)
  sketch-geometry (5):
    g0: LineSegment [constr] StartX=-189.75 StartY=-153 StartZ=0 EndX=-172 EndY=-153 EndZ=0
    g1: LineSegment [constr] StartX=-172 StartY=-153 StartZ=0 EndX=-172 EndY=-147 EndZ=0
    g2: LineSegment [constr] StartX=-172 StartY=-147 StartZ=0 EndX=-189.75 EndY=-147 EndZ=0
    g3: LineSegment [constr] StartX=-189.75 StartY=-147 StartZ=0 EndX=-189.75 EndY=-153 EndZ=0
    g4: Circle CenterX=-180.875 CenterY=-150 CenterZ=0 NormalX=0 NormalY=0 NormalZ=1 AngleXU=0 Radius=2.5
  constraints (14):
    c: Coincident(g0,g1)
    c: Coincident(g1,g2)
    c: Coincident(g2,g3)
    c: Coincident(g3,g0)
    c: Horizontal(g0)
    c: Horizontal(g2)
    c: Vertical(g1)
    c: Vertical(g3)
    c: DistanceY(g3,g3) = 6
    c: DistanceY(g2,g-1) = 147
    c: DistanceX(g1,g-1) = 172
    c: DistanceX(g2,g2) = 17.75
    c: Diameter(g4) = 5
    c: Symmetric(g2,g0,g4)
FEATURE [PartDesign::Hole] Hole016
  BaseFeature = -> Hole015
  CustomThreadClearance = 0
  Depth = 5
  DepthType = 0
  Diameter = 4.224
  DrillForDepth = false
  DrillPoint = 0
  DrillPointAngle = 118
  HoleCutCountersinkAngle = 90
  HoleCutCustomValues = false
  HoleCutDepth = 0
  HoleCutDiameter = 6.1
  HoleCutType = 0
  ModelThread = true
  Placement = pos=(0,0,0) rot=(1,0,0;1.5708rad)
  Profile = -> Sketch085
  Suppressed = true
  Tapered = false
  TaperedAngle = 90
  ThreadClass = 0
  ThreadDepth = 5
  ThreadDepthType = 0
  ThreadDirection = 0
  ThreadFit = 0
  ThreadSize = 13
  ThreadType = 1
  Threaded = true
  UseCustomThreadClearance = false
FEATURE [Part::Extrusion] Extrude006  label="BaseBackExtrusion"
  Base = -> Sketch
  Dir = (0,0,1)
  DirMode = 2
  FaceMakerClass = Part::FaceMakerBullseye
  FaceMakerMode = 3
  LengthFwd = 400
  LengthRev = 0
  Placement = pos=(-190,285,0) rot=(0,1,0;1.5708rad)
  Solid = true
  Symmetric = false
FEATURE [Part::Extrusion] Extrude007  label="BaseFrontExtrusion"
  Base = -> Sketch
  Dir = (0,0,1)
  DirMode = 2
  FaceMakerClass = Part::FaceMakerBullseye
  FaceMakerMode = 3
  LengthFwd = 400
  LengthRev = 0
  Placement = pos=(-190,-145,0) rot=(0,1,0;1.5708rad)
  Solid = true
  Symmetric = false
FEATURE [Part::Extrusion] Extrude008  label="BaseMiddleExtrusion"
  Base = -> Sketch001
  Dir = (0,0,1)
  DirMode = 2
  FaceMakerClass = Part::FaceMakerBullseye
  FaceMakerMode = 3
  LengthFwd = 410
  LengthRev = 0
  Placement = pos=(70,-135,0) rot=(-0.58,-0.58,0.58;4.18879rad)
  Reversed = true
  Solid = true
  Symmetric = false
FEATURE [Sketcher::SketchObject] Sketch088
  ArcFitTolerance = 1e-06
  AttachmentOffset = pos=(0,0,3) rot=(0,0,1;0rad)
  AttachmentSupport = -> [XZ_Plane052]
  FullyConstrained = true
  MakeInternals = false
  MapMode = 5
  Placement = pos=(0,-3,7e-16) rot=(1,0,0;1.5708rad)
  sketch-geometry (4):
    g0: LineSegment StartX=-19 StartY=203 StartZ=0 EndX=-19 EndY=172 EndZ=0
    g1: LineSegment StartX=-19 StartY=172 StartZ=0 EndX=19 EndY=172 EndZ=0
    g2: LineSegment StartX=19 StartY=172 StartZ=0 EndX=19 EndY=203 EndZ=0
    g3: LineSegment StartX=19 StartY=203 StartZ=0 EndX=-19 EndY=203 EndZ=0
  constraints (11):
    c: Coincident(g0,g1)
    c: Coincident(g1,g2)
    c: Coincident(g2,g3)
    c: Coincident(g3,g0)
    c: Vertical(g0)
    c: Vertical(g2)
    c: Horizontal(g1)
    c: Distance(g0,g2) = 38
    c: Distance(g1,g3) = 31
    c: Symmetric(g0,g2,g-2)
    c: DistanceY(g-1,g1) = 172
FEATURE [PartDesign::Pad] Pad029
  Direction = (0,-1,2e-16)
  Length = 30
  Length2 = 10
  Placement = pos=(0,0,0) rot=(1,0,0;1.5708rad)
  Profile = -> Sketch088
  ReferenceAxis = -> Sketch088 [N_Axis]
  Reversed = true
  Suppressed = false
  Type = 0
FEATURE [Part::Extrusion] Extrude009  label="BaseRightExtrusion"
  Base = -> Sketch001
  Dir = (0,0,1)
  DirMode = 2
  FaceMakerClass = Part::FaceMakerBullseye
  FaceMakerMode = 3
  LengthFwd = 450
  LengthRev = 0
  Placement = pos=(220,-155,0) rot=(-0.58,-0.58,0.58;4.18879rad)
  Reversed = true
  Solid = true
  Symmetric = false
FEATURE [App::Part] Part  label="ZAxisAssembly"
  Group = -> [Body,_7HS4401S_Stepper_Motor,Part002,ThreadedRod,Sketch004,Extrude004,Body009,Sketch001,Extrude005,Extrude001,Extrude,Sketch,Extrude006,Extrude007,Extrude008,Extrude009]
  Origin = -> Origin002
  Placement = pos=(0,20,0) rot=(0,0,1;0rad)
FEATURE [Sketcher::SketchObject] Sketch089
  ArcFitTolerance = 1e-06
  FullyConstrained = true
  MakeInternals = false
  Placement = pos=(0,132,-7.09e-14) rot=(1,0,0;1.5708rad)
  sketch-geometry (12):
    g0: Circle CenterX=-17 CenterY=208.5 CenterZ=0 NormalX=0 NormalY=0 NormalZ=1 AngleXU=0 Radius=2.3
    g1: Circle CenterX=17 CenterY=208.5 CenterZ=0 NormalX=0 NormalY=0 NormalZ=1 AngleXU=0 Radius=2.5
    g2: LineSegment [constr] StartX=-17 StartY=208.5 StartZ=0 EndX=17 EndY=208.5 EndZ=0
    g3: Circle CenterX=-22.5 CenterY=199.5 CenterZ=0 NormalX=0 NormalY=0 NormalZ=1 AngleXU=0 Radius=2.3
    g4: Circle CenterX=22.5 CenterY=199.5 CenterZ=0 NormalX=0 NormalY=0 NormalZ=1 AngleXU=0 Radius=2.3
    g5: Circle CenterX=-34 CenterY=210 CenterZ=0 NormalX=0 NormalY=0 NormalZ=1 AngleXU=0 Radius=2.3
    g6: Circle CenterX=-34 CenterY=220 CenterZ=0 NormalX=0 NormalY=0 NormalZ=1 AngleXU=0 Radius=2.3
    g7: LineSegment [constr] StartX=-34 StartY=220 StartZ=0 EndX=-34 EndY=210 EndZ=0
    g8: Circle CenterX=-7.5 CenterY=224.5 CenterZ=0 NormalX=0 NormalY=0 NormalZ=1 AngleXU=0 Radius=2.3
    g9: Circle CenterX=7.5 CenterY=224.5 CenterZ=0 NormalX=0 NormalY=0 NormalZ=1 AngleXU=0 Radius=2.3
    g10: Circle CenterX=30.5 CenterY=209 CenterZ=0 NormalX=0 NormalY=0 NormalZ=1 AngleXU=0 Radius=2.3
    g11: Circle CenterX=40.5 CenterY=199 CenterZ=0 NormalX=0 NormalY=0 NormalZ=1 AngleXU=0 Radius=2.3
  constraints (32):
    c: Diameter(g0) = 4.6
    c: Diameter(g1) = 5
    c: DistanceX(g0,g-1) = 17
    c: DistanceX(g-1,g1) = 17
    c: Coincident(g2,g0)
    c: Coincident(g2,g1)
    c: Horizontal(g2)
    c: DistanceY(g-1,g1) = 208.5
    c: Equal(g0,g3)
    c: DistanceY(g-1,g3) = 199.5
    c: DistanceX(g3,g-1) = 22.5
    c: Equal(g3,g4)
    c: Symmetric(g3,g4,g-2)
    c: Coincident(g7,g6)
    c: Vertical(g7)
    c: Coincident(g7,g5)
    c: DistanceX(g5,g0) = 17
    c: DistanceY(g7,g7) = 10
    c: Equal(g6,g5)
    c: Equal(g5,g3)
    c: DistanceY(g0,g5) = 1.5
    c: DistanceX(g0,g8) = 9.5
    c: DistanceY(g0,g8) = 16
    c: Equal(g8,g0)
    c: Equal(g8,g9)
    c: Symmetric(g8,g9,g-2)
    c: DistanceX(g10,g11) = 10
    c: DistanceY(g11,g10) = 10
    c: Equal(g10,g4)
    c: Equal(g4,g11)
    c: DistanceY(g1,g10) = 0.5
    c: DistanceX(g1,g10) = 13.5
FEATURE [Sketcher::SketchObject] Sketch090
  ArcFitTolerance = 1e-06
  FullyConstrained = true
  MakeInternals = false
  Placement = pos=(0,132,-7.09e-14) rot=(1,0,0;1.5708rad)
  sketch-geometry (4):
    g0: LineSegment StartX=-12.5 StartY=202 StartZ=0 EndX=-12.5 EndY=172 EndZ=0
    g1: LineSegment StartX=-12.5 StartY=172 StartZ=0 EndX=12.5 EndY=172 EndZ=0
    g2: LineSegment StartX=12.5 StartY=172 StartZ=0 EndX=12.5 EndY=202 EndZ=0
    g3: LineSegment StartX=12.5 StartY=202 StartZ=0 EndX=-12.5 EndY=202 EndZ=0
  constraints (12):
    c: Coincident(g0,g1)
    c: Coincident(g1,g2)
    c: Coincident(g2,g3)
    c: Coincident(g3,g0)
    c: Vertical(g0)
    c: Vertical(g2)
    c: Horizontal(g1)
    c: Horizontal(g3)
    c: Distance(g0,g2) = 25
    c: Distance(g1,g3) = 30
    c: DistanceX(g-1,g2) = 12.5
    c: DistanceY(g-1,g1) = 172
FEATURE [Sketcher::SketchObject] Sketch091
  ArcFitTolerance = 1e-06
  AttachmentSupport = -> [XZ_Plane053]
  FullyConstrained = true
  MakeInternals = false
  MapMode = 5
  Placement = pos=(0,0,0) rot=(1,0,0;1.5708rad)
  sketch-geometry (4):
    g0: LineSegment StartX=-10 StartY=211.31 StartZ=0 EndX=-10 EndY=205.56 EndZ=0
    g1: LineSegment StartX=-10 StartY=205.56 StartZ=0 EndX=10 EndY=205.56 EndZ=0
    g2: LineSegment StartX=10 StartY=205.56 StartZ=0 EndX=10 EndY=211.31 EndZ=0
    g3: LineSegment StartX=10 StartY=211.31 StartZ=0 EndX=-10 EndY=211.31 EndZ=0
  constraints (11):
    c: Coincident(g0,g1)
    c: Coincident(g1,g2)
    c: Coincident(g2,g3)
    c: Coincident(g3,g0)
    c: Vertical(g0)
    c: Vertical(g2)
    c: Horizontal(g1)
    c: Distance(g0,g2) = 20
    c: Distance(g1,g3) = 5.75
    c: Symmetric(g0,g2,g-2)
    c: DistanceY(g-1,g1) = 205.56
FEATURE [PartDesign::Pad] Pad030
  Direction = (0,-1,2e-16)
  Length = 18
  Length2 = 10
  Placement = pos=(0,0,0) rot=(1,0,0;1.5708rad)
  Profile = -> Sketch091
  ReferenceAxis = -> Sketch091 [N_Axis]
  Suppressed = false
  Type = 0
FEATURE [Sketcher::SketchObject] Sketch092
  ArcFitTolerance = 1e-06
  AttachmentSupport = -> [Pad030]
  FullyConstrained = true
  MakeInternals = false
  MapMode = 5
  Placement = pos=(0,9.3e-14,211.31) rot=(0,0,1;3.14159rad)
  sketch-geometry (4):
    g0: ArcOfCircle CenterX=0 CenterY=12 CenterZ=0 NormalX=0 NormalY=0 NormalZ=1 AngleXU=0 Radius=6 StartAngle=3.14159 EndAngle=6.28319
    g1: LineSegment StartX=-6 StartY=22 StartZ=0 EndX=-6 EndY=12 EndZ=0
    g2: LineSegment StartX=6 StartY=12 StartZ=0 EndX=6 EndY=22 EndZ=0
    g3: LineSegment StartX=-6 StartY=22 StartZ=0 EndX=6 EndY=22 EndZ=0
  constraints (11):
    c: Diameter(g0) = 12
    c: PointOnObject(g0,g-2)
    c: DistanceY(g-1,g0) = 12
    c: Vertical(g1)
    c: Vertical(g2)
    c: Coincident(g3,g1)
    c: Coincident(g3,g2)
    c: Horizontal(g3)
    c: Tangent(g0,g2) = -1.5708
    c: Tangent(g0,g1) = -1.5708
    c: DistanceY(g2,g2) = 10
FEATURE [PartDesign::Pocket] Pocket028
  BaseFeature = -> Pad030
  Direction = (0,0,-1)
  Length = 5
  Length2 = 5
  Placement = pos=(0,0,0) rot=(1,0,0;1.5708rad)
  Profile = -> Sketch092
  ReferenceAxis = -> Sketch092 [N_Axis]
  Suppressed = false
  Type = 1
FEATURE [Sketcher::SketchObject] Sketch093
  ArcFitTolerance = 1e-06
  AttachmentSupport = -> [XZ_Plane053]
  FullyConstrained = true
  MakeInternals = false
  MapMode = 5
  Placement = pos=(0,0,0) rot=(1,0,0;1.5708rad)
  sketch-geometry (8):
    g0: LineSegment StartX=-10 StartY=211.31 StartZ=0 EndX=-20 EndY=211.31 EndZ=0
    g1: LineSegment StartX=-20 StartY=211.31 StartZ=0 EndX=-20 EndY=205.555 EndZ=0
    g2: LineSegment StartX=-20 StartY=205.555 StartZ=0 EndX=-10 EndY=205.555 EndZ=0
    g3: LineSegment StartX=-10 StartY=205.555 StartZ=0 EndX=-10 EndY=211.31 EndZ=0
    g4: LineSegment StartX=10 StartY=211.31 StartZ=0 EndX=20 EndY=211.31 EndZ=0
    g5: LineSegment StartX=20 StartY=211.31 StartZ=0 EndX=20 EndY=205.555 EndZ=0
    g6: LineSegment StartX=20 StartY=205.555 StartZ=0 EndX=10 EndY=205.555 EndZ=0
    g7: LineSegment StartX=10 StartY=205.555 StartZ=0 EndX=10 EndY=211.31 EndZ=0
  constraints (20):
    c: Coincident(g0,g1)
    c: Coincident(g1,g2)
    c: Coincident(g2,g3)
    c: Coincident(g3,g0)
    c: Horizontal(g0)
    c: Horizontal(g2)
    c: Vertical(g1)
    c: Vertical(g3)
    c: Distance(g1,g3) = 10
    c: Distance(g0,g2) = 5.755
    c: DistanceY(g-1,g2) = 205.555
    c: DistanceX(g2,g-1) = 10
    c: Symmetric(g0,g4,g-2)
    c: Symmetric(g0,g4,g-2)
    c: Symmetric(g1,g5,g-2)
    c: Symmetric(g1,g5,g-2)
    c: Symmetric(g2,g6,g-2)
    c: Symmetric(g2,g6,g-2)
    c: Symmetric(g3,g7,g-2)
    c: Symmetric(g3,g7,g-2)
FEATURE [PartDesign::Pad] Pad031
  BaseFeature = -> Pocket028
  Direction = (0,-1,2e-16)
  Length = 3
  Length2 = 10
  Placement = pos=(0,0,0) rot=(1,0,0;1.5708rad)
  Profile = -> Sketch093
  ReferenceAxis = -> Sketch093 [N_Axis]
  Suppressed = false
  Type = 0
FEATURE [Sketcher::SketchObject] Sketch094
  ArcFitTolerance = 1e-06
  AttachmentSupport = -> [Pad031]
  FullyConstrained = true
  MakeInternals = false
  MapMode = 5
  Placement = pos=(0,-3,7e-16) rot=(1,0,0;1.5708rad)
  sketch-geometry (2):
    g0: Circle CenterX=-17 CenterY=208.5 CenterZ=0 NormalX=0 NormalY=0 NormalZ=1 AngleXU=0 Radius=1.5
    g1: Circle CenterX=17 CenterY=208.5 CenterZ=0 NormalX=0 NormalY=0 NormalZ=1 AngleXU=0 Radius=1.5
  constraints (5):
    c: Diameter(g0) = 3
    c: DistanceX(g0,g-1) = 17
    c: DistanceY(g-1,g0) = 208.5
    c: Equal(g0,g1)
    c: Symmetric(g0,g1,g-2)
FEATURE [PartDesign::Hole] Hole018
  BaseFeature = -> Pad031
  CustomThreadClearance = 0
  Depth = 25
  DepthType = 0
  Diameter = 3.4
  DrillForDepth = false
  DrillPoint = 1
  DrillPointAngle = 118
  HoleCutCountersinkAngle = 90
  HoleCutCustomValues = false
  HoleCutDepth = 0
  HoleCutDiameter = 6.1
  HoleCutType = 0
  ModelThread = false
  Placement = pos=(0,0,0) rot=(1,0,0;1.5708rad)
  Profile = -> Sketch094
  Suppressed = false
  Tapered = false
  TaperedAngle = 90
  ThreadClass = 0
  ThreadDepth = 25
  ThreadDepthType = 0
  ThreadDirection = 0
  ThreadFit = 0
  ThreadSize = 9
  ThreadType = 1
  Threaded = false
  UseCustomThreadClearance = false
FEATURE [PartDesign::Body] Body013  label="HotendHolder1"
  AllowCompound = false
  Group = -> [Sketch091,Pad030,Sketch092,Pocket028,Sketch093,Pad031,Sketch094,Hole018]
  Origin = -> Origin053
  Placement = pos=(0,132,0) rot=(0,0,1;0rad)
  Tip = -> Hole018
FEATURE [Sketcher::SketchObject] Sketch095
  ArcFitTolerance = 1e-06
  AttachmentSupport = -> [XY_Plane054]
  FullyConstrained = false
  MakeInternals = false
  MapMode = 5
  sketch-geometry (8):
    g0: LineSegment StartX=-10 StartY=0 StartZ=0 EndX=-10 EndY=-3 EndZ=0
    g1: LineSegment StartX=-10 StartY=-3 StartZ=0 EndX=10 EndY=-3 EndZ=0
    g2: LineSegment StartX=10 StartY=-3 StartZ=0 EndX=10 EndY=0 EndZ=0
    g3: LineSegment StartX=10 StartY=0 StartZ=0 EndX=6 EndY=0 EndZ=0
    g4: ArcOfCircle CenterX=0 CenterY=6 CenterZ=0 NormalX=0 NormalY=0 NormalZ=1 AngleXU=0 Radius=6 StartAngle=3.14159 EndAngle=6.28319
    g5: LineSegment StartX=-6 StartY=2.25984e-07 StartZ=0 EndX=-6 EndY=6 EndZ=0
    g6: LineSegment StartX=6 StartY=6 StartZ=0 EndX=6 EndY=0 EndZ=0
    g7: LineSegment StartX=-6 StartY=2.25984e-07 StartZ=0 EndX=-10 EndY=0 EndZ=0
  constraints (24):
    c: Coincident(g0,g1)
    c: Coincident(g1,g2)
    c: Coincident(g2,g3)
    c: Coincident(g7,g0)
    c: Vertical(g0)
    c: Vertical(g2)
    c: Horizontal(g1)
    c: Horizontal(g3)
    c: Distance(g0,g2) = 20
    c: Distance(g1,g7) = 3
    c: PointOnObject(g0,g-1)
    c: Diameter(g4) = 12
    c: PointOnObject(g4,g-2)
    c: DistanceY(g-1,g4) = 6
    c: PointOnObject(g5,g7)
    c: Vertical(g5)
    c: Vertical(g6)
    c: Coincident(g4,g6)
    c: Coincident(g4,g5)
    c: PointOnObject(g7,g5)
    c: Coincident(g3,g6)
    c: DistanceY(g5,g5) = 6
    c: DistanceX(g7,g7) = 4
    c: DistanceX(g3,g3) = 4
FEATURE [PartDesign::Pad] Pad032
  Direction = (0,0,1)
  Length = 5.75
  Length2 = 10
  Profile = -> Sketch095
  ReferenceAxis = -> Sketch095 [N_Axis]
  Suppressed = false
  Type = 0
FEATURE [Sketcher::SketchObject] Sketch096
  ArcFitTolerance = 1e-06
  AttachmentOffset = pos=(0,0,3) rot=(0,0,1;0rad)
  AttachmentSupport = -> [XZ_Plane054]
  FullyConstrained = true
  MakeInternals = false
  MapMode = 5
  Placement = pos=(0,-3,7e-16) rot=(1,0,0;1.5708rad)
  sketch-geometry (8):
    g0: LineSegment StartX=-10 StartY=5.75 StartZ=0 EndX=-13 EndY=5.75 EndZ=0
    g1: LineSegment StartX=-13 StartY=5.75 StartZ=0 EndX=-13 EndY=0 EndZ=0
    g2: LineSegment StartX=-13 StartY=0 StartZ=0 EndX=-10 EndY=0 EndZ=0
    g3: LineSegment StartX=-10 StartY=0 StartZ=0 EndX=-10 EndY=5.75 EndZ=0
    g4: LineSegment StartX=10 StartY=5.75 StartZ=0 EndX=13 EndY=5.75 EndZ=0
    g5: LineSegment StartX=13 StartY=5.75 StartZ=0 EndX=13 EndY=0 EndZ=0
    g6: LineSegment StartX=13 StartY=0 StartZ=0 EndX=10 EndY=0 EndZ=0
    g7: LineSegment StartX=10 StartY=0 StartZ=0 EndX=10 EndY=5.75 EndZ=0
  constraints (20):
    c: Coincident(g0,g1)
    c: Coincident(g1,g2)
    c: Coincident(g2,g3)
    c: Coincident(g3,g0)
    c: Horizontal(g0)
    c: Horizontal(g2)
    c: Vertical(g1)
    c: Vertical(g3)
    c: PointOnObject(g1,g-1)
    c: DistanceX(g0,g0) = 3
    c: DistanceY(g1,g1) = 5.75
    c: DistanceX(g0,g-1) = 10
    c: Symmetric(g0,g4,g-2)
    c: Symmetric(g0,g4,g-2)
    c: Symmetric(g1,g5,g-2)
    c: Symmetric(g1,g5,g-2)
    c: Symmetric(g2,g6,g-2)
    c: Symmetric(g2,g6,g-2)
    c: Symmetric(g3,g7,g-2)
    c: Symmetric(g3,g7,g-2)
FEATURE [PartDesign::Pad] Pad033
  BaseFeature = -> Pad032
  Direction = (0,-1,2e-16)
  Length = 18
  Length2 = 10
  Profile = -> Sketch096
  ReferenceAxis = -> Sketch096 [N_Axis]
  Reversed = true
  Suppressed = false
  Type = 0
FEATURE [Sketcher::SketchObject] Sketch097
  ArcFitTolerance = 1e-06
  AttachmentSupport = -> [Pad033]
  FullyConstrained = true
  MakeInternals = false
  MapMode = 5
  Placement = pos=(0,1.3e-15,5.75) rot=(0,0,1;0rad)
  sketch-geometry (8):
    g0: LineSegment StartX=-13 StartY=15 StartZ=0 EndX=-20 EndY=15 EndZ=0
    g1: LineSegment StartX=-20 StartY=15 StartZ=0 EndX=-20 EndY=12 EndZ=0
    g2: LineSegment StartX=-20 StartY=12 StartZ=0 EndX=-13 EndY=12 EndZ=0
    g3: LineSegment StartX=-13 StartY=12 StartZ=0 EndX=-13 EndY=15 EndZ=0
    g4: LineSegment StartX=13 StartY=15 StartZ=0 EndX=20 EndY=15 EndZ=0
    g5: LineSegment StartX=20 StartY=15 StartZ=0 EndX=20 EndY=12 EndZ=0
    g6: LineSegment StartX=20 StartY=12 StartZ=0 EndX=13 EndY=12 EndZ=0
    g7: LineSegment StartX=13 StartY=12 StartZ=0 EndX=13 EndY=15 EndZ=0
  constraints (20):
    c: Coincident(g0,g1)
    c: Coincident(g1,g2)
    c: Coincident(g2,g3)
    c: Coincident(g3,g0)
    c: Horizontal(g0)
    c: Horizontal(g2)
    c: Vertical(g1)
    c: Vertical(g3)
    c: Distance(g1,g3) = 7
    c: Distance(g0,g2) = 3
    c: DistanceX(g0,g-1) = 13
    c: DistanceY(g-1,g2) = 12
    c: Symmetric(g0,g4,g-2)
    c: Symmetric(g0,g4,g-2)
    c: Symmetric(g1,g5,g-2)
    c: Symmetric(g1,g5,g-2)
    c: Symmetric(g2,g6,g-2)
    c: Symmetric(g2,g6,g-2)
    c: Symmetric(g3,g7,g-2)
    c: Symmetric(g3,g7,g-2)
FEATURE [PartDesign::Pad] Pad034
  BaseFeature = -> Pad033
  Direction = (0,0,1)
  Length = 5.75
  Length2 = 10
  Profile = -> Sketch097
  ReferenceAxis = -> Sketch097 [N_Axis]
  Reversed = true
  Suppressed = false
  Type = 0
FEATURE [Sketcher::SketchObject] Sketch098
  ArcFitTolerance = 1e-06
  AttachmentSupport = -> [Pad034]
  FullyConstrained = true
  MakeInternals = false
  MapMode = 5
  Placement = pos=(0,12,0) rot=(1,0,0;1.5708rad)
  sketch-geometry (2):
    g0: Circle CenterX=-17 CenterY=2.95 CenterZ=0 NormalX=0 NormalY=0 NormalZ=1 AngleXU=0 Radius=1.5
    g1: Circle CenterX=17 CenterY=2.95 CenterZ=0 NormalX=0 NormalY=0 NormalZ=1 AngleXU=0 Radius=1.5
  constraints (5):
    c: Diameter(g0) = 3
    c: DistanceX(g0,g-1) = 17
    c: DistanceY(g-1,g0) = 2.95
    c: Equal(g0,g1)
    c: Symmetric(g0,g1,g-2)
FEATURE [PartDesign::Hole] Hole019
  BaseFeature = -> Pad034
  CustomThreadClearance = 0
  Depth = 25
  DepthType = 0
  Diameter = 3.4
  DrillForDepth = false
  DrillPoint = 1
  DrillPointAngle = 118
  HoleCutCountersinkAngle = 90
  HoleCutCustomValues = false
  HoleCutDepth = 0
  HoleCutDiameter = 6.1
  HoleCutType = 0
  ModelThread = false
  Profile = -> Sketch098
  Suppressed = false
  Tapered = false
  TaperedAngle = 90
  ThreadClass = 0
  ThreadDepth = 25
  ThreadDepthType = 0
  ThreadDirection = 0
  ThreadFit = 0
  ThreadSize = 9
  ThreadType = 1
  Threaded = false
  UseCustomThreadClearance = false
FEATURE [PartDesign::Body] Body014  label="HotendHolder2"
  AllowCompound = false
  Group = -> [Sketch095,Pad032,Sketch096,Pad033,Sketch097,Pad034,Sketch098,Hole019]
  Origin = -> Origin054
  Placement = pos=(0,114,205.555) rot=(0,0,1;0rad)
  Tip = -> Hole019
FEATURE [Sketcher::SketchObject] Sketch099
  ArcFitTolerance = 1e-06
  AttachmentSupport = -> [Pad029]
  FullyConstrained = true
  MakeInternals = false
  MapMode = 5
  Placement = pos=(0,8.93e-14,203) rot=(0,0,1;3.14159rad)
  sketch-geometry (5):
    g0: LineSegment StartX=-12.5 StartY=-14 StartZ=0 EndX=-12.5 EndY=-24 EndZ=0
    g1: LineSegment StartX=12.5 StartY=-14 StartZ=0 EndX=12.5 EndY=-24 EndZ=0
    g2: LineSegment StartX=-12.5 StartY=-24 StartZ=0 EndX=12.5 EndY=-24 EndZ=0
    g3: ArcOfCircle CenterX=0 CenterY=-14 CenterZ=0 NormalX=0 NormalY=0 NormalZ=1 AngleXU=0 Radius=12.5 StartAngle=0 EndAngle=3.14159
    g4: LineSegment [constr] StartX=-12.5 StartY=-14 StartZ=0 EndX=12.5 EndY=-14 EndZ=0
  constraints (15):
    c: Vertical(g0)
    c: Vertical(g1)
    c: Coincident(g2,g0)
    c: Coincident(g2,g1)
    c: Horizontal(g2)
    c: DistanceY(g0,g0) = 10
    c: PointOnObject(g3,g-2)
    c: Coincident(g3,g0)
    c: Coincident(g3,g1)
    c: DistanceY(g3,g-1) = 14
    c: DistanceY(g0,g-1) = 14
    c: Coincident(g4,g0)
    c: Coincident(g4,g1)
    c: Horizontal(g4)
    c: Radius(g3) = 12.5
FEATURE [PartDesign::Pocket] Pocket029
  BaseFeature = -> Pad029
  Direction = (0,0,-1)
  Length = 5
  Length2 = 5
  Placement = pos=(0,0,0) rot=(1,0,0;1.5708rad)
  Profile = -> Sketch099
  ReferenceAxis = -> Sketch099 [N_Axis]
  Suppressed = false
  Type = 1
FEATURE [Sketcher::SketchObject] Sketch100
  ArcFitTolerance = 1e-06
  AttachmentSupport = -> [Pocket029]
  FullyConstrained = true
  MakeInternals = false
  MapMode = 5
  Placement = pos=(0,-3,7e-16) rot=(1,0,0;1.5708rad)
  sketch-geometry (1):
    g0: Circle CenterX=0 CenterY=187 CenterZ=0 NormalX=0 NormalY=0 NormalZ=1 AngleXU=0 Radius=14
  constraints (3):
    c: Diameter(g0) = 28
    c: PointOnObject(g0,g-2)
    c: DistanceY(g-1,g0) = 187
FEATURE [PartDesign::Pocket] Pocket030
  BaseFeature = -> Pocket029
  Direction = (0,1,-2e-16)
  Length = 5
  Length2 = 5
  Placement = pos=(0,0,0) rot=(1,0,0;1.5708rad)
  Profile = -> Sketch100
  ReferenceAxis = -> Sketch100 [N_Axis]
  Suppressed = false
  Type = 1
FEATURE [Sketcher::SketchObject] Sketch101
  ArcFitTolerance = 1e-06
  AttachmentSupport = -> [Pocket030]
  FullyConstrained = true
  MakeInternals = false
  MapMode = 5
  Placement = pos=(0,27,-6.2e-15) rot=(-1,0,0;1.5708rad)
  sketch-geometry (4):
    g0: LineSegment StartX=-12.5 StartY=-172 StartZ=0 EndX=-12.5 EndY=-182 EndZ=0
    g1: LineSegment StartX=-12.5 StartY=-182 StartZ=0 EndX=12.5 EndY=-182 EndZ=0
    g2: LineSegment StartX=12.5 StartY=-182 StartZ=0 EndX=12.5 EndY=-172 EndZ=0
    g3: LineSegment StartX=12.5 StartY=-172 StartZ=0 EndX=-12.5 EndY=-172 EndZ=0
  constraints (11):
    c: Coincident(g0,g1)
    c: Coincident(g1,g2)
    c: Coincident(g2,g3)
    c: Coincident(g3,g0)
    c: Vertical(g0)
    c: Vertical(g2)
    c: Horizontal(g1)
    c: DistanceX(g3,g3) = 25
    c: DistanceY(g0,g0) = 10
    c: DistanceY(g0,g-1) = 182
    c: Symmetric(g0,g2,g-2)
FEATURE [PartDesign::Pocket] Pocket031
  BaseFeature = -> Pocket030
  Direction = (0,-1,-2e-16)
  Length = 3
  Length2 = 5
  Placement = pos=(0,0,0) rot=(1,0,0;1.5708rad)
  Profile = -> Sketch101
  ReferenceAxis = -> Sketch101 [N_Axis]
  Suppressed = false
  Type = 0
FEATURE [Sketcher::SketchObject] Sketch102
  ArcFitTolerance = 1e-06
  AttachmentSupport = -> [Pocket031]
  FullyConstrained = true
  MakeInternals = false
  MapMode = 5
  Placement = pos=(0,-3,7e-16) rot=(1,0,0;1.5708rad)
  sketch-geometry (5):
    g0: Circle CenterX=-12 CenterY=199 CenterZ=0 NormalX=0 NormalY=0 NormalZ=1 AngleXU=0 Radius=2.3
    g1: Circle CenterX=-12 CenterY=175 CenterZ=0 NormalX=0 NormalY=0 NormalZ=1 AngleXU=0 Radius=2.3
    g2: LineSegment [constr] StartX=-12 StartY=199 StartZ=0 EndX=-12 EndY=175 EndZ=0
    g3: Circle CenterX=12 CenterY=175 CenterZ=0 NormalX=0 NormalY=0 NormalZ=1 AngleXU=0 Radius=2.3
    g4: Circle CenterX=12 CenterY=199 CenterZ=0 NormalX=0 NormalY=0 NormalZ=1 AngleXU=0 Radius=2.3
  constraints (12):
    c: Diameter(g0) = 4.6
    c: DistanceX(g0,g-1) = 12
    c: DistanceY(g-1,g0) = 199
    c: DistanceY(g1,g0) = 24
    c: Equal(g1,g0)
    c: Coincident(g2,g0)
    c: Coincident(g2,g1)
    c: Vertical(g2)
    c: Equal(g0,g4)
    c: Symmetric(g0,g4,g-2)
    c: Equal(g1,g3)
    c: Symmetric(g1,g3,g-2)
FEATURE [PartDesign::Pocket] Pocket032
  BaseFeature = -> Pocket031
  Direction = (0,1,-2e-16)
  Length = 5.5
  Length2 = 5
  Placement = pos=(0,0,0) rot=(1,0,0;1.5708rad)
  Profile = -> Sketch102
  ReferenceAxis = -> Sketch102 [N_Axis]
  Suppressed = false
  Type = 0
FEATURE [Sketcher::SketchObject] Sketch103
  ArcFitTolerance = 1e-06
  AttachmentOffset = pos=(0,0,-27) rot=(0,0,1;0rad)
  AttachmentSupport = -> [XZ_Plane052]
  FullyConstrained = true
  MakeInternals = false
  MapMode = 5
  Placement = pos=(0,27,-6e-15) rot=(1,0,0;1.5708rad)
  sketch-geometry (8):
    g0: LineSegment StartX=-20 StartY=203 StartZ=0 EndX=-26 EndY=203 EndZ=0
    g1: LineSegment StartX=-26 StartY=203 StartZ=0 EndX=-26 EndY=172 EndZ=0
    g2: LineSegment StartX=-26 StartY=172 StartZ=0 EndX=-20 EndY=172 EndZ=0
    g3: LineSegment StartX=-20 StartY=172 StartZ=0 EndX=-20 EndY=203 EndZ=0
    g4: LineSegment StartX=20 StartY=203 StartZ=0 EndX=26 EndY=203 EndZ=0
    g5: LineSegment StartX=26 StartY=203 StartZ=0 EndX=26 EndY=172 EndZ=0
    g6: LineSegment StartX=26 StartY=172 StartZ=0 EndX=20 EndY=172 EndZ=0
    g7: LineSegment StartX=20 StartY=172 StartZ=0 EndX=20 EndY=203 EndZ=0
  constraints (20):
    c: Coincident(g0,g1)
    c: Coincident(g1,g2)
    c: Coincident(g2,g3)
    c: Coincident(g3,g0)
    c: Horizontal(g0)
    c: Horizontal(g2)
    c: Vertical(g1)
    c: Vertical(g3)
    c: Distance(g1,g3) = 6
    c: Distance(g0,g2) = 31
    c: DistanceX(g0,g-1) = 20
    c: DistanceY(g-1,g2) = 172
    c: Symmetric(g0,g4,g-2)
    c: Symmetric(g0,g4,g-2)
    c: Symmetric(g1,g5,g-2)
    c: Symmetric(g1,g5,g-2)
    c: Symmetric(g2,g6,g-2)
    c: Symmetric(g2,g6,g-2)
    c: Symmetric(g3,g7,g-2)
    c: Symmetric(g3,g7,g-2)
FEATURE [PartDesign::Pad] Pad035
  BaseFeature = -> Pocket032
  Direction = (0,-1,2e-16)
  Length = 6
  Length2 = 10
  Placement = pos=(0,0,0) rot=(1,0,0;1.5708rad)
  Profile = -> Sketch103
  ReferenceAxis = -> Sketch103 [N_Axis]
  Suppressed = false
  Type = 0
FEATURE [Sketcher::SketchObject] Sketch104
  ArcFitTolerance = 1e-06
  AttachmentOffset = pos=(0,0,-27) rot=(0,0,1;0rad)
  AttachmentSupport = -> [XZ_Plane052]
  FullyConstrained = true
  MakeInternals = false
  MapMode = 5
  Placement = pos=(0,27,-6e-15) rot=(1,0,0;1.5708rad)
  sketch-geometry (8):
    g0: LineSegment StartX=-26 StartY=198 StartZ=0 EndX=-15 EndY=187 EndZ=0
    g1: LineSegment StartX=-15 StartY=187 StartZ=0 EndX=-15 EndY=172 EndZ=0
    g2: LineSegment StartX=-15 StartY=172 StartZ=0 EndX=-26 EndY=172 EndZ=0
    g3: LineSegment StartX=-26 StartY=172 StartZ=0 EndX=-26 EndY=198 EndZ=0
    g4: LineSegment StartX=26 StartY=198 StartZ=0 EndX=15 EndY=187 EndZ=0
    g5: LineSegment StartX=15 StartY=187 StartZ=0 EndX=15 EndY=172 EndZ=0
    g6: LineSegment StartX=15 StartY=172 StartZ=0 EndX=26 EndY=172 EndZ=0
    g7: LineSegment StartX=26 StartY=172 StartZ=0 EndX=26 EndY=198 EndZ=0
  constraints (20):
    c: Angle(g-1,g0) = -0.785398
    c: Coincident(g1,g0)
    c: Vertical(g1)
    c: Coincident(g2,g1)
    c: Horizontal(g2)
    c: Coincident(g3,g2)
    c: Coincident(g3,g0)
    c: Vertical(g3)
    c: DistanceX(g2,g2) = 11
    c: DistanceY(g1,g1) = 15
    c: DistanceX(g1,g-1) = 15
    c: DistanceY(g-1,g1) = 172
    c: Symmetric(g0,g4,g-2)
    c: Symmetric(g0,g4,g-2)
    c: Symmetric(g1,g5,g-2)
    c: Symmetric(g1,g5,g-2)
    c: Symmetric(g2,g6,g-2)
    c: Symmetric(g2,g6,g-2)
    c: Symmetric(g3,g7,g-2)
    c: Symmetric(g3,g7,g-2)
FEATURE [PartDesign::Pocket] Pocket033
  BaseFeature = -> Pad035
  Direction = (0,1,-2e-16)
  Length = 5
  Length2 = 5
  Placement = pos=(0,0,0) rot=(1,0,0;1.5708rad)
  Profile = -> Sketch104
  ReferenceAxis = -> Sketch104 [N_Axis]
  Reversed = true
  Suppressed = false
  Type = 1
FEATURE [Sketcher::SketchObject] Sketch105
  ArcFitTolerance = 1e-06
  AttachmentSupport = -> [Hole016]
  FullyConstrained = true
  MakeInternals = false
  MapMode = 5
  Placement = pos=(0,136,-5.58e-14) rot=(-1,0,0;1.5708rad)
  sketch-geometry (11):
    g0: Circle CenterX=-17 CenterY=-208.5 CenterZ=0 NormalX=0 NormalY=0 NormalZ=1 AngleXU=0 Radius=4
    g1: Circle CenterX=17 CenterY=-208.5 CenterZ=0 NormalX=0 NormalY=0 NormalZ=1 AngleXU=0 Radius=4
    g2: Circle CenterX=-22.5 CenterY=-199.5 CenterZ=0 NormalX=0 NormalY=0 NormalZ=1 AngleXU=0 Radius=4
    g3: Circle CenterX=22.5 CenterY=-199.5 CenterZ=0 NormalX=0 NormalY=0 NormalZ=1 AngleXU=0 Radius=4
    g4: Circle CenterX=-34 CenterY=-210 CenterZ=0 NormalX=0 NormalY=0 NormalZ=1 AngleXU=0 Radius=4
    g5: Circle CenterX=-34 CenterY=-220 CenterZ=0 NormalX=0 NormalY=0 NormalZ=1 AngleXU=0 Radius=4
    g6: LineSegment [constr] StartX=-34 StartY=-210 StartZ=0 EndX=-34 EndY=-220 EndZ=0
    g7: Circle CenterX=-7.5 CenterY=-224.5 CenterZ=0 NormalX=0 NormalY=0 NormalZ=1 AngleXU=0 Radius=4
    g8: Circle CenterX=7.5 CenterY=-224.5 CenterZ=0 NormalX=0 NormalY=0 NormalZ=1 AngleXU=0 Radius=4
    g9: Circle CenterX=40.5 CenterY=-199 CenterZ=0 NormalX=0 NormalY=0 NormalZ=1 AngleXU=0 Radius=4
    g10: Circle CenterX=30.5 CenterY=-209 CenterZ=0 NormalX=0 NormalY=0 NormalZ=1 AngleXU=0 Radius=4
  constraints (29):
    c: Diameter(g0) = 8
    c: DistanceX(g0,g-1) = 17
    c: DistanceY(g0,g-1) = 208.5
    c: Equal(g0,g1)
    c: Symmetric(g0,g1,g-2)
    c: Equal(g0,g2)
    c: DistanceY(g2,g-1) = 199.5
    c: DistanceX(g2,g-1) = 22.5
    c: Equal(g2,g3)
    c: Symmetric(g2,g3,g-2)
    c: Equal(g5,g4)
    c: Equal(g0,g4)
    c: Coincident(g6,g4)
    c: Coincident(g6,g5)
    c: Vertical(g6)
    c: DistanceY(g6,g6) = 10
    c: DistanceX(g4,g0) = 17
    c: DistanceY(g4,g0) = 1.5
    c: Equal(g0,g7)
    c: DistanceX(g7,g-1) = 7.5
    c: DistanceY(g7,g0) = 16
    c: Equal(g7,g8)
    c: Symmetric(g7,g8,g-2)
    c: Equal(g3,g10)
    c: Equal(g10,g9)
    c: DistanceX(g3,g9) = 18
    c: DistanceY(g10,g9) = 10
    c: DistanceX(g10,g9) = 10
    c: DistanceY(g3,g9) = 0.5
FEATURE [PartDesign::Pad] Pad036
  BaseFeature = -> Hole016
  Direction = (0,1,2e-16)
  Length = 2.5
  Length2 = 10
  Placement = pos=(0,0,0) rot=(1,0,0;1.5708rad)
  Profile = -> Sketch105
  ReferenceAxis = -> Sketch105 [N_Axis]
  Suppressed = false
  Type = 0
FEATURE [PartDesign::Hole] Hole017
  BaseFeature = -> Pad036
  CustomThreadClearance = 0
  Depth = 5.5
  DepthType = 0
  Diameter = 5.5
  DrillForDepth = false
  DrillPoint = 0
  DrillPointAngle = 118
  HoleCutCountersinkAngle = 90
  HoleCutCustomValues = false
  HoleCutDepth = 0
  HoleCutDiameter = 6.1
  HoleCutType = 0
  ModelThread = false
  Placement = pos=(0,0,0) rot=(1,0,0;1.5708rad)
  Profile = -> Sketch089
  Suppressed = false
  Tapered = false
  TaperedAngle = 90
  ThreadClass = 0
  ThreadDepth = 5.5
  ThreadDepthType = 0
  ThreadDirection = 0
  ThreadFit = 0
  ThreadSize = 0
  ThreadType = 0
  Threaded = false
  UseCustomThreadClearance = false
FEATURE [PartDesign::Pocket] Pocket027
  BaseFeature = -> Hole017
  Direction = (0,1,-2e-16)
  Length = 5
  Length2 = 5
  Placement = pos=(0,0,0) rot=(1,0,0;1.5708rad)
  Profile = -> Sketch090
  ReferenceAxis = -> Sketch090 [N_Axis]
  Suppressed = false
  Type = 1
FEATURE [PartDesign::Body] Body008  label="FrontAttachmentPlate"
  AllowCompound = false
  Group = -> [Sketch069,Pad022,Sketch076,Hole013,Sketch078,Sketch080,Sketch082,Pad025,Sketch084,Hole015,Sketch085,Hole016,Sketch089,Sketch105,Pad036,Hole017,Sketch090,Pocket027]
  Origin = -> Origin030
  Tip = -> Pocket027
FEATURE [Part::Cut] Cut
  Base = -> Body008
  Tool = -> Fusion001
FEATURE [Sketcher::SketchObject] Sketch106
  ArcFitTolerance = 1e-06
  AttachmentOffset = pos=(0,0,-27) rot=(0,0,1;0rad)
  AttachmentSupport = -> [XZ_Plane052]
  FullyConstrained = true
  MakeInternals = false
  MapMode = 5
  Placement = pos=(0,27,-6e-15) rot=(1,0,0;1.5708rad)
  sketch-geometry (8):
    g0: LineSegment StartX=-19 StartY=203 StartZ=0 EndX=-26 EndY=203 EndZ=0
    g1: LineSegment StartX=-26 StartY=203 StartZ=0 EndX=-26 EndY=198 EndZ=0
    g2: LineSegment StartX=-19 StartY=191 StartZ=0 EndX=-26 EndY=198 EndZ=0
    g3: LineSegment StartX=-19 StartY=191 StartZ=0 EndX=-19 EndY=203 EndZ=0
    g4: LineSegment StartX=19 StartY=203 StartZ=0 EndX=26 EndY=203 EndZ=0
    g5: LineSegment StartX=26 StartY=203 StartZ=0 EndX=26 EndY=198 EndZ=0
    g6: LineSegment StartX=19 StartY=191 StartZ=0 EndX=26 EndY=198 EndZ=0
    g7: LineSegment StartX=19 StartY=191 StartZ=0 EndX=19 EndY=203 EndZ=0
  constraints (20):
    c: Coincident(g0,g1)
    c: Horizontal(g0)
    c: Vertical(g1)
    c: Distance(g1,g0) = 7
    c: DistanceX(g0,g-1) = 19
    c: Coincident(g3,g2)
    c: Coincident(g3,g0)
    c: Vertical(g3)
    c: Coincident(g2,g1)
    c: DistanceY(g1,g1) = 5
    c: Angle(g3,g2) = 0.785398
    c: DistanceY(g-1,g0) = 203
    c: Symmetric(g0,g4,g-2)
    c: Symmetric(g0,g4,g-2)
    c: Symmetric(g1,g5,g-2)
    c: Symmetric(g1,g5,g-2)
    c: Symmetric(g2,g6,g-2)
    c: Symmetric(g2,g6,g-2)
    c: Symmetric(g3,g7,g-2)
    c: Symmetric(g3,g7,g-2)
FEATURE [PartDesign::Pad] Pad037
  BaseFeature = -> Pocket033
  Direction = (0,-1,2e-16)
  Length = 6
  Length2 = 10
  Placement = pos=(0,0,0) rot=(1,0,0;1.5708rad)
  Profile = -> Sketch106
  ReferenceAxis = -> Sketch106 [N_Axis]
  Suppressed = false
  Type = 0
FEATURE [Sketcher::SketchObject] Sketch107
  ArcFitTolerance = 1e-06
  AttachmentSupport = -> [Pad037]
  FullyConstrained = true
  MakeInternals = false
  MapMode = 5
  Placement = pos=(0,21,-6.3e-15) rot=(1,0,0;1.5708rad)
  sketch-geometry (2):
    g0: Circle CenterX=-22.5 CenterY=199.5 CenterZ=0 NormalX=0 NormalY=0 NormalZ=1 AngleXU=0 Radius=1.5
    g1: Circle CenterX=22.5 CenterY=199.5 CenterZ=0 NormalX=0 NormalY=0 NormalZ=1 AngleXU=0 Radius=1.5
  constraints (5):
    c: Diameter(g0) = 3
    c: DistanceY(g-1,g0) = 199.5
    c: DistanceX(g0,g-1) = 22.5
    c: Equal(g0,g1)
    c: Symmetric(g0,g1,g-2)
FEATURE [PartDesign::Hole] Hole020
  BaseFeature = -> Pad037
  CustomThreadClearance = 0
  Depth = 25
  DepthType = 0
  Diameter = 3.4
  DrillForDepth = false
  DrillPoint = 1
  DrillPointAngle = 118
  HoleCutCountersinkAngle = 90
  HoleCutCustomValues = false
  HoleCutDepth = 0
  HoleCutDiameter = 6.1
  HoleCutType = 0
  ModelThread = false
  Placement = pos=(0,0,0) rot=(1,0,0;1.5708rad)
  Profile = -> Sketch107
  Suppressed = false
  Tapered = false
  TaperedAngle = 90
  ThreadClass = 0
  ThreadDepth = 25
  ThreadDepthType = 0
  ThreadDirection = 0
  ThreadFit = 0
  ThreadSize = 9
  ThreadType = 1
  Threaded = false
  UseCustomThreadClearance = false
FEATURE [PartDesign::Body] Body012  label="HeatBreakFanHolder"
  AllowCompound = false
  Group = -> [Sketch088,Pad029,Sketch099,Pocket029,Sketch100,Pocket030,Sketch101,Pocket031,Sketch102,Pocket032,Sketch103,Pad035,Sketch104,Pocket033,Sketch106,Pad037,Sketch107,Hole020]
  Origin = -> Origin052
  Placement = pos=(0,105,0) rot=(0,0,1;0rad)
  Tip = -> Hole020
FEATURE [Part::Feature] Part__Feature319  label="rear end cap003"
  shape: bbox 46.44 x 42.08 x 9.4 mm, 73 faces (baked)
FEATURE [Part::Feature] Part__Feature320  label="rear bearing003"
  Placement = pos=(0,0,6.6) rot=(0,0,1;0rad)
  shape: bbox 16 x 16 x 5.05 mm, 13 faces (baked)
FEATURE [Part::Feature] Part__Feature321  label="connector003"
  shape: bbox 10.8 x 15.6 x 6.2 mm, 85 faces (baked)
FEATURE [Part::Feature] Part__Feature322  label="shaft003"
  Placement = pos=(0,0,2.8) rot=(0,0,1;0rad)
  shape: bbox 5 x 5 x 58 mm, 7 faces (baked)
FEATURE [Part::Feature] Part__Feature323  label="stator003"
  Placement = pos=(0,0,9.4) rot=(0,0,1;0rad)
  shape: bbox 42 x 42 x 20 mm, 713 faces (baked)
FEATURE [Part::Feature] Part__Feature324  label="front end cap003"
  Placement = pos=(0,0,29.4) rot=(0,0,1;0rad)
  shape: bbox 42 x 42 x 10 mm, 34 faces (baked)
FEATURE [Part::Feature] Part__Feature325  label="front bearing003"
  Placement = pos=(0,0,34.6) rot=(0,1,0;3.14159rad)
  shape: bbox 16 x 16 x 5.05 mm, 13 faces (baked)
FEATURE [Part::Feature] Part__Feature326  label="M3x10-Screw012"
  Placement = pos=(15.5,15.5,2) rot=(0,1,0;3.14159rad)
  shape: bbox 5.7 x 5.7 x 11.65 mm, 15 faces (baked)
FEATURE [Part::Feature] Part__Feature327  label="M3x10-Screw013"
  Placement = pos=(15.5,-15.5,2) rot=(0,1,0;3.14159rad)
  shape: bbox 5.7 x 5.7 x 11.65 mm, 15 faces (baked)
FEATURE [Part::Feature] Part__Feature328  label="M3x10-Screw014"
  Placement = pos=(-15.5,15.5,2) rot=(0,1,0;3.14159rad)
  shape: bbox 5.7 x 5.7 x 11.65 mm, 15 faces (baked)
FEATURE [Part::Feature] Part__Feature329  label="M3x10-Screw015"
  Placement = pos=(-15.5,-15.5,2) rot=(0,1,0;3.14159rad)
  shape: bbox 5.7 x 5.7 x 11.65 mm, 15 faces (baked)
FEATURE [App::Part] _7HS4401S_Stepper_Motor003  label="YMotor"
  Group = -> [Part__Feature319,Part__Feature320,Part__Feature321,Part__Feature322,Part__Feature323,Part__Feature324,Part__Feature325,Part__Feature326,Part__Feature327,Part__Feature328,Part__Feature329]
  Origin = -> Origin060
  Placement = pos=(0,-11,10) rot=(0,0,1;4.71239rad)
FEATURE [Part::Feature] Part__Feature330  label="Molded Gear Housing (65 teeth) v1"
  Placement = pos=(3.86464e-05,0.999998,-5.83907e-05) rot=(0,1,0;0.174533rad)
  shape: bbox 44.93 x 8 x 36 mm, 32 faces (baked)
FEATURE [App::Part] Gearset
  Group = -> [Part__Feature330]
  Origin = -> Origin061
  Placement = pos=(-4.99878,-0.0204988,8.99678) rot=(0,0,1;0rad)
FEATURE [Part::Feature] Part__Feature331  label="97763A813"
  Placement = pos=(23.8159,-7.87333,-13.2382) rot=(0,0,1;0rad)
  shape: bbox 5.74 x 5.704 x 10.21 mm, 54 faces (baked)
FEATURE [Part::Feature] Part__Feature332  label="97763A814"
  Placement = pos=(-13.1841,-7.87333,-13.2382) rot=(0,0,1;0rad)
  shape: bbox 5.74 x 5.704 x 10.21 mm, 54 faces (baked)
FEATURE [Part::Feature] Part__Feature333  label="91239A118"
  Placement = pos=(-18.9977,-3.8705,-11.0457) rot=(1,0,0;1.5708rad)
  shape: bbox 5.74 x 16.21 x 5.704 mm, 78 faces (baked)
FEATURE [Part::Feature] Part__Feature334  label="91239A119"
  Placement = pos=(18.9472,-3.8705,10.8618) rot=(1,0,0;1.5708rad)
  shape: bbox 5.74 x 16.21 x 5.704 mm, 78 faces (baked)
FEATURE [Part::Feature] Part__Feature335  label="LatchShaft"
  Placement = pos=(6e-14,0.334091,4.4e-15) rot=(0,0,1;0rad)
  shape: bbox 3.247 x 16.3 x 3.247 mm, 5 faces (baked)
FEATURE [Part::Feature] Part__Feature336  label="FlyShaft2"
  Placement = pos=(-6.94558,17.8705,17.5268) rot=(0,1,0;2.35619rad)
  shape: bbox 4.33 x 16.3 x 4.33 mm, 5 faces (baked)
FEATURE [App::Part] Orbiter_8MM_GoblinHubs_V3_v3  label="Orbiter 8MM GoblinHubs V3 v3"
  Group = -> [Part__Feature336]
  Origin = -> Origin062
  Placement = pos=(-0.0187851,-17.8705,-0.08822) rot=(0,1,0;3.14159rad)
FEATURE [App::Part] Nuts_Bolts  label="Nuts&Bolts"
  Group = -> [Part__Feature331,Part__Feature332,Part__Feature333,Part__Feature334,Part__Feature335,Orbiter_8MM_GoblinHubs_V3_v3]
  Origin = -> Origin063
  Placement = pos=(-4.98,2.2e-14,9.085) rot=(0,0,1;0rad)
FEATURE [Part::Feature] Part__Feature337  label="Latch (1)"
  Placement = pos=(-0.237784,-28.72,13.9794) rot=(0.984808,0,-0.173648;3.14159rad)
  shape: bbox 12.13 x 16.63 x 42.56 mm, 95 faces (baked)
FEATURE [Part::Feature] Part__Feature338  label="HubHousing V5 With Logo"
  Placement = pos=(-4.99879,-0.0205009,8.99678) rot=(0,0,1;0rad)
  shape: bbox 51.47 x 23.51 x 39.31 mm, 428 faces (baked)
FEATURE [Part::Feature] Part__Feature339  label="Orbiter Spider Shaft v4"
  Placement = pos=(-4.99878,0.729501,8.99678) rot=(0,0,1;0rad)
  shape: bbox 7.95 x 22.5 x 7.95 mm, 4 faces (baked)
FEATURE [Part::Feature] Part__Feature340  label="_MR148ZZ Outer Ring"
  Placement = pos=(23.2795,0.0187843,-0.0882192) rot=(0,0,1;0rad)
  shape: bbox 4 x 15.15 x 15.15 mm, 12 faces (baked)
FEATURE [Part::Feature] Part__Feature341  label="_MR148ZZ Inner Ring"
  Placement = pos=(23.2795,0.0187843,-0.0882192) rot=(1,0,0;1.5708rad)
  shape: bbox 4 x 11.91 x 11.91 mm, 12 faces (baked)
FEATURE [Part::Feature] Part__Feature342  label="_MR148ZZ Shield1"
  Placement = pos=(23.8107,0.0187843,-0.0882192) rot=(0,0.707107,-0.707107;3.14159rad)
  shape: bbox 0.1992 x 12.8 x 12.8 mm, 4 faces (baked)
FEATURE [Part::Feature] Part__Feature343  label="_MR148ZZ Ball"
  Placement = pos=(25.2795,0.0187843,5.41178) rot=(1,0,0;1.5708rad)
  shape: bbox 1.8 x 1.8 x 1.8 mm, 1 faces (baked)
FEATURE [Part::Feature] Part__Feature344  label="_MR148ZZ Ball001"
  Placement = pos=(25.2795,-2.36758,4.86711) rot=(1,0,0;1.5708rad)
  shape: bbox 1.8 x 1.8 x 1.8 mm, 1 faces (baked)
FEATURE [Part::Feature] Part__Feature345  label="_MR148ZZ Ball002"
  Placement = pos=(25.2795,-4.28129,3.34097) rot=(1,0,0;1.5708rad)
  shape: bbox 1.8 x 1.8 x 1.8 mm, 1 faces (baked)
FEATURE [Part::Feature] Part__Feature346  label="_MR148ZZ Ball003"
  Placement = pos=(25.2795,-5.34332,1.13565) rot=(1,0,0;1.5708rad)
  shape: bbox 1.8 x 1.8 x 1.8 mm, 1 faces (baked)
FEATURE [Part::Feature] Part__Feature347  label="_MR148ZZ Ball004"
  Placement = pos=(25.2795,-5.34332,-1.31208) rot=(1,0,0;1.5708rad)
  shape: bbox 1.8 x 1.8 x 1.8 mm, 1 faces (baked)
FEATURE [Part::Feature] Part__Feature348  label="_MR148ZZ Ball005"
  Placement = pos=(25.2795,-4.28129,-3.51741) rot=(1,0,0;1.5708rad)
  shape: bbox 1.8 x 1.8 x 1.8 mm, 1 faces (baked)
FEATURE [Part::Feature] Part__Feature349  label="_MR148ZZ Ball006"
  Placement = pos=(25.2795,-2.36758,-5.04355) rot=(1,0,0;1.5708rad)
  shape: bbox 1.8 x 1.8 x 1.8 mm, 1 faces (baked)
FEATURE [Part::Feature] Part__Feature350  label="_MR148ZZ Ball007"
  Placement = pos=(25.2795,0.0187843,-5.58822) rot=(1,0,0;1.5708rad)
  shape: bbox 1.8 x 1.8 x 1.8 mm, 1 faces (baked)
FEATURE [Part::Feature] Part__Feature351  label="_MR148ZZ Ball008"
  Placement = pos=(25.2795,2.40514,-5.04355) rot=(1,0,0;1.5708rad)
  shape: bbox 1.8 x 1.8 x 1.8 mm, 1 faces (baked)
FEATURE [Part::Feature] Part__Feature352  label="_MR148ZZ Ball009"
  Placement = pos=(25.2795,4.31886,-3.51741) rot=(1,0,0;1.5708rad)
  shape: bbox 1.8 x 1.8 x 1.8 mm, 1 faces (baked)
FEATURE [Part::Feature] Part__Feature353  label="_MR148ZZ Ball010"
  Placement = pos=(25.2795,5.38089,-1.31208) rot=(1,0,0;1.5708rad)
  shape: bbox 1.8 x 1.8 x 1.8 mm, 1 faces (baked)
FEATURE [Part::Feature] Part__Feature354  label="_MR148ZZ Ball011"
  Placement = pos=(25.2795,5.38089,1.13565) rot=(1,0,0;1.5708rad)
  shape: bbox 1.8 x 1.8 x 1.8 mm, 1 faces (baked)
FEATURE [Part::Feature] Part__Feature355  label="_MR148ZZ Ball012"
  Placement = pos=(25.2795,4.31886,3.34097) rot=(1,0,0;1.5708rad)
  shape: bbox 1.8 x 1.8 x 1.8 mm, 1 faces (baked)
FEATURE [Part::Feature] Part__Feature356  label="_MR148ZZ Ball013"
  Placement = pos=(25.2795,2.40514,4.86711) rot=(1,0,0;1.5708rad)
  shape: bbox 1.8 x 1.8 x 1.8 mm, 1 faces (baked)
FEATURE [Part::Feature] Part__Feature357  label="_MR148ZZ Shield2"
  Placement = pos=(23.2795,0.0187843,-0.0882192) rot=(0,0,1;0rad)
  shape: bbox 0.1992 x 12.8 x 12.8 mm, 4 faces (baked)
FEATURE [App::Part] MR148ZZ_v2  label="MR148ZZ v2"
  Group = -> [Part__Feature340,Part__Feature341,Part__Feature342,Part__Feature343,Part__Feature344,Part__Feature345,Part__Feature346,Part__Feature347,Part__Feature348,Part__Feature349,Part__Feature350,Part__Feature351,Part__Feature352,Part__Feature353,Part__Feature354,Part__Feature355,Part__Feature356,Part__Feature357]
  Origin = -> Origin064
  Placement = pos=(1.055e-13,-44.1,6.7e-15) rot=(0,0,1;1.5708rad)
FEATURE [App::Part] Bearings
  Group = -> [MR148ZZ_v2]
  Origin = -> Origin065
  Placement = pos=(-4.98,-0.2,9.085) rot=(0,0,1;0rad)
FEATURE [Part::Feature] Part__Feature358  label="BrassCouplerRing"
  shape: bbox 8.7 x 8.7 x 3.8 mm, 10 faces (baked)
FEATURE [Part::Feature] Part__Feature359  label="Bowden Clip 1,75 v1"
  Placement = pos=(4.2e-15,-3.66e-14,3.8) rot=(0,0,1;0rad)
  shape: bbox 7.75 x 8.132 x 2.1 mm, 16 faces (baked)
FEATURE [Part::Feature] Part__Feature360  label="4mm Bowden Coupler v1"
  Placement = pos=(-1.28e-14,8.9e-15,5.8) rot=(1,0,0;3.14159rad)
  shape: bbox 6.917 x 6.917 x 6.567 mm, 63 faces (baked)
FEATURE [Part::Feature] Part__Feature361  label="4mm Bowden Coupler v002"
  Placement = pos=(-1.28e-14,8.9e-15,5.8) rot=(1,0,0;3.14159rad)
  shape: bbox 0.3 x 1.249 x 0.3 mm, 6 faces (baked)
FEATURE [Part::Feature] Part__Feature362  label="4mm Bowden Coupler v003"
  Placement = pos=(-1.28e-14,8.9e-15,5.8) rot=(1,0,0;3.14159rad)
  shape: bbox 1.249 x 0.3 x 0.3 mm, 6 faces (baked)
FEATURE [Part::Feature] Part__Feature363  label="4mm Bowden Coupler v004"
  Placement = pos=(-1.28e-14,8.9e-15,5.8) rot=(1,0,0;3.14159rad)
  shape: bbox 0.3 x 1.249 x 0.3 mm, 6 faces (baked)
FEATURE [Part::Feature] Part__Feature364  label="4mm Bowden Coupler v005"
  Placement = pos=(-1.28e-14,8.9e-15,5.8) rot=(1,0,0;3.14159rad)
  shape: bbox 1.249 x 0.3 x 0.3 mm, 6 faces (baked)
FEATURE [App::Part] _mm_Bowden_Coupler_v1  label="4mm Bowden Coupler v006"
  Group = -> [Part__Feature360,Part__Feature361,Part__Feature362,Part__Feature363,Part__Feature364]
  Origin = -> Origin066
FEATURE [App::Part] BrassCouplerRing_4mm_PFTE_v1  label="BrassCouplerRing 4mm PFTE v1"
  Group = -> [Part__Feature358,Part__Feature359,_mm_Bowden_Coupler_v1]
  Origin = -> Origin067
  Placement = pos=(1.33591,-7.87333,25.1967) rot=(0,0,1;0rad)
FEATURE [Part::Feature] Part__Feature365  label="T10 SpurGear"
  Placement = pos=(-0.00556044,0.0234153,3.8e-14) rot=(0,0,1;0.436332rad)
  shape: bbox 5.939 x 5.984 x 5.76 mm, 83 faces (baked)
FEATURE [Part::Feature] Part__Feature366  label="Component143"
  Placement = pos=(-6.58325,-20.8487,-3.5) rot=(0,0,-1;0.610865rad)
  shape: bbox 36.4 x 36.4 x 5.6 mm, 25 faces (baked)
FEATURE [Part::Feature] Part__Feature367  label="Component144"
  Placement = pos=(-1.23752,9.44492,2.66e-14) rot=(0,0,1;0.261799rad)
  shape: bbox 48.79 x 36.4 x 11 mm, 62 faces (baked)
FEATURE [Part::Feature] Part__Feature368  label="Component145"
  Placement = pos=(27.2578,27.4813,-0.35) rot=(0,0,-1;0.610865rad)
  shape: bbox 37.82 x 37.86 x 0.4018 mm, 26 faces (baked)
FEATURE [Part::Feature] Part__Feature369  label="Component146"
  Placement = pos=(27.2578,27.4813,-0.35) rot=(0,0,-1;0.610865rad)
  shape: bbox 37.82 x 37.86 x 0.5018 mm, 38 faces (baked)
FEATURE [Part::Feature] Part__Feature370  label="Component147"
  Placement = pos=(27.2578,27.4813,-0.35) rot=(0,0,-1;0.610865rad)
  shape: bbox 37.82 x 37.86 x 0.5018 mm, 38 faces (baked)
FEATURE [Part::Feature] Part__Feature371  label="Component148"
  Placement = pos=(27.2578,27.4813,-0.35) rot=(0,0,-1;0.610865rad)
  shape: bbox 37.82 x 37.86 x 0.5018 mm, 38 faces (baked)
FEATURE [Part::Feature] Part__Feature372  label="Component149"
  Placement = pos=(27.2578,27.4813,-0.35) rot=(0,0,-1;0.610865rad)
  shape: bbox 37.82 x 37.86 x 0.5018 mm, 38 faces (baked)
FEATURE [Part::Feature] Part__Feature373  label="Component150"
  Placement = pos=(27.2578,27.4813,-0.35) rot=(0,0,-1;0.610865rad)
  shape: bbox 37.82 x 37.86 x 0.5018 mm, 38 faces (baked)
FEATURE [Part::Feature] Part__Feature374  label="Component151"
  Placement = pos=(27.2578,27.4813,-0.35) rot=(0,0,-1;0.610865rad)
  shape: bbox 37.82 x 37.86 x 0.5018 mm, 38 faces (baked)
FEATURE [Part::Feature] Part__Feature375  label="Component152"
  Placement = pos=(27.2578,27.4813,-0.35) rot=(0,0,-1;0.610865rad)
  shape: bbox 37.82 x 37.86 x 0.5018 mm, 38 faces (baked)
FEATURE [Part::Feature] Part__Feature376  label="Component153"
  Placement = pos=(27.2578,27.4813,-0.35) rot=(0,0,-1;0.610865rad)
  shape: bbox 37.82 x 37.86 x 0.5018 mm, 38 faces (baked)
FEATURE [Part::Feature] Part__Feature377  label="Component154"
  Placement = pos=(27.2578,27.4813,-0.35) rot=(0,0,-1;0.610865rad)
  shape: bbox 37.82 x 37.86 x 0.5018 mm, 38 faces (baked)
FEATURE [Part::Feature] Part__Feature378  label="Component155"
  Placement = pos=(27.2578,27.4813,-0.35) rot=(0,0,-1;0.610865rad)
  shape: bbox 37.82 x 37.86 x 0.5018 mm, 38 faces (baked)
FEATURE [Part::Feature] Part__Feature379  label="Component156"
  Placement = pos=(27.2578,27.4813,-0.35) rot=(0,0,-1;0.610865rad)
  shape: bbox 37.82 x 37.86 x 0.5018 mm, 38 faces (baked)
FEATURE [Part::Feature] Part__Feature380  label="Component157"
  Placement = pos=(27.2578,27.4813,-0.35) rot=(0,0,-1;0.610865rad)
  shape: bbox 37.82 x 37.86 x 0.5018 mm, 38 faces (baked)
FEATURE [Part::Feature] Part__Feature381  label="Component158"
  Placement = pos=(-36.4,1.49073e-07,-23.75) rot=(0,0,-1;0.349066rad)
  shape: bbox 7.395 x 6.348 x 3.4 mm, 59 faces (baked)
FEATURE [Part::Feature] Part__Feature382  label="Component159"
  Placement = pos=(27.2578,27.4813,1.65) rot=(0,0,-1;0.610865rad)
  shape: bbox 37.82 x 37.86 x 0.5018 mm, 38 faces (baked)
FEATURE [Part::Feature] Part__Feature383  label="Component160"
  Placement = pos=(27.2578,27.4813,1.65) rot=(0,0,-1;0.610865rad)
  shape: bbox 37.82 x 37.86 x 0.5018 mm, 38 faces (baked)
FEATURE [Part::Feature] Part__Feature384  label="Component161"
  Placement = pos=(27.2578,27.4813,1.65) rot=(0,0,-1;0.610865rad)
  shape: bbox 37.82 x 37.86 x 0.5018 mm, 38 faces (baked)
FEATURE [Part::Feature] Part__Feature385  label="Component162"
  Placement = pos=(27.2578,27.4813,1.65) rot=(0,0,-1;0.610865rad)
  shape: bbox 37.82 x 37.86 x 0.5018 mm, 38 faces (baked)
FEATURE [App::Part] LDO_Stepper__1_  label="LDO Stepper (1)"
  Group = -> [Part__Feature366,Part__Feature367,Part__Feature368,Part__Feature369,Part__Feature370,Part__Feature371,Part__Feature372,Part__Feature373,Part__Feature374,Part__Feature375,Part__Feature376,Part__Feature377,Part__Feature378,Part__Feature379,Part__Feature380,Part__Feature381,Part__Feature382,Part__Feature383,Part__Feature384,Part__Feature385]
  Origin = -> Origin068
  Placement = pos=(34.2048,12.4495,25.75) rot=(0,0,1;0.349066rad)
FEATURE [App::Part] LDO_36STH17_1004AHG_v6  label="LDO_36STH17-1004AHG v6"
  Group = -> [Part__Feature365,LDO_Stepper__1_]
  Origin = -> Origin069
  Placement = pos=(-4.98437,2.4795,9.03861) rot=(-0.913318,-0.287968,-0.287968;1.66134rad)
FEATURE [Part::Feature] Part__Feature386  label="92125A138"
  Placement = pos=(0.540241,17.1797,0) rot=(-1,0,0;1.5708rad)
  shape: bbox 3.468 x 24.34 x 3.004 mm, 55 faces (baked)
FEATURE [Part::Feature] Part__Feature387  label="KnurledNut"
  Placement = pos=(4.4e-15,-2,-4.4e-15) rot=(0,0,1;0rad)
  shape: bbox 11.81 x 5.058 x 11.81 mm, 332 faces (baked)
FEATURE [Part::Feature] Part__Feature388  label="90940A412"
  Placement = pos=(211.065,-54.1981,54.7898) rot=(1,0,0;1.5708rad)
  shape: bbox 8 x 1 x 8 mm, 4 faces (baked)
FEATURE [Part::Feature] Part__Feature389  label="Spring v1"
  Placement = pos=(-0.357931,-5.805,0.459437) rot=(0,0,1;0rad)
  shape: bbox 7.654 x 10.57 x 7.513 mm, 3 faces (baked)
FEATURE [App::Part] Sping
  Group = -> [Part__Feature388,Part__Feature389]
  Origin = -> Origin070
  Placement = pos=(-210.525,-51.9859,54.7898) rot=(1,0,0;3.14159rad)
FEATURE [App::Part] Orbiter_2_7_LDO_Molding_CaptiveTensioner_v10_v1  label="Orbiter 2.7 LDO Molding_CaptiveTensioner v10 v1"
  Group = -> [Part__Feature386,Part__Feature387,Sping]
  Origin = -> Origin071
  Placement = pos=(13.3078,-11.37,19.6564) rot=(0.57735,0.57735,0.57735;4.18879rad)
FEATURE [App::Part] Orbiter_V2_0_Mockup  label="Orbiter V2.0 Mockup"
  Group = -> [Gearset,Nuts_Bolts,Part__Feature337,Part__Feature338,Part__Feature339,Bearings,BrassCouplerRing_4mm_PFTE_v1,LDO_36STH17_1004AHG_v6,Orbiter_2_7_LDO_Molding_CaptiveTensioner_v10_v1]
  Origin = -> Origin072
  Placement = pos=(-2.7734,0.0179123,-4.619e-13) rot=(0,0,1;0rad)
FEATURE [App::Part] Orbiter_v2_0_mockup_v7  label="Orbiter v2.0 mockup v7"
  Group = -> [Orbiter_V2_0_Mockup]
  Origin = -> Origin073
  Placement = pos=(1.44,126.86,245.3) rot=(0,0,1;0rad)
FEATURE [Sketcher::SketchObject] Sketch108
  ArcFitTolerance = 1e-06
  AttachmentSupport = -> [YZ_Plane074]
  FullyConstrained = true
  MakeInternals = false
  MapMode = 5
  Placement = pos=(0,0,0) rot=(0.57735,0.57735,0.57735;2.0944rad)
  sketch-geometry (6):
    g0: LineSegment StartX=106 StartY=198.8 StartZ=0 EndX=106 EndY=205.8 EndZ=0
    g1: LineSegment StartX=106 StartY=205.8 StartZ=0 EndX=126 EndY=205.8 EndZ=0
    g2: LineSegment StartX=126 StartY=205.8 StartZ=0 EndX=126 EndY=224.8 EndZ=0
    g3: LineSegment StartX=126 StartY=224.8 StartZ=0 EndX=132 EndY=224.8 EndZ=0
    g4: LineSegment StartX=132 StartY=224.8 StartZ=0 EndX=132 EndY=198.8 EndZ=0
    g5: LineSegment StartX=132 StartY=198.8 StartZ=0 EndX=106 EndY=198.8 EndZ=0
  constraints (18):
    c: Distance(g0) = 7
    c: Vertical(g0)
    c: Coincident(g1,g0)
    c: Horizontal(g1)
    c: Coincident(g2,g1)
    c: Vertical(g2)
    c: Coincident(g3,g2)
    c: Coincident(g4,g3)
    c: Vertical(g4)
    c: Coincident(g5,g4)
    c: Coincident(g5,g0)
    c: Horizontal(g5)
    c: Horizontal(g3)
    c: DistanceX(g1,g1) = 20
    c: DistanceY(g2,g2) = 19
    c: DistanceX(g3,g3) = 6
    c: DistanceY(g-1,g4) = 198.8
    c: DistanceX(g-1,g0) = 106
FEATURE [PartDesign::Pad] Pad038
  Direction = (1,0,0)
  Length = 10
  Length2 = 10
  Placement = pos=(0,0,0) rot=(1,1,1;2.0944rad)
  Profile = -> Sketch108
  ReferenceAxis = -> Sketch108 [N_Axis]
  Suppressed = false
  Type = 0
FEATURE [Sketcher::SketchObject] Sketch109
  ArcFitTolerance = 1e-06
  AttachmentSupport = -> [Pad038]
  FullyConstrained = true
  MakeInternals = false
  MapMode = 5
  Placement = pos=(0,4.37e-14,198.8) rot=(0.707107,0.707107,0;3.14159rad)
  sketch-geometry (3):
    g0: Circle CenterX=128 CenterY=5 CenterZ=0 NormalX=0 NormalY=0 NormalZ=1 AngleXU=0 Radius=2.3
    g1: Circle CenterX=110 CenterY=5 CenterZ=0 NormalX=0 NormalY=0 NormalZ=1 AngleXU=0 Radius=2.3
    g2: LineSegment [constr] StartX=128 StartY=5 StartZ=0 EndX=110 EndY=5 EndZ=0
  constraints (8):
    c: Diameter(g0) = 4.6
    c: Equal(g1,g0)
    c: Coincident(g2,g0)
    c: Coincident(g2,g1)
    c: Horizontal(g2)
    c: DistanceX(g2,g2) = -18
    c: DistanceX(g1,g-1) = -110
    c: DistanceY(g-1,g1) = 5
FEATURE [PartDesign::Pocket] Pocket034
  BaseFeature = -> Pad038
  Direction = (0,0,1)
  Length = 5.5
  Length2 = 5
  Placement = pos=(0,0,0) rot=(1,1,1;2.0944rad)
  Profile = -> Sketch109
  ReferenceAxis = -> Sketch109 [N_Axis]
  Suppressed = false
  Type = 0
FEATURE [Sketcher::SketchObject] Sketch110
  ArcFitTolerance = 1e-06
  AttachmentSupport = -> [Pocket034]
  FullyConstrained = true
  MakeInternals = false
  MapMode = 5
  Placement = pos=(2.77e-14,126,0) rot=(0.57735,0.57735,-0.57735;2.0944rad)
  sketch-geometry (3):
    g0: Circle CenterX=-220 CenterY=5 CenterZ=0 NormalX=0 NormalY=0 NormalZ=1 AngleXU=0 Radius=1.5
    g1: Circle CenterX=-210 CenterY=5 CenterZ=0 NormalX=0 NormalY=0 NormalZ=1 AngleXU=0 Radius=1.5
    g2: LineSegment [constr] StartX=-220 StartY=5 StartZ=0 EndX=-210 EndY=5 EndZ=0
  constraints (8):
    c: Diameter(g0) = 3
    c: Equal(g1,g0)
    c: Coincident(g2,g0)
    c: Coincident(g2,g1)
    c: Horizontal(g2)
    c: DistanceX(g2,g2) = 10
    c: DistanceX(g1,g-1) = 210
    c: DistanceY(g-1,g1) = 5
FEATURE [PartDesign::Hole] Hole021
  BaseFeature = -> Pocket034
  CustomThreadClearance = 0
  Depth = 25
  DepthType = 0
  Diameter = 3.4
  DrillForDepth = false
  DrillPoint = 1
  DrillPointAngle = 118
  HoleCutCountersinkAngle = 90
  HoleCutCustomValues = false
  HoleCutDepth = 0
  HoleCutDiameter = 6.1
  HoleCutType = 0
  ModelThread = false
  Placement = pos=(0,0,0) rot=(1,1,1;2.0944rad)
  Profile = -> Sketch110
  Suppressed = false
  Tapered = false
  TaperedAngle = 90
  ThreadClass = 0
  ThreadDepth = 25
  ThreadDepthType = 0
  ThreadDirection = 0
  ThreadFit = 0
  ThreadSize = 9
  ThreadType = 1
  Threaded = false
  UseCustomThreadClearance = false
FEATURE [PartDesign::Body] Body015  label="BLTHolder"
  AllowCompound = false
  Group = -> [Sketch108,Pad038,Sketch109,Pocket034,Sketch110,Hole021]
  Origin = -> Origin074
  Placement = pos=(-39,0,0) rot=(0,0,1;0rad)
  Tip = -> Hole021
FEATURE [Sketcher::SketchObject] Sketch111
  ArcFitTolerance = 1e-06
  AttachmentSupport = -> [YZ_Plane075]
  FullyConstrained = true
  MakeInternals = false
  MapMode = 5
  Placement = pos=(0,0,0) rot=(0.57735,0.57735,0.57735;2.0944rad)
  sketch-geometry (6):
    g0: LineSegment StartX=106 StartY=235 StartZ=0 EndX=132 EndY=235 EndZ=0
    g1: LineSegment StartX=132 StartY=235 StartZ=0 EndX=132 EndY=218 EndZ=0
    g2: LineSegment StartX=132 StartY=218 StartZ=0 EndX=126 EndY=218 EndZ=0
    g3: LineSegment StartX=126 StartY=218 StartZ=0 EndX=126 EndY=228 EndZ=0
    g4: LineSegment StartX=126 StartY=228 StartZ=0 EndX=106 EndY=228 EndZ=0
    g5: LineSegment StartX=106 StartY=228 StartZ=0 EndX=106 EndY=235 EndZ=0
  constraints (18):
    c: Horizontal(g0)
    c: Coincident(g1,g0)
    c: Vertical(g1)
    c: Coincident(g2,g1)
    c: Horizontal(g2)
    c: Coincident(g3,g2)
    c: Vertical(g3)
    c: Coincident(g4,g3)
    c: Horizontal(g4)
    c: Coincident(g5,g4)
    c: Coincident(g5,g0)
    c: Vertical(g5)
    c: DistanceY(g5,g5) = 7
    c: DistanceX(g2,g2) = 6
    c: DistanceY(g3,g3) = 10
    c: DistanceX(g4,g4) = 20
    c: DistanceY(g-1,g0) = 235
    c: DistanceX(g-1,g0) = 132
FEATURE [PartDesign::Pad] Pad039
  Direction = (1,0,0)
  Length = 50
  Length2 = 10
  Placement = pos=(0,0,0) rot=(1,1,1;2.0944rad)
  Profile = -> Sketch111
  ReferenceAxis = -> Sketch111 [N_Axis]
  Suppressed = false
  Type = 0
FEATURE [Sketcher::SketchObject] Sketch112
  ArcFitTolerance = 1e-06
  AttachmentSupport = -> [XZ_Plane075]
  FullyConstrained = true
  MakeInternals = false
  MapMode = 5
  Placement = pos=(0,0,0) rot=(1,0,0;1.5708rad)
  sketch-geometry (9):
    g0: LineSegment StartX=20 StartY=218 StartZ=0 EndX=0 EndY=218 EndZ=0
    g1: LineSegment StartX=0 StartY=228 StartZ=0 EndX=0 EndY=218 EndZ=0
    g2: LineSegment [constr] StartX=25 StartY=210 StartZ=0 EndX=25 EndY=230 EndZ=0
    g3: LineSegment StartX=0 StartY=228 StartZ=0 EndX=6 EndY=228 EndZ=0
    g4: LineSegment StartX=6 StartY=228 StartZ=0 EndX=20 EndY=218 EndZ=0
    g5: LineSegment StartX=30 StartY=218 StartZ=0 EndX=50 EndY=218 EndZ=0
    g6: LineSegment StartX=50 StartY=228 StartZ=0 EndX=50 EndY=218 EndZ=0
    g7: LineSegment StartX=50 StartY=228 StartZ=0 EndX=44 EndY=228 EndZ=0
    g8: LineSegment StartX=44 StartY=228 StartZ=0 EndX=30 EndY=218 EndZ=0
  constraints (24):
    c: PointOnObject(g0,g-2)
    c: Horizontal(g0)
    c: Coincident(g1,g0)
    c: Vertical(g1)
    c: DistanceX(g0,g0) = 20
    c: DistanceY(g1,g1) = 10
    c: DistanceY(g-1,g0) = 218
    c: Vertical(g2)
    c: DistanceY(g2,g2) = 20
    c: DistanceX(g-1,g2) = 25
    c: DistanceY(g-1,g2) = 210
    c: Coincident(g3,g1)
    c: Coincident(g4,g3)
    c: Coincident(g4,g0)
    c: Horizontal(g3)
    c: DistanceX(g3,g3) = 6
    c: Symmetric(g0,g5,g2)
    c: Symmetric(g0,g5,g2)
    c: Symmetric(g1,g6,g2)
    c: Symmetric(g1,g6,g2)
    c: Symmetric(g3,g7,g2)
    c: Symmetric(g3,g7,g2)
    c: Symmetric(g4,g8,g2)
    c: Symmetric(g4,g8,g2)
FEATURE [PartDesign::Pocket] Pocket035
  BaseFeature = -> Pad039
  Direction = (0,1,-2e-16)
  Length = 5
  Length2 = 5
  Placement = pos=(0,0,0) rot=(1,1,1;2.0944rad)
  Profile = -> Sketch112
  ReferenceAxis = -> Sketch112 [N_Axis]
  Suppressed = false
  Type = 1
FEATURE [Sketcher::SketchObject] Sketch113
  ArcFitTolerance = 1e-06
  AttachmentSupport = -> [Pocket035]
  FullyConstrained = true
  MakeInternals = false
  MapMode = 5
  Placement = pos=(0,5.17e-14,235) rot=(0,0,-1;1.5708rad)
  sketch-geometry (3):
    g0: Circle CenterX=-119 CenterY=42.5 CenterZ=0 NormalX=0 NormalY=0 NormalZ=1 AngleXU=0 Radius=2.3
    g1: Circle CenterX=-119 CenterY=5.5 CenterZ=0 NormalX=0 NormalY=0 NormalZ=1 AngleXU=0 Radius=2.3
    g2: LineSegment [constr] StartX=-119 StartY=5.5 StartZ=0 EndX=-119 EndY=42.5 EndZ=0
  constraints (8):
    c: Diameter(g0) = 4.6
    c: Equal(g1,g0)
    c: Coincident(g2,g1)
    c: Coincident(g2,g0)
    c: Vertical(g2)
    c: DistanceY(g2,g2) = 37
    c: DistanceY(g-1,g1) = 5.5
    c: DistanceX(g1,g-1) = 119
FEATURE [PartDesign::Pocket] Pocket036
  BaseFeature = -> Pocket035
  Direction = (0,0,-1)
  Length = 5.5
  Length2 = 5
  Placement = pos=(0,0,0) rot=(1,1,1;2.0944rad)
  Profile = -> Sketch113
  ReferenceAxis = -> Sketch113 [N_Axis]
  Suppressed = false
  Type = 0
FEATURE [Sketcher::SketchObject] Sketch114
  ArcFitTolerance = 1e-06
  AttachmentSupport = -> [Pocket036]
  FullyConstrained = true
  MakeInternals = false
  MapMode = 5
  Placement = pos=(2.77e-14,126,0) rot=(0.57735,0.57735,-0.57735;2.0944rad)
  sketch-geometry (3):
    g0: Circle CenterX=-224.5 CenterY=32.5 CenterZ=0 NormalX=0 NormalY=0 NormalZ=1 AngleXU=0 Radius=1.5
    g1: Circle CenterX=-224.5 CenterY=17.5 CenterZ=0 NormalX=0 NormalY=0 NormalZ=1 AngleXU=0 Radius=1.5
    g2: LineSegment [constr] StartX=-224.5 StartY=32.5 StartZ=0 EndX=-224.5 EndY=17.5 EndZ=0
  constraints (8):
    c: Diameter(g1) = 3
    c: Equal(g0,g1)
    c: Coincident(g2,g0)
    c: Coincident(g2,g1)
    c: Vertical(g2)
    c: DistanceY(g2,g2) = 15
    c: DistanceX(g0,g-1) = 224.5
    c: DistanceY(g-1,g1) = 17.5
FEATURE [PartDesign::Hole] Hole022
  BaseFeature = -> Pocket036
  CustomThreadClearance = 0
  Depth = 25
  DepthType = 0
  Diameter = 3.4
  DrillForDepth = false
  DrillPoint = 1
  DrillPointAngle = 118
  HoleCutCountersinkAngle = 90
  HoleCutCustomValues = false
  HoleCutDepth = 0
  HoleCutDiameter = 6.1
  HoleCutType = 0
  ModelThread = false
  Placement = pos=(0,0,0) rot=(1,1,1;2.0944rad)
  Profile = -> Sketch114
  Suppressed = false
  Tapered = false
  TaperedAngle = 90
  ThreadClass = 0
  ThreadDepth = 25
  ThreadDepthType = 0
  ThreadDirection = 0
  ThreadFit = 0
  ThreadSize = 9
  ThreadType = 1
  Threaded = false
  UseCustomThreadClearance = false
FEATURE [Sketcher::SketchObject] Sketch115
  ArcFitTolerance = 1e-06
  AttachmentSupport = -> [Hole022]
  FullyConstrained = true
  MakeInternals = false
  MapMode = 5
  Placement = pos=(0,5.17e-14,235) rot=(0,0,-1;1.5708rad)
  sketch-geometry (1):
    g0: Circle CenterX=-119 CenterY=25 CenterZ=0 NormalX=0 NormalY=0 NormalZ=1 AngleXU=0 Radius=2.5
  constraints (3):
    c: Diameter(g0) = 5
    c: DistanceX(g0,g-1) = 119
    c: DistanceY(g-1,g0) = 25
FEATURE [PartDesign::Pocket] Pocket037
  BaseFeature = -> Hole022
  Direction = (1.1e-15,0,-1)
  Length = 5
  Length2 = 5
  Placement = pos=(0,0,0) rot=(1,1,1;2.0944rad)
  Profile = -> Sketch115
  ReferenceAxis = -> Sketch115 [N_Axis]
  Suppressed = false
  Type = 1
FEATURE [PartDesign::Body] Body016  label="OrbiterHolder"
  AllowCompound = false
  Group = -> [Sketch111,Pad039,Sketch112,Pocket035,Sketch113,Pocket036,Sketch114,Hole022,Sketch115,Pocket037]
  Origin = -> Origin075
  Placement = pos=(-25,0,0) rot=(0,0,1;0rad)
  Tip = -> Pocket037
FEATURE [Sketcher::SketchObject] Sketch116
  ArcFitTolerance = 1e-06
  AttachmentSupport = -> [XZ_Plane076]
  FullyConstrained = true
  MakeInternals = false
  MapMode = 5
  Placement = pos=(0,0,0) rot=(1,0,0;1.5708rad)
  sketch-geometry (6):
    g0: LineSegment StartX=28 StartY=211.5 StartZ=0 EndX=43 EndY=211.5 EndZ=0
    g1: LineSegment StartX=43 StartY=211.5 StartZ=0 EndX=43 EndY=189.985 EndZ=0
    g2: LineSegment StartX=43 StartY=189.985 StartZ=0 EndX=53.4558 EndY=179.529 EndZ=0
    g3: LineSegment StartX=53.4558 StartY=179.529 StartZ=0 EndX=49.2132 EndY=175.287 EndZ=0
    g4: LineSegment StartX=49.2132 StartY=175.287 StartZ=0 EndX=28 EndY=196.5 EndZ=0
    g5: LineSegment StartX=28 StartY=196.5 StartZ=0 EndX=28 EndY=211.5 EndZ=0
  constraints (18):
    c: Horizontal(g0)
    c: Coincident(g1,g0)
    c: Vertical(g1)
    c: Coincident(g2,g1)
    c: Coincident(g3,g2)
    c: Coincident(g4,g3)
    c: Coincident(g5,g4)
    c: Coincident(g5,g0)
    c: Vertical(g5)
    c: Angle(g2,g1) = 2.35619
    c: Angle(g4,g5) = 2.35619
    c: Perpendicular(g2,g3)
    c: Distance(g4,g4) = 30
    c: Distance(g3,g3) = 6
    c: DistanceY(g5,g5) = 15
    c: DistanceX(g0,g0) = 15
    c: DistanceX(g-1,g0) = 28
    c: DistanceY(g-1,g4) = 196.5
FEATURE [PartDesign::Pad] Pad040
  Direction = (0,-1,2e-16)
  Length = 6
  Length2 = 10
  Placement = pos=(0,0,0) rot=(1,0,0;1.5708rad)
  Profile = -> Sketch116
  ReferenceAxis = -> Sketch116 [N_Axis]
  Suppressed = false
  Type = 0
FEATURE [Sketcher::SketchObject] Sketch117
  ArcFitTolerance = 1e-06
  AttachmentSupport = -> [Pad040]
  FullyConstrained = true
  MakeInternals = false
  MapMode = 5
  Placement = pos=(0,-6,1.3e-15) rot=(1,0,0;1.5708rad)
  sketch-geometry (4):
    g0: LineSegment StartX=28 StartY=196.5 StartZ=0 EndX=49.2132 EndY=175.287 EndZ=0
    g1: LineSegment StartX=49.2132 StartY=175.287 StartZ=0 EndX=53.4558 EndY=179.529 EndZ=0
    g2: LineSegment StartX=53.4558 StartY=179.529 StartZ=0 EndX=32.2426 EndY=200.743 EndZ=0
    g3: LineSegment StartX=32.2426 StartY=200.743 StartZ=0 EndX=28 EndY=196.5 EndZ=0
  constraints (12):
    c: Coincident(g0,g1)
    c: Coincident(g1,g2)
    c: Coincident(g2,g3)
    c: Coincident(g3,g0)
    c: Parallel(g0,g2)
    c: Parallel(g1,g3)
    c: Distance(g3,g3) = 6
    c: Distance(g2,g2) = 30
    c: Distance(g0,g-2) = 28
    c: DistanceY(g-1,g0) = 196.5
    c: Perpendicular(g1,g0)
    c: Angle(g-2,g3) = 2.35619
FEATURE [PartDesign::Pad] Pad041
  BaseFeature = -> Pad040
  Direction = (0,-1,2e-16)
  Length = 30
  Length2 = 10
  Placement = pos=(0,0,0) rot=(1,0,0;1.5708rad)
  Profile = -> Sketch117
  ReferenceAxis = -> Sketch117 [N_Axis]
  Suppressed = false
  Type = 0
FEATURE [Sketcher::SketchObject] Sketch118
  ArcFitTolerance = 1e-06
  AttachmentSupport = -> [Pad041]
  FullyConstrained = false
  MakeInternals = false
  MapMode = 5
  Placement = pos=(116.493,5.11e-14,116.493) rot=(0.382683,0,0.92388;3.14159rad)
  sketch-geometry (1):
    g0: Circle CenterX=104.206 CenterY=21 CenterZ=0 NormalX=0 NormalY=0 NormalZ=1 AngleXU=0 Radius=14
  constraints (2):
    c: Diameter(g0) = 28
    c: DistanceY(g-1,g0) = 21
FEATURE [PartDesign::Pocket] Pocket038
  BaseFeature = -> Pad041
  Direction = (-0.707107,0,-0.707107)
  Length = 5
  Length2 = 5
  Placement = pos=(0,0,0) rot=(1,0,0;1.5708rad)
  Profile = -> Sketch118
  ReferenceAxis = -> Sketch118 [N_Axis]
  Suppressed = false
  Type = 1
FEATURE [Sketcher::SketchObject] Sketch119
  ArcFitTolerance = 1e-06
  AttachmentSupport = -> [Pocket038]
  FullyConstrained = true
  MakeInternals = false
  MapMode = 5
  Placement = pos=(116.493,5.11e-14,116.493) rot=(0.382683,0,0.92388;3.14159rad)
  sketch-geometry (8):
    g0: Circle CenterX=92.3 CenterY=33 CenterZ=0 NormalX=0 NormalY=0 NormalZ=1 AngleXU=0 Radius=1.5
    g1: Circle CenterX=116.3 CenterY=33 CenterZ=0 NormalX=0 NormalY=0 NormalZ=1 AngleXU=0 Radius=1.5
    g2: Circle CenterX=92.3 CenterY=9 CenterZ=0 NormalX=0 NormalY=0 NormalZ=1 AngleXU=0 Radius=1.5
    g3: Circle CenterX=116.3 CenterY=9 CenterZ=0 NormalX=0 NormalY=0 NormalZ=1 AngleXU=0 Radius=1.5
    g4: LineSegment [constr] StartX=92.3 StartY=33 StartZ=0 EndX=92.3 EndY=9 EndZ=0
    g5: LineSegment [constr] StartX=92.3 StartY=9 StartZ=0 EndX=116.3 EndY=9 EndZ=0
    g6: LineSegment [constr] StartX=116.3 StartY=9 StartZ=0 EndX=116.3 EndY=33 EndZ=0
    g7: LineSegment [constr] StartX=116.3 StartY=33 StartZ=0 EndX=92.3 EndY=33 EndZ=0
  constraints (20):
    c: Diameter(g0) = 3
    c: Equal(g0,g2)
    c: Equal(g2,g3)
    c: Equal(g3,g1)
    c: Coincident(g4,g5)
    c: Coincident(g5,g6)
    c: Coincident(g6,g7)
    c: Coincident(g7,g4)
    c: Vertical(g4)
    c: Vertical(g6)
    c: Horizontal(g5)
    c: Horizontal(g7)
    c: Coincident(g4,g0)
    c: Coincident(g5,g3)
    c: DistanceX(g7,g7) = 24
    c: DistanceY(g4,g4) = 24
    c: Coincident(g2,g4)
    c: Coincident(g1,g6)
    c: DistanceY(g-1,g3) = 9
    c: DistanceX(g-1,g0) = 92.3
FEATURE [PartDesign::Hole] Hole023
  BaseFeature = -> Pocket038
  CustomThreadClearance = 0
  Depth = 25
  DepthType = 0
  Diameter = 3.4
  DrillForDepth = false
  DrillPoint = 1
  DrillPointAngle = 118
  HoleCutCountersinkAngle = 90
  HoleCutCustomValues = false
  HoleCutDepth = 0
  HoleCutDiameter = 6.1
  HoleCutType = 0
  ModelThread = false
  Placement = pos=(0,0,0) rot=(1,0,0;1.5708rad)
  Profile = -> Sketch119
  Suppressed = false
  Tapered = false
  TaperedAngle = 90
  ThreadClass = 0
  ThreadDepth = 25
  ThreadDepthType = 0
  ThreadDirection = 0
  ThreadFit = 0
  ThreadSize = 9
  ThreadType = 1
  Threaded = false
  UseCustomThreadClearance = false
FEATURE [Sketcher::SketchObject] Sketch120
  ArcFitTolerance = 1e-06
  AttachmentSupport = -> [Hole023]
  FullyConstrained = true
  MakeInternals = false
  MapMode = 5
  Placement = pos=(0,-6,1.3e-15) rot=(1,0,0;1.5708rad)
  sketch-geometry (3):
    g0: Circle CenterX=30.5 CenterY=209 CenterZ=0 NormalX=0 NormalY=0 NormalZ=1 AngleXU=0 Radius=1.5
    g1: Circle CenterX=40.5 CenterY=199 CenterZ=0 NormalX=0 NormalY=0 NormalZ=1 AngleXU=0 Radius=1.5
    g2: LineSegment [constr] StartX=30.5 StartY=209 StartZ=0 EndX=40.5 EndY=199 EndZ=0
  constraints (8):
    c: Diameter(g0) = 3
    c: Equal(g1,g0)
    c: Coincident(g2,g0)
    c: Coincident(g2,g1)
    c: Angle(g-2,g2) = 0.785398
    c: DistanceX(g0,g1) = 10
    c: DistanceX(g-1,g0) = 30.5
    c: DistanceY(g-1,g0) = 209
FEATURE [PartDesign::Hole] Hole024
  BaseFeature = -> Hole023
  CustomThreadClearance = 0
  Depth = 25
  DepthType = 0
  Diameter = 3.4
  DrillForDepth = false
  DrillPoint = 1
  DrillPointAngle = 118
  HoleCutCountersinkAngle = 90
  HoleCutCustomValues = false
  HoleCutDepth = 0
  HoleCutDiameter = 6.1
  HoleCutType = 0
  ModelThread = false
  Placement = pos=(0,0,0) rot=(1,0,0;1.5708rad)
  Profile = -> Sketch120
  Suppressed = false
  Tapered = false
  TaperedAngle = 90
  ThreadClass = 0
  ThreadDepth = 25
  ThreadDepthType = 0
  ThreadDirection = 0
  ThreadFit = 0
  ThreadSize = 9
  ThreadType = 1
  Threaded = false
  UseCustomThreadClearance = false
FEATURE [PartDesign::Body] Body017  label="CoolingFanHolder"
  AllowCompound = false
  Group = -> [Sketch116,Pad040,Sketch117,Pad041,Sketch118,Pocket038,Sketch119,Hole023,Sketch120,Hole024]
  Origin = -> Origin076
  Placement = pos=(0,132,0) rot=(0,0,1;0rad)
  Tip = -> Hole024
FEATURE [Part::FeaturePython] Screw032  label="M5x10-Screw"  # WARN: FeaturePython — macro-defined, semantics opaque (R4)
  BaseObject = -> Cut [Edge41]
  Diameter = 3
  Invert = true
  LeftHanded = false
  Length = 1
  LengthCustom = 10
  MatchOuter = false
  OffsetAngle = 0
  Placement = pos=(-20,132,180) rot=(1,0,0;1.5708rad)
  Thread = false
  Type = 85
FEATURE [Part::FeaturePython] Screw033  label="M5x10-Screw001"  # WARN: FeaturePython — macro-defined, semantics opaque (R4)
  BaseObject = -> Cut [Edge52]
  Diameter = 3
  Invert = true
  LeftHanded = false
  Length = 1
  LengthCustom = 10
  MatchOuter = false
  OffsetAngle = 0
  Placement = pos=(20,132,180) rot=(1,0,0;1.5708rad)
  Thread = false
  Type = 85
FEATURE [App::Part] Part007  label="ExtruderAssembly"
  Group = -> [Screw033,Screw032,Part008,Wheel__V_slot_Rail_625_2Z_Bearing_v008,Wheel__V_slot_Rail_625_2Z_Bearing_v009,Wheel__V_slot_Rail_625_2Z_Bearing_v010,Wheel__V_slot_Rail_625_2Z_Bearing_v011,Body010,Body008,PathArray001,Part__Mirroring,Fusion001,Cut,Body012,Body013,Body014,Orbiter_v2_0_mockup_v7,Body015,Body016,Body017]
  Origin = -> Origin028
  Placement = pos=(80,-1,0) rot=(0,0,1;0rad)
FEATURE [PartDesign::Pad] Pad042
  Direction = (0,0,1)
  Length = 10
  Length2 = 10
  Profile = -> Sketch021
  ReferenceAxis = -> Sketch021 [N_Axis]
  Suppressed = false
  Type = 0
FEATURE [Sketcher::SketchObject] Sketch121
  ArcFitTolerance = 1e-06
  AttachmentSupport = -> [XY_Plane077]
  FullyConstrained = true
  MakeInternals = false
  MapMode = 5
  sketch-geometry (2):
    g0: Circle CenterX=0 CenterY=118 CenterZ=0 NormalX=0 NormalY=0 NormalZ=1 AngleXU=0 Radius=87.5
    g1: Circle CenterX=0 CenterY=118 CenterZ=0 NormalX=0 NormalY=0 NormalZ=1 AngleXU=0 Radius=100
  constraints (5):
    c: Diameter(g0) = 175
    c: PointOnObject(g0,g-2)
    c: DistanceY(g-1,g0) = 118
    c: Diameter(g1) = 200
    c: Coincident(g1,g0)
FEATURE [PartDesign::Pad] Pad043
  Direction = (0,0,1)
  Length = 10
  Length2 = 10
  Profile = -> Sketch121
  ReferenceAxis = -> Sketch121 [N_Axis]
  Suppressed = false
  Type = 0
FEATURE [Sketcher::SketchObject] Sketch124
  ArcFitTolerance = 1e-06
  AttachmentSupport = -> [YZ_Plane079]
  FullyConstrained = true
  MakeInternals = false
  MapMode = 5
  Placement = pos=(0,0,0) rot=(0.57735,0.57735,0.57735;2.0944rad)
  sketch-geometry (12):
    g0: LineSegment StartX=-32 StartY=10 StartZ=0 EndX=-32 EndY=43 EndZ=0
    g1: LineSegment StartX=-32 StartY=43 StartZ=0 EndX=10 EndY=43 EndZ=0
    g2: LineSegment StartX=10 StartY=43 StartZ=0 EndX=10 EndY=10 EndZ=0
    g3: LineSegment StartX=10 StartY=10 StartZ=0 EndX=33 EndY=10 EndZ=0
    g4: LineSegment StartX=33 StartY=10 StartZ=0 EndX=33 EndY=13 EndZ=0
    g5: LineSegment StartX=33 StartY=13 StartZ=0 EndX=13 EndY=13 EndZ=0
    g6: LineSegment StartX=13 StartY=13 StartZ=0 EndX=13 EndY=46 EndZ=0
    g7: LineSegment StartX=13 StartY=46 StartZ=0 EndX=-35 EndY=46 EndZ=0
    g8: LineSegment StartX=-32 StartY=10 StartZ=0 EndX=-65 EndY=10 EndZ=0
    g9: LineSegment StartX=-65 StartY=10 StartZ=0 EndX=-65 EndY=13 EndZ=0
    g10: LineSegment StartX=-65 StartY=13 StartZ=0 EndX=-35 EndY=13 EndZ=0
    g11: LineSegment StartX=-35 StartY=13 StartZ=0 EndX=-35 EndY=46 EndZ=0
  constraints (36):
    c: Vertical(g0)
    c: Coincident(g1,g0)
    c: Horizontal(g1)
    c: Coincident(g2,g1)
    c: Vertical(g2)
    c: Coincident(g3,g2)
    c: Horizontal(g3)
    c: Coincident(g4,g3)
    c: Vertical(g4)
    c: Coincident(g5,g4)
    c: Horizontal(g5)
    c: Coincident(g6,g5)
    c: Vertical(g6)
    c: Coincident(g7,g6)
    c: Horizontal(g7)
    c: Coincident(g8,g0)
    c: Horizontal(g8)
    c: Coincident(g9,g8)
    c: Coincident(g10,g9)
    c: Horizontal(g10)
    c: Coincident(g11,g10)
    c: Coincident(g11,g7)
    c: Vertical(g11)
    c: Vertical(g9)
    c: DistanceY(g0,g0) = 33
    c: DistanceY(g-1,g8) = 10
    c: DistanceY(g0,g7) = 3
    c: DistanceX(g10,g0) = 3
    c: DistanceY(g9,g9) = 3
    c: DistanceY(g4,g4) = 3
    c: DistanceX(g2,g5) = 3
    c: DistanceX(g10,g10) = 30
    c: DistanceX(g5,g5) = 20
    c: DistanceX(g1,g1) = 42
    c: DistanceY(g-1,g3) = 10
    c: DistanceX(g-1,g2) = 10
FEATURE [Sketcher::SketchObject] Sketch125
  ArcFitTolerance = 1e-06
  AttachmentSupport = -> [Pad043]
  FullyConstrained = true
  MakeInternals = false
  MapMode = 5
  Placement = pos=(0,0,10) rot=(0,0,1;0rad)
  sketch-geometry (7):
    g0: Circle [constr] CenterX=0 CenterY=118 CenterZ=0 NormalX=0 NormalY=0 NormalZ=1 AngleXU=0 Radius=93.75
    g1: Circle CenterX=-66.2913 CenterY=51.7087 CenterZ=0 NormalX=0 NormalY=0 NormalZ=1 AngleXU=0 Radius=2
    g2: Circle CenterX=-66.2913 CenterY=184.291 CenterZ=0 NormalX=0 NormalY=0 NormalZ=1 AngleXU=0 Radius=2
    g3: Circle CenterX=66.2913 CenterY=184.291 CenterZ=0 NormalX=0 NormalY=0 NormalZ=1 AngleXU=0 Radius=2
    g4: Circle CenterX=66.2913 CenterY=51.7087 CenterZ=0 NormalX=0 NormalY=0 NormalZ=1 AngleXU=0 Radius=2
    g5: LineSegment [constr] StartX=-66.2913 StartY=51.7087 StartZ=0 EndX=66.2913 EndY=184.291 EndZ=0
    g6: LineSegment [constr] StartX=66.2913 StartY=51.7087 StartZ=0 EndX=-66.2913 EndY=184.291 EndZ=0
  constraints (19):
    c: Diameter(g0) = 187.5
    c: PointOnObject(g0,g-2)
    c: Diameter(g1) = 4
    c: PointOnObject(g1,g0)
    c: PointOnObject(g4,g0)
    c: Equal(g4,g3)
    c: Equal(g3,g2)
    c: Equal(g2,g1)
    c: Coincident(g5,g1)
    c: Coincident(g5,g3)
    c: DistanceY(g-1,g0) = 118
    c: PointOnObject(g2,g0)
    c: PointOnObject(g3,g0)
    c: Coincident(g6,g4)
    c: Coincident(g6,g2)
    c: Perpendicular(g6,g5)
    c: PointOnObject(g0,g6)
    c: PointOnObject(g0,g5)
    c: Angle(g5,g-2) = 0.785398
FEATURE [PartDesign::Hole] Hole025
  BaseFeature = -> Pad043
  CustomThreadClearance = 0
  Depth = 25
  DepthType = 0
  Diameter = 4.5
  DrillForDepth = false
  DrillPoint = 1
  DrillPointAngle = 118
  HoleCutCountersinkAngle = 90
  HoleCutCustomValues = false
  HoleCutDepth = 0
  HoleCutDiameter = 6.1
  HoleCutType = 2
  ModelThread = false
  Profile = -> Sketch125
  Suppressed = false
  Tapered = false
  TaperedAngle = 90
  ThreadClass = 0
  ThreadDepth = 25
  ThreadDepthType = 0
  ThreadDirection = 0
  ThreadFit = 0
  ThreadSize = 11
  ThreadType = 1
  Threaded = false
  UseCustomThreadClearance = false
FEATURE [PartDesign::Body] Body018  label="TurntableOuter"
  AllowCompound = false
  Group = -> [Sketch121,Pad043,Sketch125,Hole025]
  Origin = -> Origin077
  Tip = -> Hole025
FEATURE [Sketcher::SketchObject] Sketch126
  ArcFitTolerance = 1e-06
  AttachmentSupport = -> [Pad042]
  FullyConstrained = true
  MakeInternals = false
  MapMode = 5
  Placement = pos=(0,0,0) rot=(1,0,0;3.14159rad)
  sketch-geometry (7):
    g0: Circle [constr] CenterX=0 CenterY=-118 CenterZ=0 NormalX=0 NormalY=0 NormalZ=1 AngleXU=0 Radius=79.75
    g1: Circle CenterX=0 CenterY=-38.25 CenterZ=0 NormalX=0 NormalY=0 NormalZ=1 AngleXU=0 Radius=2.25
    g2: Circle CenterX=0 CenterY=-197.75 CenterZ=0 NormalX=0 NormalY=0 NormalZ=1 AngleXU=0 Radius=2.25
    g3: Circle CenterX=-79.75 CenterY=-118 CenterZ=0 NormalX=0 NormalY=0 NormalZ=1 AngleXU=0 Radius=2.25
    g4: Circle CenterX=79.75 CenterY=-118 CenterZ=0 NormalX=0 NormalY=0 NormalZ=1 AngleXU=0 Radius=2.25
    g5: LineSegment [constr] StartX=-79.75 StartY=-118 StartZ=0 EndX=79.75 EndY=-118 EndZ=0
    g6: LineSegment [constr] StartX=0 StartY=-38.25 StartZ=0 EndX=0 EndY=-197.75 EndZ=0
  constraints (19):
    c: Diameter(g0) = 159.5
    c: PointOnObject(g0,g-2)
    c: DistanceY(g0,g-1) = 118
    c: Diameter(g1) = 4.5
    c: PointOnObject(g1,g0)
    c: PointOnObject(g2,g0)
    c: Equal(g2,g1)
    c: PointOnObject(g3,g0)
    c: PointOnObject(g4,g0)
    c: Equal(g3,g4)
    c: Equal(g4,g2)
    c: Coincident(g5,g3)
    c: Coincident(g5,g4)
    c: Horizontal(g5)
    c: Coincident(g6,g1)
    c: Coincident(g6,g2)
    c: Vertical(g6)
    c: PointOnObject(g2,g-2)
    c: PointOnObject(g0,g5)
FEATURE [PartDesign::Hole] Hole026
  BaseFeature = -> Pad042
  CustomThreadClearance = 0
  Depth = 25
  DepthType = 0
  Diameter = 4.5
  DrillForDepth = false
  DrillPoint = 1
  DrillPointAngle = 118
  HoleCutCountersinkAngle = 90
  HoleCutCustomValues = false
  HoleCutDepth = 0
  HoleCutDiameter = 6.1
  HoleCutType = 2
  ModelThread = false
  Profile = -> Sketch126
  Suppressed = false
  Tapered = false
  TaperedAngle = 90
  ThreadClass = 0
  ThreadDepth = 25
  ThreadDepthType = 0
  ThreadDirection = 0
  ThreadFit = 0
  ThreadSize = 11
  ThreadType = 1
  Threaded = false
  UseCustomThreadClearance = false
FEATURE [PartDesign::Body] Body003  label="TurntableInner"
  AllowCompound = false
  Group = -> [Sketch021,Pad042,Sketch126,Hole026]
  Origin = -> Origin009
  Tip = -> Hole026
FEATURE [App::Part] Part009  label="Turntable"
  Group = -> [Body018,Body003]
  Origin = -> Origin078
  Placement = pos=(0,0,20) rot=(0,0,1;0rad)
FEATURE [Part::Feature] Part__Feature390  label="GT2 Pulley 20 Tooth (ID6mm)001"
  shape: bbox 16 x 16 x 17 mm, 133 faces (baked)
FEATURE [Part::Feature] Part__Feature391  label="socket set screw flat point_am_B18.3.6M - M3 x 0.5 x 5 Hex Socket Flat Pt. SS --S002"
  Placement = pos=(8.05,9e-16,12) rot=(0,0.826578,-0.562822;3.14159rad)
  shape: bbox 5 x 3 x 3 mm, 71 faces (baked)
FEATURE [Part::Feature] Part__Feature392  label="socket set screw flat point_am_B18.3.6M - M3 x 0.5 x 5 Hex Socket Flat Pt. SS --S003"
  Placement = pos=(0,8.05,12) rot=(0.274383,-0.274383,-0.921644;1.6523rad)
  shape: bbox 3 x 5 x 3 mm, 71 faces (baked)
FEATURE [App::Part] GT2_20_Tooth_Assy__ID_6mm_001  label="GT2 20 Tooth Assy (ID 6mm)001"
  Group = -> [Part__Feature390,Part__Feature391,Part__Feature392]
  Origin = -> Origin080
  Placement = pos=(0,-11,60) rot=(0,-1,0;3.14159rad)
FEATURE [PartDesign::Pad] Pad044
  Direction = (1,0,0)
  Length = 42
  Length2 = 10
  Placement = pos=(0,0,0) rot=(1,1,1;2.0944rad)
  Profile = -> Sketch124
  ReferenceAxis = -> Sketch124 [N_Axis]
  Suppressed = false
  Type = 0
FEATURE [Sketcher::SketchObject] Sketch127
  ArcFitTolerance = 1e-06
  AttachmentSupport = -> [Pad044]
  FullyConstrained = true
  MakeInternals = false
  MapMode = 5
  Placement = pos=(0,1.01e-14,46) rot=(0,0,-1;1.5708rad)
  sketch-geometry (9):
    g0: Circle CenterX=-4.5 CenterY=36.5 CenterZ=0 NormalX=0 NormalY=0 NormalZ=1 AngleXU=0 Radius=1.75
    g1: Circle CenterX=-4.5 CenterY=5.5 CenterZ=0 NormalX=0 NormalY=0 NormalZ=1 AngleXU=0 Radius=1.75
    g2: LineSegment [constr] StartX=-4.5 StartY=36.5 StartZ=0 EndX=26.5 EndY=36.5 EndZ=0
    g3: LineSegment [constr] StartX=26.5 StartY=36.5 StartZ=0 EndX=26.5 EndY=5.5 EndZ=0
    g4: LineSegment [constr] StartX=26.5 StartY=5.5 StartZ=0 EndX=-4.5 EndY=5.5 EndZ=0
    g5: LineSegment [constr] StartX=-4.5 StartY=5.5 StartZ=0 EndX=-4.5 EndY=36.5 EndZ=0
    g6: Circle CenterX=26.5 CenterY=36.5 CenterZ=0 NormalX=0 NormalY=0 NormalZ=1 AngleXU=0 Radius=1.75
    g7: Circle CenterX=26.5 CenterY=5.5 CenterZ=0 NormalX=0 NormalY=0 NormalZ=1 AngleXU=0 Radius=1.75
    g8: Circle CenterX=11 CenterY=21 CenterZ=0 NormalX=0 NormalY=0 NormalZ=1 AngleXU=0 Radius=11.1
  constraints (22):
    c: Diameter(g0) = 3.5
    c: Coincident(g2,g0)
    c: Horizontal(g2)
    c: Coincident(g3,g2)
    c: Vertical(g3)
    c: Coincident(g4,g3)
    c: Coincident(g4,g1)
    c: Horizontal(g4)
    c: Coincident(g5,g1)
    c: Coincident(g5,g0)
    c: Vertical(g5)
    c: Equal(g2,g3)
    c: Coincident(g6,g2)
    c: Coincident(g7,g3)
    c: Equal(g1,g7)
    c: Equal(g7,g6)
    c: Equal(g6,g0)
    c: DistanceX(g2,g2) = 31
    c: DistanceY(g-1,g0) = 36.5
    c: Symmetric(g1,g2,g8)
    c: Diameter(g8) = 22.2
    c: DistanceX(g0,g-1) = 4.5
FEATURE [PartDesign::Pocket] Pocket039
  BaseFeature = -> Pad044
  Direction = (0,0,-1)
  Length = 5
  Length2 = 5
  Placement = pos=(0,0,0) rot=(1,1,1;2.0944rad)
  Profile = -> Sketch127
  ReferenceAxis = -> Sketch127 [N_Axis]
  Suppressed = false
  Type = 1
FEATURE [Sketcher::SketchObject] Sketch128
  ArcFitTolerance = 1e-06
  AttachmentSupport = -> [Pocket039]
  FullyConstrained = true
  MakeInternals = false
  MapMode = 5
  Placement = pos=(0,2.9e-15,13) rot=(0,0,-1;1.5708rad)
  sketch-geometry (3):
    g0: LineSegment [constr] StartX=55 StartY=11 StartZ=0 EndX=55 EndY=31 EndZ=0
    g1: Circle CenterX=55 CenterY=31 CenterZ=0 NormalX=0 NormalY=0 NormalZ=1 AngleXU=0 Radius=2.5
    g2: Circle CenterX=55 CenterY=11 CenterZ=0 NormalX=0 NormalY=0 NormalZ=1 AngleXU=0 Radius=2.5
  constraints (8):
    c: Vertical(g0)
    c: Coincident(g1,g0)
    c: Equal(g2,g1)
    c: DistanceX(g-1,g0) = 55
    c: Diameter(g1) = 5
    c: DistanceY(g0,g0) = 20
    c: DistanceY(g-1,g2) = 11
    c: Coincident(g0,g2)
FEATURE [PartDesign::Hole] Hole027
  BaseFeature = -> Pocket039
  CustomThreadClearance = 0
  Depth = 25
  DepthType = 0
  Diameter = 5.5
  DrillForDepth = false
  DrillPoint = 1
  DrillPointAngle = 118
  HoleCutCountersinkAngle = 90
  HoleCutCustomValues = false
  HoleCutDepth = 0
  HoleCutDiameter = 6.1
  HoleCutType = 0
  ModelThread = false
  Placement = pos=(0,0,0) rot=(1,1,1;2.0944rad)
  Profile = -> Sketch128
  Suppressed = false
  Tapered = false
  TaperedAngle = 90
  ThreadClass = 0
  ThreadDepth = 25
  ThreadDepthType = 0
  ThreadDirection = 0
  ThreadFit = 0
  ThreadSize = 13
  ThreadType = 1
  Threaded = false
  UseCustomThreadClearance = false
FEATURE [Sketcher::SketchObject] Sketch129
  ArcFitTolerance = 1e-06
  AttachmentSupport = -> [XY_Plane081]
  FullyConstrained = true
  MakeInternals = false
  MapMode = 5
  sketch-geometry (27):
    g0: GeomPoint X=0 Y=118 Z=0
    g1: ArcOfCircle CenterX=0 CenterY=118 CenterZ=0 NormalX=0 NormalY=0 NormalZ=1 AngleXU=0 Radius=22.5 StartAngle=4.2905 EndAngle=5.13428
    g2: ArcOfCircle CenterX=-66.2913 CenterY=51.7087 CenterZ=0 NormalX=0 NormalY=0 NormalZ=1 AngleXU=0 Radius=8 StartAngle=2.3562 EndAngle=5.49779
    g3: LineSegment StartX=-9.21342 StartY=97.4729 StartZ=0 EndX=-60.6344 EndY=46.0519 EndZ=0
    g4: ArcOfCircle CenterX=-66.2912 CenterY=184.291 CenterZ=0 NormalX=0 NormalY=0 NormalZ=1 AngleXU=0 Radius=8 StartAngle=0.785398 EndAngle=3.92699
    g5: LineSegment StartX=-9.21342 StartY=138.527 StartZ=0 EndX=-60.6344 EndY=189.948 EndZ=0
    g6: ArcOfCircle CenterX=66.2912 CenterY=184.291 CenterZ=0 NormalX=0 NormalY=0 NormalZ=1 AngleXU=0 Radius=8 StartAngle=5.49779 EndAngle=8.63938
    g7: LineSegment StartX=9.21342 StartY=138.527 StartZ=0 EndX=60.6344 EndY=189.948 EndZ=0
    g8: ArcOfCircle CenterX=66.2913 CenterY=51.7087 CenterZ=0 NormalX=0 NormalY=0 NormalZ=1 AngleXU=0 Radius=8 StartAngle=3.92699 EndAngle=7.06859
    g9: LineSegment StartX=9.21342 StartY=97.4729 StartZ=0 EndX=60.6344 EndY=46.0519 EndZ=0
    g10: LineSegment StartX=-20.5271 StartY=108.787 StartZ=0 EndX=-71.9481 EndY=57.3656 EndZ=0
    g11: ArcOfCircle CenterX=0 CenterY=118 CenterZ=0 NormalX=0 NormalY=0 NormalZ=1 AngleXU=0 Radius=22.5 StartAngle=1.14891 EndAngle=1.99269
    g12: LineSegment StartX=20.5271 StartY=127.213 StartZ=0 EndX=71.9481 EndY=178.634 EndZ=0
    g13: ArcOfCircle CenterX=0 CenterY=118 CenterZ=0 NormalX=0 NormalY=0 NormalZ=1 AngleXU=0 Radius=22.5 StartAngle=5.8613 EndAngle=6.70508
    g14: ArcOfCircle CenterX=0 CenterY=118 CenterZ=0 NormalX=0 NormalY=0 NormalZ=1 AngleXU=0 Radius=22.5 StartAngle=2.7197 EndAngle=3.56348
    g15: LineSegment [constr] StartX=-20.5271 StartY=108.787 StartZ=0 EndX=9.21342 EndY=138.527 EndZ=0
    g16: LineSegment [constr] StartX=20.5271 StartY=127.213 StartZ=0 EndX=-9.21342 EndY=97.4729 EndZ=0
    g17: LineSegment [constr] StartX=-20.5271 StartY=127.213 StartZ=0 EndX=9.21342 EndY=97.4729 EndZ=0
    g18: LineSegment StartX=20.5271 StartY=108.787 StartZ=0 EndX=71.9481 EndY=57.3656 EndZ=0
    g19: LineSegment StartX=-20.5271 StartY=127.213 StartZ=0 EndX=-71.9481 EndY=178.634 EndZ=0
    g20: LineSegment [constr] StartX=-9.21342 StartY=138.527 StartZ=0 EndX=20.5271 EndY=108.787 EndZ=0
    g21: GeomPoint [constr] X=-11.3137 Y=118 Z=0
    g22: GeomPoint [constr] X=11.3137 Y=118 Z=0
    g23: GeomPoint [constr] X=1.8e-15 Y=129.314 Z=0
    g24: GeomPoint [constr] X=-2.6e-15 Y=106.686 Z=0
    g25: LineSegment [constr] StartX=1.8e-15 StartY=129.314 StartZ=0 EndX=11.3137 EndY=118 EndZ=0
    g26: LineSegment [constr] StartX=-11.3137 StartY=118 StartZ=0 EndX=1.8e-15 EndY=129.314 EndZ=0
  constraints (73):
    c: PointOnObject(g0,g-2)
    c: DistanceY(g-1,g0) = 118
    c: Diameter(g1) = 45
    c: Coincident(g1,g0)
    c: Tangent(g2,g3) = 1.5708
    c: Coincident(g2,g10) = -1.5708
    c: Coincident(g4,g19) = 1.5708
    c: Tangent(g4,g5) = -1.5708
    c: Tangent(g6,g7) = 1.5708
    c: Coincident(g6,g12) = -1.5708
    c: Coincident(g8,g18) = 1.5708
    c: Tangent(g8,g9) = -1.5708
    c: PointOnObject(g14,g10)
    c: Coincident(g1,g3)
    c: PointOnObject(g10,g13)
    c: PointOnObject(g7,g11)
    c: PointOnObject(g13,g12)
    c: PointOnObject(g11,g7)
    c: Coincident(g1,g11)
    c: PointOnObject(g12,g13)
    c: PointOnObject(g13,g18)
    c: Coincident(g1,g13)
    c: Equal(g11,g14)
    c: PointOnObject(g14,g19)
    c: Coincident(g11,g14)
    c: Coincident(g15,g10)
    c: Coincident(g15,g7)
    c: Coincident(g16,g12)
    c: Coincident(g16,g1)
    c: Coincident(g17,g14)
    c: Coincident(g17,g1)
    c: Coincident(g9,g1)
    c: PointOnObject(g18,g13)
    c: Coincident(g5,g11)
    c: PointOnObject(g19,g14)
    c: Coincident(g20,g5)
    c: Coincident(g20,g13)
    c: PointOnObject(g21,g15)
    c: Equal(g14,g1)
    c: Equal(g1,g13)
    c: PointOnObject(g21,g17)
    c: PointOnObject(g22,g20)
    c: PointOnObject(g22,g16)
    c: Symmetric(g21,g22,g0)
    c: PointOnObject(g24,g16)
    c: PointOnObject(g24,g17)
    c: Symmetric(g24,g23,g0)
    c: Radius(g4) = 8
    c: Radius(g6) = 8
    c: Radius(g2) = 8
    c: Radius(g8) = 8
    c: Equal(g5,g18)
    c: Coincident(g25,g23)
    c: Coincident(g25,g22)
    c: Coincident(g26,g21)
    c: Coincident(g26,g23)
    c: Equal(g18,g19)
    c: Equal(g25,g26)
    c: Parallel(g7,g12)
    c: Parallel(g10,g3)
    c: Parallel(g10,g7)
    c: Parallel(g19,g5)
    c: Parallel(g5,g9)
    c: Parallel(g9,g18)
    c: Perpendicular(g18,g12)
    c: Perpendicular(g20,g15)
    c: Perpendicular(g16,g17)
    c: Parallel(g12,g16)
    c: Angle(g6) = 3.14159
    c: Angle(g7,g-2) = 0.785398
    c: Distance(g0,g8) = 93.75
    c: Equal(g3,g9)
    c: Equal(g12,g18)
FEATURE [PartDesign::Pad] Pad045
  Direction = (0,0,1)
  Length = 5
  Length2 = 10
  Profile = -> Sketch129
  ReferenceAxis = -> Sketch129 [N_Axis]
  Suppressed = false
  Type = 0
FEATURE [Sketcher::SketchObject] Sketch130
  ArcFitTolerance = 1e-06
  AttachmentOffset = pos=(0,0,40) rot=(0,0,1;0rad)
  AttachmentSupport = -> [XZ_Plane079]
  FullyConstrained = true
  MakeInternals = false
  MapMode = 5
  Placement = pos=(0,-40,8.9e-15) rot=(1,0,0;1.5708rad)
  sketch-geometry (5):
    g0: LineSegment StartX=8.5 StartY=20 StartZ=0 EndX=8.5 EndY=10 EndZ=0
    g1: LineSegment StartX=8.5 StartY=10 StartZ=0 EndX=33.5 EndY=10 EndZ=0
    g2: LineSegment StartX=33.5 StartY=10 StartZ=0 EndX=33.5 EndY=20 EndZ=0
    g3: LineSegment StartX=33.5 StartY=20 StartZ=0 EndX=8.5 EndY=20 EndZ=0
    g4: GeomPoint X=21 Y=15 Z=0
  constraints (13):
    c: Coincident(g0,g1)
    c: Coincident(g1,g2)
    c: Coincident(g2,g3)
    c: Coincident(g3,g0)
    c: Vertical(g0)
    c: Vertical(g2)
    c: Horizontal(g1)
    c: Horizontal(g3)
    c: DistanceY(g-1,g1) = 10
    c: DistanceY(g2,g2) = 10
    c: DistanceX(g1,g1) = 25
    c: Symmetric(g2,g0,g4)
    c: DistanceX(g-1,g4) = 21
FEATURE [PartDesign::Pocket] Pocket040
  BaseFeature = -> Hole027
  Direction = (0,1,-2e-16)
  Length = 13
  Length2 = 5
  Placement = pos=(0,0,0) rot=(1,1,1;2.0944rad)
  Profile = -> Sketch130
  ReferenceAxis = -> Sketch130 [N_Axis]
  Suppressed = false
  Type = 0
FEATURE [PartDesign::Body] Body019  label="YMotorHolder"
  AllowCompound = false
  Group = -> [Sketch124,Pad044,Sketch127,Pocket039,Sketch128,Hole027,Sketch130,Pocket040]
  Origin = -> Origin079
  Placement = pos=(-21,0,0) rot=(0,0,1;0rad)
  Tip = -> Pocket040
FEATURE [Sketcher::SketchObject] Sketch132
  ArcFitTolerance = 1e-06
  FullyConstrained = true
  MakeInternals = false
  MapMode = 5
  Placement = pos=(0,0,6) rot=(0,0,1;0rad)
  sketch-geometry (9):
    g0: GeomPoint X=0 Y=118 Z=0
    g1: LineSegment [constr] StartX=10 StartY=128 StartZ=0 EndX=-10 EndY=128 EndZ=0
    g2: LineSegment [constr] StartX=-10 StartY=128 StartZ=0 EndX=-10 EndY=108 EndZ=0
    g3: LineSegment [constr] StartX=-10 StartY=108 StartZ=0 EndX=10 EndY=108 EndZ=0
    g4: LineSegment [constr] StartX=10 StartY=108 StartZ=0 EndX=10 EndY=128 EndZ=0
    g5: Circle CenterX=10 CenterY=128 CenterZ=0 NormalX=0 NormalY=0 NormalZ=1 AngleXU=0 Radius=2.5
    g6: Circle CenterX=10 CenterY=108 CenterZ=0 NormalX=0 NormalY=0 NormalZ=1 AngleXU=0 Radius=2.5
    g7: Circle CenterX=-10 CenterY=108 CenterZ=0 NormalX=0 NormalY=0 NormalZ=1 AngleXU=0 Radius=2.5
    g8: Circle CenterX=-10 CenterY=128 CenterZ=0 NormalX=0 NormalY=0 NormalZ=1 AngleXU=0 Radius=2.5
  constraints (21):
    c: PointOnObject(g0,g-2)
    c: DistanceY(g-1,g0) = 118
    c: Coincident(g1,g2)
    c: Coincident(g2,g3)
    c: Coincident(g3,g4)
    c: Coincident(g4,g1)
    c: Distance(g2,g4) = 20
    c: Symmetric(g1,g2,g0)
    c: Perpendicular(g4,g3)
    c: Perpendicular(g1,g2)
    c: Equal(g3,g2)
    c: Equal(g2,g1)
    c: Diameter(g5) = 5
    c: Coincident(g5,g1)
    c: Coincident(g6,g3)
    c: Coincident(g7,g2)
    c: Coincident(g8,g1)
    c: Equal(g7,g6)
    c: Equal(g6,g5)
    c: Equal(g5,g8)
    c: Angle(g-2,g4) = 0
FEATURE [PartDesign::Hole] Hole028
  BaseFeature = -> Pad045
  CustomThreadClearance = 0
  Depth = 25
  DepthType = 0
  Diameter = 5.5
  DrillForDepth = false
  DrillPoint = 1
  DrillPointAngle = 118
  HoleCutCountersinkAngle = 90
  HoleCutCustomValues = false
  HoleCutDepth = 0
  HoleCutDiameter = 6.1
  HoleCutType = 0
  ModelThread = false
  Profile = -> Sketch132
  Suppressed = false
  Tapered = false
  TaperedAngle = 90
  ThreadClass = 0
  ThreadDepth = 25
  ThreadDepthType = 0
  ThreadDirection = 0
  ThreadFit = 0
  ThreadSize = 13
  ThreadType = 1
  Threaded = false
  UseCustomThreadClearance = false
FEATURE [Sketcher::SketchObject] Sketch134
  ArcFitTolerance = 1e-06
  AttachmentSupport = -> [XY_Plane082]
  FullyConstrained = true
  MakeInternals = false
  MapMode = 5
  sketch-geometry (24):
    g0: Circle [constr] CenterX=0 CenterY=118 CenterZ=0 NormalX=0 NormalY=0 NormalZ=1 AngleXU=0 Radius=78.75
    g1: Circle [constr] CenterX=0 CenterY=118 CenterZ=0 NormalX=0 NormalY=0 NormalZ=1 AngleXU=0 Radius=30
    g2: LineSegment StartX=28.9137 StartY=126 StartZ=0 EndX=78.3426 EndY=126 EndZ=0
    g3: LineSegment StartX=28.9137 StartY=110 StartZ=0 EndX=78.3426 EndY=110 EndZ=0
    g4: LineSegment StartX=-28.9137 StartY=126 StartZ=0 EndX=-78.3426 EndY=126 EndZ=0
    g5: LineSegment StartX=-28.9137 StartY=110 StartZ=0 EndX=-78.3426 EndY=110 EndZ=0
    g6: LineSegment StartX=-8 StartY=146.914 StartZ=0 EndX=-8 EndY=196.343 EndZ=0
    g7: LineSegment StartX=8 StartY=196.343 StartZ=0 EndX=8 EndY=146.914 EndZ=0
    g8: LineSegment StartX=-8 StartY=89.0863 StartZ=0 EndX=-8 EndY=39.6574 EndZ=0
    g9: LineSegment StartX=8 StartY=89.0863 StartZ=0 EndX=8 EndY=39.6574 EndZ=0
    g10: ArcOfCircle CenterX=-4.6e-15 CenterY=196.343 CenterZ=0 NormalX=0 NormalY=0 NormalZ=1 AngleXU=0 Radius=8 StartAngle=6.28318 EndAngle=9.42478
    g11: ArcOfCircle CenterX=-78.3426 CenterY=118 CenterZ=0 NormalX=0 NormalY=0 NormalZ=1 AngleXU=0 Radius=8 StartAngle=1.5708 EndAngle=4.71239
    g12: ArcOfCircle CenterX=78.3426 CenterY=118 CenterZ=0 NormalX=0 NormalY=0 NormalZ=1 AngleXU=0 Radius=8 StartAngle=4.71239 EndAngle=7.85398
    g13: ArcOfCircle CenterX=5.6e-15 CenterY=39.6574 CenterZ=0 NormalX=0 NormalY=0 NormalZ=1 AngleXU=0 Radius=8 StartAngle=3.1416 EndAngle=6.28318
    g14: LineSegment [constr] StartX=8 StartY=89.0863 StartZ=0 EndX=8 EndY=146.914 EndZ=0
    g15: LineSegment [constr] StartX=-8 StartY=89.0863 StartZ=0 EndX=-8 EndY=146.914 EndZ=0
    g16: LineSegment [constr] StartX=-28.9137 StartY=126 StartZ=0 EndX=28.9137 EndY=126 EndZ=0
    g17: LineSegment [constr] StartX=28.9137 StartY=110 StartZ=0 EndX=-28.9137 EndY=110 EndZ=0
    g18: LineSegment [constr] StartX=28.9137 StartY=110 StartZ=0 EndX=28.9137 EndY=126 EndZ=0
    g19: LineSegment [constr] StartX=-8 StartY=146.914 StartZ=0 EndX=8 EndY=146.914 EndZ=0
    g20: ArcOfCircle CenterX=1e-15 CenterY=118 CenterZ=0 NormalX=0 NormalY=0 NormalZ=1 AngleXU=0 Radius=30 StartAngle=1.84073 EndAngle=2.87166
    g21: ArcOfCircle CenterX=1e-15 CenterY=118 CenterZ=0 NormalX=0 NormalY=0 NormalZ=1 AngleXU=0 Radius=30 StartAngle=0.269933 EndAngle=1.30086
    g22: ArcOfCircle CenterX=1.4e-15 CenterY=118 CenterZ=0 NormalX=0 NormalY=0 NormalZ=1 AngleXU=0 Radius=30 StartAngle=4.98232 EndAngle=6.01325
    g23: ArcOfCircle CenterX=2.6e-15 CenterY=118 CenterZ=0 NormalX=0 NormalY=0 NormalZ=1 AngleXU=0 Radius=30 StartAngle=3.41153 EndAngle=4.44246
  constraints (72):
    c: Diameter(g0) = 157.5
    c: PointOnObject(g0,g-2)
    c: DistanceY(g-1,g0) = 118
    c: Diameter(g1) = 60
    c: Coincident(g1,g0)
    c: PointOnObject(g2,g1)
    c: PointOnObject(g2,g0)
    c: PointOnObject(g3,g1)
    c: PointOnObject(g3,g0)
    c: PointOnObject(g4,g1)
    c: PointOnObject(g4,g0)
    c: PointOnObject(g5,g1)
    c: PointOnObject(g5,g0)
    c: PointOnObject(g6,g1)
    c: PointOnObject(g6,g0)
    c: PointOnObject(g7,g0)
    c: PointOnObject(g7,g1)
    c: PointOnObject(g8,g1)
    c: PointOnObject(g8,g0)
    c: PointOnObject(g9,g1)
    c: PointOnObject(g9,g0)
    c: Parallel(g9,g8)
    c: Parallel(g8,g6)
    c: Parallel(g6,g7)
    c: Parallel(g4,g5)
    c: Parallel(g5,g2)
    c: Parallel(g2,g3)
    c: Perpendicular(g7,g2)
    c: Coincident(g10,g6)
    c: Coincident(g10,g7)
    c: Coincident(g11,g4)
    c: Coincident(g11,g5)
    c: Coincident(g12,g2)
    c: Coincident(g12,g3)
    c: Coincident(g13,g8)
    c: Coincident(g13,g9)
    c: Equal(g11,g13)
    c: Equal(g13,g12)
    c: Equal(g12,g10)
    c: Radius(g10) = 8
    c: Coincident(g14,g9)
    c: Coincident(g14,g7)
    c: Coincident(g15,g8)
    c: Coincident(g15,g6)
    c: Parallel(g14,g15)
    c: Parallel(g15,g8)
    c: Coincident(g16,g4)
    c: Coincident(g16,g2)
    c: Coincident(g17,g3)
    c: Coincident(g17,g5)
    c: Parallel(g17,g16)
    c: Parallel(g16,g4)
    c: Coincident(g18,g3)
    c: Coincident(g18,g2)
    c: Coincident(g19,g6)
    c: Coincident(g19,g7)
    c: Equal(g19,g18)
    c: Perpendicular(g19,g18)
    c: Parallel(g19,g16)
    c: Angle(g12) = 3.14159
    c: Angle(g15,g-2) = 0
    c: Coincident(g21,g20)
    c: Coincident(g21,g7)
    c: Coincident(g21,g2)
    c: Coincident(g20,g4)
    c: Coincident(g6,g20)
    c: Coincident(g22,g3)
    c: Coincident(g22,g9)
    c: Equal(g22,g21)
    c: Coincident(g23,g5)
    c: Coincident(g23,g8)
    c: Equal(g23,g22)
FEATURE [Sketcher::SketchObject] Sketch138  label="Allignment"
  ArcFitTolerance = 1e-06
  FullyConstrained = true
  MakeInternals = false
  MapMode = 5
  Placement = pos=(0,0,5) rot=(0,0,1;0rad)
  sketch-geometry (1):
    g0: GeomPoint X=0 Y=118 Z=0
  constraints (2):
    c: DistanceY(g-1,g0) = 118
    c: PointOnObject(g0,g-2)
FEATURE [Sketcher::SketchObject] Sketch139  label="d001"
  ArcFitTolerance = 0
  AttachmentSupport = -> [XY_Plane083]
  FullyConstrained = true
  MakeInternals = false
  MapMode = 5
  sketch-geometry (12):
    g0: ArcOfCircle CenterX=0 CenterY=-118 CenterZ=0 NormalX=0 NormalY=0 NormalZ=1 AngleXU=0 Radius=30 StartAngle=2.96628 EndAngle=6.4585
    g1: ArcOfCircle CenterX=0 CenterY=11 CenterZ=0 NormalX=0 NormalY=0 NormalZ=1 AngleXU=0 Radius=7.5 StartAngle=0.175315 EndAngle=2.96628
    g2: LineSegment StartX=29.5401 StartY=-112.767 StartZ=0 EndX=7.38504 EndY=12.3081 EndZ=0
    g3: LineSegment StartX=-29.5401 StartY=-112.767 StartZ=0 EndX=-7.38504 EndY=12.3081 EndZ=0
    g4: LineSegment StartX=-1 StartY=-0.254 StartZ=0 EndX=-0.734887 EndY=-0.254 EndZ=0
    g5: ArcOfCircle CenterX=-0.734887 CenterY=-0.404 CenterZ=0 NormalX=0 NormalY=0 NormalZ=1 AngleXU=0 Radius=0.15 StartAngle=0.162302 EndAngle=1.5708
    g6: ArcOfCircle CenterX=0.4 CenterY=-0.218171 CenterZ=0 NormalX=0 NormalY=0 NormalZ=1 AngleXU=0 Radius=1 StartAngle=3.30389 EndAngle=3.68787
    g7: ArcOfCircle CenterX=0.0197626 CenterY=-0.449352 CenterZ=0 NormalX=0 NormalY=0 NormalZ=1 AngleXU=0 Radius=0.555 StartAngle=3.68787 EndAngle=4.67677
    g8: LineSegment StartX=-1 StartY=0.376 StartZ=0 EndX=3.331e-13 EndY=0.376 EndZ=0
    g9: LineSegment StartX=3.331e-13 StartY=0.376 StartZ=0 EndX=3.331e-13 EndY=-1.004 EndZ=0
    g10: LineSegment StartX=-1 StartY=0.376 StartZ=0 EndX=-1 EndY=-0.254 EndZ=0
    g11: LineSegment StartX=0 StartY=1.577e-12 StartZ=0 EndX=5.851e-13 EndY=1.577e-12 EndZ=0
  constraints (36):
    c: Tangent(g0,g3) = 1.5708
    c: Tangent(g0,g2) = -1.5708
    c: Tangent(g2,g1) = -1.5708
    c: Tangent(g3,g1) = 1.5708
    c: Horizontal(g4)
    c: Tangent(g4,g5) = 1.5708
    c: Tangent(g6,g5) = 1.5708
    c: Radius(g5) = 0.15
    c: Radius(g6) = 1
    c: Tangent(g7,g6) = -1.5708
    c: Radius(g7) = 0.555
    c: DistanceX(g7,g6) = 0.4
    c: DistanceX(g4,g7) = 1
    c: DistanceY(g7,g4) = 0.75
    c: Angle(g6) = 0.383972
    c: Horizontal(g8)
    c: Coincident(g9,g8)
    c: Coincident(g9,g7)
    c: Vertical(g9)
    c: Coincident(g10,g4)
    c: DistanceY(g7,g8) = 1.38
    c: Horizontal(g11)
    c: PointOnObject(g11,g9)
    c: DistanceY(g4,g11) = 0.254
    c: Radius(g1) = 7.5  'r1'
    c: Radius(g0) = 30  'r2'
    c: Distance(g3) = 127.023  'd1'
    c: Distance(g2) = 127.023  'd2'
    c: Coincident(g10,g8)
    c: Coincident(g11,g-1)
    c: PointOnObject(g7,g-2)
    c: Vertical(g10)
    c: PointOnObject(g1,g-2)
    c: DistanceY(g-1,g1) = 11
    c: DistanceY(g0,g-1) = 118
    c: PointOnObject(g0,g-2)
FEATURE [PartDesign::ShapeBinder] ShapeBinder001
  Support = -> [Sketch139]
  TraceSupport = false
FEATURE [PartDesign::CoordinateSystem] LCS_Part_003
  AttacherType = Attacher::AttachEngine3D
  AttachmentSupport = -> [ShapeBinder001]
  MapMode = 11
  Placement = pos=(-3.6e-15,-118,0) rot=(0,0,-1;1.74611rad)
FEATURE [PartDesign::CoordinateSystem] LCS_Part_004
  AttacherType = Attacher::AttachEngine3D
  AttachmentSupport = -> [ShapeBinder001]
  MapMode = 11
  Placement = pos=(1.6e-15,11,0) rot=(0,0,1;1.74611rad)
FEATURE [Sketcher::SketchObject] Sketch140
  ArcFitTolerance = 0
  AttachmentSupport = -> [XY_Plane083]
  ExternalGeometry = -> [ShapeBinder001]
  FullyConstrained = true
  MakeInternals = false
  MapMode = 5
  sketch-geometry (7):
    g0: ArcOfCircle CenterX=0.0197626 CenterY=-0.449352 CenterZ=0 NormalX=0 NormalY=0 NormalZ=1 AngleXU=0 Radius=0.555 StartAngle=3.68787 EndAngle=4.67677
    g1: ArcOfCircle CenterX=0.4 CenterY=-0.218171 CenterZ=0 NormalX=0 NormalY=0 NormalZ=1 AngleXU=0 Radius=1 StartAngle=3.30389 EndAngle=3.68787
    g2: ArcOfCircle CenterX=-0.734887 CenterY=-0.404 CenterZ=0 NormalX=0 NormalY=0 NormalZ=1 AngleXU=0 Radius=0.15 StartAngle=0.162302 EndAngle=1.5708
    g3: LineSegment StartX=-0.734887 StartY=-0.254 StartZ=0 EndX=-1 EndY=-0.254 EndZ=0
    g4: LineSegment StartX=-1 StartY=-0.254 StartZ=0 EndX=-1 EndY=0.376 EndZ=0
    g5: LineSegment StartX=-1 StartY=0.376 StartZ=0 EndX=1.1954e-12 EndY=0.376 EndZ=0
    g6: LineSegment StartX=1.1954e-12 StartY=0.376 StartZ=0 EndX=8.933e-13 EndY=-1.004 EndZ=0
  constraints (17):
    c: Coincident(g0,g-4)
    c: Horizontal(g0,g-5)
    c: Coincident(g0,g1)
    c: Horizontal(g1,g-6)
    c: Coincident(g1,g-5)
    c: Coincident(g0,g-4)
    c: Coincident(g2,g-6)
    c: Coincident(g2,g1)
    c: Vertical(g-7,g2)
    c: Coincident(g3,g2)
    c: Coincident(g3,g-10)
    c: Coincident(g4,g3)
    c: Coincident(g5,g-9)
    c: Coincident(g6,g5)
    c: Coincident(g6,g0)
    c: Coincident(g5,g-10)
    c: Coincident(g4,g5)
FEATURE [PartDesign::Pad] Pad047
  Direction = (0,0,1)
  Length = 6
  Length2 = 100
  Profile = -> Sketch140
  Refine = true
  Suppressed = false
  Type = 0
FEATURE [PartDesign::Mirrored] Mirrored001
  BaseFeature = -> Pad047
  MirrorPlane = -> Pad047 [Face2]
  Originals = -> [Pad047]
  Refine = true
  Suppressed = false
  TransformMode = 0
FEATURE [PartDesign::Body] Body022
  AllowCompound = false
  Group = -> [Sketch139,ShapeBinder001,Sketch140,Pad047,Mirrored001]
  Origin = -> Origin083
  Tip = -> Mirrored001
FEATURE [Part::FeaturePython] PathArray002  # WARN: FeaturePython — macro-defined, semantics opaque (R4)
  Align = true
  AlignMode = 0
  Base = -> Mirrored001
  Count = 187
  EndOffset = 0
  ExtraTranslation = (0,0,0)
  ForceVertical = true
  Fuse = false
  PathObject = -> ShapeBinder001
  StartOffset = 0
  TangentVector = (1,0,0)
  VerticalVector = (0,0,-1)
  expr: Count = (Sketch139.Constraints.d1 + Sketch139.Constraints.d2 + pi * Sketch139.Constraints.r1 + pi * Sketch139.Constraints.r2) / 2 + 1 mm
FEATURE [App::Part] Part010  label="BedBelt"
  Group = -> [PathArray002,Body022,LCS_Part_003,LCS_Part_004]
  Origin = -> Origin084
  Placement = pos=(0,0,59.5) rot=(0,0,1;3.14159rad)
FEATURE [PartDesign::Pad] Pad048
  Direction = (0,0,1)
  Length = 7
  Length2 = 10
  Profile = -> Sketch134
  ReferenceAxis = -> Sketch134 [N_Axis]
  Suppressed = false
  Type = 0
FEATURE [Sketcher::SketchObject] Sketch141
  ArcFitTolerance = 1e-06
  AttachmentSupport = -> [Hole028]
  FullyConstrained = true
  MakeInternals = false
  MapMode = 5
  Placement = pos=(0,0,5) rot=(0,0,1;0rad)
  sketch-geometry (7):
    g0: Circle [constr] CenterX=0 CenterY=118 CenterZ=0 NormalX=0 NormalY=0 NormalZ=1 AngleXU=0 Radius=93.75
    g1: Circle CenterX=-66.2913 CenterY=51.7087 CenterZ=0 NormalX=0 NormalY=0 NormalZ=1 AngleXU=0 Radius=5
    g2: Circle CenterX=66.2913 CenterY=51.7087 CenterZ=0 NormalX=0 NormalY=0 NormalZ=1 AngleXU=0 Radius=5
    g3: Circle CenterX=66.2913 CenterY=184.291 CenterZ=0 NormalX=0 NormalY=0 NormalZ=1 AngleXU=0 Radius=5
    g4: Circle CenterX=-66.2913 CenterY=184.291 CenterZ=0 NormalX=0 NormalY=0 NormalZ=1 AngleXU=0 Radius=5
    g5: LineSegment [constr] StartX=-66.2913 StartY=184.291 StartZ=0 EndX=66.2913 EndY=51.7087 EndZ=0
    g6: LineSegment [constr] StartX=-66.2913 StartY=51.7087 StartZ=0 EndX=66.2913 EndY=184.291 EndZ=0
  constraints (19):
    c: PointOnObject(g0,g-2)
    c: Diameter(g0) = 187.5
    c: PointOnObject(g1,g0)
    c: Diameter(g1) = 10
    c: PointOnObject(g2,g0)
    c: PointOnObject(g3,g0)
    c: PointOnObject(g4,g0)
    c: DistanceY(g-1,g0) = 118
    c: Coincident(g5,g4)
    c: Coincident(g5,g2)
    c: Coincident(g6,g1)
    c: Coincident(g6,g3)
    c: Perpendicular(g5,g6)
    c: PointOnObject(g0,g6)
    c: PointOnObject(g0,g5)
    c: Equal(g1,g2)
    c: Equal(g2,g3)
    c: Equal(g3,g4)
    c: Angle(g6,g-2) = 0.785398
FEATURE [PartDesign::Pad] Pad049
  BaseFeature = -> Hole028
  Direction = (0,0,1)
  Length = 5
  Length2 = 10
  Profile = -> Sketch141
  ReferenceAxis = -> Sketch141 [N_Axis]
  Suppressed = false
  Type = 0
FEATURE [Sketcher::SketchObject] Sketch136
  ArcFitTolerance = 1e-06
  AttachmentSupport = -> [Pad049]
  FullyConstrained = true
  MakeInternals = false
  MapMode = 5
  Placement = pos=(0,0,10) rot=(0,0,1;0rad)
  sketch-geometry (7):
    g0: Circle [constr] CenterX=0 CenterY=118 CenterZ=0 NormalX=0 NormalY=0 NormalZ=1 AngleXU=0 Radius=93.75
    g1: Circle CenterX=-66.2913 CenterY=184.291 CenterZ=0 NormalX=0 NormalY=0 NormalZ=1 AngleXU=0 Radius=2.8
    g2: Circle CenterX=66.2913 CenterY=184.291 CenterZ=0 NormalX=0 NormalY=0 NormalZ=1 AngleXU=0 Radius=2.8
    g3: Circle CenterX=66.2913 CenterY=51.7087 CenterZ=0 NormalX=0 NormalY=0 NormalZ=1 AngleXU=0 Radius=2.8
    g4: Circle CenterX=-66.2913 CenterY=51.7087 CenterZ=0 NormalX=0 NormalY=0 NormalZ=1 AngleXU=0 Radius=2.8
    g5: LineSegment [constr] StartX=66.2913 StartY=184.291 StartZ=0 EndX=-66.2913 EndY=51.7087 EndZ=0
    g6: LineSegment [constr] StartX=-66.2913 StartY=184.291 StartZ=0 EndX=66.2913 EndY=51.7087 EndZ=0
  constraints (18):
    c: PointOnObject(g0,g-2)
    c: DistanceY(g-1,g0) = 118
    c: Diameter(g0) = 187.5
    c: PointOnObject(g1,g0)
    c: PointOnObject(g2,g0)
    c: PointOnObject(g3,g0)
    c: PointOnObject(g4,g0)
    c: Coincident(g5,g2)
    c: Coincident(g5,g4)
    c: Coincident(g6,g1)
    c: Coincident(g6,g3)
    c: Symmetric(g4,g2,g6)
    c: Equal(g4,g1)
    c: Equal(g1,g2)
    c: Equal(g2,g3)
    c: Diameter(g2) = 5.6
    c: PointOnObject(g0,g5)
    c: Angle(g5,g-2) = 0.785398
FEATURE [PartDesign::Pocket] Pocket041
  BaseFeature = -> Pad049
  Direction = (0,0,-1)
  Length = 9.1
  Length2 = 5
  Profile = -> Sketch136
  ReferenceAxis = -> Sketch136 [N_Axis]
  Suppressed = false
  Type = 0
FEATURE [PartDesign::Body] Body020  label="TurntableOuterHolder"
  AllowCompound = false
  Group = -> [Sketch129,Pad045,Sketch132,Hole028,Sketch136,Sketch141,Pad049,Pocket041,Sketch138]
  Origin = -> Origin081
  Placement = pos=(0,0,10) rot=(0,0,1;0rad)
  Tip = -> Pocket041
FEATURE [Sketcher::SketchObject] Sketch143
  ArcFitTolerance = 1e-06
  AttachmentSupport = -> [XY_Plane085]
  FullyConstrained = true
  MakeInternals = false
  MapMode = 5
  sketch-geometry (1):
    g0: Circle CenterX=0 CenterY=118 CenterZ=0 NormalX=0 NormalY=0 NormalZ=1 AngleXU=0 Radius=30
  constraints (3):
    c: Diameter(g0) = 60
    c: PointOnObject(g0,g-2)
    c: DistanceY(g-1,g0) = 118
FEATURE [PartDesign::Body] Body023  label="BedLoopBeltObject"
  AllowCompound = false
  Group = -> [Sketch143]
  Origin = -> Origin085
  Placement = pos=(0,0,56.5) rot=(0,0,1;0rad)
FEATURE [Sketcher::SketchObject] Sketch144
  ArcFitTolerance = 1e-06
  AttachmentSupport = -> [XZ_Plane086]
  FullyConstrained = true
  MakeInternals = false
  MapMode = 5
  Placement = pos=(0,0,0) rot=(1,0,0;1.5708rad)
  sketch-geometry (17):
    g0: LineSegment StartX=-0.727916 StartY=0.059 StartZ=0 EndX=-1.125 EndY=0.059 EndZ=0
    g1: LineSegment StartX=-1.125 StartY=0.059 StartZ=0 EndX=-1.125 EndY=-0.571 EndZ=0
    g2: LineSegment StartX=-1.125 StartY=-0.571 StartZ=0 EndX=1.125 EndY=-0.571 EndZ=0
    g3: LineSegment StartX=1.125 StartY=-0.571 StartZ=0 EndX=1.125 EndY=0.059 EndZ=0
    g4: LineSegment StartX=1.125 StartY=0.059 StartZ=0 EndX=0.727916 EndY=0.059 EndZ=0
    g5: ArcOfCircle CenterX=-0.727916 CenterY=0.209 CenterZ=0 NormalX=0 NormalY=0 NormalZ=1 AngleXU=0 Radius=0.15 StartAngle=4.71239 EndAngle=6.28319
    g6: GeomPoint X=0.4 Y=0 Z=0
    g7: ArcOfCircle CenterX=0.4 CenterY=0 CenterZ=0 NormalX=0 NormalY=0 NormalZ=1 AngleXU=0 Radius=1 StartAngle=2.83303 EndAngle=2.93104
    g8: ArcOfCircle CenterX=0 CenterY=0.254 CenterZ=0 NormalX=0 NormalY=0 NormalZ=1 AngleXU=0 Radius=0.555 StartAngle=1.04187 EndAngle=3.05194
    g9: LineSegment [constr] StartX=-0.577916 StartY=0.209 StartZ=0 EndX=-0.727916 EndY=0.209 EndZ=0
    g10: GeomPoint X=-0.4 Y=0 Z=0
    g11: ArcOfCircle CenterX=-0.4 CenterY=0 CenterZ=0 NormalX=0 NormalY=0 NormalZ=1 AngleXU=0 Radius=1 StartAngle=0.210552 EndAngle=0.822954
    g12: ArcOfCircle CenterX=0.727916 CenterY=0.209 CenterZ=0 NormalX=0 NormalY=0 NormalZ=1 AngleXU=0 Radius=0.15 StartAngle=3.14159 EndAngle=4.71239
    g13: LineSegment [constr] StartX=0.727916 StartY=0.209 StartZ=0 EndX=0.577916 EndY=0.209 EndZ=0
    g14: LineSegment [constr] StartX=-0.727916 StartY=0.059 StartZ=0 EndX=-0.727916 EndY=0.209 EndZ=0
    g15: LineSegment [constr] StartX=0.727916 StartY=0.059 StartZ=0 EndX=0.727916 EndY=0.209 EndZ=0
    g16: GeomPoint [constr] X=0 Y=0.809 Z=0
  constraints (47):
    c: Horizontal(g0)
    c: Coincident(g1,g0)
    c: Coincident(g2,g1)
    c: Horizontal(g2)
    c: Coincident(g3,g2)
    c: Vertical(g3)
    c: Coincident(g4,g3)
    c: Horizontal(g4)
    c: Vertical(g1)
    c: DistanceX(g2,g2) = 2.25
    c: Equal(g0,g4)
    c: Coincident(g5,g0)
    c: Radius(g5) = 0.15
    c: PointOnObject(g6,g-1)
    c: DistanceX(g-1,g6) = 0.4
    c: Coincident(g7,g6)
    c: Coincident(g7,g5)
    c: Radius(g7) = 1
    c: PointOnObject(g8,g-2)
    c: Coincident(g8,g7)
    c: Radius(g8) = 0.555
    c: Coincident(g9,g5)
    c: Coincident(g9,g5)
    c: Horizontal(g9)
    c: PointOnObject(g10,g-1)
    c: DistanceX(g10,g-1) = 0.4
    c: Coincident(g11,g10)
    c: Coincident(g11,g8)
    c: Radius(g11) = 1
    c: Coincident(g12,g4)
    c: Coincident(g12,g11)
    c: Radius(g12) = 0.15
    c: Coincident(g13,g12)
    c: Coincident(g13,g11)
    c: Horizontal(g13)
    c: Equal(g3,g1)
    c: Coincident(g14,g0)
    c: Coincident(g14,g5)
    c: Vertical(g14)
    c: Coincident(g15,g4)
    c: Coincident(g15,g12)
    c: Vertical(g15)
    c: PointOnObject(g16,g8)
    c: PointOnObject(g16,g-2)
    c: DistanceY(g4,g16) = 0.75
    c: DistanceY(g2,g16) = 1.38
    c: DistanceY(g-1,g8) = 0.254
FEATURE [PartDesign::Pad] Pad051
  Direction = (0,-1,2e-16)
  Length = 6
  Length2 = 10
  Placement = pos=(0,0,0) rot=(1,0,0;1.5708rad)
  Profile = -> Sketch144
  ReferenceAxis = -> Sketch144 [N_Axis]
  Suppressed = false
  Type = 0
FEATURE [PartDesign::Body] Body024  label="BedBeltArrayObject"
  AllowCompound = false
  Group = -> [Sketch144,Pad051]
  Origin = -> Origin086
  Placement = pos=(0,0,0) rot=(0,0,1;3.14159rad)
  Tip = -> Pad051
FEATURE [Part::FeaturePython] PathArray003  label="BedLoopBelt"  # WARN: FeaturePython — macro-defined, semantics opaque (R4)
  Align = true
  AlignMode = 2
  Base = -> Body024
  Count = 95
  EndOffset = 0
  ExtraTranslation = (0,0,0)
  ForceVertical = false
  Fuse = true
  PathObject = -> Sketch143
  Placement = pos=(0,0,53.5) rot=(0,0,1;0rad)
  StartOffset = 0
  TangentVector = (-500,0,1)
  VerticalVector = (0,0,1)
FEATURE [Sketcher::SketchObject] Sketch145
  ArcFitTolerance = 1e-06
  FullyConstrained = true
  MakeInternals = false
  MapMode = 5
  Placement = pos=(0,0,0) rot=(1,0,0;3.14159rad)
  sketch-geometry (7):
    g0: Circle [constr] CenterX=0 CenterY=-118 CenterZ=0 NormalX=0 NormalY=0 NormalZ=1 AngleXU=0 Radius=79.75
    g1: Circle CenterX=-2.2e-15 CenterY=-38.25 CenterZ=0 NormalX=0 NormalY=0 NormalZ=1 AngleXU=0 Radius=5
    g2: Circle CenterX=2.2e-15 CenterY=-197.75 CenterZ=0 NormalX=0 NormalY=0 NormalZ=1 AngleXU=0 Radius=5
    g3: Circle CenterX=-79.75 CenterY=-118 CenterZ=0 NormalX=0 NormalY=0 NormalZ=1 AngleXU=0 Radius=5
    g4: Circle CenterX=79.75 CenterY=-118 CenterZ=0 NormalX=0 NormalY=0 NormalZ=1 AngleXU=0 Radius=5
    g5: LineSegment [constr] StartX=-79.75 StartY=-118 StartZ=0 EndX=79.75 EndY=-118 EndZ=0
    g6: LineSegment [constr] StartX=-2.2e-15 StartY=-38.25 StartZ=0 EndX=2.2e-15 EndY=-197.75 EndZ=0
  constraints (19):
    c: PointOnObject(g0,g-2)
    c: PointOnObject(g1,g0)
    c: PointOnObject(g2,g0)
    c: PointOnObject(g3,g0)
    c: PointOnObject(g4,g0)
    c: Coincident(g5,g3)
    c: Coincident(g5,g4)
    c: Coincident(g6,g1)
    c: Coincident(g6,g2)
    c: Perpendicular(g5,g6)
    c: PointOnObject(g0,g6)
    c: PointOnObject(g0,g5)
    c: Distance(g0,g-1) = 118
    c: Equal(g3,g2)
    c: Equal(g2,g4)
    c: Equal(g4,g1)
    c: Diameter(g1) = 10
    c: Angle(g6,g-2) = 0
    c: Diameter(g0) = 159.5
FEATURE [PartDesign::Pad] Pad052
  BaseFeature = -> Pad048
  Direction = (0,0,-1)
  Length = 5
  Length2 = 10
  Profile = -> Sketch145
  ReferenceAxis = -> Sketch145 [N_Axis]
  Suppressed = false
  Type = 0
FEATURE [Sketcher::SketchObject] Sketch146
  ArcFitTolerance = 1e-06
  AttachmentSupport = -> [Pad052]
  FullyConstrained = true
  MakeInternals = false
  MapMode = 5
  Placement = pos=(0,0,7) rot=(0,0,1;0rad)
  sketch-geometry (7):
    g0: Circle [constr] CenterX=0 CenterY=118 CenterZ=0 NormalX=0 NormalY=0 NormalZ=1 AngleXU=0 Radius=15
    g1: Circle CenterX=-10.6066 CenterY=128.607 CenterZ=0 NormalX=0 NormalY=0 NormalZ=1 AngleXU=0 Radius=2.3
    g2: Circle CenterX=10.6066 CenterY=128.607 CenterZ=0 NormalX=0 NormalY=0 NormalZ=1 AngleXU=0 Radius=2.3
    g3: Circle CenterX=10.6066 CenterY=107.393 CenterZ=0 NormalX=0 NormalY=0 NormalZ=1 AngleXU=0 Radius=2.3
    g4: Circle CenterX=-10.6066 CenterY=107.393 CenterZ=0 NormalX=0 NormalY=0 NormalZ=1 AngleXU=0 Radius=2.3
    g5: LineSegment [constr] StartX=10.6066 StartY=128.607 StartZ=0 EndX=-10.6066 EndY=107.393 EndZ=0
    g6: LineSegment [constr] StartX=-10.6066 StartY=128.607 StartZ=0 EndX=10.6066 EndY=107.393 EndZ=0
  constraints (19):
    c: Diameter(g0) = 30
    c: PointOnObject(g0,g-2)
    c: Diameter(g1) = 4.6
    c: PointOnObject(g1,g0)
    c: PointOnObject(g2,g0)
    c: PointOnObject(g3,g0)
    c: PointOnObject(g4,g0)
    c: Coincident(g5,g2)
    c: Coincident(g5,g4)
    c: Coincident(g6,g1)
    c: Coincident(g6,g3)
    c: PointOnObject(g0,g5)
    c: PointOnObject(g0,g6)
    c: Perpendicular(g5,g6)
    c: Equal(g3,g2)
    c: Equal(g2,g1)
    c: Equal(g1,g4)
    c: DistanceY(g-1,g0) = 118
    c: Angle(g5,g-2) = 0.785398
FEATURE [PartDesign::Pocket] Pocket042
  BaseFeature = -> Pad052
  Direction = (0,0,-1)
  Length = 5.5
  Length2 = 5
  Profile = -> Sketch146
  ReferenceAxis = -> Sketch146 [N_Axis]
  Suppressed = false
  Type = 0
FEATURE [PartDesign::Body] Body021  label="TurntableInnerPart"
  AllowCompound = false
  Group = -> [Sketch134,Pad048,Sketch145,Pad052,Sketch146,Pocket042]
  Origin = -> Origin082
  Placement = pos=(0,0,35) rot=(0,0,1;0rad)
  Tip = -> Pocket042
FEATURE [Sketcher::SketchObject] Sketch147
  ArcFitTolerance = 1e-06
  AttachmentSupport = -> [XY_Plane087]
  FullyConstrained = true
  MakeInternals = false
  MapMode = 5
  sketch-geometry (1):
    g0: Circle CenterX=0 CenterY=118 CenterZ=0 NormalX=0 NormalY=0 NormalZ=1 AngleXU=0 Radius=30
  constraints (3):
    c: Diameter(g0) = 60
    c: PointOnObject(g0,g-2)
    c: DistanceY(g-1,g0) = 118
FEATURE [PartDesign::Pad] Pad053
  Direction = (0,0,1)
  Length = 29
  Length2 = 10
  Profile = -> Sketch147
  ReferenceAxis = -> Sketch147 [N_Axis]
  Suppressed = false
  Type = 0
FEATURE [Sketcher::SketchObject] Sketch148
  ArcFitTolerance = 1e-06
  AttachmentSupport = -> [Pad053]
  FullyConstrained = true
  MakeInternals = false
  MapMode = 5
  Placement = pos=(0,0,29) rot=(0,0,1;0rad)
  sketch-geometry (27):
    g0: ArcOfCircle CenterX=0 CenterY=118 CenterZ=0 NormalX=0 NormalY=0 NormalZ=1 AngleXU=0 Radius=30 StartAngle=2.72632 EndAngle=3.55687
    g1: LineSegment StartX=-17.3249 StartY=142.492 StartZ=0 EndX=-98.9373 EndY=209.194 EndZ=0
    g2: LineSegment StartX=-27.4502 StartY=130.103 StartZ=0 EndX=-109.063 EndY=196.806 EndZ=0
    g3: LineSegment StartX=17.3249 StartY=142.492 StartZ=0 EndX=98.9373 EndY=209.194 EndZ=0
    g4: LineSegment StartX=27.4502 StartY=130.103 StartZ=0 EndX=109.063 EndY=196.806 EndZ=0
    g5: LineSegment StartX=27.4502 StartY=105.897 StartZ=0 EndX=109.063 EndY=39.1943 EndZ=0
    g6: LineSegment StartX=17.3249 StartY=93.5082 StartZ=0 EndX=98.9373 EndY=26.8057 EndZ=0
    g7: LineSegment StartX=-17.3249 StartY=93.5082 StartZ=0 EndX=-98.9373 EndY=26.8057 EndZ=0
    g8: LineSegment StartX=-27.4502 StartY=105.897 StartZ=0 EndX=-109.063 EndY=39.1943 EndZ=0
    g9: ArcOfCircle CenterX=-104 CenterY=33 CenterZ=0 NormalX=0 NormalY=0 NormalZ=1 AngleXU=0 Radius=8 StartAngle=2.256 EndAngle=5.39759
    g10: ArcOfCircle CenterX=104 CenterY=33 CenterZ=0 NormalX=0 NormalY=0 NormalZ=1 AngleXU=0 Radius=8 StartAngle=4.02718 EndAngle=7.16878
    g11: ArcOfCircle CenterX=104 CenterY=203 CenterZ=0 NormalX=0 NormalY=0 NormalZ=1 AngleXU=0 Radius=8 StartAngle=5.39759 EndAngle=8.53919
    g12: ArcOfCircle CenterX=-104 CenterY=203 CenterZ=0 NormalX=0 NormalY=0 NormalZ=1 AngleXU=0 Radius=8 StartAngle=0.885591 EndAngle=4.02718
    g13: LineSegment [constr] StartX=-27.4502 StartY=105.897 StartZ=0 EndX=17.3249 EndY=142.492 EndZ=0
    g14: LineSegment [constr] StartX=27.4502 StartY=130.103 StartZ=0 EndX=-17.3249 EndY=93.5082 EndZ=0
    g15: LineSegment [constr] StartX=-27.4502 StartY=130.103 StartZ=0 EndX=17.3249 EndY=93.5082 EndZ=0
    g16: LineSegment [constr] StartX=27.4502 StartY=105.897 StartZ=0 EndX=-17.3249 EndY=142.492 EndZ=0
    g17: GeomPoint [constr] X=-3.8e-15 Y=107.668 Z=0
    g18: GeomPoint [constr] X=3.8e-15 Y=128.332 Z=0
    g19: ArcOfCircle CenterX=0 CenterY=118 CenterZ=0 NormalX=0 NormalY=0 NormalZ=1 AngleXU=0 Radius=30 StartAngle=0.955138 EndAngle=2.18645
    g20: ArcOfCircle CenterX=0 CenterY=118 CenterZ=0 NormalX=0 NormalY=0 NormalZ=1 AngleXU=0 Radius=30 StartAngle=5.86791 EndAngle=6.69846
    g21: ArcOfCircle CenterX=0 CenterY=118 CenterZ=0 NormalX=0 NormalY=0 NormalZ=1 AngleXU=0 Radius=30 StartAngle=4.09673 EndAngle=5.32805
    g22: LineSegment [constr] StartX=-150 StartY=-7 StartZ=0 EndX=150 EndY=-7 EndZ=0
    g23: LineSegment [constr] StartX=150 StartY=-7 StartZ=0 EndX=150 EndY=243 EndZ=0
    g24: LineSegment [constr] StartX=150 StartY=243 StartZ=0 EndX=-150 EndY=243 EndZ=0
    g25: LineSegment [constr] StartX=-150 StartY=243 StartZ=0 EndX=-150 EndY=-7 EndZ=0
    g26: GeomPoint [constr] X=0 Y=118 Z=0
  constraints (79):
    c: Diameter(g0) = 60
    c: PointOnObject(g0,g-2)
    c: PointOnObject(g3,g19)
    c: PointOnObject(g5,g20)
    c: PointOnObject(g7,g21)
    c: Parallel(g8,g3)
    c: Parallel(g3,g7)
    c: Parallel(g7,g4)
    c: Parallel(g5,g6)
    c: Parallel(g6,g1)
    c: Parallel(g1,g2)
    c: DistanceY(g-1,g0) = 118
    c: Coincident(g9,g8)
    c: Coincident(g9,g7)
    c: Coincident(g10,g5)
    c: Coincident(g10,g6)
    c: Coincident(g11,g3)
    c: Coincident(g11,g4)
    c: Coincident(g12,g1)
    c: Coincident(g12,g2)
    c: Radius(g12) = 8
    c: Equal(g11,g12)
    c: Equal(g12,g9)
    c: Equal(g9,g10)
    c: Angle(g10) = 3.14159
    c: Angle(g12) = 3.14159
    c: Angle(g11) = 3.14159
    c: Angle(g9) = 3.14159
    c: Coincident(g13,g8)
    c: Coincident(g13,g3)
    c: Coincident(g14,g4)
    c: Coincident(g14,g7)
    c: Coincident(g15,g2)
    c: Coincident(g15,g6)
    c: Coincident(g16,g5)
    c: Coincident(g16,g1)
    c: Parallel(g3,g13)
    c: Parallel(g15,g2)
    c: PointOnObject(g17,g15)
    c: PointOnObject(g17,g14)
    c: PointOnObject(g18,g16)
    c: PointOnObject(g18,g13)
    c: Symmetric(g17,g18,g0)
    c: Coincident(g19,g1)
    c: Coincident(g0,g2)
    c: Equal(g0,g19)
    c: Coincident(g20,g4)
    c: PointOnObject(g19,g13)
    c: Coincident(g0,g19)
    c: Equal(g0,g20)
    c: Coincident(g21,g6)
    c: PointOnObject(g20,g5)
    c: Coincident(g0,g20)
    c: Equal(g0,g21)
    c: Coincident(g0,g8)
    c: PointOnObject(g21,g7)
    c: Coincident(g0,g21)
    c: Coincident(g22,g23)
    c: Coincident(g23,g24)
    c: Coincident(g24,g25)
    c: Coincident(g25,g22)
    c: Horizontal(g22)
    c: Horizontal(g24)
    c: Vertical(g23)
    c: Vertical(g25)
    c: Symmetric(g24,g22,g26)
    c: Distance(g23,g25) = 300
    c: Distance(g22,g24) = 250
    c: Coincident(g26,g0)
    c: Equal(g2,g1)
    c: Equal(g3,g4)
    c: Equal(g5,g6)
    c: Equal(g8,g7)
    c: DistanceX(g24,g12) = 46
    c: DistanceY(g12,g24) = 40
    c: DistanceX(g11,g23) = 46
    c: DistanceY(g11,g23) = 40
    c: DistanceX(g22,g9) = 46
    c: DistanceX(g10,g22) = 46
FEATURE [PartDesign::Pad] Pad054
  BaseFeature = -> Pad053
  Direction = (0,0,1)
  Length = 4
  Length2 = 10
  Profile = -> Sketch148
  ReferenceAxis = -> Sketch148 [N_Axis]
  Suppressed = false
  Type = 0
FEATURE [Sketcher::SketchObject] Sketch149
  ArcFitTolerance = 1e-06
  AttachmentSupport = -> [Pad054]
  FullyConstrained = true
  MakeInternals = false
  MapMode = 5
  Placement = pos=(0,0,33) rot=(0,0,1;0rad)
  sketch-geometry (7):
    g0: Circle [constr] CenterX=0 CenterY=118 CenterZ=0 NormalX=0 NormalY=0 NormalZ=1 AngleXU=0 Radius=15
    g1: Circle CenterX=10.6066 CenterY=128.607 CenterZ=0 NormalX=0 NormalY=0 NormalZ=1 AngleXU=0 Radius=4
    g2: Circle CenterX=10.6066 CenterY=107.393 CenterZ=0 NormalX=0 NormalY=0 NormalZ=1 AngleXU=0 Radius=4
    g3: Circle CenterX=-10.6066 CenterY=107.393 CenterZ=0 NormalX=0 NormalY=0 NormalZ=1 AngleXU=0 Radius=4
    g4: Circle CenterX=-10.6066 CenterY=128.607 CenterZ=0 NormalX=0 NormalY=0 NormalZ=1 AngleXU=0 Radius=4
    g5: LineSegment [constr] StartX=-10.6066 StartY=128.607 StartZ=0 EndX=10.6066 EndY=107.393 EndZ=0
    g6: LineSegment [constr] StartX=-10.6066 StartY=107.393 StartZ=0 EndX=10.6066 EndY=128.607 EndZ=0
  constraints (19):
    c: Diameter(g0) = 30
    c: PointOnObject(g0,g-2)
    c: PointOnObject(g1,g0)
    c: PointOnObject(g2,g0)
    c: PointOnObject(g3,g0)
    c: PointOnObject(g4,g0)
    c: Coincident(g5,g4)
    c: Coincident(g5,g2)
    c: Coincident(g6,g3)
    c: Coincident(g6,g1)
    c: Perpendicular(g6,g5)
    c: PointOnObject(g0,g5)
    c: PointOnObject(g0,g6)
    c: Diameter(g1) = 8
    c: Equal(g1,g2)
    c: Equal(g2,g3)
    c: Equal(g3,g4)
    c: DistanceY(g-1,g0) = 118
    c: Angle(g6,g-2) = 0.785398
FEATURE [PartDesign::Pocket] Pocket043
  BaseFeature = -> Pad054
  Direction = (0,0,-1)
  Length = 27
  Length2 = 5
  Profile = -> Sketch149
  ReferenceAxis = -> Sketch149 [N_Axis]
  Suppressed = false
  Type = 0
FEATURE [Sketcher::SketchObject] Sketch150
  ArcFitTolerance = 1e-06
  AttachmentSupport = -> [Pocket043]
  FullyConstrained = true
  MakeInternals = false
  MapMode = 5
  Placement = pos=(0,0,6) rot=(0,0,1;0rad)
  sketch-geometry (7):
    g0: Circle [constr] CenterX=0 CenterY=118 CenterZ=0 NormalX=0 NormalY=0 NormalZ=1 AngleXU=0 Radius=15
    g1: Circle CenterX=-10.6066 CenterY=128.607 CenterZ=0 NormalX=0 NormalY=0 NormalZ=1 AngleXU=0 Radius=1.5
    g2: Circle CenterX=10.6066 CenterY=128.607 CenterZ=0 NormalX=0 NormalY=0 NormalZ=1 AngleXU=0 Radius=1.5
    g3: Circle CenterX=10.6066 CenterY=107.393 CenterZ=0 NormalX=0 NormalY=0 NormalZ=1 AngleXU=0 Radius=1.5
    g4: Circle CenterX=-10.6066 CenterY=107.393 CenterZ=0 NormalX=0 NormalY=0 NormalZ=1 AngleXU=0 Radius=1.5
    g5: LineSegment [constr] StartX=-10.6066 StartY=128.607 StartZ=0 EndX=10.6066 EndY=107.393 EndZ=0
    g6: LineSegment [constr] StartX=10.6066 StartY=128.607 StartZ=0 EndX=-10.6066 EndY=107.393 EndZ=0
  constraints (19):
    c: PointOnObject(g0,g-2)
    c: Diameter(g0) = 30
    c: DistanceY(g-1,g0) = 118
    c: PointOnObject(g1,g0)
    c: PointOnObject(g2,g0)
    c: PointOnObject(g3,g0)
    c: PointOnObject(g4,g0)
    c: Diameter(g1) = 3
    c: Equal(g1,g2)
    c: Equal(g2,g3)
    c: Equal(g3,g4)
    c: Coincident(g5,g1)
    c: Coincident(g5,g3)
    c: Coincident(g6,g2)
    c: Coincident(g6,g4)
    c: Perpendicular(g6,g5)
    c: PointOnObject(g0,g5)
    c: PointOnObject(g0,g6)
    c: Angle(g6,g-2) = 0.785398
FEATURE [PartDesign::Hole] Hole029
  BaseFeature = -> Pocket043
  CustomThreadClearance = 0
  Depth = 291.363
  DepthType = 1
  Diameter = 3.4
  DrillForDepth = false
  DrillPoint = 1
  DrillPointAngle = 118
  HoleCutCountersinkAngle = 90
  HoleCutCustomValues = false
  HoleCutDepth = 0
  HoleCutDiameter = 6.1
  HoleCutType = 0
  ModelThread = false
  Profile = -> Sketch150
  Suppressed = false
  Tapered = false
  TaperedAngle = 90
  ThreadClass = 0
  ThreadDepth = 291.363
  ThreadDepthType = 0
  ThreadDirection = 0
  ThreadFit = 0
  ThreadSize = 9
  ThreadType = 1
  Threaded = false
  UseCustomThreadClearance = false
FEATURE [PartDesign::Body] Body025  label="BedHolder"
  AllowCompound = false
  Group = -> [Sketch147,Pad053,Sketch148,Pad054,Sketch149,Pocket043,Sketch150,Hole029]
  Origin = -> Origin087
  Placement = pos=(0,0,42) rot=(0,0,1;0rad)
  Tip = -> Hole029
FEATURE [Sketcher::SketchObject] Sketch151
  ArcFitTolerance = 1e-06
  AttachmentSupport = -> [XY_Plane088]
  FullyConstrained = true
  MakeInternals = false
  MapMode = 5
  sketch-geometry (5):
    g0: LineSegment StartX=-150 StartY=-125 StartZ=0 EndX=150 EndY=-125 EndZ=0
    g1: LineSegment StartX=150 StartY=-125 StartZ=0 EndX=150 EndY=125 EndZ=0
    g2: LineSegment StartX=150 StartY=125 StartZ=0 EndX=-150 EndY=125 EndZ=0
    g3: LineSegment StartX=-150 StartY=125 StartZ=0 EndX=-150 EndY=-125 EndZ=0
    g4: GeomPoint [constr] X=0 Y=0 Z=0
  constraints (12):
    c: Coincident(g0,g1)
    c: Coincident(g1,g2)
    c: Coincident(g2,g3)
    c: Coincident(g3,g0)
    c: Horizontal(g0)
    c: Horizontal(g2)
    c: Vertical(g1)
    c: Vertical(g3)
    c: Symmetric(g2,g0,g4)
    c: Distance(g1,g3) = 300
    c: Distance(g0,g2) = 250
    c: Coincident(g4,g-1)
FEATURE [PartDesign::Pad] Pad055
  Direction = (0,0,1)
  Length = 10
  Length2 = 10
  Profile = -> Sketch151
  ReferenceAxis = -> Sketch151 [N_Axis]
  Suppressed = false
  Type = 0
FEATURE [Sketcher::SketchObject] Sketch152
  ArcFitTolerance = 1e-06
  AttachmentSupport = -> [Pad055]
  FullyConstrained = true
  MakeInternals = false
  MapMode = 5
  Placement = pos=(0,0,10) rot=(0,0,1;0rad)
  sketch-geometry (14):
    g0: Circle CenterX=-104 CenterY=85 CenterZ=0 NormalX=0 NormalY=0 NormalZ=1 AngleXU=0 Radius=2.5
    g1: Circle CenterX=104 CenterY=85 CenterZ=0 NormalX=0 NormalY=0 NormalZ=1 AngleXU=0 Radius=2.5
    g2: Circle CenterX=104 CenterY=-85 CenterZ=0 NormalX=0 NormalY=0 NormalZ=1 AngleXU=0 Radius=2.5
    g3: Circle CenterX=-104 CenterY=-85 CenterZ=0 NormalX=0 NormalY=0 NormalZ=1 AngleXU=0 Radius=2.5
    g4: LineSegment [constr] StartX=-104 StartY=-85 StartZ=0 EndX=104 EndY=-85 EndZ=0
    g5: LineSegment [constr] StartX=104 StartY=-85 StartZ=0 EndX=104 EndY=85 EndZ=0
    g6: LineSegment [constr] StartX=104 StartY=85 StartZ=0 EndX=-104 EndY=85 EndZ=0
    g7: LineSegment [constr] StartX=-104 StartY=85 StartZ=0 EndX=-104 EndY=-85 EndZ=0
    g8: GeomPoint [constr] X=0 Y=0 Z=0
    g9: LineSegment [constr] StartX=-150 StartY=-125 StartZ=0 EndX=150 EndY=-125 EndZ=0
    g10: LineSegment [constr] StartX=150 StartY=-125 StartZ=0 EndX=150 EndY=125 EndZ=0
    g11: LineSegment [constr] StartX=150 StartY=125 StartZ=0 EndX=-150 EndY=125 EndZ=0
    g12: LineSegment [constr] StartX=-150 StartY=125 StartZ=0 EndX=-150 EndY=-125 EndZ=0
    g13: GeomPoint [constr] X=0 Y=0 Z=0
  constraints (32):
    c: Coincident(g4,g5)
    c: Coincident(g5,g6)
    c: Coincident(g6,g7)
    c: Coincident(g7,g4)
    c: Horizontal(g4)
    c: Horizontal(g6)
    c: Vertical(g5)
    c: Vertical(g7)
    c: Symmetric(g6,g4,g8)
    c: Coincident(g8,g-1)
    c: Coincident(g5,g1)
    c: Coincident(g3,g4)
    c: Coincident(g6,g0)
    c: Coincident(g2,g4)
    c: Equal(g0,g1)
    c: Equal(g1,g2)
    c: Equal(g2,g3)
    c: Coincident(g9,g10)
    c: Coincident(g10,g11)
    c: Coincident(g11,g12)
    c: Coincident(g12,g9)
    c: Horizontal(g9)
    c: Horizontal(g11)
    c: Vertical(g10)
    c: Vertical(g12)
    c: Symmetric(g11,g9,g13)
    c: Distance(g10,g12) = 300
    c: Distance(g9,g11) = 250
    c: Coincident(g13,g8)
    c: DistanceX(g11,g0) = 46
    c: DistanceY(g0,g11) = 40
    c: Diameter(g0) = 5
FEATURE [PartDesign::Hole] Hole030
  BaseFeature = -> Pad055
  CustomThreadClearance = 0
  Depth = 25
  DepthType = 0
  Diameter = 5.5
  DrillForDepth = false
  DrillPoint = 1
  DrillPointAngle = 118
  HoleCutCountersinkAngle = 90
  HoleCutCustomValues = false
  HoleCutDepth = 2
  HoleCutDiameter = 10.1
  HoleCutType = 2
  ModelThread = false
  Profile = -> Sketch152
  Suppressed = false
  Tapered = false
  TaperedAngle = 90
  ThreadClass = 0
  ThreadDepth = 25
  ThreadDepthType = 0
  ThreadDirection = 0
  ThreadFit = 0
  ThreadSize = 13
  ThreadType = 1
  Threaded = false
  UseCustomThreadClearance = false
FEATURE [PartDesign::Body] Body026  label="Bed"
  AllowCompound = false
  Group = -> [Sketch151,Pad055,Sketch152,Hole030]
  Origin = -> Origin088
  Placement = pos=(0,118,100) rot=(0,0,1;0rad)
  Tip = -> Hole030
FEATURE [Part::Cut] Cut001
  Base = -> Body025
  Tool = -> PathArray003
FEATURE [App::Part] Part004  label="BedAssembly"
  Group = -> [_7HS4401S_Stepper_Motor003,Part009,Body019,GT2_20_Tooth_Assy__ID_6mm_001,Body020,Part010,Body023,Body024,Body021,Body026,PathArray003,Body025,Cut001]
  Origin = -> Origin008
  Placement = pos=(80,0,0) rot=(0,0,1;0rad)
FEATURE [Part::Feature] Part__Feature393  label="12VSticker"
  Placement = pos=(-2.5,0,0) rot=(0,0,1;0rad)
  shape: bbox 15 x 108.5 x 0.005 mm, 10 faces (baked)
FEATURE [Part::Feature] Part__Feature394  label="SOLID"
  shape: bbox 198.2 x 111 x 9 mm, 128 faces (baked)
FEATURE [App::Part] LidLRS
  Group = -> [Part__Feature393,Part__Feature394]
  Origin = -> Origin090
FEATURE [Part::Feature] Part__Feature395  label="91771A849_Passivated 18-8 Stainless Steel Phillips Flat Head Screw"
  Placement = pos=(6.48853,505.412,-24.0222) rot=(1,0,0;1.5708rad)
  shape: bbox 5.667 x 5.814 x 5.667 mm, 42 faces (baked)
FEATURE [Part::Feature] Part__Feature396  label="91771A849_Passivated 18-8 Stainless Steel Phillips Flat Head Screw001"
  Placement = pos=(187.388,505.412,-24.0203) rot=(1,0,0;1.5708rad)
  shape: bbox 5.667 x 5.814 x 5.667 mm, 42 faces (baked)
FEATURE [Part::Feature] Part__Feature397  label="91771A849_Passivated 18-8 Stainless Steel Phillips Flat Head Screw002"
  Placement = pos=(6.48826,617.009,-24.0203) rot=(0,0.707107,0.707107;3.14159rad)
  shape: bbox 5.667 x 5.814 x 5.667 mm, 42 faces (baked)
FEATURE [Part::Feature] Part__Feature398  label="91771A849_Passivated 18-8 Stainless Steel Phillips Flat Head Screw003"
  Placement = pos=(111.189,613.759,-29.5222) rot=(0,0.707107,0.707107;3.14159rad)
  shape: bbox 5.667 x 5.814 x 5.667 mm, 42 faces (baked)
FEATURE [Part::Feature] Part__Feature399  label="91771A849_Passivated 18-8 Stainless Steel Phillips Flat Head Screw004"
  Placement = pos=(187.388,617.009,-24.0203) rot=(0,0.707107,0.707107;3.14159rad)
  shape: bbox 5.667 x 5.814 x 5.667 mm, 42 faces (baked)
FEATURE [Part::Feature] Part__Feature400  label="91771A849_Passivated 18-8 Stainless Steel Phillips Flat Head Screw005"
  Placement = pos=(119.389,508.662,-29.5222) rot=(1,0,0;1.5708rad)
  shape: bbox 5.667 x 5.814 x 5.667 mm, 42 faces (baked)
FEATURE [App::Part] BoxScrews
  Group = -> [Part__Feature395,Part__Feature396,Part__Feature397,Part__Feature398,Part__Feature399,Part__Feature400]
  Origin = -> Origin091
FEATURE [Part::Feature] Part__Feature401  label="90725A020_Zinc-Plated Steel High Hex Nut"
  Placement = pos=(7.38853,608.211,-48.0222) rot=(1,0,0;1.5708rad)
  shape: bbox 6.351 x 6.351 x 3.438 mm, 39 faces (baked)
FEATURE [Part::Feature] Part__Feature402  label="90725A020_Zinc-Plated Steel High Hex Nut001"
  Placement = pos=(94.8885,567.711,-48.0222) rot=(1,0,0;1.5708rad)
  shape: bbox 6.351 x 6.351 x 3.438 mm, 39 faces (baked)
FEATURE [Part::Feature] Part__Feature403  label="90725A020_Zinc-Plated Steel High Hex Nut002"
  Placement = pos=(7.38853,513.211,-48.0222) rot=(1,0,0;1.5708rad)
  shape: bbox 6.351 x 6.351 x 3.438 mm, 39 faces (baked)
FEATURE [Part::Feature] Part__Feature404  label="90725A020_Zinc-Plated Steel High Hex Nut003"
  Placement = pos=(184.889,608.211,-48.0222) rot=(1,0,0;1.5708rad)
  shape: bbox 6.351 x 6.351 x 3.438 mm, 39 faces (baked)
FEATURE [Part::Feature] Part__Feature405  label="90725A020_Zinc-Plated Steel High Hex Nut004"
  Placement = pos=(184.889,513.211,-48.0222) rot=(1,0,0;1.5708rad)
  shape: bbox 6.351 x 6.351 x 3.438 mm, 39 faces (baked)
FEATURE [App::Part] BoxNuts
  Group = -> [Part__Feature401,Part__Feature402,Part__Feature403,Part__Feature404,Part__Feature405]
  Origin = -> Origin092
FEATURE [Part::Feature] Part__Feature406  label="SOLID001"
  shape: bbox 215 x 115.5 x 30.24 mm, 301 faces (baked)
FEATURE [App::Part] BoxLRS
  Group = -> [BoxScrews,BoxNuts,Part__Feature406]
  Origin = -> Origin093
FEATURE [App::Part] CaseLRS
  Group = -> [LidLRS,BoxLRS]
  Origin = -> Origin094
  Placement = pos=(336.681,-42.156,-732.373) rot=(0,0.707107,0.707107;3.14159rad)
FEATURE [Part::Feature] Part__Feature407  label="Trimpot"
  Placement = pos=(67.3449,-43.656,-245.115) rot=(0,0.707107,0.707107;3.14159rad)
  shape: bbox 5.461 x 0.0127 x 5.944 mm, 12 faces (baked)
FEATURE [Part::Feature] Part__Feature408  label="Trimpot001"
  Placement = pos=(67.3449,-43.656,-245.115) rot=(0,0.707107,0.707107;3.14159rad)
  shape: bbox 3.837 x 0.0127 x 1.986 mm, 12 faces (baked)
FEATURE [Part::Feature] Part__Feature409  label="Trimpot002"
  Placement = pos=(67.3449,-43.656,-245.115) rot=(0,0.707107,0.707107;3.14159rad)
  shape: bbox 3.837 x 0.0127 x 1.986 mm, 12 faces (baked)
FEATURE [Part::Feature] Part__Feature410  label="Trimpot003"
  Placement = pos=(67.3449,-43.656,-245.115) rot=(0,0.707107,0.707107;3.14159rad)
  shape: bbox 6.606 x 5.057 x 6.606 mm, 34 faces (baked)
FEATURE [Part::Feature] Part__Feature411  label="Trimpot004"
  Placement = pos=(67.3449,-43.656,-245.115) rot=(0,0.707107,0.707107;3.14159rad)
  shape: bbox 7.874 x 0.7874 x 6.807 mm, 21 faces (baked)
FEATURE [Part::Feature] Part__Feature412  label="Trimpot005"
  Placement = pos=(67.3449,-43.656,-245.115) rot=(0,0.707107,0.707107;3.14159rad)
  shape: bbox 2.667 x 7.201 x 1.905 mm, 46 faces (baked)
FEATURE [Part::Feature] Part__Feature413  label="Trimpot006"
  Placement = pos=(67.3449,-43.656,-245.115) rot=(0,0.707107,0.707107;3.14159rad)
  shape: bbox 6.159 x 6.985 x 2.794 mm, 32 faces (baked)
FEATURE [Part::Feature] Part__Feature414  label="Trimpot007"
  Placement = pos=(67.3449,-43.656,-245.115) rot=(0,0.707107,0.707107;3.14159rad)
  shape: bbox 2.667 x 7.201 x 1.905 mm, 46 faces (baked)
FEATURE [App::Part] Trimpot  label="Trimpot008"
  Group = -> [Part__Feature407,Part__Feature408,Part__Feature409,Part__Feature410,Part__Feature411,Part__Feature412,Part__Feature413,Part__Feature414]
  Origin = -> Origin095
FEATURE [Part::Feature] Part__Feature415  label="Blades"
  shape: bbox 56.45 x 55.08 x 10.5 mm, 72 faces (baked)
FEATURE [Part::Feature] Part__Feature416  label="FanBreadboard"
  shape: bbox 24 x 24 x 0.5 mm, 3 faces (baked)
FEATURE [Part::Feature] Part__Feature417  label="FanBlueWire"
  shape: bbox 17.79 x 21.87 x 14.9 mm, 11 faces (baked)
FEATURE [Part::Feature] Part__Feature418  label="FanHousing"
  Placement = pos=(0.181236,-0.00331618,0.15) rot=(0,0,1;0rad)
  shape: bbox 92.78 x 92.78 x 71.02 mm, 210 faces (baked)
FEATURE [Part::Feature] Part__Feature419  label="FanRedWire"
  shape: bbox 16.77 x 20.58 x 14.9 mm, 10 faces (baked)
FEATURE [Part::Feature] Part__Feature420  label="Label"
  shape: bbox 19 x 19 x 200000 mm, 631 faces (baked)
FEATURE [Part::Feature] Part__Feature421  label="Fan Screw"
  Placement = pos=(-5.25765,-43.0894,16.7545) rot=(0.57735,-0.57735,-0.57735;2.0944rad)
  shape: bbox 6.117 x 6.117 x 10.22 mm, 92 faces (baked)
FEATURE [Part::Feature] Part__Feature422  label="Fan Screw001"
  Placement = pos=(-55.2577,-93.0894,16.7545) rot=(0.57735,-0.57735,-0.57735;2.0944rad)
  shape: bbox 6.117 x 6.117 x 10.22 mm, 92 faces (baked)
FEATURE [App::Part] Fan_60x60x15  label="Fan 60x60x15"
  Group = -> [Part__Feature415,Part__Feature416,Part__Feature417,Part__Feature418,Part__Feature419,Part__Feature420,Part__Feature421,Part__Feature422]
  Origin = -> Origin096
  Placement = pos=(359.878,-78.1826,-161.523) rot=(-0.57735,-0.57735,-0.57735;2.0944rad)
FEATURE [Part::Feature] Part__Feature423  label="Insulator"
  Placement = pos=(-0.2,3.51e-14,9.2e-15) rot=(0,0,1;0rad)
  shape: bbox 18.01 x 87.08 x 15.01 mm, 844 faces (baked)
FEATURE [Part::Feature] Part__Feature424  label="Pan Head Combination Phillips Slotted Screw"
  Placement = pos=(205.839,531.473,-39.3722) rot=(0,0,1;0rad)
  shape: bbox 9.001 x 9.001 x 9.598 mm, 229 faces (baked)
FEATURE [Part::Feature] Part__Feature425  label="Pan Head Combination Phillips Slotted Screw001"
  Placement = pos=(205.839,578.973,-39.3722) rot=(0,0,1;0rad)
  shape: bbox 9.001 x 9.001 x 9.598 mm, 229 faces (baked)
FEATURE [Part::Feature] Part__Feature426  label="Pan Head Combination Phillips Slotted Screw002"
  Placement = pos=(205.839,559.973,-39.3722) rot=(0,0,1;0rad)
  shape: bbox 9.001 x 9.001 x 9.598 mm, 229 faces (baked)
FEATURE [Part::Feature] Part__Feature427  label="Pan Head Combination Phillips Slotted Screw003"
  Placement = pos=(205.839,569.473,-39.3722) rot=(0,0,1;0rad)
  shape: bbox 9.001 x 9.001 x 9.598 mm, 229 faces (baked)
FEATURE [Part::Feature] Part__Feature428  label="Pan Head Combination Phillips Slotted Screw004"
  Placement = pos=(205.839,540.973,-39.3722) rot=(0,0,1;0rad)
  shape: bbox 9.001 x 9.001 x 9.598 mm, 229 faces (baked)
FEATURE [Part::Feature] Part__Feature429  label="Pan Head Combination Phillips Slotted Screw005"
  Placement = pos=(205.839,550.473,-39.3722) rot=(0,0,1;0rad)
  shape: bbox 9.001 x 9.001 x 9.598 mm, 229 faces (baked)
FEATURE [Part::Feature] Part__Feature430  label="Pan Head Combination Phillips Slotted Screw006"
  Placement = pos=(205.839,607.473,-39.3722) rot=(0,0,1;0rad)
  shape: bbox 9.001 x 9.001 x 9.598 mm, 229 faces (baked)
FEATURE [Part::Feature] Part__Feature431  label="Pan Head Combination Phillips Slotted Screw007"
  Placement = pos=(205.839,588.473,-39.3722) rot=(0,0,1;0rad)
  shape: bbox 9.001 x 9.001 x 9.598 mm, 229 faces (baked)
FEATURE [Part::Feature] Part__Feature432  label="Pan Head Combination Phillips Slotted Screw008"
  Placement = pos=(205.839,597.973,-39.3722) rot=(0,0,1;0rad)
  shape: bbox 9.001 x 9.001 x 9.598 mm, 229 faces (baked)
FEATURE [App::Part] Screws
  Group = -> [Part__Feature424,Part__Feature425,Part__Feature426,Part__Feature427,Part__Feature428,Part__Feature429,Part__Feature430,Part__Feature431,Part__Feature432]
  Origin = -> Origin097
FEATURE [Part::Feature] Part__Feature433  label="SquashPlate"
  Placement = pos=(406.739,438.631,41.1574) rot=(0.57735,0.57735,0.57735;2.0944rad)
  shape: bbox 9.325 x 9.002 x 11.89 mm, 108 faces (baked)
FEATURE [Part::Feature] Part__Feature434  label="SquashPlate001"
  Placement = pos=(406.739,400.631,41.1574) rot=(0.57735,0.57735,0.57735;2.0944rad)
  shape: bbox 9.325 x 9.002 x 11.89 mm, 108 faces (baked)
FEATURE [Part::Feature] Part__Feature435  label="SquashPlate002"
  Placement = pos=(406.739,448.131,41.1574) rot=(0.57735,0.57735,0.57735;2.0944rad)
  shape: bbox 9.325 x 9.002 x 11.89 mm, 108 faces (baked)
FEATURE [Part::Feature] Part__Feature436  label="SquashPlate003"
  Placement = pos=(406.739,476.631,41.1574) rot=(0.57735,0.57735,0.57735;2.0944rad)
  shape: bbox 9.325 x 9.002 x 11.89 mm, 108 faces (baked)
FEATURE [Part::Feature] Part__Feature437  label="SquashPlate004"
  Placement = pos=(406.739,457.631,41.1574) rot=(0.57735,0.57735,0.57735;2.0944rad)
  shape: bbox 9.325 x 9.002 x 11.89 mm, 108 faces (baked)
FEATURE [Part::Feature] Part__Feature438  label="SquashPlate005"
  Placement = pos=(406.739,467.131,41.1574) rot=(0.57735,0.57735,0.57735;2.0944rad)
  shape: bbox 9.325 x 9.002 x 11.89 mm, 108 faces (baked)
FEATURE [Part::Feature] Part__Feature439  label="SquashPlate006"
  Placement = pos=(406.739,429.131,41.1574) rot=(0.57735,0.57735,0.57735;2.0944rad)
  shape: bbox 9.325 x 9.002 x 11.89 mm, 108 faces (baked)
FEATURE [Part::Feature] Part__Feature440  label="SquashPlate007"
  Placement = pos=(406.739,419.631,41.1574) rot=(0.57735,0.57735,0.57735;2.0944rad)
  shape: bbox 9.325 x 9.002 x 11.89 mm, 108 faces (baked)
FEATURE [Part::Feature] Part__Feature441  label="SquashPlate008"
  Placement = pos=(406.739,410.131,41.1574) rot=(0.57735,0.57735,0.57735;2.0944rad)
  shape: bbox 9.325 x 9.002 x 11.89 mm, 108 faces (baked)
FEATURE [App::Part] Plates
  Group = -> [Part__Feature433,Part__Feature434,Part__Feature435,Part__Feature436,Part__Feature437,Part__Feature438,Part__Feature439,Part__Feature440,Part__Feature441]
  Origin = -> Origin098
FEATURE [Part::Feature] Part__Feature442  label="WasherPlate"
  Placement = pos=(336.681,808.373,42.156) rot=(0,0.707107,0.707107;3.14159rad)
  shape: bbox 15.25 x 15.25 x 0.8348 mm, 97 faces (baked)
FEATURE [Part::Feature] Part__Feature443  label="WasherPlate001"
  Placement = pos=(336.681,798.873,42.156) rot=(0,0.707107,0.707107;3.14159rad)
  shape: bbox 15.25 x 15.25 x 0.8348 mm, 97 faces (baked)
FEATURE [Part::Feature] Part__Feature444  label="WasherPlate002"
  Placement = pos=(336.681,779.873,42.156) rot=(0,0.707107,0.707107;3.14159rad)
  shape: bbox 15.25 x 15.25 x 0.8348 mm, 97 faces (baked)
FEATURE [Part::Feature] Part__Feature445  label="WasherPlate003"
  Placement = pos=(336.681,760.873,42.156) rot=(0,0.707107,0.707107;3.14159rad)
  shape: bbox 15.25 x 15.25 x 0.8348 mm, 97 faces (baked)
FEATURE [Part::Feature] Part__Feature446  label="WasherPlate004"
  Placement = pos=(336.681,770.373,42.156) rot=(0,0.707107,0.707107;3.14159rad)
  shape: bbox 15.25 x 15.25 x 0.8348 mm, 97 faces (baked)
FEATURE [Part::Feature] Part__Feature447  label="WasherPlate005"
  Placement = pos=(336.681,751.373,42.156) rot=(0,0.707107,0.707107;3.14159rad)
  shape: bbox 15.25 x 15.25 x 0.8348 mm, 97 faces (baked)
FEATURE [Part::Feature] Part__Feature448  label="WasherPlate006"
  Placement = pos=(336.681,789.373,42.156) rot=(0,0.707107,0.707107;3.14159rad)
  shape: bbox 15.25 x 15.25 x 0.8348 mm, 97 faces (baked)
FEATURE [Part::Feature] Part__Feature449  label="WasherPlate007"
  Placement = pos=(336.681,741.873,42.156) rot=(0,0.707107,0.707107;3.14159rad)
  shape: bbox 15.25 x 15.25 x 0.8348 mm, 97 faces (baked)
FEATURE [Part::Feature] Part__Feature450  label="WasherPlate008"
  Placement = pos=(336.681,732.373,42.156) rot=(0,0.707107,0.707107;3.14159rad)
  shape: bbox 15.25 x 15.25 x 0.8348 mm, 97 faces (baked)
FEATURE [App::Part] Washers
  Group = -> [Part__Feature442,Part__Feature443,Part__Feature444,Part__Feature445,Part__Feature446,Part__Feature447,Part__Feature448,Part__Feature449,Part__Feature450]
  Origin = -> Origin099
FEATURE [App::Part] TerminalRail
  Group = -> [Part__Feature423,Screws,Plates,Washers]
  Origin = -> Origin100
  Placement = pos=(337.681,-43.656,-732.373) rot=(0,0.707107,0.707107;3.14159rad)
FEATURE [Part::Feature] Part__Feature451  label="BreadBoard"
  Placement = pos=(-1.421e-13,-1.5,0) rot=(0,0,1;0rad)
  shape: bbox 213 x 1.5 x 109 mm, 23 faces (baked)
FEATURE [Part::Feature] Part__Feature452  label="LED"
  Placement = pos=(-1.421e-13,-1.5,0) rot=(0,0,1;0rad)
  shape: bbox 3.055 x 5 x 3 mm, 8 faces (baked)
FEATURE [Part::Feature] Part__Feature453  label="LED001"
  Placement = pos=(-1.421e-13,-1.5,0) rot=(0,0,1;0rad)
  shape: bbox 0.5 x 2 x 0.5 mm, 3 faces (baked)
FEATURE [Part::Feature] Part__Feature454  label="LED002"
  Placement = pos=(-1.421e-13,-1.5,0) rot=(0,0,1;0rad)
  shape: bbox 0.5 x 2 x 0.5 mm, 3 faces (baked)
FEATURE [App::Part] LED  label="LED003"
  Group = -> [Part__Feature452,Part__Feature453,Part__Feature454]
  Origin = -> Origin101
FEATURE [Part::Feature] Part__Feature455  label="92000A118_Passivated 18-8 Stainless Steel Pan Head Phillips Screw"
  Placement = pos=(-80.3777,121.193,-307.398) rot=(-5e-06,0.707107,0.707107;3.1416rad)
  shape: bbox 6.497 x 10.72 x 6.497 mm, 65 faces (baked)
FEATURE [Part::Feature] Part__Feature456  label="94241A510"
  Placement = pos=(-80.3778,128.493,-307.398) rot=(-0.577353,0.577345,0.577353;2.0944rad)
  shape: bbox 5.615 x 1.915 x 5.615 mm, 6 faces (baked)
FEATURE [Part::Feature] Part__Feature457  label="98689A112_General Purpose 18-8 Stainless Steel Washer"
  Placement = pos=(-80.3469,127.893,-307.398) rot=(1,7e-06,7e-06;1.5708rad)
  shape: bbox 6.494 x 0.6001 x 6.494 mm, 6 faces (baked)
FEATURE [App::Part] ScrewWasherAssembly
  Group = -> [Part__Feature455,Part__Feature456,Part__Feature457]
  Origin = -> Origin102
  Placement = pos=(232.137,-212.772,183.236) rot=(0,0,-1;1.4e-05rad)
FEATURE [Part::Feature] Part__Feature458  label="92000A118_Passivated 18-8 Stainless Steel Pan Head Phillips Screw001"
  Placement = pos=(-80.3777,121.193,-307.398) rot=(-5e-06,0.707107,0.707107;3.1416rad)
  shape: bbox 6.497 x 10.72 x 6.497 mm, 65 faces (baked)
FEATURE [Part::Feature] Part__Feature459  label="94241A511"
  Placement = pos=(-80.3778,128.493,-307.398) rot=(-0.577353,0.577345,0.577353;2.0944rad)
  shape: bbox 5.615 x 1.915 x 5.615 mm, 6 faces (baked)
FEATURE [Part::Feature] Part__Feature460  label="98689A112_General Purpose 18-8 Stainless Steel Washer001"
  Placement = pos=(-80.3469,127.893,-307.398) rot=(1,7e-06,7e-06;1.5708rad)
  shape: bbox 6.494 x 0.6001 x 6.494 mm, 6 faces (baked)
FEATURE [App::Part] ScrewWasherAssembly001
  Group = -> [Part__Feature458,Part__Feature459,Part__Feature460]
  Origin = -> Origin103
  Placement = pos=(232.137,-212.772,88.2358) rot=(0,0,-1;1.4e-05rad)
FEATURE [Part::Feature] Part__Feature461  label="92000A118_Passivated 18-8 Stainless Steel Pan Head Phillips Screw002"
  Placement = pos=(-80.3777,121.193,-307.398) rot=(-5e-06,0.707107,0.707107;3.1416rad)
  shape: bbox 6.497 x 10.72 x 6.497 mm, 65 faces (baked)
FEATURE [Part::Feature] Part__Feature462  label="94241A512"
  Placement = pos=(-80.3778,128.493,-307.398) rot=(-0.577353,0.577345,0.577353;2.0944rad)
  shape: bbox 5.615 x 1.915 x 5.615 mm, 6 faces (baked)
FEATURE [Part::Feature] Part__Feature463  label="98689A112_General Purpose 18-8 Stainless Steel Washer002"
  Placement = pos=(-80.3469,127.893,-307.398) rot=(1,7e-06,7e-06;1.5708rad)
  shape: bbox 6.494 x 0.6001 x 6.494 mm, 6 faces (baked)
FEATURE [App::Part] ScrewWasherAssembly002
  Group = -> [Part__Feature461,Part__Feature462,Part__Feature463]
  Origin = -> Origin104
  Placement = pos=(409.637,-212.772,183.236) rot=(0,0,-1;1.4e-05rad)
FEATURE [Part::Feature] Part__Feature464  label="92000A118_Passivated 18-8 Stainless Steel Pan Head Phillips Screw003"
  Placement = pos=(-80.3777,121.193,-307.398) rot=(-5e-06,0.707107,0.707107;3.1416rad)
  shape: bbox 6.497 x 10.72 x 6.497 mm, 65 faces (baked)
FEATURE [Part::Feature] Part__Feature465  label="94241A513"
  Placement = pos=(-80.3778,128.493,-307.398) rot=(-0.577353,0.577345,0.577353;2.0944rad)
  shape: bbox 5.615 x 1.915 x 5.615 mm, 6 faces (baked)
FEATURE [Part::Feature] Part__Feature466  label="98689A112_General Purpose 18-8 Stainless Steel Washer003"
  Placement = pos=(-80.3469,127.893,-307.398) rot=(1,7e-06,7e-06;1.5708rad)
  shape: bbox 6.494 x 0.6001 x 6.494 mm, 6 faces (baked)
FEATURE [App::Part] ScrewWasherAssembly003
  Group = -> [Part__Feature464,Part__Feature465,Part__Feature466]
  Origin = -> Origin105
  Placement = pos=(322.137,-212.772,142.736) rot=(0,0,-1;1.4e-05rad)
FEATURE [Part::Feature] Part__Feature467  label="92000A118_Passivated 18-8 Stainless Steel Pan Head Phillips Screw004"
  Placement = pos=(-80.3777,121.193,-307.398) rot=(-5e-06,0.707107,0.707107;3.1416rad)
  shape: bbox 6.497 x 10.72 x 6.497 mm, 65 faces (baked)
FEATURE [Part::Feature] Part__Feature468  label="94241A514"
  Placement = pos=(-80.3778,128.493,-307.398) rot=(-0.577353,0.577345,0.577353;2.0944rad)
  shape: bbox 5.615 x 1.915 x 5.615 mm, 6 faces (baked)
FEATURE [Part::Feature] Part__Feature469  label="98689A112_General Purpose 18-8 Stainless Steel Washer004"
  Placement = pos=(-80.3469,127.893,-307.398) rot=(1,7e-06,7e-06;1.5708rad)
  shape: bbox 6.494 x 0.6001 x 6.494 mm, 6 faces (baked)
FEATURE [App::Part] ScrewWasherAssembly004
  Group = -> [Part__Feature467,Part__Feature468,Part__Feature469]
  Origin = -> Origin106
  Placement = pos=(409.637,-212.772,88.2358) rot=(0,0,-1;1.4e-05rad)
FEATURE [App::Part] Internals
  Group = -> [Trimpot,Fan_60x60x15,TerminalRail,Part__Feature451,LED,ScrewWasherAssembly,ScrewWasherAssembly001,ScrewWasherAssembly002,ScrewWasherAssembly003,ScrewWasherAssembly004]
  Origin = -> Origin107
FEATURE [App::Part] LRS_350  label="LRS-350"
  Group = -> [CaseLRS,Internals]
  Origin = -> Origin108
  Placement = pos=(336.681,732.373,42.156) rot=(0,0.707107,0.707107;3.14159rad)
FEATURE [App::Part] LRS_350_v40  label="LRS-350 v40"
  Group = -> [LRS_350]
  Origin = -> Origin109
  Placement = pos=(469,-112,50) rot=(0,0,1;1.5708rad)
FEATURE [PartDesign::Body] Body027  label="PSUHolder"
  AllowCompound = false
  Origin = -> Origin110
FEATURE [App::Part] Part011  label="Electrics"
  Group = -> [LRS_350_v40,Body027]
  Origin = -> Origin089
